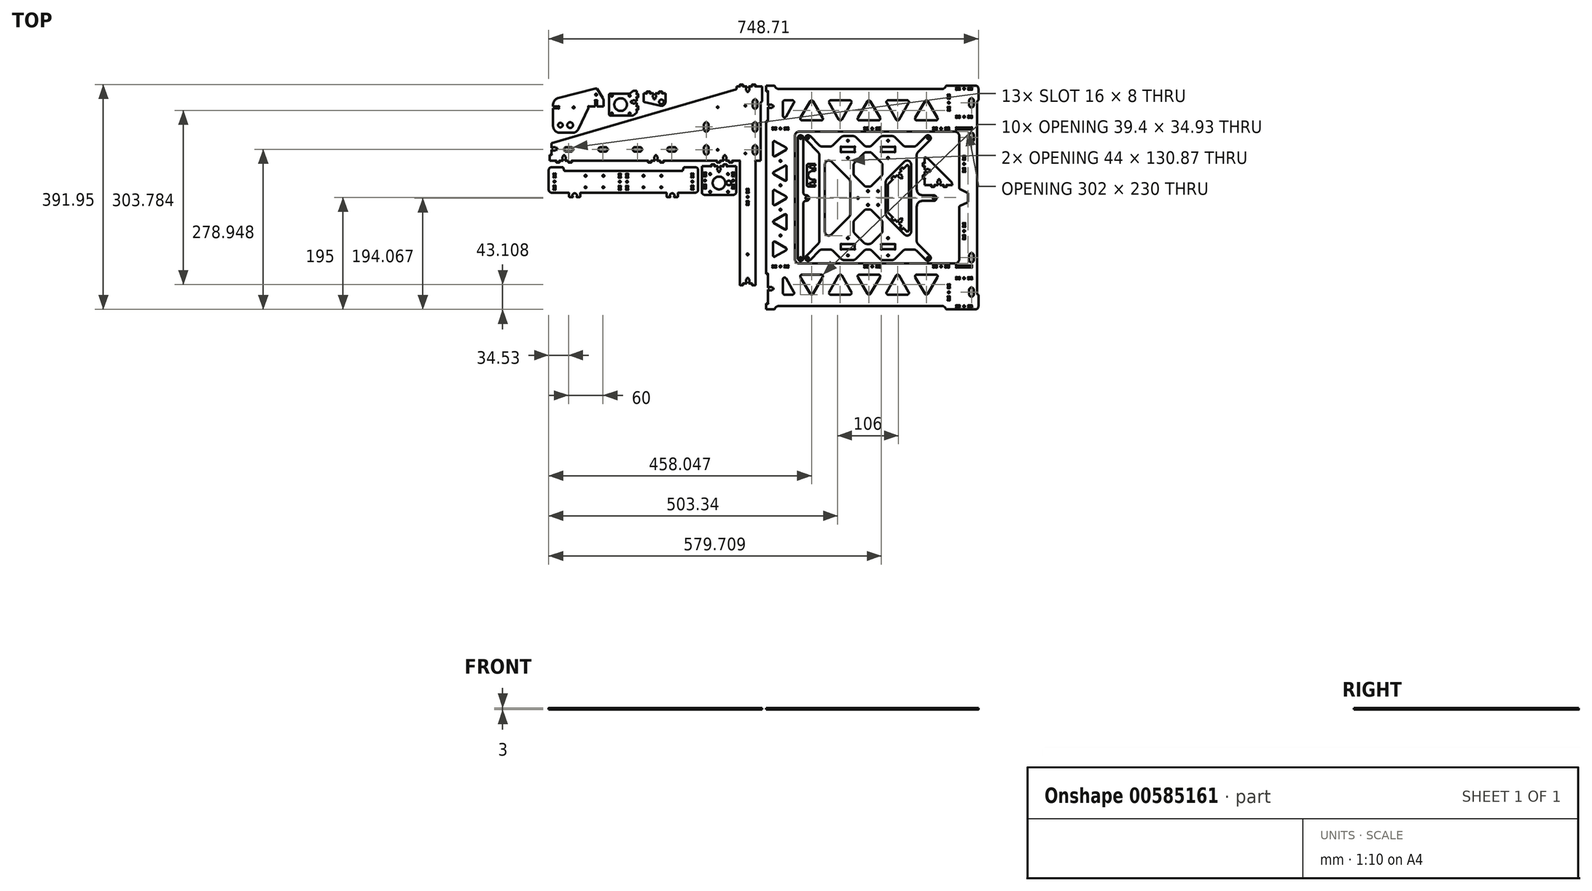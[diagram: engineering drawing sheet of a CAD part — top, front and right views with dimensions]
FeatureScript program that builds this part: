
annotation { "Feature Type Name" : "Feature", "Feature Type Description" : "" }
export const myFeature = defineFeature(function(context is Context, id is Id, definition is map)
    precondition{}
    {
        {
            assignVariable(context, id + "F0", {"name" : "thikness", "anyValue" : 3});
        }
        {
            var Q0;
            Q0=qCreatedBy(makeId("Top.planeOp"),FACE);
            var sketch = newSketch(context, id + "F1", { "sketchPlane" : qUnion([Q0])});
            skLineSegment(sketch, "E0", {"start": v(506.33, 298.49) * mm, "end": v(508.33, 300.49) * mm});
            skLineSegment(sketch, "E1", {"start": v(508.33, 300.49) * mm, "end": v(508.33, 320.49) * mm});
            skArc(sketch, "E2", {"start": v(508.33, 320.49) * mm, "mid": v(506.86, 324.03) * mm, "end": v(503.33, 325.49) * mm});
            skLineSegment(sketch, "E3", {"start": v(503.33, 325.49) * mm, "end": v(451.98, 325.49) * mm});
            skArc(sketch, "E4", {"start": v(444.23, 319.49) * mm, "mid": v(449.13, 321.17) * mm, "end": v(451.98, 325.49) * mm});
            skLineSegment(sketch, "E5", {"start": v(444.23, 319.49) * mm, "end": v(161.07, 319.49) * mm});
            skArc(sketch, "E6", {"start": v(153.33, 325.49) * mm, "mid": v(156.18, 321.17) * mm, "end": v(161.07, 319.49) * mm});
            skLineSegment(sketch, "E7", {"start": v(153.33, 325.49) * mm, "end": v(138.33, 325.49) * mm});
            skLineSegment(sketch, "E8", {"start": v(138.33, 325.49) * mm, "end": v(138.33, 315.49) * mm});
            skLineSegment(sketch, "E9", {"start": v(138.33, 315.49) * mm, "end": v(140.56, 315.49) * mm});
            skArc(sketch, "E10", {"start": v(140.56, 315.49) * mm, "mid": v(140.81, 315.56) * mm, "end": v(141, 315.74) * mm});
            skArc(sketch, "E11", {"start": v(141.68, 315.06) * mm, "mid": v(141.78, 315.84) * mm, "end": v(141, 315.74) * mm});
            skArc(sketch, "E12", {"start": v(141.68, 315.06) * mm, "mid": v(141.5, 314.87) * mm, "end": v(141.43, 314.62) * mm});
            skLineSegment(sketch, "E13", {"start": v(141.43, 314.62) * mm, "end": v(141.43, 291.26) * mm});
            skLineSegment(sketch, "E14", {"start": v(141.43, 291.26) * mm, "end": v(144.43, 291.26) * mm});
            skLineSegment(sketch, "E15", {"start": v(144.43, 291.26) * mm, "end": v(144.43, 292.54) * mm});
            skLineSegment(sketch, "E16", {"start": v(144.43, 292.54) * mm, "end": v(148.43, 292.54) * mm});
            skLineSegment(sketch, "E17", {"start": v(148.43, 292.54) * mm, "end": v(148.43, 291.26) * mm});
            skLineSegment(sketch, "E18", {"start": v(148.43, 291.26) * mm, "end": v(151.43, 291.26) * mm});
            skLineSegment(sketch, "E19", {"start": v(151.43, 291.26) * mm, "end": v(151.43, 288.06) * mm});
            skLineSegment(sketch, "E20", {"start": v(151.43, 288.06) * mm, "end": v(148.43, 288.06) * mm});
            skLineSegment(sketch, "E21", {"start": v(148.43, 288.06) * mm, "end": v(148.43, 286.79) * mm});
            skLineSegment(sketch, "E22", {"start": v(148.43, 286.79) * mm, "end": v(144.43, 286.79) * mm});
            skLineSegment(sketch, "E23", {"start": v(144.43, 286.79) * mm, "end": v(144.43, 288.06) * mm});
            skLineSegment(sketch, "E24", {"start": v(144.43, 288.06) * mm, "end": v(141.43, 288.06) * mm});
            skLineSegment(sketch, "E25", {"start": v(141.43, 288.06) * mm, "end": v(141.43, 264.7) * mm});
            skArc(sketch, "E26", {"start": v(141.43, 264.7) * mm, "mid": v(141.5, 264.46) * mm, "end": v(141.68, 264.27) * mm});
            skArc(sketch, "E27", {"start": v(141, 263.59) * mm, "mid": v(141.78, 263.49) * mm, "end": v(141.68, 264.27) * mm});
            skArc(sketch, "E28", {"start": v(141, 263.59) * mm, "mid": v(140.81, 263.77) * mm, "end": v(140.56, 263.84) * mm});
            skLineSegment(sketch, "E29", {"start": v(140.56, 263.84) * mm, "end": v(138.33, 263.84) * mm});
            skLineSegment(sketch, "E30", {"start": v(138.33, 263.84) * mm, "end": v(138.33, -2.86) * mm});
            skLineSegment(sketch, "E31", {"start": v(138.33, -2.86) * mm, "end": v(140.56, -2.86) * mm});
            skArc(sketch, "E32", {"start": v(140.56, -2.86) * mm, "mid": v(140.81, -2.8) * mm, "end": v(141, -2.61) * mm});
            skArc(sketch, "E33", {"start": v(141.68, -3.3) * mm, "mid": v(141.78, -2.5) * mm, "end": v(141, -2.61) * mm});
            skArc(sketch, "E34", {"start": v(141.68, -3.3) * mm, "mid": v(141.5, -3.48) * mm, "end": v(141.43, -3.73) * mm});
            skLineSegment(sketch, "E35", {"start": v(141.43, -3.73) * mm, "end": v(141.43, -27.09) * mm});
            skLineSegment(sketch, "E36", {"start": v(141.43, -27.09) * mm, "end": v(144.43, -27.09) * mm});
            skLineSegment(sketch, "E37", {"start": v(144.43, -27.09) * mm, "end": v(144.43, -25.81) * mm});
            skLineSegment(sketch, "E38", {"start": v(144.43, -25.81) * mm, "end": v(148.43, -25.81) * mm});
            skLineSegment(sketch, "E39", {"start": v(148.43, -25.81) * mm, "end": v(148.43, -27.09) * mm});
            skLineSegment(sketch, "E40", {"start": v(148.43, -27.09) * mm, "end": v(151.43, -27.09) * mm});
            skLineSegment(sketch, "E41", {"start": v(151.43, -27.09) * mm, "end": v(151.43, -30.29) * mm});
            skLineSegment(sketch, "E42", {"start": v(151.43, -30.29) * mm, "end": v(148.43, -30.29) * mm});
            skLineSegment(sketch, "E43", {"start": v(148.43, -30.29) * mm, "end": v(148.43, -31.56) * mm});
            skLineSegment(sketch, "E44", {"start": v(148.43, -31.56) * mm, "end": v(144.43, -31.56) * mm});
            skLineSegment(sketch, "E45", {"start": v(144.43, -31.56) * mm, "end": v(144.43, -30.29) * mm});
            skLineSegment(sketch, "E46", {"start": v(144.43, -30.29) * mm, "end": v(141.43, -30.29) * mm});
            skLineSegment(sketch, "E47", {"start": v(141.43, -30.29) * mm, "end": v(141.43, -53.64) * mm});
            skArc(sketch, "E48", {"start": v(141.43, -53.64) * mm, "mid": v(141.5, -53.9) * mm, "end": v(141.68, -54.08) * mm});
            skArc(sketch, "E49", {"start": v(141, -54.76) * mm, "mid": v(141.78, -54.86) * mm, "end": v(141.68, -54.08) * mm});
            skArc(sketch, "E50", {"start": v(141, -54.76) * mm, "mid": v(140.81, -54.58) * mm, "end": v(140.56, -54.51) * mm});
            skLineSegment(sketch, "E51", {"start": v(140.56, -54.51) * mm, "end": v(138.33, -54.51) * mm});
            skLineSegment(sketch, "E52", {"start": v(138.33, -54.51) * mm, "end": v(138.33, -64.51) * mm});
            skLineSegment(sketch, "E53", {"start": v(138.33, -64.51) * mm, "end": v(153.33, -64.51) * mm});
            skArc(sketch, "E54", {"start": v(161.07, -58.51) * mm, "mid": v(156.18, -60.19) * mm, "end": v(153.33, -64.51) * mm});
            skLineSegment(sketch, "E55", {"start": v(161.07, -58.51) * mm, "end": v(444.23, -58.51) * mm});
            skArc(sketch, "E56", {"start": v(451.98, -64.51) * mm, "mid": v(449.13, -60.19) * mm, "end": v(444.23, -58.51) * mm});
            skLineSegment(sketch, "E57", {"start": v(451.98, -64.51) * mm, "end": v(503.33, -64.51) * mm});
            skArc(sketch, "E58", {"start": v(503.33, -64.51) * mm, "mid": v(506.86, -63.05) * mm, "end": v(508.33, -59.51) * mm});
            skLineSegment(sketch, "E59", {"start": v(508.33, -59.51) * mm, "end": v(508.33, -39.51) * mm});
            skLineSegment(sketch, "E60", {"start": v(508.33, -39.51) * mm, "end": v(506.33, -37.51) * mm});
            skLineSegment(sketch, "E61", {"start": v(506.33, -37.51) * mm, "end": v(506.33, 298.49) * mm});
            skLineSegment(sketch, "E62", {"start": v(490.33, 123.77) * mm, "end": v(490.33, 137.22) * mm});
            skArc(sketch, "E63", {"start": v(490.33, 137.22) * mm, "mid": v(490.02, 138.3) * mm, "end": v(489.17, 139.03) * mm});
            skLineSegment(sketch, "E64", {"start": v(489.17, 139.03) * mm, "end": v(476.36, 145) * mm});
            skArc(sketch, "E65", {"start": v(475.2, 146.82) * mm, "mid": v(475.52, 145.74) * mm, "end": v(476.36, 145) * mm});
            skLineSegment(sketch, "E66", {"start": v(475.2, 146.82) * mm, "end": v(475.2, 237.49) * mm});
            skArc(sketch, "E67", {"start": v(475.2, 237.49) * mm, "mid": v(472.87, 243.14) * mm, "end": v(467.22, 245.49) * mm});
            skLineSegment(sketch, "E68", {"start": v(467.22, 245.49) * mm, "end": v(196.33, 245.49) * mm});
            skArc(sketch, "E69", {"start": v(196.33, 245.49) * mm, "mid": v(190.67, 243.15) * mm, "end": v(188.33, 237.49) * mm});
            skLineSegment(sketch, "E70", {"start": v(188.33, 237.49) * mm, "end": v(188.33, 23.49) * mm});
            skArc(sketch, "E71", {"start": v(188.33, 23.49) * mm, "mid": v(190.67, 17.83) * mm, "end": v(196.33, 15.49) * mm});
            skLineSegment(sketch, "E72", {"start": v(196.33, 15.49) * mm, "end": v(467.22, 15.49) * mm});
            skArc(sketch, "E73", {"start": v(467.22, 15.49) * mm, "mid": v(472.87, 17.84) * mm, "end": v(475.2, 23.49) * mm});
            skLineSegment(sketch, "E74", {"start": v(475.2, 23.49) * mm, "end": v(475.2, 114.26) * mm});
            skArc(sketch, "E75", {"start": v(476.37, 116.08) * mm, "mid": v(475.52, 115.34) * mm, "end": v(475.2, 114.26) * mm});
            skLineSegment(sketch, "E76", {"start": v(476.37, 116.08) * mm, "end": v(489.16, 121.95) * mm});
            skArc(sketch, "E77", {"start": v(489.16, 121.95) * mm, "mid": v(490.01, 122.7) * mm, "end": v(490.33, 123.77) * mm});
            skLineSegment(sketch, "E78", {"start": v(434.37, -3.94) * mm, "end": v(400.97, -3.94) * mm});
            skArc(sketch, "E79", {"start": v(400.97, -3.94) * mm, "mid": v(398.37, -5.44) * mm, "end": v(398.37, -8.44) * mm});
            skLineSegment(sketch, "E80", {"start": v(398.37, -8.44) * mm, "end": v(415.07, -37.37) * mm});
            skArc(sketch, "E81", {"start": v(415.07, -37.37) * mm, "mid": v(417.67, -38.87) * mm, "end": v(420.26, -37.37) * mm});
            skLineSegment(sketch, "E82", {"start": v(420.26, -37.37) * mm, "end": v(436.97, -8.44) * mm});
            skArc(sketch, "E83", {"start": v(436.97, -8.44) * mm, "mid": v(436.97, -5.44) * mm, "end": v(434.37, -3.94) * mm});
            skLineSegment(sketch, "E84", {"start": v(384.37, -38.87) * mm, "end": v(350.97, -38.87) * mm});
            skArc(sketch, "E85", {"start": v(348.37, -34.37) * mm, "mid": v(348.37, -37.37) * mm, "end": v(350.97, -38.87) * mm});
            skLineSegment(sketch, "E86", {"start": v(348.37, -34.37) * mm, "end": v(365.07, -5.44) * mm});
            skArc(sketch, "E87", {"start": v(370.27, -5.44) * mm, "mid": v(367.67, -3.94) * mm, "end": v(365.07, -5.44) * mm});
            skLineSegment(sketch, "E88", {"start": v(370.27, -5.44) * mm, "end": v(386.97, -34.37) * mm});
            skArc(sketch, "E89", {"start": v(384.37, -38.87) * mm, "mid": v(386.97, -37.37) * mm, "end": v(386.97, -34.37) * mm});
            skLineSegment(sketch, "E90", {"start": v(334.37, -3.94) * mm, "end": v(300.97, -3.94) * mm});
            skArc(sketch, "E91", {"start": v(300.97, -3.94) * mm, "mid": v(298.37, -5.44) * mm, "end": v(298.37, -8.44) * mm});
            skLineSegment(sketch, "E92", {"start": v(298.37, -8.44) * mm, "end": v(315.07, -37.37) * mm});
            skArc(sketch, "E93", {"start": v(315.07, -37.37) * mm, "mid": v(317.67, -38.87) * mm, "end": v(320.26, -37.37) * mm});
            skLineSegment(sketch, "E94", {"start": v(320.26, -37.37) * mm, "end": v(336.97, -8.44) * mm});
            skArc(sketch, "E95", {"start": v(336.97, -8.44) * mm, "mid": v(336.97, -5.44) * mm, "end": v(334.37, -3.94) * mm});
            skLineSegment(sketch, "E96", {"start": v(284.37, -38.87) * mm, "end": v(250.97, -38.87) * mm});
            skArc(sketch, "E97", {"start": v(248.37, -34.37) * mm, "mid": v(248.37, -37.37) * mm, "end": v(250.97, -38.87) * mm});
            skLineSegment(sketch, "E98", {"start": v(248.37, -34.37) * mm, "end": v(265.07, -5.44) * mm});
            skArc(sketch, "E99", {"start": v(270.27, -5.44) * mm, "mid": v(267.67, -3.94) * mm, "end": v(265.07, -5.44) * mm});
            skLineSegment(sketch, "E100", {"start": v(270.27, -5.44) * mm, "end": v(286.97, -34.37) * mm});
            skArc(sketch, "E101", {"start": v(284.37, -38.87) * mm, "mid": v(286.97, -37.37) * mm, "end": v(286.97, -34.37) * mm});
            skLineSegment(sketch, "E102", {"start": v(234.37, -3.94) * mm, "end": v(200.97, -3.94) * mm});
            skArc(sketch, "E103", {"start": v(200.97, -3.94) * mm, "mid": v(198.37, -5.44) * mm, "end": v(198.37, -8.44) * mm});
            skLineSegment(sketch, "E104", {"start": v(198.37, -8.44) * mm, "end": v(215.07, -37.37) * mm});
            skArc(sketch, "E105", {"start": v(215.07, -37.37) * mm, "mid": v(217.67, -38.87) * mm, "end": v(220.26, -37.37) * mm});
            skLineSegment(sketch, "E106", {"start": v(220.26, -37.37) * mm, "end": v(236.97, -8.44) * mm});
            skArc(sketch, "E107", {"start": v(236.97, -8.44) * mm, "mid": v(236.97, -5.44) * mm, "end": v(234.37, -3.94) * mm});
            skLineSegment(sketch, "E108", {"start": v(434.37, 264.92) * mm, "end": v(400.97, 264.92) * mm});
            skArc(sketch, "E109", {"start": v(398.37, 269.42) * mm, "mid": v(398.37, 266.42) * mm, "end": v(400.97, 264.92) * mm});
            skLineSegment(sketch, "E110", {"start": v(398.37, 269.42) * mm, "end": v(415.07, 298.35) * mm});
            skArc(sketch, "E111", {"start": v(420.26, 298.35) * mm, "mid": v(417.67, 299.85) * mm, "end": v(415.07, 298.35) * mm});
            skLineSegment(sketch, "E112", {"start": v(420.26, 298.35) * mm, "end": v(436.97, 269.42) * mm});
            skArc(sketch, "E113", {"start": v(434.37, 264.92) * mm, "mid": v(436.97, 266.42) * mm, "end": v(436.97, 269.42) * mm});
            skLineSegment(sketch, "E114", {"start": v(384.37, 299.85) * mm, "end": v(350.97, 299.85) * mm});
            skArc(sketch, "E115", {"start": v(350.97, 299.85) * mm, "mid": v(348.37, 298.35) * mm, "end": v(348.37, 295.35) * mm});
            skLineSegment(sketch, "E116", {"start": v(348.37, 295.35) * mm, "end": v(365.07, 266.42) * mm});
            skArc(sketch, "E117", {"start": v(365.07, 266.42) * mm, "mid": v(367.67, 264.92) * mm, "end": v(370.27, 266.42) * mm});
            skLineSegment(sketch, "E118", {"start": v(370.27, 266.42) * mm, "end": v(386.97, 295.35) * mm});
            skArc(sketch, "E119", {"start": v(386.97, 295.35) * mm, "mid": v(386.97, 298.35) * mm, "end": v(384.37, 299.85) * mm});
            skLineSegment(sketch, "E120", {"start": v(334.37, 264.92) * mm, "end": v(300.97, 264.92) * mm});
            skArc(sketch, "E121", {"start": v(298.37, 269.42) * mm, "mid": v(298.37, 266.42) * mm, "end": v(300.97, 264.92) * mm});
            skLineSegment(sketch, "E122", {"start": v(298.37, 269.42) * mm, "end": v(315.07, 298.35) * mm});
            skArc(sketch, "E123", {"start": v(320.26, 298.35) * mm, "mid": v(317.67, 299.85) * mm, "end": v(315.07, 298.35) * mm});
            skLineSegment(sketch, "E124", {"start": v(320.26, 298.35) * mm, "end": v(336.97, 269.42) * mm});
            skArc(sketch, "E125", {"start": v(334.37, 264.92) * mm, "mid": v(336.97, 266.42) * mm, "end": v(336.97, 269.42) * mm});
            skLineSegment(sketch, "E126", {"start": v(284.37, 299.85) * mm, "end": v(250.97, 299.85) * mm});
            skArc(sketch, "E127", {"start": v(250.97, 299.85) * mm, "mid": v(248.37, 298.35) * mm, "end": v(248.37, 295.35) * mm});
            skLineSegment(sketch, "E128", {"start": v(248.37, 295.35) * mm, "end": v(265.07, 266.42) * mm});
            skArc(sketch, "E129", {"start": v(265.07, 266.42) * mm, "mid": v(267.67, 264.92) * mm, "end": v(270.27, 266.42) * mm});
            skLineSegment(sketch, "E130", {"start": v(270.27, 266.42) * mm, "end": v(286.97, 295.35) * mm});
            skArc(sketch, "E131", {"start": v(286.97, 295.35) * mm, "mid": v(286.97, 298.35) * mm, "end": v(284.37, 299.85) * mm});
            skLineSegment(sketch, "E132", {"start": v(234.37, 264.92) * mm, "end": v(200.97, 264.92) * mm});
            skArc(sketch, "E133", {"start": v(198.37, 269.42) * mm, "mid": v(198.37, 266.42) * mm, "end": v(200.97, 264.92) * mm});
            skLineSegment(sketch, "E134", {"start": v(198.37, 269.42) * mm, "end": v(215.07, 298.35) * mm});
            skArc(sketch, "E135", {"start": v(220.26, 298.35) * mm, "mid": v(217.67, 299.85) * mm, "end": v(215.07, 298.35) * mm});
            skLineSegment(sketch, "E136", {"start": v(220.26, 298.35) * mm, "end": v(236.97, 269.42) * mm});
            skArc(sketch, "E137", {"start": v(234.37, 264.92) * mm, "mid": v(236.97, 266.42) * mm, "end": v(236.97, 269.42) * mm});
            skLineSegment(sketch, "E138", {"start": v(150.64, 51.7) * mm, "end": v(150.64, 29.16) * mm});
            skArc(sketch, "E139", {"start": v(150.64, 29.16) * mm, "mid": v(151.65, 27.4) * mm, "end": v(153.67, 27.4) * mm});
            skLineSegment(sketch, "E140", {"start": v(153.67, 27.4) * mm, "end": v(173.2, 38.68) * mm});
            skArc(sketch, "E141", {"start": v(173.2, 38.68) * mm, "mid": v(174.21, 40.43) * mm, "end": v(173.2, 42.19) * mm});
            skLineSegment(sketch, "E142", {"start": v(173.2, 42.19) * mm, "end": v(153.67, 53.46) * mm});
            skArc(sketch, "E143", {"start": v(153.67, 53.46) * mm, "mid": v(151.65, 53.46) * mm, "end": v(150.64, 51.7) * mm});
            skLineSegment(sketch, "E144", {"start": v(174.21, 99.25) * mm, "end": v(174.21, 76.7) * mm});
            skArc(sketch, "E145", {"start": v(171.17, 74.95) * mm, "mid": v(173.2, 74.95) * mm, "end": v(174.21, 76.7) * mm});
            skLineSegment(sketch, "E146", {"start": v(171.17, 74.95) * mm, "end": v(151.65, 86.23) * mm});
            skArc(sketch, "E147", {"start": v(151.65, 89.73) * mm, "mid": v(150.64, 87.98) * mm, "end": v(151.65, 86.23) * mm});
            skLineSegment(sketch, "E148", {"start": v(151.65, 89.73) * mm, "end": v(171.17, 101) * mm});
            skArc(sketch, "E149", {"start": v(174.21, 99.25) * mm, "mid": v(173.2, 101) * mm, "end": v(171.17, 101) * mm});
            skLineSegment(sketch, "E150", {"start": v(150.64, 141.75) * mm, "end": v(150.64, 119.2) * mm});
            skArc(sketch, "E151", {"start": v(150.64, 119.2) * mm, "mid": v(151.65, 117.45) * mm, "end": v(153.67, 117.45) * mm});
            skLineSegment(sketch, "E152", {"start": v(153.67, 117.45) * mm, "end": v(173.2, 128.73) * mm});
            skArc(sketch, "E153", {"start": v(173.2, 128.73) * mm, "mid": v(174.21, 130.48) * mm, "end": v(173.2, 132.23) * mm});
            skLineSegment(sketch, "E154", {"start": v(173.2, 132.23) * mm, "end": v(153.67, 143.5) * mm});
            skArc(sketch, "E155", {"start": v(153.67, 143.5) * mm, "mid": v(151.65, 143.5) * mm, "end": v(150.64, 141.75) * mm});
            skLineSegment(sketch, "E156", {"start": v(174.21, 184.26) * mm, "end": v(174.21, 161.72) * mm});
            skArc(sketch, "E157", {"start": v(171.17, 159.96) * mm, "mid": v(173.2, 159.96) * mm, "end": v(174.21, 161.72) * mm});
            skLineSegment(sketch, "E158", {"start": v(171.17, 159.96) * mm, "end": v(151.65, 171.24) * mm});
            skArc(sketch, "E159", {"start": v(151.65, 174.74) * mm, "mid": v(150.64, 172.99) * mm, "end": v(151.65, 171.24) * mm});
            skLineSegment(sketch, "E160", {"start": v(151.65, 174.74) * mm, "end": v(171.17, 186.02) * mm});
            skArc(sketch, "E161", {"start": v(174.21, 184.26) * mm, "mid": v(173.2, 186.02) * mm, "end": v(171.17, 186.02) * mm});
            skLineSegment(sketch, "E162", {"start": v(150.64, 226.76) * mm, "end": v(150.64, 204.22) * mm});
            skArc(sketch, "E163", {"start": v(150.64, 204.22) * mm, "mid": v(151.65, 202.46) * mm, "end": v(153.67, 202.46) * mm});
            skLineSegment(sketch, "E164", {"start": v(153.67, 202.46) * mm, "end": v(173.2, 213.74) * mm});
            skArc(sketch, "E165", {"start": v(173.2, 213.74) * mm, "mid": v(174.21, 215.49) * mm, "end": v(173.2, 217.24) * mm});
            skLineSegment(sketch, "E166", {"start": v(173.2, 217.24) * mm, "end": v(153.67, 228.52) * mm});
            skArc(sketch, "E167", {"start": v(153.67, 228.52) * mm, "mid": v(151.65, 228.52) * mm, "end": v(150.64, 226.76) * mm});
            skLineSegment(sketch, "E168", {"start": v(500.33, -38.51) * mm, "end": v(500.33, -30.51) * mm});
            skArc(sketch, "E169", {"start": v(500.33, -30.51) * mm, "mid": v(496.33, -26.51) * mm, "end": v(492.33, -30.51) * mm});
            skLineSegment(sketch, "E170", {"start": v(492.33, -30.51) * mm, "end": v(492.33, -38.51) * mm});
            skArc(sketch, "E171", {"start": v(492.33, -38.51) * mm, "mid": v(496.33, -42.51) * mm, "end": v(500.33, -38.51) * mm});
            skLineSegment(sketch, "E172", {"start": v(500.33, 21.49) * mm, "end": v(500.33, 29.49) * mm});
            skArc(sketch, "E173", {"start": v(500.33, 29.49) * mm, "mid": v(496.33, 33.49) * mm, "end": v(492.33, 29.49) * mm});
            skLineSegment(sketch, "E174", {"start": v(492.33, 29.49) * mm, "end": v(492.33, 21.49) * mm});
            skArc(sketch, "E175", {"start": v(492.33, 21.49) * mm, "mid": v(496.33, 17.49) * mm, "end": v(500.33, 21.49) * mm});
            skLineSegment(sketch, "E176", {"start": v(500.33, 231.49) * mm, "end": v(500.33, 239.49) * mm});
            skArc(sketch, "E177", {"start": v(500.33, 239.49) * mm, "mid": v(496.33, 243.49) * mm, "end": v(492.33, 239.49) * mm});
            skLineSegment(sketch, "E178", {"start": v(492.33, 239.49) * mm, "end": v(492.33, 231.49) * mm});
            skArc(sketch, "E179", {"start": v(492.33, 231.49) * mm, "mid": v(496.33, 227.49) * mm, "end": v(500.33, 231.49) * mm});
            skLineSegment(sketch, "E180", {"start": v(500.33, 291.49) * mm, "end": v(500.33, 299.49) * mm});
            skArc(sketch, "E181", {"start": v(500.33, 299.49) * mm, "mid": v(496.33, 303.49) * mm, "end": v(492.33, 299.49) * mm});
            skLineSegment(sketch, "E182", {"start": v(492.33, 299.49) * mm, "end": v(492.33, 291.49) * mm});
            skArc(sketch, "E183", {"start": v(492.33, 291.49) * mm, "mid": v(496.33, 287.49) * mm, "end": v(500.33, 291.49) * mm});
            skArc(sketch, "E184", {"start": v(469.63, 11.1) * mm, "mid": v(469.56, 11.35) * mm, "end": v(469.38, 11.53) * mm});
            skArc(sketch, "E185", {"start": v(470.06, 12.21) * mm, "mid": v(469.28, 12.32) * mm, "end": v(469.38, 11.53) * mm});
            skArc(sketch, "E186", {"start": v(470.06, 12.21) * mm, "mid": v(470.24, 12.03) * mm, "end": v(470.5, 11.96) * mm});
            skLineSegment(sketch, "E187", {"start": v(470.5, 11.96) * mm, "end": v(496.16, 11.96) * mm});
            skArc(sketch, "E188", {"start": v(496.16, 11.96) * mm, "mid": v(496.41, 12.03) * mm, "end": v(496.6, 12.21) * mm});
            skArc(sketch, "E189", {"start": v(497.28, 11.53) * mm, "mid": v(497.38, 12.32) * mm, "end": v(496.6, 12.21) * mm});
            skArc(sketch, "E190", {"start": v(497.28, 11.53) * mm, "mid": v(497.1, 11.35) * mm, "end": v(497.03, 11.1) * mm});
            skLineSegment(sketch, "E191", {"start": v(497.03, 11.1) * mm, "end": v(497.03, 9.53) * mm});
            skArc(sketch, "E192", {"start": v(497.03, 9.53) * mm, "mid": v(497.1, 9.28) * mm, "end": v(497.28, 9.1) * mm});
            skArc(sketch, "E193", {"start": v(496.6, 8.41) * mm, "mid": v(497.38, 8.31) * mm, "end": v(497.28, 9.1) * mm});
            skArc(sketch, "E194", {"start": v(496.6, 8.41) * mm, "mid": v(496.41, 8.6) * mm, "end": v(496.16, 8.66) * mm});
            skLineSegment(sketch, "E195", {"start": v(496.16, 8.66) * mm, "end": v(470.5, 8.66) * mm});
            skArc(sketch, "E196", {"start": v(470.5, 8.66) * mm, "mid": v(470.24, 8.6) * mm, "end": v(470.06, 8.41) * mm});
            skArc(sketch, "E197", {"start": v(469.38, 9.1) * mm, "mid": v(469.28, 8.31) * mm, "end": v(470.06, 8.41) * mm});
            skArc(sketch, "E198", {"start": v(469.38, 9.1) * mm, "mid": v(469.56, 9.28) * mm, "end": v(469.63, 9.53) * mm});
            skLineSegment(sketch, "E199", {"start": v(469.63, 9.53) * mm, "end": v(469.63, 11.1) * mm});
            skArc(sketch, "E200", {"start": v(469.63, 251.45) * mm, "mid": v(469.56, 251.7) * mm, "end": v(469.38, 251.88) * mm});
            skArc(sketch, "E201", {"start": v(470.06, 252.56) * mm, "mid": v(469.28, 252.67) * mm, "end": v(469.38, 251.88) * mm});
            skArc(sketch, "E202", {"start": v(470.06, 252.56) * mm, "mid": v(470.24, 252.38) * mm, "end": v(470.5, 252.31) * mm});
            skLineSegment(sketch, "E203", {"start": v(470.5, 252.31) * mm, "end": v(496.16, 252.31) * mm});
            skArc(sketch, "E204", {"start": v(496.16, 252.31) * mm, "mid": v(496.41, 252.38) * mm, "end": v(496.6, 252.56) * mm});
            skArc(sketch, "E205", {"start": v(497.28, 251.88) * mm, "mid": v(497.38, 252.67) * mm, "end": v(496.6, 252.56) * mm});
            skArc(sketch, "E206", {"start": v(497.28, 251.88) * mm, "mid": v(497.1, 251.7) * mm, "end": v(497.03, 251.45) * mm});
            skLineSegment(sketch, "E207", {"start": v(497.03, 251.45) * mm, "end": v(497.03, 249.88) * mm});
            skArc(sketch, "E208", {"start": v(497.03, 249.88) * mm, "mid": v(497.1, 249.63) * mm, "end": v(497.28, 249.45) * mm});
            skArc(sketch, "E209", {"start": v(496.6, 248.76) * mm, "mid": v(497.38, 248.66) * mm, "end": v(497.28, 249.45) * mm});
            skArc(sketch, "E210", {"start": v(496.6, 248.76) * mm, "mid": v(496.41, 248.95) * mm, "end": v(496.16, 249.01) * mm});
            skLineSegment(sketch, "E211", {"start": v(496.16, 249.01) * mm, "end": v(470.5, 249.01) * mm});
            skArc(sketch, "E212", {"start": v(470.5, 249.01) * mm, "mid": v(470.24, 248.95) * mm, "end": v(470.06, 248.76) * mm});
            skArc(sketch, "E213", {"start": v(469.38, 249.45) * mm, "mid": v(469.28, 248.66) * mm, "end": v(470.06, 248.76) * mm});
            skArc(sketch, "E214", {"start": v(469.38, 249.45) * mm, "mid": v(469.56, 249.63) * mm, "end": v(469.63, 249.88) * mm});
            skLineSegment(sketch, "E215", {"start": v(469.63, 249.88) * mm, "end": v(469.63, 251.45) * mm});
            skArc(sketch, "E216", {"start": v(490.83, -58.55) * mm, "mid": v(490.76, -58.3) * mm, "end": v(490.58, -58.11) * mm});
            skArc(sketch, "E217", {"start": v(491.26, -57.43) * mm, "mid": v(490.48, -57.33) * mm, "end": v(490.58, -58.11) * mm});
            skArc(sketch, "E218", {"start": v(491.26, -57.43) * mm, "mid": v(491.44, -57.61) * mm, "end": v(491.7, -57.68) * mm});
            skLineSegment(sketch, "E219", {"start": v(491.7, -57.68) * mm, "end": v(496.16, -57.68) * mm});
            skArc(sketch, "E220", {"start": v(496.16, -57.68) * mm, "mid": v(496.41, -57.61) * mm, "end": v(496.6, -57.43) * mm});
            skArc(sketch, "E221", {"start": v(497.28, -58.11) * mm, "mid": v(497.38, -57.33) * mm, "end": v(496.6, -57.43) * mm});
            skArc(sketch, "E222", {"start": v(497.28, -58.11) * mm, "mid": v(497.1, -58.3) * mm, "end": v(497.03, -58.55) * mm});
            skLineSegment(sketch, "E223", {"start": v(497.03, -58.55) * mm, "end": v(497.03, -60.11) * mm});
            skArc(sketch, "E224", {"start": v(497.03, -60.11) * mm, "mid": v(497.1, -60.36) * mm, "end": v(497.28, -60.55) * mm});
            skArc(sketch, "E225", {"start": v(496.6, -61.23) * mm, "mid": v(497.38, -61.33) * mm, "end": v(497.28, -60.55) * mm});
            skArc(sketch, "E226", {"start": v(496.6, -61.23) * mm, "mid": v(496.41, -61.05) * mm, "end": v(496.16, -60.98) * mm});
            skLineSegment(sketch, "E227", {"start": v(496.16, -60.98) * mm, "end": v(491.7, -60.98) * mm});
            skArc(sketch, "E228", {"start": v(491.7, -60.98) * mm, "mid": v(491.44, -61.05) * mm, "end": v(491.26, -61.23) * mm});
            skArc(sketch, "E229", {"start": v(490.58, -60.55) * mm, "mid": v(490.48, -61.33) * mm, "end": v(491.26, -61.23) * mm});
            skArc(sketch, "E230", {"start": v(490.58, -60.55) * mm, "mid": v(490.76, -60.36) * mm, "end": v(490.83, -60.11) * mm});
            skLineSegment(sketch, "E231", {"start": v(490.83, -60.11) * mm, "end": v(490.83, -58.55) * mm});
            skArc(sketch, "E232", {"start": v(469.63, -58.55) * mm, "mid": v(469.56, -58.3) * mm, "end": v(469.38, -58.11) * mm});
            skArc(sketch, "E233", {"start": v(470.06, -57.43) * mm, "mid": v(469.28, -57.33) * mm, "end": v(469.38, -58.11) * mm});
            skArc(sketch, "E234", {"start": v(470.06, -57.43) * mm, "mid": v(470.24, -57.61) * mm, "end": v(470.5, -57.68) * mm});
            skLineSegment(sketch, "E235", {"start": v(470.5, -57.68) * mm, "end": v(474.96, -57.68) * mm});
            skArc(sketch, "E236", {"start": v(474.96, -57.68) * mm, "mid": v(475.21, -57.61) * mm, "end": v(475.4, -57.43) * mm});
            skArc(sketch, "E237", {"start": v(476.08, -58.11) * mm, "mid": v(476.18, -57.33) * mm, "end": v(475.4, -57.43) * mm});
            skArc(sketch, "E238", {"start": v(476.08, -58.11) * mm, "mid": v(475.9, -58.3) * mm, "end": v(475.83, -58.55) * mm});
            skLineSegment(sketch, "E239", {"start": v(475.83, -58.55) * mm, "end": v(475.83, -60.11) * mm});
            skArc(sketch, "E240", {"start": v(475.83, -60.11) * mm, "mid": v(475.9, -60.36) * mm, "end": v(476.08, -60.55) * mm});
            skArc(sketch, "E241", {"start": v(475.4, -61.23) * mm, "mid": v(476.18, -61.33) * mm, "end": v(476.08, -60.55) * mm});
            skArc(sketch, "E242", {"start": v(475.4, -61.23) * mm, "mid": v(475.21, -61.05) * mm, "end": v(474.96, -60.98) * mm});
            skLineSegment(sketch, "E243", {"start": v(474.96, -60.98) * mm, "end": v(470.5, -60.98) * mm});
            skArc(sketch, "E244", {"start": v(470.5, -60.98) * mm, "mid": v(470.24, -61.05) * mm, "end": v(470.06, -61.23) * mm});
            skArc(sketch, "E245", {"start": v(469.38, -60.55) * mm, "mid": v(469.28, -61.33) * mm, "end": v(470.06, -61.23) * mm});
            skArc(sketch, "E246", {"start": v(469.38, -60.55) * mm, "mid": v(469.56, -60.36) * mm, "end": v(469.63, -60.11) * mm});
            skLineSegment(sketch, "E247", {"start": v(469.63, -60.11) * mm, "end": v(469.63, -58.55) * mm});
            skArc(sketch, "E248", {"start": v(455.9, -48.51) * mm, "mid": v(455.65, -48.58) * mm, "end": v(455.47, -48.76) * mm});
            skArc(sketch, "E249", {"start": v(454.78, -48.08) * mm, "mid": v(454.68, -48.86) * mm, "end": v(455.47, -48.76) * mm});
            skArc(sketch, "E250", {"start": v(454.78, -48.08) * mm, "mid": v(454.97, -47.9) * mm, "end": v(455.03, -47.64) * mm});
            skLineSegment(sketch, "E251", {"start": v(455.03, -47.64) * mm, "end": v(455.03, -43.18) * mm});
            skArc(sketch, "E252", {"start": v(455.03, -43.18) * mm, "mid": v(454.97, -42.93) * mm, "end": v(454.78, -42.74) * mm});
            skArc(sketch, "E253", {"start": v(455.47, -42.06) * mm, "mid": v(454.68, -41.96) * mm, "end": v(454.78, -42.74) * mm});
            skArc(sketch, "E254", {"start": v(455.47, -42.06) * mm, "mid": v(455.65, -42.24) * mm, "end": v(455.9, -42.31) * mm});
            skLineSegment(sketch, "E255", {"start": v(455.9, -42.31) * mm, "end": v(457.47, -42.31) * mm});
            skArc(sketch, "E256", {"start": v(457.47, -42.31) * mm, "mid": v(457.72, -42.24) * mm, "end": v(457.9, -42.06) * mm});
            skArc(sketch, "E257", {"start": v(458.58, -42.74) * mm, "mid": v(458.69, -41.96) * mm, "end": v(457.9, -42.06) * mm});
            skArc(sketch, "E258", {"start": v(458.58, -42.74) * mm, "mid": v(458.4, -42.93) * mm, "end": v(458.33, -43.18) * mm});
            skLineSegment(sketch, "E259", {"start": v(458.33, -43.18) * mm, "end": v(458.33, -47.64) * mm});
            skArc(sketch, "E260", {"start": v(458.33, -47.64) * mm, "mid": v(458.4, -47.9) * mm, "end": v(458.58, -48.08) * mm});
            skArc(sketch, "E261", {"start": v(457.9, -48.76) * mm, "mid": v(458.69, -48.86) * mm, "end": v(458.58, -48.08) * mm});
            skArc(sketch, "E262", {"start": v(457.9, -48.76) * mm, "mid": v(457.72, -48.58) * mm, "end": v(457.47, -48.51) * mm});
            skLineSegment(sketch, "E263", {"start": v(457.47, -48.51) * mm, "end": v(455.9, -48.51) * mm});
            skArc(sketch, "E264", {"start": v(455.9, -27.31) * mm, "mid": v(455.65, -27.38) * mm, "end": v(455.47, -27.56) * mm});
            skArc(sketch, "E265", {"start": v(454.78, -26.88) * mm, "mid": v(454.68, -27.66) * mm, "end": v(455.47, -27.56) * mm});
            skArc(sketch, "E266", {"start": v(454.78, -26.88) * mm, "mid": v(454.97, -26.7) * mm, "end": v(455.03, -26.44) * mm});
            skLineSegment(sketch, "E267", {"start": v(455.03, -26.44) * mm, "end": v(455.03, -21.98) * mm});
            skArc(sketch, "E268", {"start": v(455.03, -21.98) * mm, "mid": v(454.97, -21.73) * mm, "end": v(454.78, -21.54) * mm});
            skArc(sketch, "E269", {"start": v(455.47, -20.86) * mm, "mid": v(454.68, -20.76) * mm, "end": v(454.78, -21.54) * mm});
            skArc(sketch, "E270", {"start": v(455.47, -20.86) * mm, "mid": v(455.65, -21.04) * mm, "end": v(455.9, -21.11) * mm});
            skLineSegment(sketch, "E271", {"start": v(455.9, -21.11) * mm, "end": v(457.47, -21.11) * mm});
            skArc(sketch, "E272", {"start": v(457.47, -21.11) * mm, "mid": v(457.72, -21.04) * mm, "end": v(457.9, -20.86) * mm});
            skArc(sketch, "E273", {"start": v(458.58, -21.54) * mm, "mid": v(458.69, -20.76) * mm, "end": v(457.9, -20.86) * mm});
            skArc(sketch, "E274", {"start": v(458.58, -21.54) * mm, "mid": v(458.4, -21.73) * mm, "end": v(458.33, -21.98) * mm});
            skLineSegment(sketch, "E275", {"start": v(458.33, -21.98) * mm, "end": v(458.33, -26.44) * mm});
            skArc(sketch, "E276", {"start": v(458.33, -26.44) * mm, "mid": v(458.4, -26.7) * mm, "end": v(458.58, -26.88) * mm});
            skArc(sketch, "E277", {"start": v(457.9, -27.56) * mm, "mid": v(458.69, -27.66) * mm, "end": v(458.58, -26.88) * mm});
            skArc(sketch, "E278", {"start": v(457.9, -27.56) * mm, "mid": v(457.72, -27.38) * mm, "end": v(457.47, -27.31) * mm});
            skLineSegment(sketch, "E279", {"start": v(457.47, -27.31) * mm, "end": v(455.9, -27.31) * mm});
            skArc(sketch, "E280", {"start": v(490.83, -9.5) * mm, "mid": v(490.76, -9.26) * mm, "end": v(490.58, -9.07) * mm});
            skArc(sketch, "E281", {"start": v(491.26, -8.4) * mm, "mid": v(490.48, -8.29) * mm, "end": v(490.58, -9.07) * mm});
            skArc(sketch, "E282", {"start": v(491.26, -8.4) * mm, "mid": v(491.44, -8.57) * mm, "end": v(491.7, -8.64) * mm});
            skLineSegment(sketch, "E283", {"start": v(491.7, -8.64) * mm, "end": v(496.16, -8.64) * mm});
            skArc(sketch, "E284", {"start": v(496.16, -8.64) * mm, "mid": v(496.41, -8.57) * mm, "end": v(496.6, -8.4) * mm});
            skArc(sketch, "E285", {"start": v(497.28, -9.07) * mm, "mid": v(497.38, -8.29) * mm, "end": v(496.6, -8.4) * mm});
            skArc(sketch, "E286", {"start": v(497.28, -9.07) * mm, "mid": v(497.1, -9.26) * mm, "end": v(497.03, -9.5) * mm});
            skLineSegment(sketch, "E287", {"start": v(497.03, -9.5) * mm, "end": v(497.03, -11.07) * mm});
            skArc(sketch, "E288", {"start": v(497.03, -11.07) * mm, "mid": v(497.1, -11.32) * mm, "end": v(497.28, -11.5) * mm});
            skArc(sketch, "E289", {"start": v(496.6, -12.2) * mm, "mid": v(497.38, -12.3) * mm, "end": v(497.28, -11.5) * mm});
            skArc(sketch, "E290", {"start": v(496.6, -12.2) * mm, "mid": v(496.41, -12) * mm, "end": v(496.16, -11.94) * mm});
            skLineSegment(sketch, "E291", {"start": v(496.16, -11.94) * mm, "end": v(491.7, -11.94) * mm});
            skArc(sketch, "E292", {"start": v(491.7, -11.94) * mm, "mid": v(491.44, -12) * mm, "end": v(491.26, -12.2) * mm});
            skArc(sketch, "E293", {"start": v(490.58, -11.5) * mm, "mid": v(490.48, -12.3) * mm, "end": v(491.26, -12.2) * mm});
            skArc(sketch, "E294", {"start": v(490.58, -11.5) * mm, "mid": v(490.76, -11.32) * mm, "end": v(490.83, -11.07) * mm});
            skLineSegment(sketch, "E295", {"start": v(490.83, -11.07) * mm, "end": v(490.83, -9.5) * mm});
            skArc(sketch, "E296", {"start": v(469.63, -9.5) * mm, "mid": v(469.56, -9.26) * mm, "end": v(469.38, -9.07) * mm});
            skArc(sketch, "E297", {"start": v(470.06, -8.4) * mm, "mid": v(469.28, -8.29) * mm, "end": v(469.38, -9.07) * mm});
            skArc(sketch, "E298", {"start": v(470.06, -8.4) * mm, "mid": v(470.24, -8.57) * mm, "end": v(470.5, -8.64) * mm});
            skLineSegment(sketch, "E299", {"start": v(470.5, -8.64) * mm, "end": v(474.96, -8.64) * mm});
            skArc(sketch, "E300", {"start": v(474.96, -8.64) * mm, "mid": v(475.21, -8.57) * mm, "end": v(475.4, -8.4) * mm});
            skArc(sketch, "E301", {"start": v(476.08, -9.07) * mm, "mid": v(476.18, -8.29) * mm, "end": v(475.4, -8.4) * mm});
            skArc(sketch, "E302", {"start": v(476.08, -9.07) * mm, "mid": v(475.9, -9.26) * mm, "end": v(475.83, -9.5) * mm});
            skLineSegment(sketch, "E303", {"start": v(475.83, -9.5) * mm, "end": v(475.83, -11.07) * mm});
            skArc(sketch, "E304", {"start": v(475.83, -11.07) * mm, "mid": v(475.9, -11.32) * mm, "end": v(476.08, -11.5) * mm});
            skArc(sketch, "E305", {"start": v(475.4, -12.2) * mm, "mid": v(476.18, -12.3) * mm, "end": v(476.08, -11.5) * mm});
            skArc(sketch, "E306", {"start": v(475.4, -12.2) * mm, "mid": v(475.21, -12) * mm, "end": v(474.96, -11.94) * mm});
            skLineSegment(sketch, "E307", {"start": v(474.96, -11.94) * mm, "end": v(470.5, -11.94) * mm});
            skArc(sketch, "E308", {"start": v(470.5, -11.94) * mm, "mid": v(470.24, -12) * mm, "end": v(470.06, -12.2) * mm});
            skArc(sketch, "E309", {"start": v(469.38, -11.5) * mm, "mid": v(469.28, -12.3) * mm, "end": v(470.06, -12.2) * mm});
            skArc(sketch, "E310", {"start": v(469.38, -11.5) * mm, "mid": v(469.56, -11.32) * mm, "end": v(469.63, -11.07) * mm});
            skLineSegment(sketch, "E311", {"start": v(469.63, -11.07) * mm, "end": v(469.63, -9.5) * mm});
            skArc(sketch, "E312", {"start": v(450.58, 9.1) * mm, "mid": v(450.76, 9.28) * mm, "end": v(450.83, 9.53) * mm});
            skArc(sketch, "E313", {"start": v(450.58, 9.1) * mm, "mid": v(450.48, 8.31) * mm, "end": v(451.26, 8.41) * mm});
            skArc(sketch, "E314", {"start": v(451.7, 8.66) * mm, "mid": v(451.44, 8.6) * mm, "end": v(451.26, 8.41) * mm});
            skLineSegment(sketch, "E315", {"start": v(451.7, 8.66) * mm, "end": v(456.16, 8.66) * mm});
            skArc(sketch, "E316", {"start": v(456.6, 8.41) * mm, "mid": v(456.41, 8.6) * mm, "end": v(456.16, 8.66) * mm});
            skArc(sketch, "E317", {"start": v(456.6, 8.41) * mm, "mid": v(457.38, 8.31) * mm, "end": v(457.28, 9.1) * mm});
            skArc(sketch, "E318", {"start": v(457.03, 9.53) * mm, "mid": v(457.1, 9.28) * mm, "end": v(457.28, 9.1) * mm});
            skLineSegment(sketch, "E319", {"start": v(457.03, 9.53) * mm, "end": v(457.03, 11.1) * mm});
            skArc(sketch, "E320", {"start": v(457.28, 11.53) * mm, "mid": v(457.1, 11.35) * mm, "end": v(457.03, 11.1) * mm});
            skArc(sketch, "E321", {"start": v(457.28, 11.53) * mm, "mid": v(457.38, 12.32) * mm, "end": v(456.6, 12.21) * mm});
            skArc(sketch, "E322", {"start": v(456.16, 11.96) * mm, "mid": v(456.41, 12.03) * mm, "end": v(456.6, 12.21) * mm});
            skLineSegment(sketch, "E323", {"start": v(456.16, 11.96) * mm, "end": v(451.7, 11.96) * mm});
            skArc(sketch, "E324", {"start": v(451.26, 12.21) * mm, "mid": v(451.44, 12.03) * mm, "end": v(451.7, 11.96) * mm});
            skArc(sketch, "E325", {"start": v(451.26, 12.21) * mm, "mid": v(450.48, 12.32) * mm, "end": v(450.58, 11.53) * mm});
            skArc(sketch, "E326", {"start": v(450.83, 11.1) * mm, "mid": v(450.76, 11.35) * mm, "end": v(450.58, 11.53) * mm});
            skLineSegment(sketch, "E327", {"start": v(450.83, 11.1) * mm, "end": v(450.83, 9.53) * mm});
            skArc(sketch, "E328", {"start": v(429.38, 9.1) * mm, "mid": v(429.56, 9.28) * mm, "end": v(429.63, 9.53) * mm});
            skArc(sketch, "E329", {"start": v(429.38, 9.1) * mm, "mid": v(429.28, 8.31) * mm, "end": v(430.06, 8.41) * mm});
            skArc(sketch, "E330", {"start": v(430.5, 8.66) * mm, "mid": v(430.24, 8.6) * mm, "end": v(430.06, 8.41) * mm});
            skLineSegment(sketch, "E331", {"start": v(430.5, 8.66) * mm, "end": v(434.96, 8.66) * mm});
            skArc(sketch, "E332", {"start": v(435.4, 8.41) * mm, "mid": v(435.21, 8.6) * mm, "end": v(434.96, 8.66) * mm});
            skArc(sketch, "E333", {"start": v(435.4, 8.41) * mm, "mid": v(436.18, 8.31) * mm, "end": v(436.08, 9.1) * mm});
            skArc(sketch, "E334", {"start": v(435.83, 9.53) * mm, "mid": v(435.9, 9.28) * mm, "end": v(436.08, 9.1) * mm});
            skLineSegment(sketch, "E335", {"start": v(435.83, 9.53) * mm, "end": v(435.83, 11.1) * mm});
            skArc(sketch, "E336", {"start": v(436.08, 11.53) * mm, "mid": v(435.9, 11.35) * mm, "end": v(435.83, 11.1) * mm});
            skArc(sketch, "E337", {"start": v(436.08, 11.53) * mm, "mid": v(436.18, 12.32) * mm, "end": v(435.4, 12.21) * mm});
            skArc(sketch, "E338", {"start": v(434.96, 11.96) * mm, "mid": v(435.21, 12.03) * mm, "end": v(435.4, 12.21) * mm});
            skLineSegment(sketch, "E339", {"start": v(434.96, 11.96) * mm, "end": v(430.5, 11.96) * mm});
            skArc(sketch, "E340", {"start": v(430.06, 12.21) * mm, "mid": v(430.24, 12.03) * mm, "end": v(430.5, 11.96) * mm});
            skArc(sketch, "E341", {"start": v(430.06, 12.21) * mm, "mid": v(429.28, 12.32) * mm, "end": v(429.38, 11.53) * mm});
            skArc(sketch, "E342", {"start": v(429.63, 11.1) * mm, "mid": v(429.56, 11.35) * mm, "end": v(429.38, 11.53) * mm});
            skLineSegment(sketch, "E343", {"start": v(429.63, 11.1) * mm, "end": v(429.63, 9.53) * mm});
            skArc(sketch, "E344", {"start": v(330.83, 11.1) * mm, "mid": v(330.76, 11.35) * mm, "end": v(330.58, 11.53) * mm});
            skArc(sketch, "E345", {"start": v(331.26, 12.21) * mm, "mid": v(330.48, 12.32) * mm, "end": v(330.58, 11.53) * mm});
            skArc(sketch, "E346", {"start": v(331.26, 12.21) * mm, "mid": v(331.44, 12.03) * mm, "end": v(331.7, 11.96) * mm});
            skLineSegment(sketch, "E347", {"start": v(331.7, 11.96) * mm, "end": v(336.16, 11.96) * mm});
            skArc(sketch, "E348", {"start": v(336.16, 11.96) * mm, "mid": v(336.41, 12.03) * mm, "end": v(336.6, 12.21) * mm});
            skArc(sketch, "E349", {"start": v(337.28, 11.53) * mm, "mid": v(337.38, 12.32) * mm, "end": v(336.6, 12.21) * mm});
            skArc(sketch, "E350", {"start": v(337.28, 11.53) * mm, "mid": v(337.1, 11.35) * mm, "end": v(337.03, 11.1) * mm});
            skLineSegment(sketch, "E351", {"start": v(337.03, 11.1) * mm, "end": v(337.03, 9.53) * mm});
            skArc(sketch, "E352", {"start": v(337.03, 9.53) * mm, "mid": v(337.1, 9.28) * mm, "end": v(337.28, 9.1) * mm});
            skArc(sketch, "E353", {"start": v(336.6, 8.41) * mm, "mid": v(337.38, 8.31) * mm, "end": v(337.28, 9.1) * mm});
            skArc(sketch, "E354", {"start": v(336.6, 8.41) * mm, "mid": v(336.41, 8.6) * mm, "end": v(336.16, 8.66) * mm});
            skLineSegment(sketch, "E355", {"start": v(336.16, 8.66) * mm, "end": v(331.7, 8.66) * mm});
            skArc(sketch, "E356", {"start": v(331.7, 8.66) * mm, "mid": v(331.44, 8.6) * mm, "end": v(331.26, 8.41) * mm});
            skArc(sketch, "E357", {"start": v(330.58, 9.1) * mm, "mid": v(330.48, 8.31) * mm, "end": v(331.26, 8.41) * mm});
            skArc(sketch, "E358", {"start": v(330.58, 9.1) * mm, "mid": v(330.76, 9.28) * mm, "end": v(330.83, 9.53) * mm});
            skLineSegment(sketch, "E359", {"start": v(330.83, 9.53) * mm, "end": v(330.83, 11.1) * mm});
            skArc(sketch, "E360", {"start": v(309.63, 11.1) * mm, "mid": v(309.56, 11.35) * mm, "end": v(309.38, 11.53) * mm});
            skArc(sketch, "E361", {"start": v(310.06, 12.21) * mm, "mid": v(309.28, 12.32) * mm, "end": v(309.38, 11.53) * mm});
            skArc(sketch, "E362", {"start": v(310.06, 12.21) * mm, "mid": v(310.24, 12.03) * mm, "end": v(310.5, 11.96) * mm});
            skLineSegment(sketch, "E363", {"start": v(310.5, 11.96) * mm, "end": v(314.96, 11.96) * mm});
            skArc(sketch, "E364", {"start": v(314.96, 11.96) * mm, "mid": v(315.21, 12.03) * mm, "end": v(315.4, 12.21) * mm});
            skArc(sketch, "E365", {"start": v(316.08, 11.53) * mm, "mid": v(316.18, 12.32) * mm, "end": v(315.4, 12.21) * mm});
            skArc(sketch, "E366", {"start": v(316.08, 11.53) * mm, "mid": v(315.9, 11.35) * mm, "end": v(315.83, 11.1) * mm});
            skLineSegment(sketch, "E367", {"start": v(315.83, 11.1) * mm, "end": v(315.83, 9.53) * mm});
            skArc(sketch, "E368", {"start": v(315.83, 9.53) * mm, "mid": v(315.9, 9.28) * mm, "end": v(316.08, 9.1) * mm});
            skArc(sketch, "E369", {"start": v(315.4, 8.41) * mm, "mid": v(316.18, 8.31) * mm, "end": v(316.08, 9.1) * mm});
            skArc(sketch, "E370", {"start": v(315.4, 8.41) * mm, "mid": v(315.21, 8.6) * mm, "end": v(314.96, 8.66) * mm});
            skLineSegment(sketch, "E371", {"start": v(314.96, 8.66) * mm, "end": v(310.5, 8.66) * mm});
            skArc(sketch, "E372", {"start": v(310.5, 8.66) * mm, "mid": v(310.24, 8.6) * mm, "end": v(310.06, 8.41) * mm});
            skArc(sketch, "E373", {"start": v(309.38, 9.1) * mm, "mid": v(309.28, 8.31) * mm, "end": v(310.06, 8.41) * mm});
            skArc(sketch, "E374", {"start": v(309.38, 9.1) * mm, "mid": v(309.56, 9.28) * mm, "end": v(309.63, 9.53) * mm});
            skLineSegment(sketch, "E375", {"start": v(309.63, 9.53) * mm, "end": v(309.63, 11.1) * mm});
            skArc(sketch, "E376", {"start": v(170.83, 11.1) * mm, "mid": v(170.76, 11.35) * mm, "end": v(170.58, 11.53) * mm});
            skArc(sketch, "E377", {"start": v(171.26, 12.21) * mm, "mid": v(170.48, 12.32) * mm, "end": v(170.58, 11.53) * mm});
            skArc(sketch, "E378", {"start": v(171.26, 12.21) * mm, "mid": v(171.44, 12.03) * mm, "end": v(171.7, 11.96) * mm});
            skLineSegment(sketch, "E379", {"start": v(171.7, 11.96) * mm, "end": v(176.16, 11.96) * mm});
            skArc(sketch, "E380", {"start": v(176.16, 11.96) * mm, "mid": v(176.41, 12.03) * mm, "end": v(176.6, 12.21) * mm});
            skArc(sketch, "E381", {"start": v(177.28, 11.53) * mm, "mid": v(177.38, 12.32) * mm, "end": v(176.6, 12.21) * mm});
            skArc(sketch, "E382", {"start": v(177.28, 11.53) * mm, "mid": v(177.1, 11.35) * mm, "end": v(177.03, 11.1) * mm});
            skLineSegment(sketch, "E383", {"start": v(177.03, 11.1) * mm, "end": v(177.03, 9.53) * mm});
            skArc(sketch, "E384", {"start": v(177.03, 9.53) * mm, "mid": v(177.1, 9.28) * mm, "end": v(177.28, 9.1) * mm});
            skArc(sketch, "E385", {"start": v(176.6, 8.41) * mm, "mid": v(177.38, 8.31) * mm, "end": v(177.28, 9.1) * mm});
            skArc(sketch, "E386", {"start": v(176.6, 8.41) * mm, "mid": v(176.41, 8.6) * mm, "end": v(176.16, 8.66) * mm});
            skLineSegment(sketch, "E387", {"start": v(176.16, 8.66) * mm, "end": v(171.7, 8.66) * mm});
            skArc(sketch, "E388", {"start": v(171.7, 8.66) * mm, "mid": v(171.44, 8.6) * mm, "end": v(171.26, 8.41) * mm});
            skArc(sketch, "E389", {"start": v(170.58, 9.1) * mm, "mid": v(170.48, 8.31) * mm, "end": v(171.26, 8.41) * mm});
            skArc(sketch, "E390", {"start": v(170.58, 9.1) * mm, "mid": v(170.76, 9.28) * mm, "end": v(170.83, 9.53) * mm});
            skLineSegment(sketch, "E391", {"start": v(170.83, 9.53) * mm, "end": v(170.83, 11.1) * mm});
            skArc(sketch, "E392", {"start": v(149.63, 11.1) * mm, "mid": v(149.56, 11.35) * mm, "end": v(149.38, 11.53) * mm});
            skArc(sketch, "E393", {"start": v(150.06, 12.21) * mm, "mid": v(149.28, 12.32) * mm, "end": v(149.38, 11.53) * mm});
            skArc(sketch, "E394", {"start": v(150.06, 12.21) * mm, "mid": v(150.24, 12.03) * mm, "end": v(150.5, 11.96) * mm});
            skLineSegment(sketch, "E395", {"start": v(150.5, 11.96) * mm, "end": v(154.96, 11.96) * mm});
            skArc(sketch, "E396", {"start": v(154.96, 11.96) * mm, "mid": v(155.21, 12.03) * mm, "end": v(155.4, 12.21) * mm});
            skArc(sketch, "E397", {"start": v(156.08, 11.53) * mm, "mid": v(156.18, 12.32) * mm, "end": v(155.4, 12.21) * mm});
            skArc(sketch, "E398", {"start": v(156.08, 11.53) * mm, "mid": v(155.9, 11.35) * mm, "end": v(155.83, 11.1) * mm});
            skLineSegment(sketch, "E399", {"start": v(155.83, 11.1) * mm, "end": v(155.83, 9.53) * mm});
            skArc(sketch, "E400", {"start": v(155.83, 9.53) * mm, "mid": v(155.9, 9.28) * mm, "end": v(156.08, 9.1) * mm});
            skArc(sketch, "E401", {"start": v(155.4, 8.41) * mm, "mid": v(156.18, 8.31) * mm, "end": v(156.08, 9.1) * mm});
            skArc(sketch, "E402", {"start": v(155.4, 8.41) * mm, "mid": v(155.21, 8.6) * mm, "end": v(154.96, 8.66) * mm});
            skLineSegment(sketch, "E403", {"start": v(154.96, 8.66) * mm, "end": v(150.5, 8.66) * mm});
            skArc(sketch, "E404", {"start": v(150.5, 8.66) * mm, "mid": v(150.24, 8.6) * mm, "end": v(150.06, 8.41) * mm});
            skArc(sketch, "E405", {"start": v(149.38, 9.1) * mm, "mid": v(149.28, 8.31) * mm, "end": v(150.06, 8.41) * mm});
            skArc(sketch, "E406", {"start": v(149.38, 9.1) * mm, "mid": v(149.56, 9.28) * mm, "end": v(149.63, 9.53) * mm});
            skLineSegment(sketch, "E407", {"start": v(149.63, 9.53) * mm, "end": v(149.63, 11.1) * mm});
            skArc(sketch, "E408", {"start": v(450.58, 249.45) * mm, "mid": v(450.76, 249.63) * mm, "end": v(450.83, 249.88) * mm});
            skArc(sketch, "E409", {"start": v(450.58, 249.45) * mm, "mid": v(450.48, 248.66) * mm, "end": v(451.26, 248.76) * mm});
            skArc(sketch, "E410", {"start": v(451.7, 249.01) * mm, "mid": v(451.44, 248.95) * mm, "end": v(451.26, 248.76) * mm});
            skLineSegment(sketch, "E411", {"start": v(451.7, 249.01) * mm, "end": v(456.16, 249.01) * mm});
            skArc(sketch, "E412", {"start": v(456.6, 248.76) * mm, "mid": v(456.41, 248.95) * mm, "end": v(456.16, 249.01) * mm});
            skArc(sketch, "E413", {"start": v(456.6, 248.76) * mm, "mid": v(457.38, 248.66) * mm, "end": v(457.28, 249.45) * mm});
            skArc(sketch, "E414", {"start": v(457.03, 249.88) * mm, "mid": v(457.1, 249.63) * mm, "end": v(457.28, 249.45) * mm});
            skLineSegment(sketch, "E415", {"start": v(457.03, 249.88) * mm, "end": v(457.03, 251.45) * mm});
            skArc(sketch, "E416", {"start": v(457.28, 251.88) * mm, "mid": v(457.1, 251.7) * mm, "end": v(457.03, 251.45) * mm});
            skArc(sketch, "E417", {"start": v(457.28, 251.88) * mm, "mid": v(457.38, 252.67) * mm, "end": v(456.6, 252.56) * mm});
            skArc(sketch, "E418", {"start": v(456.16, 252.31) * mm, "mid": v(456.41, 252.38) * mm, "end": v(456.6, 252.56) * mm});
            skLineSegment(sketch, "E419", {"start": v(456.16, 252.31) * mm, "end": v(451.7, 252.31) * mm});
            skArc(sketch, "E420", {"start": v(451.26, 252.56) * mm, "mid": v(451.44, 252.38) * mm, "end": v(451.7, 252.31) * mm});
            skArc(sketch, "E421", {"start": v(451.26, 252.56) * mm, "mid": v(450.48, 252.67) * mm, "end": v(450.58, 251.88) * mm});
            skArc(sketch, "E422", {"start": v(450.83, 251.45) * mm, "mid": v(450.76, 251.7) * mm, "end": v(450.58, 251.88) * mm});
            skLineSegment(sketch, "E423", {"start": v(450.83, 251.45) * mm, "end": v(450.83, 249.88) * mm});
            skArc(sketch, "E424", {"start": v(429.38, 249.45) * mm, "mid": v(429.56, 249.63) * mm, "end": v(429.63, 249.88) * mm});
            skArc(sketch, "E425", {"start": v(429.38, 249.45) * mm, "mid": v(429.28, 248.66) * mm, "end": v(430.06, 248.76) * mm});
            skArc(sketch, "E426", {"start": v(430.5, 249.01) * mm, "mid": v(430.24, 248.95) * mm, "end": v(430.06, 248.76) * mm});
            skLineSegment(sketch, "E427", {"start": v(430.5, 249.01) * mm, "end": v(434.96, 249.01) * mm});
            skArc(sketch, "E428", {"start": v(435.4, 248.76) * mm, "mid": v(435.21, 248.95) * mm, "end": v(434.96, 249.01) * mm});
            skArc(sketch, "E429", {"start": v(435.4, 248.76) * mm, "mid": v(436.18, 248.66) * mm, "end": v(436.08, 249.45) * mm});
            skArc(sketch, "E430", {"start": v(435.83, 249.88) * mm, "mid": v(435.9, 249.63) * mm, "end": v(436.08, 249.45) * mm});
            skLineSegment(sketch, "E431", {"start": v(435.83, 249.88) * mm, "end": v(435.83, 251.45) * mm});
            skArc(sketch, "E432", {"start": v(436.08, 251.88) * mm, "mid": v(435.9, 251.7) * mm, "end": v(435.83, 251.45) * mm});
            skArc(sketch, "E433", {"start": v(436.08, 251.88) * mm, "mid": v(436.18, 252.67) * mm, "end": v(435.4, 252.56) * mm});
            skArc(sketch, "E434", {"start": v(434.96, 252.31) * mm, "mid": v(435.21, 252.38) * mm, "end": v(435.4, 252.56) * mm});
            skLineSegment(sketch, "E435", {"start": v(434.96, 252.31) * mm, "end": v(430.5, 252.31) * mm});
            skArc(sketch, "E436", {"start": v(430.06, 252.56) * mm, "mid": v(430.24, 252.38) * mm, "end": v(430.5, 252.31) * mm});
            skArc(sketch, "E437", {"start": v(430.06, 252.56) * mm, "mid": v(429.28, 252.67) * mm, "end": v(429.38, 251.88) * mm});
            skArc(sketch, "E438", {"start": v(429.63, 251.45) * mm, "mid": v(429.56, 251.7) * mm, "end": v(429.38, 251.88) * mm});
            skLineSegment(sketch, "E439", {"start": v(429.63, 251.45) * mm, "end": v(429.63, 249.88) * mm});
            skArc(sketch, "E440", {"start": v(330.83, 251.45) * mm, "mid": v(330.76, 251.7) * mm, "end": v(330.58, 251.88) * mm});
            skArc(sketch, "E441", {"start": v(331.26, 252.56) * mm, "mid": v(330.48, 252.67) * mm, "end": v(330.58, 251.88) * mm});
            skArc(sketch, "E442", {"start": v(331.26, 252.56) * mm, "mid": v(331.44, 252.38) * mm, "end": v(331.7, 252.31) * mm});
            skLineSegment(sketch, "E443", {"start": v(331.7, 252.31) * mm, "end": v(336.16, 252.31) * mm});
            skArc(sketch, "E444", {"start": v(336.16, 252.31) * mm, "mid": v(336.41, 252.38) * mm, "end": v(336.6, 252.56) * mm});
            skArc(sketch, "E445", {"start": v(337.28, 251.88) * mm, "mid": v(337.38, 252.67) * mm, "end": v(336.6, 252.56) * mm});
            skArc(sketch, "E446", {"start": v(337.28, 251.88) * mm, "mid": v(337.1, 251.7) * mm, "end": v(337.03, 251.45) * mm});
            skLineSegment(sketch, "E447", {"start": v(337.03, 251.45) * mm, "end": v(337.03, 249.88) * mm});
            skArc(sketch, "E448", {"start": v(337.03, 249.88) * mm, "mid": v(337.1, 249.63) * mm, "end": v(337.28, 249.45) * mm});
            skArc(sketch, "E449", {"start": v(336.6, 248.76) * mm, "mid": v(337.38, 248.66) * mm, "end": v(337.28, 249.45) * mm});
            skArc(sketch, "E450", {"start": v(336.6, 248.76) * mm, "mid": v(336.41, 248.95) * mm, "end": v(336.16, 249.01) * mm});
            skLineSegment(sketch, "E451", {"start": v(336.16, 249.01) * mm, "end": v(331.7, 249.01) * mm});
            skArc(sketch, "E452", {"start": v(331.7, 249.01) * mm, "mid": v(331.44, 248.95) * mm, "end": v(331.26, 248.76) * mm});
            skArc(sketch, "E453", {"start": v(330.58, 249.45) * mm, "mid": v(330.48, 248.66) * mm, "end": v(331.26, 248.76) * mm});
            skArc(sketch, "E454", {"start": v(330.58, 249.45) * mm, "mid": v(330.76, 249.63) * mm, "end": v(330.83, 249.88) * mm});
            skLineSegment(sketch, "E455", {"start": v(330.83, 249.88) * mm, "end": v(330.83, 251.45) * mm});
            skArc(sketch, "E456", {"start": v(309.63, 251.45) * mm, "mid": v(309.56, 251.7) * mm, "end": v(309.38, 251.88) * mm});
            skArc(sketch, "E457", {"start": v(310.06, 252.56) * mm, "mid": v(309.28, 252.67) * mm, "end": v(309.38, 251.88) * mm});
            skArc(sketch, "E458", {"start": v(310.06, 252.56) * mm, "mid": v(310.24, 252.38) * mm, "end": v(310.5, 252.31) * mm});
            skLineSegment(sketch, "E459", {"start": v(310.5, 252.31) * mm, "end": v(314.96, 252.31) * mm});
            skArc(sketch, "E460", {"start": v(314.96, 252.31) * mm, "mid": v(315.21, 252.38) * mm, "end": v(315.4, 252.56) * mm});
            skArc(sketch, "E461", {"start": v(316.08, 251.88) * mm, "mid": v(316.18, 252.67) * mm, "end": v(315.4, 252.56) * mm});
            skArc(sketch, "E462", {"start": v(316.08, 251.88) * mm, "mid": v(315.9, 251.7) * mm, "end": v(315.83, 251.45) * mm});
            skLineSegment(sketch, "E463", {"start": v(315.83, 251.45) * mm, "end": v(315.83, 249.88) * mm});
            skArc(sketch, "E464", {"start": v(315.83, 249.88) * mm, "mid": v(315.9, 249.63) * mm, "end": v(316.08, 249.45) * mm});
            skArc(sketch, "E465", {"start": v(315.4, 248.76) * mm, "mid": v(316.18, 248.66) * mm, "end": v(316.08, 249.45) * mm});
            skArc(sketch, "E466", {"start": v(315.4, 248.76) * mm, "mid": v(315.21, 248.95) * mm, "end": v(314.96, 249.01) * mm});
            skLineSegment(sketch, "E467", {"start": v(314.96, 249.01) * mm, "end": v(310.5, 249.01) * mm});
            skArc(sketch, "E468", {"start": v(310.5, 249.01) * mm, "mid": v(310.24, 248.95) * mm, "end": v(310.06, 248.76) * mm});
            skArc(sketch, "E469", {"start": v(309.38, 249.45) * mm, "mid": v(309.28, 248.66) * mm, "end": v(310.06, 248.76) * mm});
            skArc(sketch, "E470", {"start": v(309.38, 249.45) * mm, "mid": v(309.56, 249.63) * mm, "end": v(309.63, 249.88) * mm});
            skLineSegment(sketch, "E471", {"start": v(309.63, 249.88) * mm, "end": v(309.63, 251.45) * mm});
            skArc(sketch, "E472", {"start": v(170.83, 251.45) * mm, "mid": v(170.76, 251.7) * mm, "end": v(170.58, 251.88) * mm});
            skArc(sketch, "E473", {"start": v(171.26, 252.56) * mm, "mid": v(170.48, 252.67) * mm, "end": v(170.58, 251.88) * mm});
            skArc(sketch, "E474", {"start": v(171.26, 252.56) * mm, "mid": v(171.44, 252.38) * mm, "end": v(171.7, 252.31) * mm});
            skLineSegment(sketch, "E475", {"start": v(171.7, 252.31) * mm, "end": v(176.16, 252.31) * mm});
            skArc(sketch, "E476", {"start": v(176.16, 252.31) * mm, "mid": v(176.41, 252.38) * mm, "end": v(176.6, 252.56) * mm});
            skArc(sketch, "E477", {"start": v(177.28, 251.88) * mm, "mid": v(177.38, 252.67) * mm, "end": v(176.6, 252.56) * mm});
            skArc(sketch, "E478", {"start": v(177.28, 251.88) * mm, "mid": v(177.1, 251.7) * mm, "end": v(177.03, 251.45) * mm});
            skLineSegment(sketch, "E479", {"start": v(177.03, 251.45) * mm, "end": v(177.03, 249.88) * mm});
            skArc(sketch, "E480", {"start": v(177.03, 249.88) * mm, "mid": v(177.1, 249.63) * mm, "end": v(177.28, 249.45) * mm});
            skArc(sketch, "E481", {"start": v(176.6, 248.76) * mm, "mid": v(177.38, 248.66) * mm, "end": v(177.28, 249.45) * mm});
            skArc(sketch, "E482", {"start": v(176.6, 248.76) * mm, "mid": v(176.41, 248.95) * mm, "end": v(176.16, 249.01) * mm});
            skLineSegment(sketch, "E483", {"start": v(176.16, 249.01) * mm, "end": v(171.7, 249.01) * mm});
            skArc(sketch, "E484", {"start": v(171.7, 249.01) * mm, "mid": v(171.44, 248.95) * mm, "end": v(171.26, 248.76) * mm});
            skArc(sketch, "E485", {"start": v(170.58, 249.45) * mm, "mid": v(170.48, 248.66) * mm, "end": v(171.26, 248.76) * mm});
            skArc(sketch, "E486", {"start": v(170.58, 249.45) * mm, "mid": v(170.76, 249.63) * mm, "end": v(170.83, 249.88) * mm});
            skLineSegment(sketch, "E487", {"start": v(170.83, 249.88) * mm, "end": v(170.83, 251.45) * mm});
            skArc(sketch, "E488", {"start": v(149.63, 251.45) * mm, "mid": v(149.56, 251.7) * mm, "end": v(149.38, 251.88) * mm});
            skArc(sketch, "E489", {"start": v(150.06, 252.56) * mm, "mid": v(149.28, 252.67) * mm, "end": v(149.38, 251.88) * mm});
            skArc(sketch, "E490", {"start": v(150.06, 252.56) * mm, "mid": v(150.24, 252.38) * mm, "end": v(150.5, 252.31) * mm});
            skLineSegment(sketch, "E491", {"start": v(150.5, 252.31) * mm, "end": v(154.96, 252.31) * mm});
            skArc(sketch, "E492", {"start": v(154.96, 252.31) * mm, "mid": v(155.21, 252.38) * mm, "end": v(155.4, 252.56) * mm});
            skArc(sketch, "E493", {"start": v(156.08, 251.88) * mm, "mid": v(156.18, 252.67) * mm, "end": v(155.4, 252.56) * mm});
            skArc(sketch, "E494", {"start": v(156.08, 251.88) * mm, "mid": v(155.9, 251.7) * mm, "end": v(155.83, 251.45) * mm});
            skLineSegment(sketch, "E495", {"start": v(155.83, 251.45) * mm, "end": v(155.83, 249.88) * mm});
            skArc(sketch, "E496", {"start": v(155.83, 249.88) * mm, "mid": v(155.9, 249.63) * mm, "end": v(156.08, 249.45) * mm});
            skArc(sketch, "E497", {"start": v(155.4, 248.76) * mm, "mid": v(156.18, 248.66) * mm, "end": v(156.08, 249.45) * mm});
            skArc(sketch, "E498", {"start": v(155.4, 248.76) * mm, "mid": v(155.21, 248.95) * mm, "end": v(154.96, 249.01) * mm});
            skLineSegment(sketch, "E499", {"start": v(154.96, 249.01) * mm, "end": v(150.5, 249.01) * mm});
            skArc(sketch, "E500", {"start": v(150.5, 249.01) * mm, "mid": v(150.24, 248.95) * mm, "end": v(150.06, 248.76) * mm});
            skArc(sketch, "E501", {"start": v(149.38, 249.45) * mm, "mid": v(149.28, 248.66) * mm, "end": v(150.06, 248.76) * mm});
            skArc(sketch, "E502", {"start": v(149.38, 249.45) * mm, "mid": v(149.56, 249.63) * mm, "end": v(149.63, 249.88) * mm});
            skLineSegment(sketch, "E503", {"start": v(149.63, 249.88) * mm, "end": v(149.63, 251.45) * mm});
            skArc(sketch, "E504", {"start": v(490.58, 270.05) * mm, "mid": v(490.76, 270.24) * mm, "end": v(490.83, 270.49) * mm});
            skArc(sketch, "E505", {"start": v(490.58, 270.05) * mm, "mid": v(490.48, 269.27) * mm, "end": v(491.26, 269.37) * mm});
            skArc(sketch, "E506", {"start": v(491.7, 269.62) * mm, "mid": v(491.44, 269.55) * mm, "end": v(491.26, 269.37) * mm});
            skLineSegment(sketch, "E507", {"start": v(491.7, 269.62) * mm, "end": v(496.16, 269.62) * mm});
            skArc(sketch, "E508", {"start": v(496.6, 269.37) * mm, "mid": v(496.41, 269.55) * mm, "end": v(496.16, 269.62) * mm});
            skArc(sketch, "E509", {"start": v(496.6, 269.37) * mm, "mid": v(497.38, 269.27) * mm, "end": v(497.28, 270.05) * mm});
            skArc(sketch, "E510", {"start": v(497.03, 270.49) * mm, "mid": v(497.1, 270.24) * mm, "end": v(497.28, 270.05) * mm});
            skLineSegment(sketch, "E511", {"start": v(497.03, 270.49) * mm, "end": v(497.03, 272.05) * mm});
            skArc(sketch, "E512", {"start": v(497.28, 272.49) * mm, "mid": v(497.1, 272.3) * mm, "end": v(497.03, 272.05) * mm});
            skArc(sketch, "E513", {"start": v(497.28, 272.49) * mm, "mid": v(497.38, 273.27) * mm, "end": v(496.6, 273.17) * mm});
            skArc(sketch, "E514", {"start": v(496.16, 272.92) * mm, "mid": v(496.41, 272.99) * mm, "end": v(496.6, 273.17) * mm});
            skLineSegment(sketch, "E515", {"start": v(496.16, 272.92) * mm, "end": v(491.7, 272.92) * mm});
            skArc(sketch, "E516", {"start": v(491.26, 273.17) * mm, "mid": v(491.44, 272.99) * mm, "end": v(491.7, 272.92) * mm});
            skArc(sketch, "E517", {"start": v(491.26, 273.17) * mm, "mid": v(490.48, 273.27) * mm, "end": v(490.58, 272.49) * mm});
            skArc(sketch, "E518", {"start": v(490.83, 272.05) * mm, "mid": v(490.76, 272.3) * mm, "end": v(490.58, 272.49) * mm});
            skLineSegment(sketch, "E519", {"start": v(490.83, 272.05) * mm, "end": v(490.83, 270.49) * mm});
            skArc(sketch, "E520", {"start": v(469.38, 270.05) * mm, "mid": v(469.56, 270.24) * mm, "end": v(469.63, 270.49) * mm});
            skArc(sketch, "E521", {"start": v(469.38, 270.05) * mm, "mid": v(469.28, 269.27) * mm, "end": v(470.06, 269.37) * mm});
            skArc(sketch, "E522", {"start": v(470.5, 269.62) * mm, "mid": v(470.24, 269.55) * mm, "end": v(470.06, 269.37) * mm});
            skLineSegment(sketch, "E523", {"start": v(470.5, 269.62) * mm, "end": v(474.96, 269.62) * mm});
            skArc(sketch, "E524", {"start": v(475.4, 269.37) * mm, "mid": v(475.21, 269.55) * mm, "end": v(474.96, 269.62) * mm});
            skArc(sketch, "E525", {"start": v(475.4, 269.37) * mm, "mid": v(476.18, 269.27) * mm, "end": v(476.08, 270.05) * mm});
            skArc(sketch, "E526", {"start": v(475.83, 270.49) * mm, "mid": v(475.9, 270.24) * mm, "end": v(476.08, 270.05) * mm});
            skLineSegment(sketch, "E527", {"start": v(475.83, 270.49) * mm, "end": v(475.83, 272.05) * mm});
            skArc(sketch, "E528", {"start": v(476.08, 272.49) * mm, "mid": v(475.9, 272.3) * mm, "end": v(475.83, 272.05) * mm});
            skArc(sketch, "E529", {"start": v(476.08, 272.49) * mm, "mid": v(476.18, 273.27) * mm, "end": v(475.4, 273.17) * mm});
            skArc(sketch, "E530", {"start": v(474.96, 272.92) * mm, "mid": v(475.21, 272.99) * mm, "end": v(475.4, 273.17) * mm});
            skLineSegment(sketch, "E531", {"start": v(474.96, 272.92) * mm, "end": v(470.5, 272.92) * mm});
            skArc(sketch, "E532", {"start": v(470.06, 273.17) * mm, "mid": v(470.24, 272.99) * mm, "end": v(470.5, 272.92) * mm});
            skArc(sketch, "E533", {"start": v(470.06, 273.17) * mm, "mid": v(469.28, 273.27) * mm, "end": v(469.38, 272.49) * mm});
            skArc(sketch, "E534", {"start": v(469.63, 272.05) * mm, "mid": v(469.56, 272.3) * mm, "end": v(469.38, 272.49) * mm});
            skLineSegment(sketch, "E535", {"start": v(469.63, 272.05) * mm, "end": v(469.63, 270.49) * mm});
            skArc(sketch, "E536", {"start": v(455.47, 288.54) * mm, "mid": v(455.65, 288.36) * mm, "end": v(455.9, 288.29) * mm});
            skArc(sketch, "E537", {"start": v(455.47, 288.54) * mm, "mid": v(454.68, 288.64) * mm, "end": v(454.78, 287.86) * mm});
            skArc(sketch, "E538", {"start": v(455.03, 287.42) * mm, "mid": v(454.97, 287.67) * mm, "end": v(454.78, 287.86) * mm});
            skLineSegment(sketch, "E539", {"start": v(455.03, 287.42) * mm, "end": v(455.03, 282.96) * mm});
            skArc(sketch, "E540", {"start": v(454.78, 282.52) * mm, "mid": v(454.97, 282.7) * mm, "end": v(455.03, 282.96) * mm});
            skArc(sketch, "E541", {"start": v(454.78, 282.52) * mm, "mid": v(454.68, 281.74) * mm, "end": v(455.47, 281.84) * mm});
            skArc(sketch, "E542", {"start": v(455.9, 282.09) * mm, "mid": v(455.65, 282.02) * mm, "end": v(455.47, 281.84) * mm});
            skLineSegment(sketch, "E543", {"start": v(455.9, 282.09) * mm, "end": v(457.47, 282.09) * mm});
            skArc(sketch, "E544", {"start": v(457.9, 281.84) * mm, "mid": v(457.72, 282.02) * mm, "end": v(457.47, 282.09) * mm});
            skArc(sketch, "E545", {"start": v(457.9, 281.84) * mm, "mid": v(458.69, 281.74) * mm, "end": v(458.58, 282.52) * mm});
            skArc(sketch, "E546", {"start": v(458.33, 282.96) * mm, "mid": v(458.4, 282.7) * mm, "end": v(458.58, 282.52) * mm});
            skLineSegment(sketch, "E547", {"start": v(458.33, 282.96) * mm, "end": v(458.33, 287.42) * mm});
            skArc(sketch, "E548", {"start": v(458.58, 287.86) * mm, "mid": v(458.4, 287.67) * mm, "end": v(458.33, 287.42) * mm});
            skArc(sketch, "E549", {"start": v(458.58, 287.86) * mm, "mid": v(458.69, 288.64) * mm, "end": v(457.9, 288.54) * mm});
            skArc(sketch, "E550", {"start": v(457.47, 288.29) * mm, "mid": v(457.72, 288.36) * mm, "end": v(457.9, 288.54) * mm});
            skLineSegment(sketch, "E551", {"start": v(457.47, 288.29) * mm, "end": v(455.9, 288.29) * mm});
            skArc(sketch, "E552", {"start": v(455.47, 309.74) * mm, "mid": v(455.65, 309.56) * mm, "end": v(455.9, 309.49) * mm});
            skArc(sketch, "E553", {"start": v(455.47, 309.74) * mm, "mid": v(454.68, 309.84) * mm, "end": v(454.78, 309.06) * mm});
            skArc(sketch, "E554", {"start": v(455.03, 308.62) * mm, "mid": v(454.97, 308.87) * mm, "end": v(454.78, 309.06) * mm});
            skLineSegment(sketch, "E555", {"start": v(455.03, 308.62) * mm, "end": v(455.03, 304.16) * mm});
            skArc(sketch, "E556", {"start": v(454.78, 303.72) * mm, "mid": v(454.97, 303.9) * mm, "end": v(455.03, 304.16) * mm});
            skArc(sketch, "E557", {"start": v(454.78, 303.72) * mm, "mid": v(454.68, 302.94) * mm, "end": v(455.47, 303.04) * mm});
            skArc(sketch, "E558", {"start": v(455.9, 303.29) * mm, "mid": v(455.65, 303.22) * mm, "end": v(455.47, 303.04) * mm});
            skLineSegment(sketch, "E559", {"start": v(455.9, 303.29) * mm, "end": v(457.47, 303.29) * mm});
            skArc(sketch, "E560", {"start": v(457.9, 303.04) * mm, "mid": v(457.72, 303.22) * mm, "end": v(457.47, 303.29) * mm});
            skArc(sketch, "E561", {"start": v(457.9, 303.04) * mm, "mid": v(458.69, 302.94) * mm, "end": v(458.58, 303.72) * mm});
            skArc(sketch, "E562", {"start": v(458.33, 304.16) * mm, "mid": v(458.4, 303.9) * mm, "end": v(458.58, 303.72) * mm});
            skLineSegment(sketch, "E563", {"start": v(458.33, 304.16) * mm, "end": v(458.33, 308.62) * mm});
            skArc(sketch, "E564", {"start": v(458.58, 309.06) * mm, "mid": v(458.4, 308.87) * mm, "end": v(458.33, 308.62) * mm});
            skArc(sketch, "E565", {"start": v(458.58, 309.06) * mm, "mid": v(458.69, 309.84) * mm, "end": v(457.9, 309.74) * mm});
            skArc(sketch, "E566", {"start": v(457.47, 309.49) * mm, "mid": v(457.72, 309.56) * mm, "end": v(457.9, 309.74) * mm});
            skLineSegment(sketch, "E567", {"start": v(457.47, 309.49) * mm, "end": v(455.9, 309.49) * mm});
            skArc(sketch, "E568", {"start": v(490.58, 319.1) * mm, "mid": v(490.76, 319.28) * mm, "end": v(490.83, 319.53) * mm});
            skArc(sketch, "E569", {"start": v(490.58, 319.1) * mm, "mid": v(490.48, 318.3) * mm, "end": v(491.26, 318.4) * mm});
            skArc(sketch, "E570", {"start": v(491.7, 318.66) * mm, "mid": v(491.44, 318.6) * mm, "end": v(491.26, 318.4) * mm});
            skLineSegment(sketch, "E571", {"start": v(491.7, 318.66) * mm, "end": v(496.16, 318.66) * mm});
            skArc(sketch, "E572", {"start": v(496.6, 318.4) * mm, "mid": v(496.41, 318.6) * mm, "end": v(496.16, 318.66) * mm});
            skArc(sketch, "E573", {"start": v(496.6, 318.4) * mm, "mid": v(497.38, 318.3) * mm, "end": v(497.28, 319.1) * mm});
            skArc(sketch, "E574", {"start": v(497.03, 319.53) * mm, "mid": v(497.1, 319.28) * mm, "end": v(497.28, 319.1) * mm});
            skLineSegment(sketch, "E575", {"start": v(497.03, 319.53) * mm, "end": v(497.03, 321.1) * mm});
            skArc(sketch, "E576", {"start": v(497.28, 321.53) * mm, "mid": v(497.1, 321.34) * mm, "end": v(497.03, 321.1) * mm});
            skArc(sketch, "E577", {"start": v(497.28, 321.53) * mm, "mid": v(497.38, 322.31) * mm, "end": v(496.6, 322.2) * mm});
            skArc(sketch, "E578", {"start": v(496.16, 321.96) * mm, "mid": v(496.41, 322.03) * mm, "end": v(496.6, 322.2) * mm});
            skLineSegment(sketch, "E579", {"start": v(496.16, 321.96) * mm, "end": v(491.7, 321.96) * mm});
            skArc(sketch, "E580", {"start": v(491.26, 322.2) * mm, "mid": v(491.44, 322.03) * mm, "end": v(491.7, 321.96) * mm});
            skArc(sketch, "E581", {"start": v(491.26, 322.2) * mm, "mid": v(490.48, 322.31) * mm, "end": v(490.58, 321.53) * mm});
            skArc(sketch, "E582", {"start": v(490.83, 321.1) * mm, "mid": v(490.76, 321.34) * mm, "end": v(490.58, 321.53) * mm});
            skLineSegment(sketch, "E583", {"start": v(490.83, 321.1) * mm, "end": v(490.83, 319.53) * mm});
            skArc(sketch, "E584", {"start": v(469.38, 319.1) * mm, "mid": v(469.56, 319.28) * mm, "end": v(469.63, 319.53) * mm});
            skArc(sketch, "E585", {"start": v(469.38, 319.1) * mm, "mid": v(469.28, 318.3) * mm, "end": v(470.06, 318.4) * mm});
            skArc(sketch, "E586", {"start": v(470.5, 318.66) * mm, "mid": v(470.24, 318.6) * mm, "end": v(470.06, 318.4) * mm});
            skLineSegment(sketch, "E587", {"start": v(470.5, 318.66) * mm, "end": v(474.96, 318.66) * mm});
            skArc(sketch, "E588", {"start": v(475.4, 318.4) * mm, "mid": v(475.21, 318.6) * mm, "end": v(474.96, 318.66) * mm});
            skArc(sketch, "E589", {"start": v(475.4, 318.4) * mm, "mid": v(476.18, 318.3) * mm, "end": v(476.08, 319.1) * mm});
            skArc(sketch, "E590", {"start": v(475.83, 319.53) * mm, "mid": v(475.9, 319.28) * mm, "end": v(476.08, 319.1) * mm});
            skLineSegment(sketch, "E591", {"start": v(475.83, 319.53) * mm, "end": v(475.83, 321.1) * mm});
            skArc(sketch, "E592", {"start": v(476.08, 321.53) * mm, "mid": v(475.9, 321.34) * mm, "end": v(475.83, 321.1) * mm});
            skArc(sketch, "E593", {"start": v(476.08, 321.53) * mm, "mid": v(476.18, 322.31) * mm, "end": v(475.4, 322.2) * mm});
            skArc(sketch, "E594", {"start": v(474.96, 321.96) * mm, "mid": v(475.21, 322.03) * mm, "end": v(475.4, 322.2) * mm});
            skLineSegment(sketch, "E595", {"start": v(474.96, 321.96) * mm, "end": v(470.5, 321.96) * mm});
            skArc(sketch, "E596", {"start": v(470.06, 322.2) * mm, "mid": v(470.24, 322.03) * mm, "end": v(470.5, 321.96) * mm});
            skArc(sketch, "E597", {"start": v(470.06, 322.2) * mm, "mid": v(469.28, 322.31) * mm, "end": v(469.38, 321.53) * mm});
            skArc(sketch, "E598", {"start": v(469.63, 321.1) * mm, "mid": v(469.56, 321.34) * mm, "end": v(469.38, 321.53) * mm});
            skLineSegment(sketch, "E599", {"start": v(469.63, 321.1) * mm, "end": v(469.63, 319.53) * mm});
            skCircle(sketch, "E600", {"center": v(483.33, -59.33) * mm, "radius": 1.6 * mm});
            skCircle(sketch, "E601", {"center": v(456.68, -34.81) * mm, "radius": 1.6 * mm});
            skCircle(sketch, "E602", {"center": v(483.33, -10.3) * mm, "radius": 1.6 * mm});
            skCircle(sketch, "E603", {"center": v(443.33, 10.31) * mm, "radius": 1.6 * mm});
            skCircle(sketch, "E604", {"center": v(323.33, 10.31) * mm, "radius": 1.6 * mm});
            skCircle(sketch, "E605", {"center": v(163.33, 10.31) * mm, "radius": 1.6 * mm});
            skCircle(sketch, "E606", {"center": v(443.33, 250.66) * mm, "radius": 1.6 * mm});
            skCircle(sketch, "E607", {"center": v(323.33, 250.66) * mm, "radius": 1.6 * mm});
            skCircle(sketch, "E608", {"center": v(163.33, 250.66) * mm, "radius": 1.6 * mm});
            skCircle(sketch, "E609", {"center": v(483.33, 271.27) * mm, "radius": 1.6 * mm});
            skCircle(sketch, "E610", {"center": v(456.68, 295.79) * mm, "radius": 1.6 * mm});
            skCircle(sketch, "E611", {"center": v(483.33, 320.3) * mm, "radius": 1.6 * mm});
            skArc(sketch, "E612", {"start": v(-246.27, -63.4) * mm, "mid": v(-246.09, -63.59) * mm, "end": v(-245.84, -63.65) * mm});
            skArc(sketch, "E613", {"start": v(-246.27, -63.4) * mm, "mid": v(-247.06, -63.3) * mm, "end": v(-246.96, -64.09) * mm});
            skArc(sketch, "E614", {"start": v(-246.7, -64.52) * mm, "mid": v(-246.77, -64.27) * mm, "end": v(-246.96, -64.09) * mm});
            skLineSegment(sketch, "E615", {"start": v(-246.7, -64.52) * mm, "end": v(-246.7, -66.15) * mm});
            skArc(sketch, "E616", {"start": v(-247.2, -66.65) * mm, "mid": v(-246.85, -66.5) * mm, "end": v(-246.7, -66.15) * mm});
            skLineSegment(sketch, "E617", {"start": v(-247.2, -66.65) * mm, "end": v(-252.2, -66.65) * mm});
            skArc(sketch, "E618", {"start": v(-252.7, -66.15) * mm, "mid": v(-252.56, -66.5) * mm, "end": v(-252.2, -66.65) * mm});
            skLineSegment(sketch, "E619", {"start": v(-252.7, -66.15) * mm, "end": v(-252.7, -64.52) * mm});
            skArc(sketch, "E620", {"start": v(-252.46, -64.09) * mm, "mid": v(-252.64, -64.27) * mm, "end": v(-252.7, -64.52) * mm});
            skArc(sketch, "E621", {"start": v(-252.46, -64.09) * mm, "mid": v(-252.35, -63.3) * mm, "end": v(-253.14, -63.4) * mm});
            skArc(sketch, "E622", {"start": v(-253.57, -63.65) * mm, "mid": v(-253.32, -63.59) * mm, "end": v(-253.14, -63.4) * mm});
            skLineSegment(sketch, "E623", {"start": v(-253.57, -63.65) * mm, "end": v(-258.7, -63.65) * mm});
            skLineSegment(sketch, "E624", {"start": v(-258.7, -63.65) * mm, "end": v(-258.7, -60.65) * mm});
            skLineSegment(sketch, "E625", {"start": v(-258.7, -60.65) * mm, "end": v(-257.43, -60.65) * mm});
            skLineSegment(sketch, "E626", {"start": v(-257.43, -60.65) * mm, "end": v(-257.43, -56.65) * mm});
            skLineSegment(sketch, "E627", {"start": v(-257.43, -56.65) * mm, "end": v(-258.7, -56.65) * mm});
            skLineSegment(sketch, "E628", {"start": v(-258.7, -56.65) * mm, "end": v(-258.7, -53.65) * mm});
            skLineSegment(sketch, "E629", {"start": v(-258.7, -53.65) * mm, "end": v(-261.9, -53.65) * mm});
            skLineSegment(sketch, "E630", {"start": v(-261.9, -53.65) * mm, "end": v(-261.9, -56.65) * mm});
            skLineSegment(sketch, "E631", {"start": v(-261.9, -56.65) * mm, "end": v(-263.18, -56.65) * mm});
            skLineSegment(sketch, "E632", {"start": v(-263.18, -56.65) * mm, "end": v(-263.18, -60.65) * mm});
            skLineSegment(sketch, "E633", {"start": v(-263.18, -60.65) * mm, "end": v(-261.9, -60.65) * mm});
            skLineSegment(sketch, "E634", {"start": v(-261.9, -60.65) * mm, "end": v(-261.9, -63.65) * mm});
            skLineSegment(sketch, "E635", {"start": v(-261.9, -63.65) * mm, "end": v(-267.04, -63.65) * mm});
            skArc(sketch, "E636", {"start": v(-267.47, -63.4) * mm, "mid": v(-267.29, -63.59) * mm, "end": v(-267.04, -63.65) * mm});
            skArc(sketch, "E637", {"start": v(-267.47, -63.4) * mm, "mid": v(-268.26, -63.3) * mm, "end": v(-268.16, -64.09) * mm});
            skArc(sketch, "E638", {"start": v(-267.9, -64.52) * mm, "mid": v(-267.97, -64.27) * mm, "end": v(-268.16, -64.09) * mm});
            skLineSegment(sketch, "E639", {"start": v(-267.9, -64.52) * mm, "end": v(-267.9, -66.15) * mm});
            skArc(sketch, "E640", {"start": v(-268.4, -66.65) * mm, "mid": v(-268.05, -66.5) * mm, "end": v(-267.9, -66.15) * mm});
            skLineSegment(sketch, "E641", {"start": v(-268.4, -66.65) * mm, "end": v(-273.4, -66.65) * mm});
            skArc(sketch, "E642", {"start": v(-273.9, -66.15) * mm, "mid": v(-273.76, -66.5) * mm, "end": v(-273.4, -66.65) * mm});
            skLineSegment(sketch, "E643", {"start": v(-273.9, -66.15) * mm, "end": v(-273.9, -64.52) * mm});
            skArc(sketch, "E644", {"start": v(-273.66, -64.09) * mm, "mid": v(-273.84, -64.27) * mm, "end": v(-273.9, -64.52) * mm});
            skArc(sketch, "E645", {"start": v(-273.66, -64.09) * mm, "mid": v(-273.55, -63.3) * mm, "end": v(-274.34, -63.4) * mm});
            skArc(sketch, "E646", {"start": v(-274.77, -63.65) * mm, "mid": v(-274.52, -63.59) * mm, "end": v(-274.34, -63.4) * mm});
            skLineSegment(sketch, "E647", {"start": v(-274.77, -63.65) * mm, "end": v(-285.3, -63.65) * mm});
            skLineSegment(sketch, "E648", {"start": v(-285.3, -58.65) * mm, "end": v(-285.3, -37.65) * mm});
            skLineSegment(sketch, "E649", {"start": v(-285.3, -37.65) * mm, "end": v(-283.3, -35.65) * mm});
            skLineSegment(sketch, "E650", {"start": v(-283.3, -35.65) * mm, "end": v(-283.3, 66.35) * mm});
            skLineSegment(sketch, "E651", {"start": v(-283.3, 66.35) * mm, "end": v(-274.77, 66.35) * mm});
            skArc(sketch, "E652", {"start": v(-274.34, 66.1) * mm, "mid": v(-274.52, 66.28) * mm, "end": v(-274.77, 66.35) * mm});
            skArc(sketch, "E653", {"start": v(-274.34, 66.1) * mm, "mid": v(-273.55, 66) * mm, "end": v(-273.66, 66.78) * mm});
            skArc(sketch, "E654", {"start": v(-273.9, 67.21) * mm, "mid": v(-273.84, 66.96) * mm, "end": v(-273.66, 66.78) * mm});
            skLineSegment(sketch, "E655", {"start": v(-273.9, 67.21) * mm, "end": v(-273.9, 278.85) * mm});
            skArc(sketch, "E656", {"start": v(-273.4, 283.35) * mm, "mid": v(-273.76, 283.2) * mm, "end": v(-273.9, 282.85) * mm});
            skLineSegment(sketch, "E657", {"start": v(-273.4, 283.35) * mm, "end": v(-268.4, 283.35) * mm});
            skArc(sketch, "E658", {"start": v(-267.9, 282.85) * mm, "mid": v(-268.05, 283.2) * mm, "end": v(-268.4, 283.35) * mm});
            skLineSegment(sketch, "E659", {"start": v(-267.9, 282.85) * mm, "end": v(-267.9, 281.21) * mm});
            skArc(sketch, "E660", {"start": v(-268.16, 280.78) * mm, "mid": v(-267.97, 280.96) * mm, "end": v(-267.9, 281.21) * mm});
            skArc(sketch, "E661", {"start": v(-268.16, 280.78) * mm, "mid": v(-268.26, 280) * mm, "end": v(-267.47, 280.1) * mm});
            skArc(sketch, "E662", {"start": v(-267.04, 280.35) * mm, "mid": v(-267.29, 280.28) * mm, "end": v(-267.47, 280.1) * mm});
            skLineSegment(sketch, "E663", {"start": v(-267.04, 280.35) * mm, "end": v(-261.9, 280.35) * mm});
            skLineSegment(sketch, "E664", {"start": v(-261.9, 280.35) * mm, "end": v(-261.9, 277.35) * mm});
            skLineSegment(sketch, "E665", {"start": v(-261.9, 277.35) * mm, "end": v(-263.18, 277.35) * mm});
            skLineSegment(sketch, "E666", {"start": v(-263.18, 277.35) * mm, "end": v(-263.18, 273.35) * mm});
            skLineSegment(sketch, "E667", {"start": v(-263.18, 273.35) * mm, "end": v(-261.9, 273.35) * mm});
            skLineSegment(sketch, "E668", {"start": v(-261.9, 273.35) * mm, "end": v(-261.9, 270.35) * mm});
            skLineSegment(sketch, "E669", {"start": v(-261.9, 270.35) * mm, "end": v(-258.7, 270.35) * mm});
            skLineSegment(sketch, "E670", {"start": v(-258.7, 270.35) * mm, "end": v(-258.7, 273.35) * mm});
            skLineSegment(sketch, "E671", {"start": v(-258.7, 273.35) * mm, "end": v(-257.43, 273.35) * mm});
            skLineSegment(sketch, "E672", {"start": v(-257.43, 273.35) * mm, "end": v(-257.43, 277.35) * mm});
            skLineSegment(sketch, "E673", {"start": v(-257.43, 277.35) * mm, "end": v(-258.7, 277.35) * mm});
            skLineSegment(sketch, "E674", {"start": v(-258.7, 277.35) * mm, "end": v(-258.7, 280.35) * mm});
            skLineSegment(sketch, "E675", {"start": v(-258.7, 280.35) * mm, "end": v(-253.57, 280.35) * mm});
            skArc(sketch, "E676", {"start": v(-253.14, 280.1) * mm, "mid": v(-253.32, 280.28) * mm, "end": v(-253.57, 280.35) * mm});
            skArc(sketch, "E677", {"start": v(-253.14, 280.1) * mm, "mid": v(-252.35, 280) * mm, "end": v(-252.46, 280.78) * mm});
            skArc(sketch, "E678", {"start": v(-252.7, 281.21) * mm, "mid": v(-252.64, 280.96) * mm, "end": v(-252.46, 280.78) * mm});
            skLineSegment(sketch, "E679", {"start": v(-252.7, 281.21) * mm, "end": v(-252.7, 282.85) * mm});
            skArc(sketch, "E680", {"start": v(-252.2, 283.35) * mm, "mid": v(-252.56, 283.2) * mm, "end": v(-252.7, 282.85) * mm});
            skLineSegment(sketch, "E681", {"start": v(-252.2, 283.35) * mm, "end": v(-247.2, 283.35) * mm});
            skArc(sketch, "E682", {"start": v(-246.7, 282.85) * mm, "mid": v(-246.85, 283.2) * mm, "end": v(-247.2, 283.35) * mm});
            skLineSegment(sketch, "E683", {"start": v(-246.7, 278.85) * mm, "end": v(-246.7, 67.21) * mm});
            skArc(sketch, "E684", {"start": v(-246.96, 66.78) * mm, "mid": v(-246.77, 66.96) * mm, "end": v(-246.7, 67.21) * mm});
            skArc(sketch, "E685", {"start": v(-246.96, 66.78) * mm, "mid": v(-247.06, 66) * mm, "end": v(-246.27, 66.1) * mm});
            skArc(sketch, "E686", {"start": v(-245.84, 66.35) * mm, "mid": v(-246.09, 66.28) * mm, "end": v(-246.27, 66.1) * mm});
            skLineSegment(sketch, "E687", {"start": v(-245.84, 66.35) * mm, "end": v(-234.77, 66.35) * mm});
            skArc(sketch, "E688", {"start": v(-234.34, 66.1) * mm, "mid": v(-234.52, 66.28) * mm, "end": v(-234.77, 66.35) * mm});
            skArc(sketch, "E689", {"start": v(-234.34, 66.1) * mm, "mid": v(-233.55, 66) * mm, "end": v(-233.66, 66.78) * mm});
            skArc(sketch, "E690", {"start": v(-233.9, 67.21) * mm, "mid": v(-233.84, 66.96) * mm, "end": v(-233.66, 66.78) * mm});
            skLineSegment(sketch, "E691", {"start": v(-233.9, 67.21) * mm, "end": v(-233.9, 68.85) * mm});
            skArc(sketch, "E692", {"start": v(-233.4, 69.35) * mm, "mid": v(-233.76, 69.2) * mm, "end": v(-233.9, 68.85) * mm});
            skLineSegment(sketch, "E693", {"start": v(-233.4, 69.35) * mm, "end": v(-228.4, 69.35) * mm});
            skArc(sketch, "E694", {"start": v(-227.9, 68.85) * mm, "mid": v(-228.05, 69.2) * mm, "end": v(-228.4, 69.35) * mm});
            skLineSegment(sketch, "E695", {"start": v(-227.9, 68.85) * mm, "end": v(-227.9, 67.21) * mm});
            skArc(sketch, "E696", {"start": v(-228.16, 66.78) * mm, "mid": v(-227.97, 66.96) * mm, "end": v(-227.9, 67.21) * mm});
            skArc(sketch, "E697", {"start": v(-228.16, 66.78) * mm, "mid": v(-228.26, 66) * mm, "end": v(-227.47, 66.1) * mm});
            skArc(sketch, "E698", {"start": v(-227.04, 66.35) * mm, "mid": v(-227.29, 66.28) * mm, "end": v(-227.47, 66.1) * mm});
            skLineSegment(sketch, "E699", {"start": v(-227.04, 66.35) * mm, "end": v(-221.9, 66.35) * mm});
            skLineSegment(sketch, "E700", {"start": v(-221.9, 66.35) * mm, "end": v(-221.9, 63.35) * mm});
            skLineSegment(sketch, "E701", {"start": v(-221.9, 63.35) * mm, "end": v(-223.18, 63.35) * mm});
            skLineSegment(sketch, "E702", {"start": v(-223.18, 63.35) * mm, "end": v(-223.18, 59.35) * mm});
            skLineSegment(sketch, "E703", {"start": v(-223.18, 59.35) * mm, "end": v(-221.9, 59.35) * mm});
            skLineSegment(sketch, "E704", {"start": v(-221.9, 59.35) * mm, "end": v(-221.9, 56.35) * mm});
            skLineSegment(sketch, "E705", {"start": v(-221.9, 56.35) * mm, "end": v(-218.7, 56.35) * mm});
            skLineSegment(sketch, "E706", {"start": v(-218.7, 56.35) * mm, "end": v(-218.7, 59.35) * mm});
            skLineSegment(sketch, "E707", {"start": v(-218.7, 59.35) * mm, "end": v(-217.43, 59.35) * mm});
            skLineSegment(sketch, "E708", {"start": v(-217.43, 59.35) * mm, "end": v(-217.43, 63.35) * mm});
            skLineSegment(sketch, "E709", {"start": v(-217.43, 63.35) * mm, "end": v(-218.7, 63.35) * mm});
            skLineSegment(sketch, "E710", {"start": v(-218.7, 63.35) * mm, "end": v(-218.7, 66.35) * mm});
            skLineSegment(sketch, "E711", {"start": v(-218.7, 66.35) * mm, "end": v(-213.57, 66.35) * mm});
            skArc(sketch, "E712", {"start": v(-213.14, 66.1) * mm, "mid": v(-213.32, 66.28) * mm, "end": v(-213.57, 66.35) * mm});
            skArc(sketch, "E713", {"start": v(-213.14, 66.1) * mm, "mid": v(-212.35, 66) * mm, "end": v(-212.46, 66.78) * mm});
            skArc(sketch, "E714", {"start": v(-212.7, 67.21) * mm, "mid": v(-212.64, 66.96) * mm, "end": v(-212.46, 66.78) * mm});
            skLineSegment(sketch, "E715", {"start": v(-212.7, 67.21) * mm, "end": v(-212.7, 68.85) * mm});
            skArc(sketch, "E716", {"start": v(-212.2, 69.35) * mm, "mid": v(-212.56, 69.2) * mm, "end": v(-212.7, 68.85) * mm});
            skLineSegment(sketch, "E717", {"start": v(-212.2, 69.35) * mm, "end": v(-207.2, 69.35) * mm});
            skArc(sketch, "E718", {"start": v(-206.7, 68.85) * mm, "mid": v(-206.85, 69.2) * mm, "end": v(-207.2, 69.35) * mm});
            skLineSegment(sketch, "E719", {"start": v(-206.7, 68.85) * mm, "end": v(-206.7, 67.21) * mm});
            skArc(sketch, "E720", {"start": v(-206.96, 66.78) * mm, "mid": v(-206.77, 66.96) * mm, "end": v(-206.7, 67.21) * mm});
            skArc(sketch, "E721", {"start": v(-206.96, 66.78) * mm, "mid": v(-207.06, 66) * mm, "end": v(-206.27, 66.1) * mm});
            skArc(sketch, "E722", {"start": v(-205.84, 66.35) * mm, "mid": v(-206.09, 66.28) * mm, "end": v(-206.27, 66.1) * mm});
            skLineSegment(sketch, "E723", {"start": v(-205.84, 66.35) * mm, "end": v(-114.77, 66.35) * mm});
            skArc(sketch, "E724", {"start": v(-114.34, 66.1) * mm, "mid": v(-114.52, 66.28) * mm, "end": v(-114.77, 66.35) * mm});
            skArc(sketch, "E725", {"start": v(-114.34, 66.1) * mm, "mid": v(-113.55, 66) * mm, "end": v(-113.66, 66.78) * mm});
            skArc(sketch, "E726", {"start": v(-113.9, 67.21) * mm, "mid": v(-113.84, 66.96) * mm, "end": v(-113.66, 66.78) * mm});
            skLineSegment(sketch, "E727", {"start": v(-113.9, 67.21) * mm, "end": v(-113.9, 68.85) * mm});
            skArc(sketch, "E728", {"start": v(-113.4, 69.35) * mm, "mid": v(-113.76, 69.2) * mm, "end": v(-113.9, 68.85) * mm});
            skLineSegment(sketch, "E729", {"start": v(-113.4, 69.35) * mm, "end": v(-108.4, 69.35) * mm});
            skArc(sketch, "E730", {"start": v(-107.9, 68.85) * mm, "mid": v(-108.05, 69.2) * mm, "end": v(-108.4, 69.35) * mm});
            skLineSegment(sketch, "E731", {"start": v(-107.9, 68.85) * mm, "end": v(-107.9, 67.21) * mm});
            skArc(sketch, "E732", {"start": v(-108.16, 66.78) * mm, "mid": v(-107.97, 66.96) * mm, "end": v(-107.9, 67.21) * mm});
            skArc(sketch, "E733", {"start": v(-108.16, 66.78) * mm, "mid": v(-108.26, 66) * mm, "end": v(-107.47, 66.1) * mm});
            skArc(sketch, "E734", {"start": v(-107.04, 66.35) * mm, "mid": v(-107.29, 66.28) * mm, "end": v(-107.47, 66.1) * mm});
            skLineSegment(sketch, "E735", {"start": v(-107.04, 66.35) * mm, "end": v(-101.9, 66.35) * mm});
            skLineSegment(sketch, "E736", {"start": v(-101.9, 66.35) * mm, "end": v(-101.9, 63.35) * mm});
            skLineSegment(sketch, "E737", {"start": v(-101.9, 63.35) * mm, "end": v(-103.18, 63.35) * mm});
            skLineSegment(sketch, "E738", {"start": v(-103.18, 63.35) * mm, "end": v(-103.18, 59.35) * mm});
            skLineSegment(sketch, "E739", {"start": v(-103.18, 59.35) * mm, "end": v(-101.9, 59.35) * mm});
            skLineSegment(sketch, "E740", {"start": v(-101.9, 59.35) * mm, "end": v(-101.9, 56.35) * mm});
            skLineSegment(sketch, "E741", {"start": v(-101.9, 56.35) * mm, "end": v(-98.7, 56.35) * mm});
            skLineSegment(sketch, "E742", {"start": v(-98.7, 56.35) * mm, "end": v(-98.7, 59.35) * mm});
            skLineSegment(sketch, "E743", {"start": v(-98.7, 59.35) * mm, "end": v(-97.43, 59.35) * mm});
            skLineSegment(sketch, "E744", {"start": v(-97.43, 59.35) * mm, "end": v(-97.43, 63.35) * mm});
            skLineSegment(sketch, "E745", {"start": v(-97.43, 63.35) * mm, "end": v(-98.7, 63.35) * mm});
            skLineSegment(sketch, "E746", {"start": v(-98.7, 63.35) * mm, "end": v(-98.7, 66.35) * mm});
            skLineSegment(sketch, "E747", {"start": v(-98.7, 66.35) * mm, "end": v(-93.57, 66.35) * mm});
            skArc(sketch, "E748", {"start": v(-93.14, 66.1) * mm, "mid": v(-93.32, 66.28) * mm, "end": v(-93.57, 66.35) * mm});
            skArc(sketch, "E749", {"start": v(-93.14, 66.1) * mm, "mid": v(-92.35, 66) * mm, "end": v(-92.46, 66.78) * mm});
            skArc(sketch, "E750", {"start": v(-92.7, 67.21) * mm, "mid": v(-92.64, 66.96) * mm, "end": v(-92.46, 66.78) * mm});
            skLineSegment(sketch, "E751", {"start": v(-92.7, 67.21) * mm, "end": v(-92.7, 68.85) * mm});
            skArc(sketch, "E752", {"start": v(-92.2, 69.35) * mm, "mid": v(-92.56, 69.2) * mm, "end": v(-92.7, 68.85) * mm});
            skLineSegment(sketch, "E753", {"start": v(-92.2, 69.35) * mm, "end": v(-87.2, 69.35) * mm});
            skArc(sketch, "E754", {"start": v(-86.7, 68.85) * mm, "mid": v(-86.85, 69.2) * mm, "end": v(-87.2, 69.35) * mm});
            skLineSegment(sketch, "E755", {"start": v(-86.7, 68.85) * mm, "end": v(-86.7, 67.21) * mm});
            skArc(sketch, "E756", {"start": v(-86.96, 66.78) * mm, "mid": v(-86.77, 66.96) * mm, "end": v(-86.7, 67.21) * mm});
            skArc(sketch, "E757", {"start": v(-86.96, 66.78) * mm, "mid": v(-87.06, 66) * mm, "end": v(-86.27, 66.1) * mm});
            skArc(sketch, "E758", {"start": v(-85.84, 66.35) * mm, "mid": v(-86.09, 66.28) * mm, "end": v(-86.27, 66.1) * mm});
            skLineSegment(sketch, "E759", {"start": v(-85.84, 66.35) * mm, "end": v(45.23, 66.35) * mm});
            skArc(sketch, "E760", {"start": v(45.66, 66.1) * mm, "mid": v(45.48, 66.28) * mm, "end": v(45.23, 66.35) * mm});
            skArc(sketch, "E761", {"start": v(45.66, 66.1) * mm, "mid": v(46.45, 66) * mm, "end": v(46.34, 66.78) * mm});
            skArc(sketch, "E762", {"start": v(46.1, 67.21) * mm, "mid": v(46.16, 66.96) * mm, "end": v(46.34, 66.78) * mm});
            skLineSegment(sketch, "E763", {"start": v(46.1, 67.21) * mm, "end": v(46.1, 68.85) * mm});
            skArc(sketch, "E764", {"start": v(46.6, 69.35) * mm, "mid": v(46.24, 69.2) * mm, "end": v(46.1, 68.85) * mm});
            skLineSegment(sketch, "E765", {"start": v(46.6, 69.35) * mm, "end": v(51.6, 69.35) * mm});
            skArc(sketch, "E766", {"start": v(52.1, 68.85) * mm, "mid": v(51.95, 69.2) * mm, "end": v(51.6, 69.35) * mm});
            skLineSegment(sketch, "E767", {"start": v(52.1, 68.85) * mm, "end": v(52.1, 67.21) * mm});
            skArc(sketch, "E768", {"start": v(51.84, 66.78) * mm, "mid": v(52.03, 66.96) * mm, "end": v(52.1, 67.21) * mm});
            skArc(sketch, "E769", {"start": v(51.84, 66.78) * mm, "mid": v(51.74, 66) * mm, "end": v(52.53, 66.1) * mm});
            skArc(sketch, "E770", {"start": v(52.96, 66.35) * mm, "mid": v(52.71, 66.28) * mm, "end": v(52.53, 66.1) * mm});
            skLineSegment(sketch, "E771", {"start": v(52.96, 66.35) * mm, "end": v(58.1, 66.35) * mm});
            skLineSegment(sketch, "E772", {"start": v(58.1, 66.35) * mm, "end": v(58.1, 63.35) * mm});
            skLineSegment(sketch, "E773", {"start": v(58.1, 63.35) * mm, "end": v(56.82, 63.35) * mm});
            skLineSegment(sketch, "E774", {"start": v(56.82, 63.35) * mm, "end": v(56.82, 59.35) * mm});
            skLineSegment(sketch, "E775", {"start": v(56.82, 59.35) * mm, "end": v(58.1, 59.35) * mm});
            skLineSegment(sketch, "E776", {"start": v(58.1, 59.35) * mm, "end": v(58.1, 56.35) * mm});
            skLineSegment(sketch, "E777", {"start": v(58.1, 56.35) * mm, "end": v(61.3, 56.35) * mm});
            skLineSegment(sketch, "E778", {"start": v(61.3, 56.35) * mm, "end": v(61.3, 59.35) * mm});
            skLineSegment(sketch, "E779", {"start": v(61.3, 59.35) * mm, "end": v(62.57, 59.35) * mm});
            skLineSegment(sketch, "E780", {"start": v(62.57, 59.35) * mm, "end": v(62.57, 63.35) * mm});
            skLineSegment(sketch, "E781", {"start": v(62.57, 63.35) * mm, "end": v(61.3, 63.35) * mm});
            skLineSegment(sketch, "E782", {"start": v(61.3, 63.35) * mm, "end": v(61.3, 66.35) * mm});
            skLineSegment(sketch, "E783", {"start": v(61.3, 66.35) * mm, "end": v(66.43, 66.35) * mm});
            skArc(sketch, "E784", {"start": v(66.86, 66.1) * mm, "mid": v(66.68, 66.28) * mm, "end": v(66.43, 66.35) * mm});
            skArc(sketch, "E785", {"start": v(66.86, 66.1) * mm, "mid": v(67.65, 66) * mm, "end": v(67.54, 66.78) * mm});
            skArc(sketch, "E786", {"start": v(67.3, 67.21) * mm, "mid": v(67.36, 66.96) * mm, "end": v(67.54, 66.78) * mm});
            skLineSegment(sketch, "E787", {"start": v(67.3, 67.21) * mm, "end": v(67.3, 68.85) * mm});
            skArc(sketch, "E788", {"start": v(67.8, 69.35) * mm, "mid": v(67.44, 69.2) * mm, "end": v(67.3, 68.85) * mm});
            skLineSegment(sketch, "E789", {"start": v(67.8, 69.35) * mm, "end": v(72.8, 69.35) * mm});
            skArc(sketch, "E790", {"start": v(73.3, 68.85) * mm, "mid": v(73.15, 69.2) * mm, "end": v(72.8, 69.35) * mm});
            skLineSegment(sketch, "E791", {"start": v(73.3, 68.85) * mm, "end": v(73.3, 67.21) * mm});
            skArc(sketch, "E792", {"start": v(73.04, 66.78) * mm, "mid": v(73.23, 66.96) * mm, "end": v(73.3, 67.21) * mm});
            skArc(sketch, "E793", {"start": v(73.04, 66.78) * mm, "mid": v(72.94, 66) * mm, "end": v(73.73, 66.1) * mm});
            skArc(sketch, "E794", {"start": v(74.16, 66.35) * mm, "mid": v(73.91, 66.28) * mm, "end": v(73.73, 66.1) * mm});
            skLineSegment(sketch, "E795", {"start": v(74.16, 66.35) * mm, "end": v(84.7, 66.35) * mm});
            skLineSegment(sketch, "E796", {"start": v(84.7, 66.35) * mm, "end": v(84.7, 55.7) * mm});
            skLineSegment(sketch, "E797", {"start": v(84.7, 55.7) * mm, "end": v(82.46, 55.7) * mm});
            skArc(sketch, "E798", {"start": v(82.03, 55.95) * mm, "mid": v(82.21, 55.76) * mm, "end": v(82.46, 55.7) * mm});
            skArc(sketch, "E799", {"start": v(82.03, 55.95) * mm, "mid": v(81.24, 56.05) * mm, "end": v(81.34, 55.26) * mm});
            skArc(sketch, "E800", {"start": v(81.6, 54.83) * mm, "mid": v(81.53, 55.08) * mm, "end": v(81.34, 55.26) * mm});
            skLineSegment(sketch, "E801", {"start": v(81.6, 54.83) * mm, "end": v(81.6, 47.3) * mm});
            skLineSegment(sketch, "E802", {"start": v(81.6, 47.3) * mm, "end": v(78.6, 47.3) * mm});
            skLineSegment(sketch, "E803", {"start": v(78.6, 47.3) * mm, "end": v(78.6, 48.57) * mm});
            skLineSegment(sketch, "E804", {"start": v(78.6, 48.57) * mm, "end": v(74.6, 48.57) * mm});
            skLineSegment(sketch, "E805", {"start": v(74.6, 48.57) * mm, "end": v(74.6, 47.3) * mm});
            skLineSegment(sketch, "E806", {"start": v(74.6, 47.3) * mm, "end": v(71.6, 47.3) * mm});
            skLineSegment(sketch, "E807", {"start": v(71.6, 47.3) * mm, "end": v(71.6, 44.1) * mm});
            skLineSegment(sketch, "E808", {"start": v(71.6, 44.1) * mm, "end": v(74.6, 44.1) * mm});
            skLineSegment(sketch, "E809", {"start": v(74.6, 44.1) * mm, "end": v(74.6, 42.82) * mm});
            skLineSegment(sketch, "E810", {"start": v(74.6, 42.82) * mm, "end": v(78.6, 42.82) * mm});
            skLineSegment(sketch, "E811", {"start": v(78.6, 42.82) * mm, "end": v(78.6, 44.1) * mm});
            skLineSegment(sketch, "E812", {"start": v(78.6, 44.1) * mm, "end": v(81.6, 44.1) * mm});
            skLineSegment(sketch, "E813", {"start": v(81.6, 44.1) * mm, "end": v(81.6, 35.35) * mm});
            skLineSegment(sketch, "E814", {"start": v(81.6, 35.35) * mm, "end": v(-240.5, -58.55) * mm});
            skLineSegment(sketch, "E815", {"start": v(-240.86, -63.65) * mm, "end": v(-245.84, -63.65) * mm});
            skLineSegment(sketch, "E816", {"start": v(47.7, 42.35) * mm, "end": v(55.7, 42.35) * mm});
            skArc(sketch, "E817", {"start": v(55.7, 42.35) * mm, "mid": v(59.7, 46.35) * mm, "end": v(55.7, 50.35) * mm});
            skLineSegment(sketch, "E818", {"start": v(55.7, 50.35) * mm, "end": v(47.7, 50.35) * mm});
            skArc(sketch, "E819", {"start": v(47.7, 50.35) * mm, "mid": v(43.7, 46.35) * mm, "end": v(47.7, 42.35) * mm});
            skLineSegment(sketch, "E820", {"start": v(-12.3, 42.35) * mm, "end": v(-4.3, 42.35) * mm});
            skArc(sketch, "E821", {"start": v(-4.3, 42.35) * mm, "mid": v(-0.3, 46.35) * mm, "end": v(-4.3, 50.35) * mm});
            skLineSegment(sketch, "E822", {"start": v(-4.3, 50.35) * mm, "end": v(-12.3, 50.35) * mm});
            skArc(sketch, "E823", {"start": v(-12.3, 50.35) * mm, "mid": v(-16.3, 46.35) * mm, "end": v(-12.3, 42.35) * mm});
            skLineSegment(sketch, "E824", {"start": v(-72.3, 42.35) * mm, "end": v(-64.3, 42.35) * mm});
            skArc(sketch, "E825", {"start": v(-64.3, 42.35) * mm, "mid": v(-60.3, 46.35) * mm, "end": v(-64.3, 50.35) * mm});
            skLineSegment(sketch, "E826", {"start": v(-64.3, 50.35) * mm, "end": v(-72.3, 50.35) * mm});
            skArc(sketch, "E827", {"start": v(-72.3, 50.35) * mm, "mid": v(-76.3, 46.35) * mm, "end": v(-72.3, 42.35) * mm});
            skLineSegment(sketch, "E828", {"start": v(-132.3, 42.35) * mm, "end": v(-124.3, 42.35) * mm});
            skArc(sketch, "E829", {"start": v(-124.3, 42.35) * mm, "mid": v(-120.3, 46.35) * mm, "end": v(-124.3, 50.35) * mm});
            skLineSegment(sketch, "E830", {"start": v(-124.3, 50.35) * mm, "end": v(-132.3, 50.35) * mm});
            skArc(sketch, "E831", {"start": v(-132.3, 50.35) * mm, "mid": v(-136.3, 46.35) * mm, "end": v(-132.3, 42.35) * mm});
            skLineSegment(sketch, "E832", {"start": v(-192.3, 51.35) * mm, "end": v(-192.3, 43.35) * mm});
            skArc(sketch, "E833", {"start": v(-192.3, 43.35) * mm, "mid": v(-188.3, 39.35) * mm, "end": v(-184.3, 43.35) * mm});
            skLineSegment(sketch, "E834", {"start": v(-184.3, 43.35) * mm, "end": v(-184.3, 51.35) * mm});
            skArc(sketch, "E835", {"start": v(-184.3, 51.35) * mm, "mid": v(-188.3, 55.35) * mm, "end": v(-192.3, 51.35) * mm});
            skLineSegment(sketch, "E836", {"start": v(-192.3, 11.35) * mm, "end": v(-192.3, 3.35) * mm});
            skArc(sketch, "E837", {"start": v(-192.3, 3.35) * mm, "mid": v(-188.3, -0.65) * mm, "end": v(-184.3, 3.35) * mm});
            skLineSegment(sketch, "E838", {"start": v(-184.3, 3.35) * mm, "end": v(-184.3, 11.35) * mm});
            skArc(sketch, "E839", {"start": v(-184.3, 11.35) * mm, "mid": v(-188.3, 15.35) * mm, "end": v(-192.3, 11.35) * mm});
            skLineSegment(sketch, "E840", {"start": v(-277.3, 51.35) * mm, "end": v(-277.3, 43.35) * mm});
            skArc(sketch, "E841", {"start": v(-277.3, 43.35) * mm, "mid": v(-273.3, 39.35) * mm, "end": v(-269.3, 43.35) * mm});
            skLineSegment(sketch, "E842", {"start": v(-269.3, 43.35) * mm, "end": v(-269.3, 51.35) * mm});
            skArc(sketch, "E843", {"start": v(-269.3, 51.35) * mm, "mid": v(-273.3, 55.35) * mm, "end": v(-277.3, 51.35) * mm});
            skLineSegment(sketch, "E844", {"start": v(-277.3, 11.35) * mm, "end": v(-277.3, 3.35) * mm});
            skArc(sketch, "E845", {"start": v(-277.3, 3.35) * mm, "mid": v(-273.3, -0.65) * mm, "end": v(-269.3, 3.35) * mm});
            skLineSegment(sketch, "E846", {"start": v(-269.3, 3.35) * mm, "end": v(-269.3, 11.35) * mm});
            skArc(sketch, "E847", {"start": v(-269.3, 11.35) * mm, "mid": v(-273.3, 15.35) * mm, "end": v(-277.3, 11.35) * mm});
            skLineSegment(sketch, "E848", {"start": v(-277.3, -28.65) * mm, "end": v(-277.3, -36.65) * mm});
            skArc(sketch, "E849", {"start": v(-277.3, -36.65) * mm, "mid": v(-273.3, -40.65) * mm, "end": v(-269.3, -36.65) * mm});
            skLineSegment(sketch, "E850", {"start": v(-269.3, -36.65) * mm, "end": v(-269.3, -28.65) * mm});
            skArc(sketch, "E851", {"start": v(-269.3, -28.65) * mm, "mid": v(-273.3, -24.65) * mm, "end": v(-277.3, -28.65) * mm});
            skCircle(sketch, "E852", {"center": v(-208.27, 53.55) * mm, "radius": 1.3 * mm});
            skCircle(sketch, "E853", {"center": v(-208.3, -29.65) * mm, "radius": 1.3 * mm});
            skCircle(sketch, "E854", {"center": v(-256.47, 47.35) * mm, "radius": 1.3 * mm});
            skCircle(sketch, "E855", {"center": v(-256.49, -27.15) * mm, "radius": 1.3 * mm});
            skArc(sketch, "E856", {"start": v(-110.47, -34.37) * mm, "mid": v(-110.72, -34.44) * mm, "end": v(-110.9, -34.62) * mm});
            skArc(sketch, "E857", {"start": v(-111.58, -33.94) * mm, "mid": v(-111.69, -34.72) * mm, "end": v(-110.9, -34.62) * mm});
            skArc(sketch, "E858", {"start": v(-111.58, -33.94) * mm, "mid": v(-111.4, -33.75) * mm, "end": v(-111.33, -33.5) * mm});
            skLineSegment(sketch, "E859", {"start": v(-111.33, -33.5) * mm, "end": v(-111.33, -31.87) * mm});
            skArc(sketch, "E860", {"start": v(-111.33, -31.87) * mm, "mid": v(-111.48, -31.52) * mm, "end": v(-111.83, -31.37) * mm});
            skLineSegment(sketch, "E861", {"start": v(-111.83, -31.37) * mm, "end": v(-116.83, -31.37) * mm});
            skArc(sketch, "E862", {"start": v(-116.83, -31.37) * mm, "mid": v(-117.19, -31.52) * mm, "end": v(-117.33, -31.87) * mm});
            skLineSegment(sketch, "E863", {"start": v(-117.33, -31.87) * mm, "end": v(-117.33, -33.5) * mm});
            skArc(sketch, "E864", {"start": v(-117.33, -33.5) * mm, "mid": v(-117.27, -33.75) * mm, "end": v(-117.08, -33.94) * mm});
            skArc(sketch, "E865", {"start": v(-117.77, -34.62) * mm, "mid": v(-116.98, -34.72) * mm, "end": v(-117.08, -33.94) * mm});
            skArc(sketch, "E866", {"start": v(-117.77, -34.62) * mm, "mid": v(-117.95, -34.44) * mm, "end": v(-118.2, -34.37) * mm});
            skLineSegment(sketch, "E867", {"start": v(-118.2, -34.37) * mm, "end": v(-122.73, -34.37) * mm});
            skLineSegment(sketch, "E868", {"start": v(-122.73, -34.37) * mm, "end": v(-122.73, -47.78) * mm});
            skArc(sketch, "E869", {"start": v(-122.73, -47.78) * mm, "mid": v(-122.3, -49.02) * mm, "end": v(-121.18, -49.73) * mm});
            skLineSegment(sketch, "E870", {"start": v(-121.18, -49.73) * mm, "end": v(-93.31, -56.19) * mm});
            skArc(sketch, "E871", {"start": v(-93.31, -56.19) * mm, "mid": v(-87.38, -54.85) * mm, "end": v(-84.73, -49.37) * mm});
            skLineSegment(sketch, "E872", {"start": v(-84.73, -49.37) * mm, "end": v(-84.73, -34.37) * mm});
            skLineSegment(sketch, "E873", {"start": v(-84.73, -34.37) * mm, "end": v(-89.27, -34.37) * mm});
            skArc(sketch, "E874", {"start": v(-89.27, -34.37) * mm, "mid": v(-89.52, -34.44) * mm, "end": v(-89.7, -34.62) * mm});
            skArc(sketch, "E875", {"start": v(-90.38, -33.94) * mm, "mid": v(-90.49, -34.72) * mm, "end": v(-89.7, -34.62) * mm});
            skArc(sketch, "E876", {"start": v(-90.38, -33.94) * mm, "mid": v(-90.2, -33.75) * mm, "end": v(-90.13, -33.5) * mm});
            skLineSegment(sketch, "E877", {"start": v(-90.13, -33.5) * mm, "end": v(-90.13, -31.87) * mm});
            skArc(sketch, "E878", {"start": v(-90.13, -31.87) * mm, "mid": v(-90.28, -31.52) * mm, "end": v(-90.63, -31.37) * mm});
            skLineSegment(sketch, "E879", {"start": v(-90.63, -31.37) * mm, "end": v(-95.63, -31.37) * mm});
            skArc(sketch, "E880", {"start": v(-95.63, -31.37) * mm, "mid": v(-95.99, -31.52) * mm, "end": v(-96.13, -31.87) * mm});
            skLineSegment(sketch, "E881", {"start": v(-96.13, -31.87) * mm, "end": v(-96.13, -33.5) * mm});
            skArc(sketch, "E882", {"start": v(-96.13, -33.5) * mm, "mid": v(-96.07, -33.75) * mm, "end": v(-95.88, -33.94) * mm});
            skArc(sketch, "E883", {"start": v(-96.57, -34.62) * mm, "mid": v(-95.78, -34.72) * mm, "end": v(-95.88, -33.94) * mm});
            skArc(sketch, "E884", {"start": v(-96.57, -34.62) * mm, "mid": v(-96.75, -34.44) * mm, "end": v(-97, -34.37) * mm});
            skLineSegment(sketch, "E885", {"start": v(-97, -34.37) * mm, "end": v(-102.13, -34.37) * mm});
            skLineSegment(sketch, "E886", {"start": v(-102.13, -34.37) * mm, "end": v(-102.13, -37.37) * mm});
            skLineSegment(sketch, "E887", {"start": v(-102.13, -37.37) * mm, "end": v(-100.86, -37.37) * mm});
            skLineSegment(sketch, "E888", {"start": v(-100.86, -37.37) * mm, "end": v(-100.86, -41.37) * mm});
            skLineSegment(sketch, "E889", {"start": v(-100.86, -41.37) * mm, "end": v(-102.13, -41.37) * mm});
            skLineSegment(sketch, "E890", {"start": v(-102.13, -41.37) * mm, "end": v(-102.13, -44.37) * mm});
            skLineSegment(sketch, "E891", {"start": v(-102.13, -44.37) * mm, "end": v(-105.33, -44.37) * mm});
            skLineSegment(sketch, "E892", {"start": v(-105.33, -44.37) * mm, "end": v(-105.33, -41.37) * mm});
            skLineSegment(sketch, "E893", {"start": v(-105.33, -41.37) * mm, "end": v(-106.6, -41.37) * mm});
            skLineSegment(sketch, "E894", {"start": v(-106.6, -41.37) * mm, "end": v(-106.6, -37.37) * mm});
            skLineSegment(sketch, "E895", {"start": v(-106.6, -37.37) * mm, "end": v(-105.33, -37.37) * mm});
            skLineSegment(sketch, "E896", {"start": v(-105.33, -37.37) * mm, "end": v(-105.33, -34.37) * mm});
            skLineSegment(sketch, "E897", {"start": v(-105.33, -34.37) * mm, "end": v(-110.47, -34.37) * mm});
            skCircle(sketch, "E898", {"center": v(-91.73, -49.37) * mm, "radius": 4 * mm});
            skArc(sketch, "E899", {"start": v(-62.8, 312.28) * mm, "mid": v(-63.05, 312.22) * mm, "end": v(-63.23, 312.03) * mm});
            skArc(sketch, "E900", {"start": v(-63.91, 312.72) * mm, "mid": v(-64.02, 311.93) * mm, "end": v(-63.23, 312.03) * mm});
            skArc(sketch, "E901", {"start": v(-63.91, 312.72) * mm, "mid": v(-63.73, 312.9) * mm, "end": v(-63.66, 313.15) * mm});
            skLineSegment(sketch, "E902", {"start": v(-63.66, 313.15) * mm, "end": v(-63.66, 314.78) * mm});
            skArc(sketch, "E903", {"start": v(-63.66, 314.78) * mm, "mid": v(-63.81, 315.14) * mm, "end": v(-64.16, 315.28) * mm});
            skLineSegment(sketch, "E904", {"start": v(-64.16, 315.28) * mm, "end": v(-69.16, 315.28) * mm});
            skArc(sketch, "E905", {"start": v(-69.16, 315.28) * mm, "mid": v(-69.52, 315.14) * mm, "end": v(-69.66, 314.78) * mm});
            skLineSegment(sketch, "E906", {"start": v(-69.66, 314.78) * mm, "end": v(-69.66, 313.15) * mm});
            skArc(sketch, "E907", {"start": v(-69.66, 313.15) * mm, "mid": v(-69.6, 312.9) * mm, "end": v(-69.41, 312.72) * mm});
            skArc(sketch, "E908", {"start": v(-70.1, 312.03) * mm, "mid": v(-69.31, 311.93) * mm, "end": v(-69.41, 312.72) * mm});
            skArc(sketch, "E909", {"start": v(-70.1, 312.03) * mm, "mid": v(-70.28, 312.22) * mm, "end": v(-70.53, 312.28) * mm});
            skLineSegment(sketch, "E910", {"start": v(-70.53, 312.28) * mm, "end": v(-75.06, 312.28) * mm});
            skLineSegment(sketch, "E911", {"start": v(-75.06, 312.28) * mm, "end": v(-75.06, 298.87) * mm});
            skArc(sketch, "E912", {"start": v(-75.06, 298.87) * mm, "mid": v(-74.63, 297.63) * mm, "end": v(-73.52, 296.92) * mm});
            skLineSegment(sketch, "E913", {"start": v(-73.52, 296.92) * mm, "end": v(-45.64, 290.46) * mm});
            skArc(sketch, "E914", {"start": v(-45.64, 290.46) * mm, "mid": v(-39.7, 291.8) * mm, "end": v(-37.06, 297.28) * mm});
            skLineSegment(sketch, "E915", {"start": v(-37.06, 297.28) * mm, "end": v(-37.06, 312.28) * mm});
            skLineSegment(sketch, "E916", {"start": v(-37.06, 312.28) * mm, "end": v(-41.6, 312.28) * mm});
            skArc(sketch, "E917", {"start": v(-41.6, 312.28) * mm, "mid": v(-41.85, 312.22) * mm, "end": v(-42.03, 312.03) * mm});
            skArc(sketch, "E918", {"start": v(-42.71, 312.72) * mm, "mid": v(-42.82, 311.93) * mm, "end": v(-42.03, 312.03) * mm});
            skArc(sketch, "E919", {"start": v(-42.71, 312.72) * mm, "mid": v(-42.53, 312.9) * mm, "end": v(-42.46, 313.15) * mm});
            skLineSegment(sketch, "E920", {"start": v(-42.46, 313.15) * mm, "end": v(-42.46, 314.78) * mm});
            skArc(sketch, "E921", {"start": v(-42.46, 314.78) * mm, "mid": v(-42.61, 315.14) * mm, "end": v(-42.96, 315.28) * mm});
            skLineSegment(sketch, "E922", {"start": v(-42.96, 315.28) * mm, "end": v(-47.96, 315.28) * mm});
            skArc(sketch, "E923", {"start": v(-47.96, 315.28) * mm, "mid": v(-48.32, 315.14) * mm, "end": v(-48.46, 314.78) * mm});
            skLineSegment(sketch, "E924", {"start": v(-48.46, 314.78) * mm, "end": v(-48.46, 313.15) * mm});
            skArc(sketch, "E925", {"start": v(-48.46, 313.15) * mm, "mid": v(-48.4, 312.9) * mm, "end": v(-48.21, 312.72) * mm});
            skArc(sketch, "E926", {"start": v(-48.9, 312.03) * mm, "mid": v(-48.11, 311.93) * mm, "end": v(-48.21, 312.72) * mm});
            skArc(sketch, "E927", {"start": v(-48.9, 312.03) * mm, "mid": v(-49.08, 312.22) * mm, "end": v(-49.33, 312.28) * mm});
            skLineSegment(sketch, "E928", {"start": v(-49.33, 312.28) * mm, "end": v(-54.46, 312.28) * mm});
            skLineSegment(sketch, "E929", {"start": v(-54.46, 312.28) * mm, "end": v(-54.46, 309.28) * mm});
            skLineSegment(sketch, "E930", {"start": v(-54.46, 309.28) * mm, "end": v(-53.19, 309.28) * mm});
            skLineSegment(sketch, "E931", {"start": v(-53.19, 309.28) * mm, "end": v(-53.19, 305.28) * mm});
            skLineSegment(sketch, "E932", {"start": v(-53.19, 305.28) * mm, "end": v(-54.46, 305.28) * mm});
            skLineSegment(sketch, "E933", {"start": v(-54.46, 305.28) * mm, "end": v(-54.46, 302.28) * mm});
            skLineSegment(sketch, "E934", {"start": v(-54.46, 302.28) * mm, "end": v(-57.66, 302.28) * mm});
            skLineSegment(sketch, "E935", {"start": v(-57.66, 302.28) * mm, "end": v(-57.66, 305.28) * mm});
            skLineSegment(sketch, "E936", {"start": v(-57.66, 305.28) * mm, "end": v(-58.94, 305.28) * mm});
            skLineSegment(sketch, "E937", {"start": v(-58.94, 305.28) * mm, "end": v(-58.94, 309.28) * mm});
            skLineSegment(sketch, "E938", {"start": v(-58.94, 309.28) * mm, "end": v(-57.66, 309.28) * mm});
            skLineSegment(sketch, "E939", {"start": v(-57.66, 309.28) * mm, "end": v(-57.66, 312.28) * mm});
            skLineSegment(sketch, "E940", {"start": v(-57.66, 312.28) * mm, "end": v(-62.8, 312.28) * mm});
            skCircle(sketch, "E941", {"center": v(-44.06, 297.28) * mm, "radius": 4 * mm});
            skLineSegment(sketch, "E942", {"start": v(173.27, -10.63) * mm, "end": v(186.97, -34.37) * mm});
            skArc(sketch, "E943", {"start": v(184.37, -38.87) * mm, "mid": v(186.97, -37.37) * mm, "end": v(186.97, -34.37) * mm});
            skLineSegment(sketch, "E944", {"start": v(167.67, -35.87) * mm, "end": v(167.67, -12.13) * mm});
            skArc(sketch, "E945", {"start": v(173.27, -10.63) * mm, "mid": v(169.9, -9.24) * mm, "end": v(167.67, -12.13) * mm});
            skLineSegment(sketch, "E946", {"start": v(170.67, -38.87) * mm, "end": v(184.37, -38.87) * mm});
            skArc(sketch, "E947", {"start": v(167.67, -35.87) * mm, "mid": v(168.55, -37.99) * mm, "end": v(170.67, -38.87) * mm});
            skLineSegment(sketch, "E948", {"start": v(173.27, 271.61) * mm, "end": v(186.97, 295.35) * mm});
            skArc(sketch, "E949", {"start": v(186.97, 295.35) * mm, "mid": v(186.97, 298.35) * mm, "end": v(184.37, 299.85) * mm});
            skLineSegment(sketch, "E950", {"start": v(167.67, 296.85) * mm, "end": v(167.67, 273.11) * mm});
            skArc(sketch, "E951", {"start": v(167.67, 273.11) * mm, "mid": v(169.9, 270.22) * mm, "end": v(173.27, 271.61) * mm});
            skLineSegment(sketch, "E952", {"start": v(170.67, 299.85) * mm, "end": v(184.37, 299.85) * mm});
            skArc(sketch, "E953", {"start": v(170.67, 299.85) * mm, "mid": v(168.55, 298.97) * mm, "end": v(167.67, 296.85) * mm});
            skCircle(sketch, "E954", {"center": v(163.33, 109.23) * mm, "radius": 1.6 * mm});
            skCircle(sketch, "E955", {"center": v(163.33, 151.74) * mm, "radius": 1.6 * mm});
            skCircle(sketch, "E956", {"center": v(163.33, 194.24) * mm, "radius": 1.6 * mm});
            skCircle(sketch, "E957", {"center": v(163.33, 64.2) * mm, "radius": 1.6 * mm});
            skArc(sketch, "E958", {"start": v(482.54, 58.26) * mm, "mid": v(482.3, 58.2) * mm, "end": v(482.11, 58.01) * mm});
            skArc(sketch, "E959", {"start": v(481.43, 58.7) * mm, "mid": v(481.33, 57.91) * mm, "end": v(482.11, 58.01) * mm});
            skArc(sketch, "E960", {"start": v(481.43, 58.7) * mm, "mid": v(481.61, 58.88) * mm, "end": v(481.68, 59.13) * mm});
            skLineSegment(sketch, "E961", {"start": v(481.68, 59.13) * mm, "end": v(481.68, 63.6) * mm});
            skArc(sketch, "E962", {"start": v(481.68, 63.6) * mm, "mid": v(481.61, 63.85) * mm, "end": v(481.43, 64.03) * mm});
            skArc(sketch, "E963", {"start": v(482.11, 64.71) * mm, "mid": v(481.33, 64.82) * mm, "end": v(481.43, 64.03) * mm});
            skArc(sketch, "E964", {"start": v(482.11, 64.71) * mm, "mid": v(482.3, 64.53) * mm, "end": v(482.54, 64.46) * mm});
            skLineSegment(sketch, "E965", {"start": v(482.54, 64.46) * mm, "end": v(484.11, 64.46) * mm});
            skArc(sketch, "E966", {"start": v(484.11, 64.46) * mm, "mid": v(484.36, 64.53) * mm, "end": v(484.55, 64.71) * mm});
            skArc(sketch, "E967", {"start": v(485.23, 64.03) * mm, "mid": v(485.33, 64.82) * mm, "end": v(484.55, 64.71) * mm});
            skArc(sketch, "E968", {"start": v(485.23, 64.03) * mm, "mid": v(485.05, 63.85) * mm, "end": v(484.98, 63.6) * mm});
            skLineSegment(sketch, "E969", {"start": v(484.98, 63.6) * mm, "end": v(484.98, 59.13) * mm});
            skArc(sketch, "E970", {"start": v(484.98, 59.13) * mm, "mid": v(485.05, 58.88) * mm, "end": v(485.23, 58.7) * mm});
            skArc(sketch, "E971", {"start": v(484.55, 58.01) * mm, "mid": v(485.33, 57.91) * mm, "end": v(485.23, 58.7) * mm});
            skArc(sketch, "E972", {"start": v(484.55, 58.01) * mm, "mid": v(484.36, 58.2) * mm, "end": v(484.11, 58.26) * mm});
            skLineSegment(sketch, "E973", {"start": v(484.11, 58.26) * mm, "end": v(482.54, 58.26) * mm});
            skArc(sketch, "E974", {"start": v(482.54, 79.46) * mm, "mid": v(482.3, 79.4) * mm, "end": v(482.11, 79.21) * mm});
            skArc(sketch, "E975", {"start": v(481.43, 79.9) * mm, "mid": v(481.33, 79.11) * mm, "end": v(482.11, 79.21) * mm});
            skArc(sketch, "E976", {"start": v(481.43, 79.9) * mm, "mid": v(481.61, 80.08) * mm, "end": v(481.68, 80.33) * mm});
            skLineSegment(sketch, "E977", {"start": v(481.68, 80.33) * mm, "end": v(481.68, 84.8) * mm});
            skArc(sketch, "E978", {"start": v(481.68, 84.8) * mm, "mid": v(481.61, 85.05) * mm, "end": v(481.43, 85.23) * mm});
            skArc(sketch, "E979", {"start": v(482.11, 85.91) * mm, "mid": v(481.33, 86.02) * mm, "end": v(481.43, 85.23) * mm});
            skArc(sketch, "E980", {"start": v(482.11, 85.91) * mm, "mid": v(482.3, 85.73) * mm, "end": v(482.54, 85.66) * mm});
            skLineSegment(sketch, "E981", {"start": v(482.54, 85.66) * mm, "end": v(484.11, 85.66) * mm});
            skArc(sketch, "E982", {"start": v(484.11, 85.66) * mm, "mid": v(484.36, 85.73) * mm, "end": v(484.55, 85.91) * mm});
            skArc(sketch, "E983", {"start": v(485.23, 85.23) * mm, "mid": v(485.33, 86.02) * mm, "end": v(484.55, 85.91) * mm});
            skArc(sketch, "E984", {"start": v(485.23, 85.23) * mm, "mid": v(485.05, 85.05) * mm, "end": v(484.98, 84.8) * mm});
            skLineSegment(sketch, "E985", {"start": v(484.98, 84.8) * mm, "end": v(484.98, 80.33) * mm});
            skArc(sketch, "E986", {"start": v(484.98, 80.33) * mm, "mid": v(485.05, 80.08) * mm, "end": v(485.23, 79.9) * mm});
            skArc(sketch, "E987", {"start": v(484.55, 79.21) * mm, "mid": v(485.33, 79.11) * mm, "end": v(485.23, 79.9) * mm});
            skArc(sketch, "E988", {"start": v(484.55, 79.21) * mm, "mid": v(484.36, 79.4) * mm, "end": v(484.11, 79.46) * mm});
            skLineSegment(sketch, "E989", {"start": v(484.11, 79.46) * mm, "end": v(482.54, 79.46) * mm});
            skCircle(sketch, "E990", {"center": v(483.33, 71.96) * mm, "radius": 1.6 * mm});
            skArc(sketch, "E991", {"start": v(-261.09, 136.85) * mm, "mid": v(-261.34, 136.78) * mm, "end": v(-261.52, 136.6) * mm});
            skArc(sketch, "E992", {"start": v(-262.2, 137.28) * mm, "mid": v(-262.3, 136.5) * mm, "end": v(-261.52, 136.6) * mm});
            skArc(sketch, "E993", {"start": v(-262.2, 137.28) * mm, "mid": v(-262.02, 137.46) * mm, "end": v(-261.96, 137.71) * mm});
            skLineSegment(sketch, "E994", {"start": v(-261.96, 137.71) * mm, "end": v(-261.96, 142.18) * mm});
            skArc(sketch, "E995", {"start": v(-261.96, 142.18) * mm, "mid": v(-262.02, 142.43) * mm, "end": v(-262.2, 142.61) * mm});
            skArc(sketch, "E996", {"start": v(-261.52, 143.3) * mm, "mid": v(-262.3, 143.4) * mm, "end": v(-262.2, 142.61) * mm});
            skArc(sketch, "E997", {"start": v(-261.52, 143.3) * mm, "mid": v(-261.34, 143.11) * mm, "end": v(-261.09, 143.05) * mm});
            skLineSegment(sketch, "E998", {"start": v(-261.09, 143.05) * mm, "end": v(-259.52, 143.05) * mm});
            skArc(sketch, "E999", {"start": v(-259.52, 143.05) * mm, "mid": v(-259.27, 143.11) * mm, "end": v(-259.09, 143.3) * mm});
            skArc(sketch, "E1000", {"start": v(-258.4, 142.61) * mm, "mid": v(-258.3, 143.4) * mm, "end": v(-259.09, 143.3) * mm});
            skArc(sketch, "E1001", {"start": v(-258.4, 142.61) * mm, "mid": v(-258.59, 142.43) * mm, "end": v(-258.66, 142.18) * mm});
            skLineSegment(sketch, "E1002", {"start": v(-258.66, 142.18) * mm, "end": v(-258.66, 137.71) * mm});
            skArc(sketch, "E1003", {"start": v(-258.66, 137.71) * mm, "mid": v(-258.59, 137.46) * mm, "end": v(-258.4, 137.28) * mm});
            skArc(sketch, "E1004", {"start": v(-259.09, 136.6) * mm, "mid": v(-258.3, 136.5) * mm, "end": v(-258.4, 137.28) * mm});
            skArc(sketch, "E1005", {"start": v(-259.09, 136.6) * mm, "mid": v(-259.27, 136.78) * mm, "end": v(-259.52, 136.85) * mm});
            skLineSegment(sketch, "E1006", {"start": v(-259.52, 136.85) * mm, "end": v(-261.09, 136.85) * mm});
            skArc(sketch, "E1007", {"start": v(-261.09, 115.65) * mm, "mid": v(-261.34, 115.58) * mm, "end": v(-261.52, 115.4) * mm});
            skArc(sketch, "E1008", {"start": v(-262.2, 116.08) * mm, "mid": v(-262.3, 115.3) * mm, "end": v(-261.52, 115.4) * mm});
            skArc(sketch, "E1009", {"start": v(-262.2, 116.08) * mm, "mid": v(-262.02, 116.26) * mm, "end": v(-261.96, 116.51) * mm});
            skLineSegment(sketch, "E1010", {"start": v(-261.96, 116.51) * mm, "end": v(-261.96, 120.98) * mm});
            skArc(sketch, "E1011", {"start": v(-261.96, 120.98) * mm, "mid": v(-262.02, 121.23) * mm, "end": v(-262.2, 121.41) * mm});
            skArc(sketch, "E1012", {"start": v(-261.52, 122.1) * mm, "mid": v(-262.3, 122.2) * mm, "end": v(-262.2, 121.41) * mm});
            skArc(sketch, "E1013", {"start": v(-261.52, 122.1) * mm, "mid": v(-261.34, 121.91) * mm, "end": v(-261.09, 121.85) * mm});
            skLineSegment(sketch, "E1014", {"start": v(-261.09, 121.85) * mm, "end": v(-259.52, 121.85) * mm});
            skArc(sketch, "E1015", {"start": v(-259.52, 121.85) * mm, "mid": v(-259.27, 121.91) * mm, "end": v(-259.09, 122.1) * mm});
            skArc(sketch, "E1016", {"start": v(-258.4, 121.41) * mm, "mid": v(-258.3, 122.2) * mm, "end": v(-259.09, 122.1) * mm});
            skArc(sketch, "E1017", {"start": v(-258.4, 121.41) * mm, "mid": v(-258.59, 121.23) * mm, "end": v(-258.66, 120.98) * mm});
            skLineSegment(sketch, "E1018", {"start": v(-258.66, 120.98) * mm, "end": v(-258.66, 116.51) * mm});
            skArc(sketch, "E1019", {"start": v(-258.66, 116.51) * mm, "mid": v(-258.59, 116.26) * mm, "end": v(-258.4, 116.08) * mm});
            skArc(sketch, "E1020", {"start": v(-259.09, 115.4) * mm, "mid": v(-258.3, 115.3) * mm, "end": v(-258.4, 116.08) * mm});
            skArc(sketch, "E1021", {"start": v(-259.09, 115.4) * mm, "mid": v(-259.27, 115.58) * mm, "end": v(-259.52, 115.65) * mm});
            skLineSegment(sketch, "E1022", {"start": v(-259.52, 115.65) * mm, "end": v(-261.09, 115.65) * mm});
            skCircle(sketch, "E1023", {"center": v(-260.3, 129.35) * mm, "radius": 1.6 * mm});
            skArc(sketch, "E1024", {"start": v(482.54, 175.31) * mm, "mid": v(482.3, 175.25) * mm, "end": v(482.11, 175.06) * mm});
            skArc(sketch, "E1025", {"start": v(481.43, 175.75) * mm, "mid": v(481.33, 174.96) * mm, "end": v(482.11, 175.06) * mm});
            skArc(sketch, "E1026", {"start": v(481.43, 175.75) * mm, "mid": v(481.61, 175.93) * mm, "end": v(481.68, 176.18) * mm});
            skLineSegment(sketch, "E1027", {"start": v(481.68, 176.18) * mm, "end": v(481.68, 180.65) * mm});
            skArc(sketch, "E1028", {"start": v(481.68, 180.65) * mm, "mid": v(481.61, 180.9) * mm, "end": v(481.43, 181.08) * mm});
            skArc(sketch, "E1029", {"start": v(482.11, 181.76) * mm, "mid": v(481.33, 181.87) * mm, "end": v(481.43, 181.08) * mm});
            skArc(sketch, "E1030", {"start": v(482.11, 181.76) * mm, "mid": v(482.3, 181.58) * mm, "end": v(482.54, 181.51) * mm});
            skLineSegment(sketch, "E1031", {"start": v(482.54, 181.51) * mm, "end": v(484.11, 181.51) * mm});
            skArc(sketch, "E1032", {"start": v(484.11, 181.51) * mm, "mid": v(484.36, 181.58) * mm, "end": v(484.55, 181.76) * mm});
            skArc(sketch, "E1033", {"start": v(485.23, 181.08) * mm, "mid": v(485.33, 181.87) * mm, "end": v(484.55, 181.76) * mm});
            skArc(sketch, "E1034", {"start": v(485.23, 181.08) * mm, "mid": v(485.05, 180.9) * mm, "end": v(484.98, 180.65) * mm});
            skLineSegment(sketch, "E1035", {"start": v(484.98, 180.65) * mm, "end": v(484.98, 176.18) * mm});
            skArc(sketch, "E1036", {"start": v(484.98, 176.18) * mm, "mid": v(485.05, 175.93) * mm, "end": v(485.23, 175.75) * mm});
            skArc(sketch, "E1037", {"start": v(484.55, 175.06) * mm, "mid": v(485.33, 174.96) * mm, "end": v(485.23, 175.75) * mm});
            skArc(sketch, "E1038", {"start": v(484.55, 175.06) * mm, "mid": v(484.36, 175.25) * mm, "end": v(484.11, 175.31) * mm});
            skLineSegment(sketch, "E1039", {"start": v(484.11, 175.31) * mm, "end": v(482.54, 175.31) * mm});
            skArc(sketch, "E1040", {"start": v(482.54, 196.51) * mm, "mid": v(482.3, 196.45) * mm, "end": v(482.11, 196.26) * mm});
            skArc(sketch, "E1041", {"start": v(481.43, 196.95) * mm, "mid": v(481.33, 196.16) * mm, "end": v(482.11, 196.26) * mm});
            skArc(sketch, "E1042", {"start": v(481.43, 196.95) * mm, "mid": v(481.61, 197.13) * mm, "end": v(481.68, 197.38) * mm});
            skLineSegment(sketch, "E1043", {"start": v(481.68, 197.38) * mm, "end": v(481.68, 201.85) * mm});
            skArc(sketch, "E1044", {"start": v(481.68, 201.85) * mm, "mid": v(481.61, 202.1) * mm, "end": v(481.43, 202.28) * mm});
            skArc(sketch, "E1045", {"start": v(482.11, 202.96) * mm, "mid": v(481.33, 203.07) * mm, "end": v(481.43, 202.28) * mm});
            skArc(sketch, "E1046", {"start": v(482.11, 202.96) * mm, "mid": v(482.3, 202.78) * mm, "end": v(482.54, 202.71) * mm});
            skLineSegment(sketch, "E1047", {"start": v(482.54, 202.71) * mm, "end": v(484.11, 202.71) * mm});
            skArc(sketch, "E1048", {"start": v(484.11, 202.71) * mm, "mid": v(484.36, 202.78) * mm, "end": v(484.55, 202.96) * mm});
            skArc(sketch, "E1049", {"start": v(485.23, 202.28) * mm, "mid": v(485.33, 203.07) * mm, "end": v(484.55, 202.96) * mm});
            skArc(sketch, "E1050", {"start": v(485.23, 202.28) * mm, "mid": v(485.05, 202.1) * mm, "end": v(484.98, 201.85) * mm});
            skLineSegment(sketch, "E1051", {"start": v(484.98, 201.85) * mm, "end": v(484.98, 197.38) * mm});
            skArc(sketch, "E1052", {"start": v(484.98, 197.38) * mm, "mid": v(485.05, 197.13) * mm, "end": v(485.23, 196.95) * mm});
            skArc(sketch, "E1053", {"start": v(484.55, 196.26) * mm, "mid": v(485.33, 196.16) * mm, "end": v(485.23, 196.95) * mm});
            skArc(sketch, "E1054", {"start": v(484.55, 196.26) * mm, "mid": v(484.36, 196.45) * mm, "end": v(484.11, 196.51) * mm});
            skLineSegment(sketch, "E1055", {"start": v(484.11, 196.51) * mm, "end": v(482.54, 196.51) * mm});
            skCircle(sketch, "E1056", {"center": v(483.33, 189.01) * mm, "radius": 1.6 * mm});
            skArc(sketch, "E1057", {"start": v(92.12, 324.19) * mm, "mid": v(91.93, 324.37) * mm, "end": v(91.68, 324.44) * mm});
            skArc(sketch, "E1058", {"start": v(92.12, 324.19) * mm, "mid": v(92.9, 324.08) * mm, "end": v(92.8, 324.87) * mm});
            skArc(sketch, "E1059", {"start": v(92.55, 325.3) * mm, "mid": v(92.62, 325.05) * mm, "end": v(92.8, 324.87) * mm});
            skLineSegment(sketch, "E1060", {"start": v(92.55, 325.3) * mm, "end": v(92.55, 326.94) * mm});
            skArc(sketch, "E1061", {"start": v(93.05, 327.44) * mm, "mid": v(92.7, 327.3) * mm, "end": v(92.55, 326.94) * mm});
            skLineSegment(sketch, "E1062", {"start": v(93.05, 327.44) * mm, "end": v(98.05, 327.44) * mm});
            skArc(sketch, "E1063", {"start": v(98.55, 326.94) * mm, "mid": v(98.4, 327.3) * mm, "end": v(98.05, 327.44) * mm});
            skLineSegment(sketch, "E1064", {"start": v(98.55, 326.94) * mm, "end": v(98.55, 325.3) * mm});
            skArc(sketch, "E1065", {"start": v(98.3, 324.87) * mm, "mid": v(98.48, 325.05) * mm, "end": v(98.55, 325.3) * mm});
            skArc(sketch, "E1066", {"start": v(98.3, 324.87) * mm, "mid": v(98.2, 324.08) * mm, "end": v(98.98, 324.19) * mm});
            skArc(sketch, "E1067", {"start": v(99.42, 324.44) * mm, "mid": v(99.17, 324.37) * mm, "end": v(98.98, 324.19) * mm});
            skLineSegment(sketch, "E1068", {"start": v(99.42, 324.44) * mm, "end": v(104.55, 324.44) * mm});
            skLineSegment(sketch, "E1069", {"start": v(104.55, 324.44) * mm, "end": v(104.55, 321.44) * mm});
            skLineSegment(sketch, "E1070", {"start": v(104.55, 321.44) * mm, "end": v(103.28, 321.44) * mm});
            skLineSegment(sketch, "E1071", {"start": v(103.28, 321.44) * mm, "end": v(103.28, 317.44) * mm});
            skLineSegment(sketch, "E1072", {"start": v(103.28, 317.44) * mm, "end": v(104.55, 317.44) * mm});
            skLineSegment(sketch, "E1073", {"start": v(104.55, 317.44) * mm, "end": v(104.55, 314.44) * mm});
            skLineSegment(sketch, "E1074", {"start": v(104.55, 314.44) * mm, "end": v(107.75, 314.44) * mm});
            skLineSegment(sketch, "E1075", {"start": v(107.75, 314.44) * mm, "end": v(107.75, 317.44) * mm});
            skLineSegment(sketch, "E1076", {"start": v(107.75, 317.44) * mm, "end": v(109.03, 317.44) * mm});
            skLineSegment(sketch, "E1077", {"start": v(109.03, 317.44) * mm, "end": v(109.03, 321.44) * mm});
            skLineSegment(sketch, "E1078", {"start": v(109.03, 321.44) * mm, "end": v(107.75, 321.44) * mm});
            skLineSegment(sketch, "E1079", {"start": v(107.75, 321.44) * mm, "end": v(107.75, 324.44) * mm});
            skLineSegment(sketch, "E1080", {"start": v(107.75, 324.44) * mm, "end": v(112.88, 324.44) * mm});
            skArc(sketch, "E1081", {"start": v(113.32, 324.19) * mm, "mid": v(113.13, 324.37) * mm, "end": v(112.88, 324.44) * mm});
            skArc(sketch, "E1082", {"start": v(113.32, 324.19) * mm, "mid": v(114.1, 324.08) * mm, "end": v(114, 324.87) * mm});
            skArc(sketch, "E1083", {"start": v(113.75, 325.3) * mm, "mid": v(113.82, 325.05) * mm, "end": v(114, 324.87) * mm});
            skLineSegment(sketch, "E1084", {"start": v(113.75, 325.3) * mm, "end": v(113.75, 326.94) * mm});
            skArc(sketch, "E1085", {"start": v(114.25, 327.44) * mm, "mid": v(113.9, 327.3) * mm, "end": v(113.75, 326.94) * mm});
            skLineSegment(sketch, "E1086", {"start": v(114.25, 327.44) * mm, "end": v(119.25, 327.44) * mm});
            skArc(sketch, "E1087", {"start": v(119.75, 326.94) * mm, "mid": v(119.6, 327.3) * mm, "end": v(119.25, 327.44) * mm});
            skLineSegment(sketch, "E1088", {"start": v(119.75, 326.94) * mm, "end": v(119.75, 325.3) * mm});
            skArc(sketch, "E1089", {"start": v(119.5, 324.87) * mm, "mid": v(119.68, 325.05) * mm, "end": v(119.75, 325.3) * mm});
            skArc(sketch, "E1090", {"start": v(119.5, 324.87) * mm, "mid": v(119.4, 324.08) * mm, "end": v(120.18, 324.19) * mm});
            skArc(sketch, "E1091", {"start": v(120.62, 324.44) * mm, "mid": v(120.37, 324.37) * mm, "end": v(120.18, 324.19) * mm});
            skLineSegment(sketch, "E1092", {"start": v(120.62, 324.44) * mm, "end": v(131.15, 324.44) * mm});
            skLineSegment(sketch, "E1093", {"start": v(131.15, 319.44) * mm, "end": v(131.15, 298.44) * mm});
            skLineSegment(sketch, "E1094", {"start": v(131.15, 298.44) * mm, "end": v(129.15, 296.44) * mm});
            skLineSegment(sketch, "E1095", {"start": v(129.15, 296.44) * mm, "end": v(129.15, 194.44) * mm});
            skLineSegment(sketch, "E1096", {"start": v(129.15, 194.44) * mm, "end": v(120.62, 194.44) * mm});
            skArc(sketch, "E1097", {"start": v(120.18, 194.69) * mm, "mid": v(120.37, 194.5) * mm, "end": v(120.62, 194.44) * mm});
            skArc(sketch, "E1098", {"start": v(120.18, 194.69) * mm, "mid": v(119.4, 194.8) * mm, "end": v(119.5, 194) * mm});
            skArc(sketch, "E1099", {"start": v(119.75, 193.57) * mm, "mid": v(119.68, 193.82) * mm, "end": v(119.5, 194) * mm});
            skArc(sketch, "E1100", {"start": v(92.8, 194) * mm, "mid": v(92.62, 193.82) * mm, "end": v(92.55, 193.57) * mm});
            skArc(sketch, "E1101", {"start": v(92.8, 194) * mm, "mid": v(92.9, 194.8) * mm, "end": v(92.12, 194.69) * mm});
            skArc(sketch, "E1102", {"start": v(91.68, 194.44) * mm, "mid": v(91.93, 194.5) * mm, "end": v(92.12, 194.69) * mm});
            skLineSegment(sketch, "E1103", {"start": v(91.68, 194.44) * mm, "end": v(80.62, 194.44) * mm});
            skArc(sketch, "E1104", {"start": v(80.18, 194.69) * mm, "mid": v(80.37, 194.5) * mm, "end": v(80.62, 194.44) * mm});
            skArc(sketch, "E1105", {"start": v(80.18, 194.69) * mm, "mid": v(79.4, 194.8) * mm, "end": v(79.5, 194) * mm});
            skArc(sketch, "E1106", {"start": v(79.75, 193.57) * mm, "mid": v(79.68, 193.82) * mm, "end": v(79.5, 194) * mm});
            skLineSegment(sketch, "E1107", {"start": v(79.75, 193.57) * mm, "end": v(79.75, 191.94) * mm});
            skArc(sketch, "E1108", {"start": v(79.25, 191.44) * mm, "mid": v(79.6, 191.58) * mm, "end": v(79.75, 191.94) * mm});
            skLineSegment(sketch, "E1109", {"start": v(79.25, 191.44) * mm, "end": v(74.25, 191.44) * mm});
            skArc(sketch, "E1110", {"start": v(73.75, 191.94) * mm, "mid": v(73.9, 191.58) * mm, "end": v(74.25, 191.44) * mm});
            skLineSegment(sketch, "E1111", {"start": v(73.75, 191.94) * mm, "end": v(73.75, 193.57) * mm});
            skArc(sketch, "E1112", {"start": v(74, 194) * mm, "mid": v(73.82, 193.82) * mm, "end": v(73.75, 193.57) * mm});
            skArc(sketch, "E1113", {"start": v(74, 194) * mm, "mid": v(74.1, 194.8) * mm, "end": v(73.32, 194.69) * mm});
            skArc(sketch, "E1114", {"start": v(72.88, 194.44) * mm, "mid": v(73.13, 194.5) * mm, "end": v(73.32, 194.69) * mm});
            skLineSegment(sketch, "E1115", {"start": v(72.88, 194.44) * mm, "end": v(67.75, 194.44) * mm});
            skLineSegment(sketch, "E1116", {"start": v(67.75, 194.44) * mm, "end": v(67.75, 197.44) * mm});
            skLineSegment(sketch, "E1117", {"start": v(67.75, 197.44) * mm, "end": v(69.03, 197.44) * mm});
            skLineSegment(sketch, "E1118", {"start": v(69.03, 197.44) * mm, "end": v(69.03, 201.44) * mm});
            skLineSegment(sketch, "E1119", {"start": v(69.03, 201.44) * mm, "end": v(67.75, 201.44) * mm});
            skLineSegment(sketch, "E1120", {"start": v(67.75, 201.44) * mm, "end": v(67.75, 204.44) * mm});
            skLineSegment(sketch, "E1121", {"start": v(67.75, 204.44) * mm, "end": v(64.55, 204.44) * mm});
            skLineSegment(sketch, "E1122", {"start": v(64.55, 204.44) * mm, "end": v(64.55, 201.44) * mm});
            skLineSegment(sketch, "E1123", {"start": v(64.55, 201.44) * mm, "end": v(63.28, 201.44) * mm});
            skLineSegment(sketch, "E1124", {"start": v(63.28, 201.44) * mm, "end": v(63.28, 197.44) * mm});
            skLineSegment(sketch, "E1125", {"start": v(63.28, 197.44) * mm, "end": v(64.55, 197.44) * mm});
            skLineSegment(sketch, "E1126", {"start": v(64.55, 197.44) * mm, "end": v(64.55, 194.44) * mm});
            skLineSegment(sketch, "E1127", {"start": v(64.55, 194.44) * mm, "end": v(59.42, 194.44) * mm});
            skArc(sketch, "E1128", {"start": v(58.98, 194.69) * mm, "mid": v(59.17, 194.5) * mm, "end": v(59.42, 194.44) * mm});
            skArc(sketch, "E1129", {"start": v(58.98, 194.69) * mm, "mid": v(58.2, 194.8) * mm, "end": v(58.3, 194) * mm});
            skArc(sketch, "E1130", {"start": v(58.55, 193.57) * mm, "mid": v(58.48, 193.82) * mm, "end": v(58.3, 194) * mm});
            skLineSegment(sketch, "E1131", {"start": v(58.55, 193.57) * mm, "end": v(58.55, 191.94) * mm});
            skArc(sketch, "E1132", {"start": v(58.05, 191.44) * mm, "mid": v(58.4, 191.58) * mm, "end": v(58.55, 191.94) * mm});
            skLineSegment(sketch, "E1133", {"start": v(58.05, 191.44) * mm, "end": v(53.05, 191.44) * mm});
            skArc(sketch, "E1134", {"start": v(52.55, 191.94) * mm, "mid": v(52.7, 191.58) * mm, "end": v(53.05, 191.44) * mm});
            skLineSegment(sketch, "E1135", {"start": v(52.55, 191.94) * mm, "end": v(52.55, 193.57) * mm});
            skArc(sketch, "E1136", {"start": v(52.8, 194) * mm, "mid": v(52.62, 193.82) * mm, "end": v(52.55, 193.57) * mm});
            skArc(sketch, "E1137", {"start": v(52.8, 194) * mm, "mid": v(52.9, 194.8) * mm, "end": v(52.12, 194.69) * mm});
            skArc(sketch, "E1138", {"start": v(51.68, 194.44) * mm, "mid": v(51.93, 194.5) * mm, "end": v(52.12, 194.69) * mm});
            skLineSegment(sketch, "E1139", {"start": v(51.68, 194.44) * mm, "end": v(-39.38, 194.44) * mm});
            skArc(sketch, "E1140", {"start": v(-39.82, 194.69) * mm, "mid": v(-39.63, 194.5) * mm, "end": v(-39.38, 194.44) * mm});
            skArc(sketch, "E1141", {"start": v(-39.82, 194.69) * mm, "mid": v(-40.6, 194.8) * mm, "end": v(-40.5, 194) * mm});
            skArc(sketch, "E1142", {"start": v(-40.25, 193.57) * mm, "mid": v(-40.32, 193.82) * mm, "end": v(-40.5, 194) * mm});
            skLineSegment(sketch, "E1143", {"start": v(-40.25, 193.57) * mm, "end": v(-40.25, 191.94) * mm});
            skArc(sketch, "E1144", {"start": v(-40.75, 191.44) * mm, "mid": v(-40.4, 191.58) * mm, "end": v(-40.25, 191.94) * mm});
            skLineSegment(sketch, "E1145", {"start": v(-40.75, 191.44) * mm, "end": v(-45.75, 191.44) * mm});
            skArc(sketch, "E1146", {"start": v(-46.25, 191.94) * mm, "mid": v(-46.1, 191.58) * mm, "end": v(-45.75, 191.44) * mm});
            skLineSegment(sketch, "E1147", {"start": v(-46.25, 191.94) * mm, "end": v(-46.25, 193.57) * mm});
            skArc(sketch, "E1148", {"start": v(-46, 194) * mm, "mid": v(-46.18, 193.82) * mm, "end": v(-46.25, 193.57) * mm});
            skArc(sketch, "E1149", {"start": v(-46, 194) * mm, "mid": v(-45.9, 194.8) * mm, "end": v(-46.68, 194.69) * mm});
            skArc(sketch, "E1150", {"start": v(-47.12, 194.44) * mm, "mid": v(-46.87, 194.5) * mm, "end": v(-46.68, 194.69) * mm});
            skLineSegment(sketch, "E1151", {"start": v(-47.12, 194.44) * mm, "end": v(-52.25, 194.44) * mm});
            skLineSegment(sketch, "E1152", {"start": v(-52.25, 194.44) * mm, "end": v(-52.25, 197.44) * mm});
            skLineSegment(sketch, "E1153", {"start": v(-52.25, 197.44) * mm, "end": v(-50.97, 197.44) * mm});
            skLineSegment(sketch, "E1154", {"start": v(-50.97, 197.44) * mm, "end": v(-50.97, 201.44) * mm});
            skLineSegment(sketch, "E1155", {"start": v(-50.97, 201.44) * mm, "end": v(-52.25, 201.44) * mm});
            skLineSegment(sketch, "E1156", {"start": v(-52.25, 201.44) * mm, "end": v(-52.25, 204.44) * mm});
            skLineSegment(sketch, "E1157", {"start": v(-52.25, 204.44) * mm, "end": v(-55.45, 204.44) * mm});
            skLineSegment(sketch, "E1158", {"start": v(-55.45, 204.44) * mm, "end": v(-55.45, 201.44) * mm});
            skLineSegment(sketch, "E1159", {"start": v(-55.45, 201.44) * mm, "end": v(-56.72, 201.44) * mm});
            skLineSegment(sketch, "E1160", {"start": v(-56.72, 201.44) * mm, "end": v(-56.72, 197.44) * mm});
            skLineSegment(sketch, "E1161", {"start": v(-56.72, 197.44) * mm, "end": v(-55.45, 197.44) * mm});
            skLineSegment(sketch, "E1162", {"start": v(-55.45, 197.44) * mm, "end": v(-55.45, 194.44) * mm});
            skLineSegment(sketch, "E1163", {"start": v(-55.45, 194.44) * mm, "end": v(-60.58, 194.44) * mm});
            skArc(sketch, "E1164", {"start": v(-61.02, 194.69) * mm, "mid": v(-60.83, 194.5) * mm, "end": v(-60.58, 194.44) * mm});
            skArc(sketch, "E1165", {"start": v(-61.02, 194.69) * mm, "mid": v(-61.8, 194.8) * mm, "end": v(-61.7, 194) * mm});
            skArc(sketch, "E1166", {"start": v(-61.45, 193.57) * mm, "mid": v(-61.52, 193.82) * mm, "end": v(-61.7, 194) * mm});
            skLineSegment(sketch, "E1167", {"start": v(-61.45, 193.57) * mm, "end": v(-61.45, 191.94) * mm});
            skArc(sketch, "E1168", {"start": v(-61.95, 191.44) * mm, "mid": v(-61.6, 191.58) * mm, "end": v(-61.45, 191.94) * mm});
            skLineSegment(sketch, "E1169", {"start": v(-61.95, 191.44) * mm, "end": v(-66.95, 191.44) * mm});
            skArc(sketch, "E1170", {"start": v(-67.45, 191.94) * mm, "mid": v(-67.3, 191.58) * mm, "end": v(-66.95, 191.44) * mm});
            skLineSegment(sketch, "E1171", {"start": v(-67.45, 191.94) * mm, "end": v(-67.45, 193.57) * mm});
            skArc(sketch, "E1172", {"start": v(-67.2, 194) * mm, "mid": v(-67.38, 193.82) * mm, "end": v(-67.45, 193.57) * mm});
            skArc(sketch, "E1173", {"start": v(-67.2, 194) * mm, "mid": v(-67.1, 194.8) * mm, "end": v(-67.88, 194.69) * mm});
            skArc(sketch, "E1174", {"start": v(-68.32, 194.44) * mm, "mid": v(-68.07, 194.5) * mm, "end": v(-67.88, 194.69) * mm});
            skLineSegment(sketch, "E1175", {"start": v(-68.32, 194.44) * mm, "end": v(-199.38, 194.44) * mm});
            skArc(sketch, "E1176", {"start": v(-199.82, 194.69) * mm, "mid": v(-199.63, 194.5) * mm, "end": v(-199.38, 194.44) * mm});
            skArc(sketch, "E1177", {"start": v(-199.82, 194.69) * mm, "mid": v(-200.6, 194.8) * mm, "end": v(-200.5, 194) * mm});
            skArc(sketch, "E1178", {"start": v(-200.25, 193.57) * mm, "mid": v(-200.32, 193.82) * mm, "end": v(-200.5, 194) * mm});
            skLineSegment(sketch, "E1179", {"start": v(-200.25, 193.57) * mm, "end": v(-200.25, 191.94) * mm});
            skArc(sketch, "E1180", {"start": v(-200.75, 191.44) * mm, "mid": v(-200.4, 191.58) * mm, "end": v(-200.25, 191.94) * mm});
            skLineSegment(sketch, "E1181", {"start": v(-200.75, 191.44) * mm, "end": v(-205.75, 191.44) * mm});
            skArc(sketch, "E1182", {"start": v(-206.25, 191.94) * mm, "mid": v(-206.1, 191.58) * mm, "end": v(-205.75, 191.44) * mm});
            skLineSegment(sketch, "E1183", {"start": v(-206.25, 191.94) * mm, "end": v(-206.25, 193.57) * mm});
            skArc(sketch, "E1184", {"start": v(-206, 194) * mm, "mid": v(-206.18, 193.82) * mm, "end": v(-206.25, 193.57) * mm});
            skArc(sketch, "E1185", {"start": v(-206, 194) * mm, "mid": v(-205.9, 194.8) * mm, "end": v(-206.68, 194.69) * mm});
            skArc(sketch, "E1186", {"start": v(-207.12, 194.44) * mm, "mid": v(-206.87, 194.5) * mm, "end": v(-206.68, 194.69) * mm});
            skLineSegment(sketch, "E1187", {"start": v(-207.12, 194.44) * mm, "end": v(-212.25, 194.44) * mm});
            skLineSegment(sketch, "E1188", {"start": v(-212.25, 194.44) * mm, "end": v(-212.25, 197.44) * mm});
            skLineSegment(sketch, "E1189", {"start": v(-212.25, 197.44) * mm, "end": v(-210.97, 197.44) * mm});
            skLineSegment(sketch, "E1190", {"start": v(-210.97, 197.44) * mm, "end": v(-210.97, 201.44) * mm});
            skLineSegment(sketch, "E1191", {"start": v(-210.97, 201.44) * mm, "end": v(-212.25, 201.44) * mm});
            skLineSegment(sketch, "E1192", {"start": v(-212.25, 201.44) * mm, "end": v(-212.25, 204.44) * mm});
            skLineSegment(sketch, "E1193", {"start": v(-212.25, 204.44) * mm, "end": v(-215.45, 204.44) * mm});
            skLineSegment(sketch, "E1194", {"start": v(-215.45, 204.44) * mm, "end": v(-215.45, 201.44) * mm});
            skLineSegment(sketch, "E1195", {"start": v(-215.45, 201.44) * mm, "end": v(-216.72, 201.44) * mm});
            skLineSegment(sketch, "E1196", {"start": v(-216.72, 201.44) * mm, "end": v(-216.72, 197.44) * mm});
            skLineSegment(sketch, "E1197", {"start": v(-216.72, 197.44) * mm, "end": v(-215.45, 197.44) * mm});
            skLineSegment(sketch, "E1198", {"start": v(-215.45, 197.44) * mm, "end": v(-215.45, 194.44) * mm});
            skLineSegment(sketch, "E1199", {"start": v(-215.45, 194.44) * mm, "end": v(-220.58, 194.44) * mm});
            skArc(sketch, "E1200", {"start": v(-221.02, 194.69) * mm, "mid": v(-220.83, 194.5) * mm, "end": v(-220.58, 194.44) * mm});
            skArc(sketch, "E1201", {"start": v(-221.02, 194.69) * mm, "mid": v(-221.8, 194.8) * mm, "end": v(-221.7, 194) * mm});
            skArc(sketch, "E1202", {"start": v(-221.45, 193.57) * mm, "mid": v(-221.52, 193.82) * mm, "end": v(-221.7, 194) * mm});
            skLineSegment(sketch, "E1203", {"start": v(-221.45, 193.57) * mm, "end": v(-221.45, 191.94) * mm});
            skArc(sketch, "E1204", {"start": v(-221.95, 191.44) * mm, "mid": v(-221.6, 191.58) * mm, "end": v(-221.45, 191.94) * mm});
            skLineSegment(sketch, "E1205", {"start": v(-221.95, 191.44) * mm, "end": v(-226.95, 191.44) * mm});
            skArc(sketch, "E1206", {"start": v(-227.45, 191.94) * mm, "mid": v(-227.3, 191.58) * mm, "end": v(-226.95, 191.44) * mm});
            skLineSegment(sketch, "E1207", {"start": v(-227.45, 191.94) * mm, "end": v(-227.45, 193.57) * mm});
            skArc(sketch, "E1208", {"start": v(-227.2, 194) * mm, "mid": v(-227.38, 193.82) * mm, "end": v(-227.45, 193.57) * mm});
            skArc(sketch, "E1209", {"start": v(-227.2, 194) * mm, "mid": v(-227.1, 194.8) * mm, "end": v(-227.88, 194.69) * mm});
            skArc(sketch, "E1210", {"start": v(-228.32, 194.44) * mm, "mid": v(-228.07, 194.5) * mm, "end": v(-227.88, 194.69) * mm});
            skLineSegment(sketch, "E1211", {"start": v(-228.32, 194.44) * mm, "end": v(-238.85, 194.44) * mm});
            skLineSegment(sketch, "E1212", {"start": v(-238.85, 194.44) * mm, "end": v(-238.85, 205.09) * mm});
            skLineSegment(sketch, "E1213", {"start": v(-238.85, 205.09) * mm, "end": v(-236.62, 205.09) * mm});
            skArc(sketch, "E1214", {"start": v(-236.18, 204.84) * mm, "mid": v(-236.37, 205.02) * mm, "end": v(-236.62, 205.09) * mm});
            skArc(sketch, "E1215", {"start": v(-236.18, 204.84) * mm, "mid": v(-235.4, 204.73) * mm, "end": v(-235.5, 205.52) * mm});
            skArc(sketch, "E1216", {"start": v(-235.75, 205.95) * mm, "mid": v(-235.68, 205.7) * mm, "end": v(-235.5, 205.52) * mm});
            skLineSegment(sketch, "E1217", {"start": v(-235.75, 205.95) * mm, "end": v(-235.75, 213.49) * mm});
            skLineSegment(sketch, "E1218", {"start": v(-235.75, 213.49) * mm, "end": v(-232.75, 213.49) * mm});
            skLineSegment(sketch, "E1219", {"start": v(-232.75, 213.49) * mm, "end": v(-232.75, 212.21) * mm});
            skLineSegment(sketch, "E1220", {"start": v(-232.75, 212.21) * mm, "end": v(-228.75, 212.21) * mm});
            skLineSegment(sketch, "E1221", {"start": v(-228.75, 212.21) * mm, "end": v(-228.75, 213.49) * mm});
            skLineSegment(sketch, "E1222", {"start": v(-228.75, 213.49) * mm, "end": v(-225.75, 213.49) * mm});
            skLineSegment(sketch, "E1223", {"start": v(-225.75, 213.49) * mm, "end": v(-225.75, 216.69) * mm});
            skLineSegment(sketch, "E1224", {"start": v(-225.75, 216.69) * mm, "end": v(-228.75, 216.69) * mm});
            skLineSegment(sketch, "E1225", {"start": v(-228.75, 216.69) * mm, "end": v(-228.75, 217.96) * mm});
            skLineSegment(sketch, "E1226", {"start": v(-228.75, 217.96) * mm, "end": v(-232.75, 217.96) * mm});
            skLineSegment(sketch, "E1227", {"start": v(-232.75, 217.96) * mm, "end": v(-232.75, 216.69) * mm});
            skLineSegment(sketch, "E1228", {"start": v(-232.75, 216.69) * mm, "end": v(-235.75, 216.69) * mm});
            skLineSegment(sketch, "E1229", {"start": v(-235.75, 216.69) * mm, "end": v(-235.75, 225.44) * mm});
            skLineSegment(sketch, "E1230", {"start": v(-235.75, 225.44) * mm, "end": v(86.34, 319.33) * mm});
            skLineSegment(sketch, "E1231", {"start": v(86.7, 324.44) * mm, "end": v(91.68, 324.44) * mm});
            skLineSegment(sketch, "E1232", {"start": v(-201.85, 218.44) * mm, "end": v(-209.85, 218.44) * mm});
            skArc(sketch, "E1233", {"start": v(-209.85, 218.44) * mm, "mid": v(-213.85, 214.44) * mm, "end": v(-209.85, 210.44) * mm});
            skLineSegment(sketch, "E1234", {"start": v(-209.85, 210.44) * mm, "end": v(-201.85, 210.44) * mm});
            skArc(sketch, "E1235", {"start": v(-201.85, 210.44) * mm, "mid": v(-197.85, 214.44) * mm, "end": v(-201.85, 218.44) * mm});
            skLineSegment(sketch, "E1236", {"start": v(-141.85, 218.44) * mm, "end": v(-149.85, 218.44) * mm});
            skArc(sketch, "E1237", {"start": v(-149.85, 218.44) * mm, "mid": v(-153.85, 214.44) * mm, "end": v(-149.85, 210.44) * mm});
            skLineSegment(sketch, "E1238", {"start": v(-149.85, 210.44) * mm, "end": v(-141.85, 210.44) * mm});
            skArc(sketch, "E1239", {"start": v(-141.85, 210.44) * mm, "mid": v(-137.85, 214.44) * mm, "end": v(-141.85, 218.44) * mm});
            skLineSegment(sketch, "E1240", {"start": v(-81.85, 218.44) * mm, "end": v(-89.85, 218.44) * mm});
            skArc(sketch, "E1241", {"start": v(-89.85, 218.44) * mm, "mid": v(-93.85, 214.44) * mm, "end": v(-89.85, 210.44) * mm});
            skLineSegment(sketch, "E1242", {"start": v(-89.85, 210.44) * mm, "end": v(-81.85, 210.44) * mm});
            skArc(sketch, "E1243", {"start": v(-81.85, 210.44) * mm, "mid": v(-77.85, 214.44) * mm, "end": v(-81.85, 218.44) * mm});
            skLineSegment(sketch, "E1244", {"start": v(-21.85, 218.44) * mm, "end": v(-29.85, 218.44) * mm});
            skArc(sketch, "E1245", {"start": v(-29.85, 218.44) * mm, "mid": v(-33.85, 214.44) * mm, "end": v(-29.85, 210.44) * mm});
            skLineSegment(sketch, "E1246", {"start": v(-29.85, 210.44) * mm, "end": v(-21.85, 210.44) * mm});
            skArc(sketch, "E1247", {"start": v(-21.85, 210.44) * mm, "mid": v(-17.85, 214.44) * mm, "end": v(-21.85, 218.44) * mm});
            skLineSegment(sketch, "E1248", {"start": v(38.15, 209.44) * mm, "end": v(38.15, 217.44) * mm});
            skArc(sketch, "E1249", {"start": v(38.15, 217.44) * mm, "mid": v(34.15, 221.44) * mm, "end": v(30.15, 217.44) * mm});
            skLineSegment(sketch, "E1250", {"start": v(30.15, 217.44) * mm, "end": v(30.15, 209.44) * mm});
            skArc(sketch, "E1251", {"start": v(30.15, 209.44) * mm, "mid": v(34.15, 205.44) * mm, "end": v(38.15, 209.44) * mm});
            skLineSegment(sketch, "E1252", {"start": v(38.15, 249.44) * mm, "end": v(38.15, 257.44) * mm});
            skArc(sketch, "E1253", {"start": v(38.15, 257.44) * mm, "mid": v(34.15, 261.44) * mm, "end": v(30.15, 257.44) * mm});
            skLineSegment(sketch, "E1254", {"start": v(30.15, 257.44) * mm, "end": v(30.15, 249.44) * mm});
            skArc(sketch, "E1255", {"start": v(30.15, 249.44) * mm, "mid": v(34.15, 245.44) * mm, "end": v(38.15, 249.44) * mm});
            skLineSegment(sketch, "E1256", {"start": v(123.15, 209.44) * mm, "end": v(123.15, 217.44) * mm});
            skArc(sketch, "E1257", {"start": v(123.15, 217.44) * mm, "mid": v(119.15, 221.44) * mm, "end": v(115.15, 217.44) * mm});
            skLineSegment(sketch, "E1258", {"start": v(115.15, 217.44) * mm, "end": v(115.15, 209.44) * mm});
            skArc(sketch, "E1259", {"start": v(115.15, 209.44) * mm, "mid": v(119.15, 205.44) * mm, "end": v(123.15, 209.44) * mm});
            skLineSegment(sketch, "E1260", {"start": v(123.15, 249.44) * mm, "end": v(123.15, 257.44) * mm});
            skArc(sketch, "E1261", {"start": v(123.15, 257.44) * mm, "mid": v(119.15, 261.44) * mm, "end": v(115.15, 257.44) * mm});
            skLineSegment(sketch, "E1262", {"start": v(115.15, 257.44) * mm, "end": v(115.15, 249.44) * mm});
            skArc(sketch, "E1263", {"start": v(115.15, 249.44) * mm, "mid": v(119.15, 245.44) * mm, "end": v(123.15, 249.44) * mm});
            skLineSegment(sketch, "E1264", {"start": v(123.15, 289.44) * mm, "end": v(123.15, 297.44) * mm});
            skArc(sketch, "E1265", {"start": v(123.15, 297.44) * mm, "mid": v(119.15, 301.44) * mm, "end": v(115.15, 297.44) * mm});
            skLineSegment(sketch, "E1266", {"start": v(115.15, 297.44) * mm, "end": v(115.15, 289.44) * mm});
            skArc(sketch, "E1267", {"start": v(115.15, 289.44) * mm, "mid": v(119.15, 285.44) * mm, "end": v(123.15, 289.44) * mm});
            skCircle(sketch, "E1268", {"center": v(102.31, 207.23) * mm, "radius": 1.3 * mm});
            skCircle(sketch, "E1269", {"center": v(102.33, 290.43) * mm, "radius": 1.3 * mm});
            skCircle(sketch, "E1270", {"center": v(54.12, 213.45) * mm, "radius": 1.3 * mm});
            skCircle(sketch, "E1271", {"center": v(54.13, 287.95) * mm, "radius": 1.3 * mm});
            skLineSegment(sketch, "E1272", {"start": v(119.75, 193.57) * mm, "end": v(119.75, -18.06) * mm});
            skArc(sketch, "E1273", {"start": v(119.25, -22.56) * mm, "mid": v(119.6, -22.42) * mm, "end": v(119.75, -22.06) * mm});
            skLineSegment(sketch, "E1274", {"start": v(119.25, -22.56) * mm, "end": v(114.25, -22.56) * mm});
            skArc(sketch, "E1275", {"start": v(113.75, -22.06) * mm, "mid": v(113.9, -22.42) * mm, "end": v(114.25, -22.56) * mm});
            skLineSegment(sketch, "E1276", {"start": v(113.75, -22.06) * mm, "end": v(113.75, -20.43) * mm});
            skArc(sketch, "E1277", {"start": v(114, -20) * mm, "mid": v(113.82, -20.18) * mm, "end": v(113.75, -20.43) * mm});
            skArc(sketch, "E1278", {"start": v(114, -20) * mm, "mid": v(114.1, -19.2) * mm, "end": v(113.32, -19.31) * mm});
            skArc(sketch, "E1279", {"start": v(112.88, -19.56) * mm, "mid": v(113.13, -19.5) * mm, "end": v(113.32, -19.31) * mm});
            skLineSegment(sketch, "E1280", {"start": v(112.88, -19.56) * mm, "end": v(107.75, -19.56) * mm});
            skLineSegment(sketch, "E1281", {"start": v(107.75, -19.56) * mm, "end": v(107.75, -16.56) * mm});
            skLineSegment(sketch, "E1282", {"start": v(107.75, -16.56) * mm, "end": v(109.03, -16.56) * mm});
            skLineSegment(sketch, "E1283", {"start": v(109.03, -16.56) * mm, "end": v(109.03, -12.56) * mm});
            skLineSegment(sketch, "E1284", {"start": v(109.03, -12.56) * mm, "end": v(107.75, -12.56) * mm});
            skLineSegment(sketch, "E1285", {"start": v(107.75, -12.56) * mm, "end": v(107.75, -9.56) * mm});
            skLineSegment(sketch, "E1286", {"start": v(107.75, -9.56) * mm, "end": v(104.55, -9.56) * mm});
            skLineSegment(sketch, "E1287", {"start": v(104.55, -9.56) * mm, "end": v(104.55, -12.56) * mm});
            skLineSegment(sketch, "E1288", {"start": v(104.55, -12.56) * mm, "end": v(103.28, -12.56) * mm});
            skLineSegment(sketch, "E1289", {"start": v(103.28, -12.56) * mm, "end": v(103.28, -16.56) * mm});
            skLineSegment(sketch, "E1290", {"start": v(103.28, -16.56) * mm, "end": v(104.55, -16.56) * mm});
            skLineSegment(sketch, "E1291", {"start": v(104.55, -16.56) * mm, "end": v(104.55, -19.56) * mm});
            skLineSegment(sketch, "E1292", {"start": v(104.55, -19.56) * mm, "end": v(99.42, -19.56) * mm});
            skArc(sketch, "E1293", {"start": v(98.98, -19.31) * mm, "mid": v(99.17, -19.5) * mm, "end": v(99.42, -19.56) * mm});
            skArc(sketch, "E1294", {"start": v(98.98, -19.31) * mm, "mid": v(98.2, -19.2) * mm, "end": v(98.3, -20) * mm});
            skArc(sketch, "E1295", {"start": v(98.55, -20.43) * mm, "mid": v(98.48, -20.18) * mm, "end": v(98.3, -20) * mm});
            skLineSegment(sketch, "E1296", {"start": v(98.55, -20.43) * mm, "end": v(98.55, -22.06) * mm});
            skArc(sketch, "E1297", {"start": v(98.05, -22.56) * mm, "mid": v(98.4, -22.42) * mm, "end": v(98.55, -22.06) * mm});
            skLineSegment(sketch, "E1298", {"start": v(98.05, -22.56) * mm, "end": v(93.05, -22.56) * mm});
            skArc(sketch, "E1299", {"start": v(92.55, -22.06) * mm, "mid": v(92.7, -22.42) * mm, "end": v(93.05, -22.56) * mm});
            skLineSegment(sketch, "E1300", {"start": v(92.55, -18.06) * mm, "end": v(92.55, 193.57) * mm});
            skArc(sketch, "E1301", {"start": v(106.93, 123.94) * mm, "mid": v(107.18, 124) * mm, "end": v(107.37, 124.19) * mm});
            skArc(sketch, "E1302", {"start": v(108.05, 123.5) * mm, "mid": v(108.15, 124.3) * mm, "end": v(107.37, 124.19) * mm});
            skArc(sketch, "E1303", {"start": v(108.05, 123.5) * mm, "mid": v(107.87, 123.32) * mm, "end": v(107.8, 123.07) * mm});
            skLineSegment(sketch, "E1304", {"start": v(107.8, 123.07) * mm, "end": v(107.8, 118.6) * mm});
            skArc(sketch, "E1305", {"start": v(107.8, 118.6) * mm, "mid": v(107.87, 118.35) * mm, "end": v(108.05, 118.17) * mm});
            skArc(sketch, "E1306", {"start": v(107.37, 117.49) * mm, "mid": v(108.15, 117.38) * mm, "end": v(108.05, 118.17) * mm});
            skArc(sketch, "E1307", {"start": v(107.37, 117.49) * mm, "mid": v(107.18, 117.67) * mm, "end": v(106.93, 117.74) * mm});
            skLineSegment(sketch, "E1308", {"start": v(106.93, 117.74) * mm, "end": v(105.37, 117.74) * mm});
            skArc(sketch, "E1309", {"start": v(105.37, 117.74) * mm, "mid": v(105.12, 117.67) * mm, "end": v(104.93, 117.49) * mm});
            skArc(sketch, "E1310", {"start": v(104.25, 118.17) * mm, "mid": v(104.15, 117.38) * mm, "end": v(104.93, 117.49) * mm});
            skArc(sketch, "E1311", {"start": v(104.25, 118.17) * mm, "mid": v(104.43, 118.35) * mm, "end": v(104.5, 118.6) * mm});
            skLineSegment(sketch, "E1312", {"start": v(104.5, 118.6) * mm, "end": v(104.5, 123.07) * mm});
            skArc(sketch, "E1313", {"start": v(104.5, 123.07) * mm, "mid": v(104.43, 123.32) * mm, "end": v(104.25, 123.5) * mm});
            skArc(sketch, "E1314", {"start": v(104.93, 124.19) * mm, "mid": v(104.15, 124.3) * mm, "end": v(104.25, 123.5) * mm});
            skArc(sketch, "E1315", {"start": v(104.93, 124.19) * mm, "mid": v(105.12, 124) * mm, "end": v(105.37, 123.94) * mm});
            skLineSegment(sketch, "E1316", {"start": v(105.37, 123.94) * mm, "end": v(106.93, 123.94) * mm});
            skArc(sketch, "E1317", {"start": v(106.93, 145.14) * mm, "mid": v(107.18, 145.2) * mm, "end": v(107.37, 145.39) * mm});
            skArc(sketch, "E1318", {"start": v(108.05, 144.7) * mm, "mid": v(108.15, 145.5) * mm, "end": v(107.37, 145.39) * mm});
            skArc(sketch, "E1319", {"start": v(108.05, 144.7) * mm, "mid": v(107.87, 144.52) * mm, "end": v(107.8, 144.27) * mm});
            skLineSegment(sketch, "E1320", {"start": v(107.8, 144.27) * mm, "end": v(107.8, 139.8) * mm});
            skArc(sketch, "E1321", {"start": v(107.8, 139.8) * mm, "mid": v(107.87, 139.55) * mm, "end": v(108.05, 139.37) * mm});
            skArc(sketch, "E1322", {"start": v(107.37, 138.69) * mm, "mid": v(108.15, 138.58) * mm, "end": v(108.05, 139.37) * mm});
            skArc(sketch, "E1323", {"start": v(107.37, 138.69) * mm, "mid": v(107.18, 138.87) * mm, "end": v(106.93, 138.94) * mm});
            skLineSegment(sketch, "E1324", {"start": v(106.93, 138.94) * mm, "end": v(105.37, 138.94) * mm});
            skArc(sketch, "E1325", {"start": v(105.37, 138.94) * mm, "mid": v(105.12, 138.87) * mm, "end": v(104.93, 138.69) * mm});
            skArc(sketch, "E1326", {"start": v(104.25, 139.37) * mm, "mid": v(104.15, 138.58) * mm, "end": v(104.93, 138.69) * mm});
            skArc(sketch, "E1327", {"start": v(104.25, 139.37) * mm, "mid": v(104.43, 139.55) * mm, "end": v(104.5, 139.8) * mm});
            skLineSegment(sketch, "E1328", {"start": v(104.5, 139.8) * mm, "end": v(104.5, 144.27) * mm});
            skArc(sketch, "E1329", {"start": v(104.5, 144.27) * mm, "mid": v(104.43, 144.52) * mm, "end": v(104.25, 144.7) * mm});
            skArc(sketch, "E1330", {"start": v(104.93, 145.39) * mm, "mid": v(104.15, 145.5) * mm, "end": v(104.25, 144.7) * mm});
            skArc(sketch, "E1331", {"start": v(104.93, 145.39) * mm, "mid": v(105.12, 145.2) * mm, "end": v(105.37, 145.14) * mm});
            skLineSegment(sketch, "E1332", {"start": v(105.37, 145.14) * mm, "end": v(106.93, 145.14) * mm});
            skCircle(sketch, "E1333", {"center": v(106.15, 131.44) * mm, "radius": 1.6 * mm});
            skLineSegment(sketch, "E1334", {"start": v(-97.27, 295.88) * mm, "end": v(-97.27, 299.08) * mm});
            skLineSegment(sketch, "E1335", {"start": v(-97.27, 299.08) * mm, "end": v(-94.27, 299.08) * mm});
            skLineSegment(sketch, "E1336", {"start": v(-94.27, 299.08) * mm, "end": v(-94.27, 300.36) * mm});
            skLineSegment(sketch, "E1337", {"start": v(-94.27, 300.36) * mm, "end": v(-90.27, 300.36) * mm});
            skLineSegment(sketch, "E1338", {"start": v(-90.27, 300.36) * mm, "end": v(-90.27, 299.08) * mm});
            skLineSegment(sketch, "E1339", {"start": v(-90.27, 299.08) * mm, "end": v(-87.27, 299.08) * mm});
            skLineSegment(sketch, "E1340", {"start": v(-87.27, 299.08) * mm, "end": v(-87.27, 304.22) * mm});
            skArc(sketch, "E1341", {"start": v(-87.27, 304.22) * mm, "mid": v(-87.34, 304.47) * mm, "end": v(-87.52, 304.65) * mm});
            skArc(sketch, "E1342", {"start": v(-86.84, 305.33) * mm, "mid": v(-87.63, 305.44) * mm, "end": v(-87.52, 304.65) * mm});
            skArc(sketch, "E1343", {"start": v(-86.84, 305.33) * mm, "mid": v(-86.66, 305.15) * mm, "end": v(-86.4, 305.08) * mm});
            skLineSegment(sketch, "E1344", {"start": v(-86.4, 305.08) * mm, "end": v(-84.77, 305.08) * mm});
            skArc(sketch, "E1345", {"start": v(-84.77, 305.08) * mm, "mid": v(-84.42, 305.23) * mm, "end": v(-84.27, 305.58) * mm});
            skLineSegment(sketch, "E1346", {"start": v(-84.27, 305.58) * mm, "end": v(-84.27, 310.58) * mm});
            skArc(sketch, "E1347", {"start": v(-84.27, 310.58) * mm, "mid": v(-84.42, 310.94) * mm, "end": v(-84.77, 311.08) * mm});
            skLineSegment(sketch, "E1348", {"start": v(-84.77, 311.08) * mm, "end": v(-86.4, 311.08) * mm});
            skArc(sketch, "E1349", {"start": v(-86.4, 311.08) * mm, "mid": v(-86.66, 311.02) * mm, "end": v(-86.84, 310.83) * mm});
            skArc(sketch, "E1350", {"start": v(-87.52, 311.52) * mm, "mid": v(-87.63, 310.73) * mm, "end": v(-86.84, 310.83) * mm});
            skArc(sketch, "E1351", {"start": v(-87.52, 311.52) * mm, "mid": v(-87.34, 311.7) * mm, "end": v(-87.27, 311.95) * mm});
            skLineSegment(sketch, "E1352", {"start": v(-87.27, 311.95) * mm, "end": v(-87.27, 316.48) * mm});
            skLineSegment(sketch, "E1353", {"start": v(-87.27, 316.48) * mm, "end": v(-92.48, 316.48) * mm});
            skLineSegment(sketch, "E1354", {"start": v(-101.79, 311.48) * mm, "end": v(-133.27, 311.48) * mm});
            skArc(sketch, "E1355", {"start": v(-133.27, 311.48) * mm, "mid": v(-134.69, 310.9) * mm, "end": v(-135.27, 309.48) * mm});
            skLineSegment(sketch, "E1356", {"start": v(-135.27, 309.48) * mm, "end": v(-135.27, 275.48) * mm});
            skArc(sketch, "E1357", {"start": v(-135.27, 275.48) * mm, "mid": v(-134.69, 274.07) * mm, "end": v(-133.27, 273.48) * mm});
            skLineSegment(sketch, "E1358", {"start": v(-133.27, 273.48) * mm, "end": v(-96.25, 273.48) * mm});
            skArc(sketch, "E1359", {"start": v(-87.27, 283.02) * mm, "mid": v(-87.34, 283.27) * mm, "end": v(-87.52, 283.45) * mm});
            skArc(sketch, "E1360", {"start": v(-86.84, 284.13) * mm, "mid": v(-87.63, 284.24) * mm, "end": v(-87.52, 283.45) * mm});
            skArc(sketch, "E1361", {"start": v(-86.84, 284.13) * mm, "mid": v(-86.66, 283.95) * mm, "end": v(-86.4, 283.88) * mm});
            skLineSegment(sketch, "E1362", {"start": v(-86.4, 283.88) * mm, "end": v(-84.77, 283.88) * mm});
            skArc(sketch, "E1363", {"start": v(-84.77, 283.88) * mm, "mid": v(-84.42, 284.03) * mm, "end": v(-84.27, 284.38) * mm});
            skLineSegment(sketch, "E1364", {"start": v(-84.27, 284.38) * mm, "end": v(-84.27, 289.38) * mm});
            skArc(sketch, "E1365", {"start": v(-84.27, 289.38) * mm, "mid": v(-84.42, 289.74) * mm, "end": v(-84.77, 289.88) * mm});
            skLineSegment(sketch, "E1366", {"start": v(-84.77, 289.88) * mm, "end": v(-86.4, 289.88) * mm});
            skArc(sketch, "E1367", {"start": v(-86.4, 289.88) * mm, "mid": v(-86.66, 289.82) * mm, "end": v(-86.84, 289.63) * mm});
            skArc(sketch, "E1368", {"start": v(-87.52, 290.32) * mm, "mid": v(-87.63, 289.53) * mm, "end": v(-86.84, 289.63) * mm});
            skArc(sketch, "E1369", {"start": v(-87.52, 290.32) * mm, "mid": v(-87.34, 290.5) * mm, "end": v(-87.27, 290.75) * mm});
            skLineSegment(sketch, "E1370", {"start": v(-87.27, 290.75) * mm, "end": v(-87.27, 295.88) * mm});
            skLineSegment(sketch, "E1371", {"start": v(-87.27, 295.88) * mm, "end": v(-90.27, 295.88) * mm});
            skLineSegment(sketch, "E1372", {"start": v(-90.27, 295.88) * mm, "end": v(-90.27, 294.6) * mm});
            skLineSegment(sketch, "E1373", {"start": v(-90.27, 294.6) * mm, "end": v(-94.27, 294.6) * mm});
            skLineSegment(sketch, "E1374", {"start": v(-94.27, 294.6) * mm, "end": v(-94.27, 295.88) * mm});
            skLineSegment(sketch, "E1375", {"start": v(-94.27, 295.88) * mm, "end": v(-97.27, 295.88) * mm});
            skCircle(sketch, "E1376", {"center": v(-115.06, 292.48) * mm, "radius": 11.1 * mm});
            skCircle(sketch, "E1377", {"center": v(-99.56, 276.98) * mm, "radius": 1.6 * mm});
            skCircle(sketch, "E1378", {"center": v(-130.56, 276.98) * mm, "radius": 1.6 * mm});
            skCircle(sketch, "E1379", {"center": v(-99.56, 307.98) * mm, "radius": 1.6 * mm});
            skCircle(sketch, "E1380", {"center": v(-130.56, 307.98) * mm, "radius": 1.6 * mm});
            skLineSegment(sketch, "E1381", {"start": v(-93.65, 273.68) * mm, "end": v(-87.27, 278.48) * mm});
            skLineSegment(sketch, "E1382", {"start": v(-99.18, 311.68) * mm, "end": v(-93.08, 316.28) * mm});
            skArc(sketch, "E1383", {"start": v(-94.25, 273.48) * mm, "mid": v(-93.93, 273.54) * mm, "end": v(-93.65, 273.68) * mm});
            skArc(sketch, "E1384", {"start": v(-99.79, 311.48) * mm, "mid": v(-99.47, 311.54) * mm, "end": v(-99.18, 311.68) * mm});
            skArc(sketch, "E1385", {"start": v(-92.48, 316.48) * mm, "mid": v(-92.8, 316.43) * mm, "end": v(-93.08, 316.28) * mm});
            skLineSegment(sketch, "E1386", {"start": v(-87.27, 278.48) * mm, "end": v(-87.27, 283.02) * mm});
            skLineSegment(sketch, "E1387", {"start": v(-7.76, 120.34) * mm, "end": v(-212.64, 120.34) * mm});
            skLineSegment(sketch, "E1388", {"start": v(-213.6, 121.04) * mm, "end": v(-215.16, 126.02) * mm});
            skLineSegment(sketch, "E1389", {"start": v(-216.11, 126.73) * mm, "end": v(-235.38, 126.73) * mm});
            skArc(sketch, "E1390", {"start": v(-235.38, 126.73) * mm, "mid": v(-238.91, 125.26) * mm, "end": v(-240.38, 121.73) * mm});
            skLineSegment(sketch, "E1391", {"start": v(-240.38, 121.73) * mm, "end": v(-240.38, 87.34) * mm});
            skArc(sketch, "E1392", {"start": v(-240.38, 87.34) * mm, "mid": v(-238.91, 83.8) * mm, "end": v(-235.38, 82.34) * mm});
            skLineSegment(sketch, "E1393", {"start": v(-235.38, 82.34) * mm, "end": v(-205.7, 82.34) * mm});
            skArc(sketch, "E1394", {"start": v(-205.2, 81.84) * mm, "mid": v(-205.35, 82.2) * mm, "end": v(-205.7, 82.34) * mm});
            skArc(sketch, "E1395", {"start": v(-184.7, 82.34) * mm, "mid": v(-185.06, 82.2) * mm, "end": v(-185.2, 81.84) * mm});
            skLineSegment(sketch, "E1396", {"start": v(-184.7, 82.34) * mm, "end": v(-35.7, 82.34) * mm});
            skArc(sketch, "E1397", {"start": v(-35.2, 81.84) * mm, "mid": v(-35.34, 82.2) * mm, "end": v(-35.7, 82.34) * mm});
            skLineSegment(sketch, "E1398", {"start": v(-35.2, 81.84) * mm, "end": v(-35.2, 76.34) * mm});
            skArc(sketch, "E1399", {"start": v(-35.2, 76.34) * mm, "mid": v(-34.61, 74.93) * mm, "end": v(-33.2, 74.34) * mm});
            skLineSegment(sketch, "E1400", {"start": v(-33.2, 74.34) * mm, "end": v(-28.88, 74.34) * mm});
            skArc(sketch, "E1401", {"start": v(-21.93, 75.12) * mm, "mid": v(-25.2, 81.29) * mm, "end": v(-28.47, 75.12) * mm});
            skLineSegment(sketch, "E1402", {"start": v(-21.51, 74.34) * mm, "end": v(-17.2, 74.34) * mm});
            skArc(sketch, "E1403", {"start": v(-17.2, 74.34) * mm, "mid": v(-15.78, 74.93) * mm, "end": v(-15.2, 76.34) * mm});
            skLineSegment(sketch, "E1404", {"start": v(-15.2, 76.34) * mm, "end": v(-15.2, 81.84) * mm});
            skArc(sketch, "E1405", {"start": v(-14.7, 82.34) * mm, "mid": v(-15.05, 82.2) * mm, "end": v(-15.2, 81.84) * mm});
            skLineSegment(sketch, "E1406", {"start": v(-14.7, 82.34) * mm, "end": v(14.97, 82.34) * mm});
            skArc(sketch, "E1407", {"start": v(14.97, 82.34) * mm, "mid": v(18.5, 83.8) * mm, "end": v(19.97, 87.34) * mm});
            skLineSegment(sketch, "E1408", {"start": v(19.97, 87.34) * mm, "end": v(19.97, 121.73) * mm});
            skArc(sketch, "E1409", {"start": v(19.97, 121.73) * mm, "mid": v(18.5, 125.26) * mm, "end": v(14.97, 126.73) * mm});
            skLineSegment(sketch, "E1410", {"start": v(14.97, 126.73) * mm, "end": v(-4.3, 126.73) * mm});
            skLineSegment(sketch, "E1411", {"start": v(-5.25, 126.02) * mm, "end": v(-6.8, 121.04) * mm});
            skArc(sketch, "E1412", {"start": v(9.2, 109.23) * mm, "mid": v(8.94, 109.16) * mm, "end": v(8.76, 108.98) * mm});
            skArc(sketch, "E1413", {"start": v(8.07, 109.66) * mm, "mid": v(7.97, 108.87) * mm, "end": v(8.76, 108.98) * mm});
            skArc(sketch, "E1414", {"start": v(8.07, 109.66) * mm, "mid": v(8.26, 109.84) * mm, "end": v(8.32, 110.1) * mm});
            skLineSegment(sketch, "E1415", {"start": v(8.32, 110.1) * mm, "end": v(8.32, 114.56) * mm});
            skArc(sketch, "E1416", {"start": v(8.32, 114.56) * mm, "mid": v(8.26, 114.8) * mm, "end": v(8.07, 115) * mm});
            skArc(sketch, "E1417", {"start": v(8.76, 115.68) * mm, "mid": v(7.97, 115.78) * mm, "end": v(8.07, 115) * mm});
            skArc(sketch, "E1418", {"start": v(8.76, 115.68) * mm, "mid": v(8.94, 115.5) * mm, "end": v(9.2, 115.43) * mm});
            skLineSegment(sketch, "E1419", {"start": v(9.2, 115.43) * mm, "end": v(10.76, 115.43) * mm});
            skArc(sketch, "E1420", {"start": v(10.76, 115.43) * mm, "mid": v(11, 115.5) * mm, "end": v(11.2, 115.68) * mm});
            skArc(sketch, "E1421", {"start": v(11.87, 115) * mm, "mid": v(11.98, 115.78) * mm, "end": v(11.2, 115.68) * mm});
            skArc(sketch, "E1422", {"start": v(11.87, 115) * mm, "mid": v(11.7, 114.8) * mm, "end": v(11.62, 114.56) * mm});
            skLineSegment(sketch, "E1423", {"start": v(11.62, 114.56) * mm, "end": v(11.62, 110.1) * mm});
            skArc(sketch, "E1424", {"start": v(11.62, 110.1) * mm, "mid": v(11.7, 109.84) * mm, "end": v(11.87, 109.66) * mm});
            skArc(sketch, "E1425", {"start": v(11.2, 108.98) * mm, "mid": v(11.98, 108.87) * mm, "end": v(11.87, 109.66) * mm});
            skArc(sketch, "E1426", {"start": v(11.2, 108.98) * mm, "mid": v(11, 109.16) * mm, "end": v(10.76, 109.23) * mm});
            skLineSegment(sketch, "E1427", {"start": v(10.76, 109.23) * mm, "end": v(9.2, 109.23) * mm});
            skArc(sketch, "E1428", {"start": v(9.2, 88.03) * mm, "mid": v(8.94, 87.96) * mm, "end": v(8.76, 87.78) * mm});
            skArc(sketch, "E1429", {"start": v(8.07, 88.46) * mm, "mid": v(7.97, 87.67) * mm, "end": v(8.76, 87.78) * mm});
            skArc(sketch, "E1430", {"start": v(8.07, 88.46) * mm, "mid": v(8.26, 88.64) * mm, "end": v(8.32, 88.9) * mm});
            skLineSegment(sketch, "E1431", {"start": v(8.32, 88.9) * mm, "end": v(8.32, 93.36) * mm});
            skArc(sketch, "E1432", {"start": v(8.32, 93.36) * mm, "mid": v(8.26, 93.6) * mm, "end": v(8.07, 93.8) * mm});
            skArc(sketch, "E1433", {"start": v(8.76, 94.48) * mm, "mid": v(7.97, 94.58) * mm, "end": v(8.07, 93.8) * mm});
            skArc(sketch, "E1434", {"start": v(8.76, 94.48) * mm, "mid": v(8.94, 94.3) * mm, "end": v(9.2, 94.23) * mm});
            skLineSegment(sketch, "E1435", {"start": v(9.2, 94.23) * mm, "end": v(10.76, 94.23) * mm});
            skArc(sketch, "E1436", {"start": v(10.76, 94.23) * mm, "mid": v(11, 94.3) * mm, "end": v(11.2, 94.48) * mm});
            skArc(sketch, "E1437", {"start": v(11.87, 93.8) * mm, "mid": v(11.98, 94.58) * mm, "end": v(11.2, 94.48) * mm});
            skArc(sketch, "E1438", {"start": v(11.87, 93.8) * mm, "mid": v(11.7, 93.6) * mm, "end": v(11.62, 93.36) * mm});
            skLineSegment(sketch, "E1439", {"start": v(11.62, 93.36) * mm, "end": v(11.62, 88.9) * mm});
            skArc(sketch, "E1440", {"start": v(11.62, 88.9) * mm, "mid": v(11.7, 88.64) * mm, "end": v(11.87, 88.46) * mm});
            skArc(sketch, "E1441", {"start": v(11.2, 87.78) * mm, "mid": v(11.98, 87.67) * mm, "end": v(11.87, 88.46) * mm});
            skArc(sketch, "E1442", {"start": v(11.2, 87.78) * mm, "mid": v(11, 87.96) * mm, "end": v(10.76, 88.03) * mm});
            skLineSegment(sketch, "E1443", {"start": v(10.76, 88.03) * mm, "end": v(9.2, 88.03) * mm});
            skArc(sketch, "E1444", {"start": v(-104.68, 108.84) * mm, "mid": v(-104.93, 108.77) * mm, "end": v(-105.12, 108.59) * mm});
            skArc(sketch, "E1445", {"start": v(-105.8, 109.27) * mm, "mid": v(-105.9, 108.48) * mm, "end": v(-105.12, 108.59) * mm});
            skArc(sketch, "E1446", {"start": v(-105.8, 109.27) * mm, "mid": v(-105.62, 109.45) * mm, "end": v(-105.55, 109.7) * mm});
            skLineSegment(sketch, "E1447", {"start": v(-105.55, 109.7) * mm, "end": v(-105.55, 114.17) * mm});
            skArc(sketch, "E1448", {"start": v(-105.55, 114.17) * mm, "mid": v(-105.62, 114.42) * mm, "end": v(-105.8, 114.6) * mm});
            skArc(sketch, "E1449", {"start": v(-105.12, 115.29) * mm, "mid": v(-105.9, 115.4) * mm, "end": v(-105.8, 114.6) * mm});
            skArc(sketch, "E1450", {"start": v(-105.12, 115.29) * mm, "mid": v(-104.93, 115.1) * mm, "end": v(-104.68, 115.04) * mm});
            skLineSegment(sketch, "E1451", {"start": v(-104.68, 115.04) * mm, "end": v(-103.12, 115.04) * mm});
            skArc(sketch, "E1452", {"start": v(-103.12, 115.04) * mm, "mid": v(-102.87, 115.1) * mm, "end": v(-102.68, 115.29) * mm});
            skArc(sketch, "E1453", {"start": v(-102, 114.6) * mm, "mid": v(-101.9, 115.4) * mm, "end": v(-102.68, 115.29) * mm});
            skArc(sketch, "E1454", {"start": v(-102, 114.6) * mm, "mid": v(-102.18, 114.42) * mm, "end": v(-102.25, 114.17) * mm});
            skLineSegment(sketch, "E1455", {"start": v(-102.25, 114.17) * mm, "end": v(-102.25, 109.7) * mm});
            skArc(sketch, "E1456", {"start": v(-102.25, 109.7) * mm, "mid": v(-102.18, 109.45) * mm, "end": v(-102, 109.27) * mm});
            skArc(sketch, "E1457", {"start": v(-102.68, 108.59) * mm, "mid": v(-101.9, 108.48) * mm, "end": v(-102, 109.27) * mm});
            skArc(sketch, "E1458", {"start": v(-102.68, 108.59) * mm, "mid": v(-102.87, 108.77) * mm, "end": v(-103.12, 108.84) * mm});
            skLineSegment(sketch, "E1459", {"start": v(-103.12, 108.84) * mm, "end": v(-104.68, 108.84) * mm});
            skArc(sketch, "E1460", {"start": v(-104.68, 87.64) * mm, "mid": v(-104.93, 87.57) * mm, "end": v(-105.12, 87.39) * mm});
            skArc(sketch, "E1461", {"start": v(-105.8, 88.07) * mm, "mid": v(-105.9, 87.28) * mm, "end": v(-105.12, 87.39) * mm});
            skArc(sketch, "E1462", {"start": v(-105.8, 88.07) * mm, "mid": v(-105.62, 88.25) * mm, "end": v(-105.55, 88.5) * mm});
            skLineSegment(sketch, "E1463", {"start": v(-105.55, 88.5) * mm, "end": v(-105.55, 92.97) * mm});
            skArc(sketch, "E1464", {"start": v(-105.55, 92.97) * mm, "mid": v(-105.62, 93.22) * mm, "end": v(-105.8, 93.4) * mm});
            skArc(sketch, "E1465", {"start": v(-105.12, 94.09) * mm, "mid": v(-105.9, 94.2) * mm, "end": v(-105.8, 93.4) * mm});
            skArc(sketch, "E1466", {"start": v(-105.12, 94.09) * mm, "mid": v(-104.93, 93.9) * mm, "end": v(-104.68, 93.84) * mm});
            skLineSegment(sketch, "E1467", {"start": v(-104.68, 93.84) * mm, "end": v(-103.12, 93.84) * mm});
            skArc(sketch, "E1468", {"start": v(-103.12, 93.84) * mm, "mid": v(-102.87, 93.9) * mm, "end": v(-102.68, 94.09) * mm});
            skArc(sketch, "E1469", {"start": v(-102, 93.4) * mm, "mid": v(-101.9, 94.2) * mm, "end": v(-102.68, 94.09) * mm});
            skArc(sketch, "E1470", {"start": v(-102, 93.4) * mm, "mid": v(-102.18, 93.22) * mm, "end": v(-102.25, 92.97) * mm});
            skLineSegment(sketch, "E1471", {"start": v(-102.25, 92.97) * mm, "end": v(-102.25, 88.5) * mm});
            skArc(sketch, "E1472", {"start": v(-102.25, 88.5) * mm, "mid": v(-102.18, 88.25) * mm, "end": v(-102, 88.07) * mm});
            skArc(sketch, "E1473", {"start": v(-102.68, 87.39) * mm, "mid": v(-101.9, 87.28) * mm, "end": v(-102, 88.07) * mm});
            skArc(sketch, "E1474", {"start": v(-102.68, 87.39) * mm, "mid": v(-102.87, 87.57) * mm, "end": v(-103.12, 87.64) * mm});
            skLineSegment(sketch, "E1475", {"start": v(-103.12, 87.64) * mm, "end": v(-104.68, 87.64) * mm});
            skArc(sketch, "E1476", {"start": v(-117.28, 108.84) * mm, "mid": v(-117.53, 108.77) * mm, "end": v(-117.72, 108.59) * mm});
            skArc(sketch, "E1477", {"start": v(-118.4, 109.27) * mm, "mid": v(-118.5, 108.48) * mm, "end": v(-117.72, 108.59) * mm});
            skArc(sketch, "E1478", {"start": v(-118.4, 109.27) * mm, "mid": v(-118.22, 109.45) * mm, "end": v(-118.15, 109.7) * mm});
            skLineSegment(sketch, "E1479", {"start": v(-118.15, 109.7) * mm, "end": v(-118.15, 114.17) * mm});
            skArc(sketch, "E1480", {"start": v(-118.15, 114.17) * mm, "mid": v(-118.22, 114.42) * mm, "end": v(-118.4, 114.6) * mm});
            skArc(sketch, "E1481", {"start": v(-117.72, 115.29) * mm, "mid": v(-118.5, 115.4) * mm, "end": v(-118.4, 114.6) * mm});
            skArc(sketch, "E1482", {"start": v(-117.72, 115.29) * mm, "mid": v(-117.53, 115.1) * mm, "end": v(-117.28, 115.04) * mm});
            skLineSegment(sketch, "E1483", {"start": v(-117.28, 115.04) * mm, "end": v(-115.72, 115.04) * mm});
            skArc(sketch, "E1484", {"start": v(-115.72, 115.04) * mm, "mid": v(-115.47, 115.1) * mm, "end": v(-115.28, 115.29) * mm});
            skArc(sketch, "E1485", {"start": v(-114.6, 114.6) * mm, "mid": v(-114.5, 115.4) * mm, "end": v(-115.28, 115.29) * mm});
            skArc(sketch, "E1486", {"start": v(-114.6, 114.6) * mm, "mid": v(-114.78, 114.42) * mm, "end": v(-114.85, 114.17) * mm});
            skLineSegment(sketch, "E1487", {"start": v(-114.85, 114.17) * mm, "end": v(-114.85, 109.7) * mm});
            skArc(sketch, "E1488", {"start": v(-114.85, 109.7) * mm, "mid": v(-114.78, 109.45) * mm, "end": v(-114.6, 109.27) * mm});
            skArc(sketch, "E1489", {"start": v(-115.28, 108.59) * mm, "mid": v(-114.5, 108.48) * mm, "end": v(-114.6, 109.27) * mm});
            skArc(sketch, "E1490", {"start": v(-115.28, 108.59) * mm, "mid": v(-115.47, 108.77) * mm, "end": v(-115.72, 108.84) * mm});
            skLineSegment(sketch, "E1491", {"start": v(-115.72, 108.84) * mm, "end": v(-117.28, 108.84) * mm});
            skArc(sketch, "E1492", {"start": v(-117.28, 87.64) * mm, "mid": v(-117.53, 87.57) * mm, "end": v(-117.72, 87.39) * mm});
            skArc(sketch, "E1493", {"start": v(-118.4, 88.07) * mm, "mid": v(-118.5, 87.28) * mm, "end": v(-117.72, 87.39) * mm});
            skArc(sketch, "E1494", {"start": v(-118.4, 88.07) * mm, "mid": v(-118.22, 88.25) * mm, "end": v(-118.15, 88.5) * mm});
            skLineSegment(sketch, "E1495", {"start": v(-118.15, 88.5) * mm, "end": v(-118.15, 92.97) * mm});
            skArc(sketch, "E1496", {"start": v(-118.15, 92.97) * mm, "mid": v(-118.22, 93.22) * mm, "end": v(-118.4, 93.4) * mm});
            skArc(sketch, "E1497", {"start": v(-117.72, 94.09) * mm, "mid": v(-118.5, 94.2) * mm, "end": v(-118.4, 93.4) * mm});
            skArc(sketch, "E1498", {"start": v(-117.72, 94.09) * mm, "mid": v(-117.53, 93.9) * mm, "end": v(-117.28, 93.84) * mm});
            skLineSegment(sketch, "E1499", {"start": v(-117.28, 93.84) * mm, "end": v(-115.72, 93.84) * mm});
            skArc(sketch, "E1500", {"start": v(-115.72, 93.84) * mm, "mid": v(-115.47, 93.9) * mm, "end": v(-115.28, 94.09) * mm});
            skArc(sketch, "E1501", {"start": v(-114.6, 93.4) * mm, "mid": v(-114.5, 94.2) * mm, "end": v(-115.28, 94.09) * mm});
            skArc(sketch, "E1502", {"start": v(-114.6, 93.4) * mm, "mid": v(-114.78, 93.22) * mm, "end": v(-114.85, 92.97) * mm});
            skLineSegment(sketch, "E1503", {"start": v(-114.85, 92.97) * mm, "end": v(-114.85, 88.5) * mm});
            skArc(sketch, "E1504", {"start": v(-114.85, 88.5) * mm, "mid": v(-114.78, 88.25) * mm, "end": v(-114.6, 88.07) * mm});
            skArc(sketch, "E1505", {"start": v(-115.28, 87.39) * mm, "mid": v(-114.5, 87.28) * mm, "end": v(-114.6, 88.07) * mm});
            skArc(sketch, "E1506", {"start": v(-115.28, 87.39) * mm, "mid": v(-115.47, 87.57) * mm, "end": v(-115.72, 87.64) * mm});
            skLineSegment(sketch, "E1507", {"start": v(-115.72, 87.64) * mm, "end": v(-117.28, 87.64) * mm});
            skArc(sketch, "E1508", {"start": v(-229.16, 108.98) * mm, "mid": v(-229.34, 109.16) * mm, "end": v(-229.6, 109.23) * mm});
            skArc(sketch, "E1509", {"start": v(-229.16, 108.98) * mm, "mid": v(-228.37, 108.87) * mm, "end": v(-228.48, 109.66) * mm});
            skArc(sketch, "E1510", {"start": v(-228.73, 110.1) * mm, "mid": v(-228.66, 109.84) * mm, "end": v(-228.48, 109.66) * mm});
            skLineSegment(sketch, "E1511", {"start": v(-228.73, 110.1) * mm, "end": v(-228.73, 114.56) * mm});
            skArc(sketch, "E1512", {"start": v(-228.48, 115) * mm, "mid": v(-228.66, 114.8) * mm, "end": v(-228.73, 114.56) * mm});
            skArc(sketch, "E1513", {"start": v(-228.48, 115) * mm, "mid": v(-228.37, 115.78) * mm, "end": v(-229.16, 115.68) * mm});
            skArc(sketch, "E1514", {"start": v(-229.6, 115.43) * mm, "mid": v(-229.34, 115.5) * mm, "end": v(-229.16, 115.68) * mm});
            skLineSegment(sketch, "E1515", {"start": v(-229.6, 115.43) * mm, "end": v(-231.16, 115.43) * mm});
            skArc(sketch, "E1516", {"start": v(-231.6, 115.68) * mm, "mid": v(-231.4, 115.5) * mm, "end": v(-231.16, 115.43) * mm});
            skArc(sketch, "E1517", {"start": v(-231.6, 115.68) * mm, "mid": v(-232.38, 115.78) * mm, "end": v(-232.28, 115) * mm});
            skArc(sketch, "E1518", {"start": v(-232.03, 114.56) * mm, "mid": v(-232.1, 114.8) * mm, "end": v(-232.28, 115) * mm});
            skLineSegment(sketch, "E1519", {"start": v(-232.03, 114.56) * mm, "end": v(-232.03, 110.1) * mm});
            skArc(sketch, "E1520", {"start": v(-232.28, 109.66) * mm, "mid": v(-232.1, 109.84) * mm, "end": v(-232.03, 110.1) * mm});
            skArc(sketch, "E1521", {"start": v(-232.28, 109.66) * mm, "mid": v(-232.38, 108.87) * mm, "end": v(-231.6, 108.98) * mm});
            skArc(sketch, "E1522", {"start": v(-231.16, 109.23) * mm, "mid": v(-231.4, 109.16) * mm, "end": v(-231.6, 108.98) * mm});
            skLineSegment(sketch, "E1523", {"start": v(-231.16, 109.23) * mm, "end": v(-229.6, 109.23) * mm});
            skArc(sketch, "E1524", {"start": v(-229.16, 87.78) * mm, "mid": v(-229.34, 87.96) * mm, "end": v(-229.6, 88.03) * mm});
            skArc(sketch, "E1525", {"start": v(-229.16, 87.78) * mm, "mid": v(-228.37, 87.67) * mm, "end": v(-228.48, 88.46) * mm});
            skArc(sketch, "E1526", {"start": v(-228.73, 88.9) * mm, "mid": v(-228.66, 88.64) * mm, "end": v(-228.48, 88.46) * mm});
            skLineSegment(sketch, "E1527", {"start": v(-228.73, 88.9) * mm, "end": v(-228.73, 93.36) * mm});
            skArc(sketch, "E1528", {"start": v(-228.48, 93.8) * mm, "mid": v(-228.66, 93.6) * mm, "end": v(-228.73, 93.36) * mm});
            skArc(sketch, "E1529", {"start": v(-228.48, 93.8) * mm, "mid": v(-228.37, 94.58) * mm, "end": v(-229.16, 94.48) * mm});
            skArc(sketch, "E1530", {"start": v(-229.6, 94.23) * mm, "mid": v(-229.34, 94.3) * mm, "end": v(-229.16, 94.48) * mm});
            skLineSegment(sketch, "E1531", {"start": v(-229.6, 94.23) * mm, "end": v(-231.16, 94.23) * mm});
            skArc(sketch, "E1532", {"start": v(-231.6, 94.48) * mm, "mid": v(-231.4, 94.3) * mm, "end": v(-231.16, 94.23) * mm});
            skArc(sketch, "E1533", {"start": v(-231.6, 94.48) * mm, "mid": v(-232.38, 94.58) * mm, "end": v(-232.28, 93.8) * mm});
            skArc(sketch, "E1534", {"start": v(-232.03, 93.36) * mm, "mid": v(-232.1, 93.6) * mm, "end": v(-232.28, 93.8) * mm});
            skLineSegment(sketch, "E1535", {"start": v(-232.03, 93.36) * mm, "end": v(-232.03, 88.9) * mm});
            skArc(sketch, "E1536", {"start": v(-232.28, 88.46) * mm, "mid": v(-232.1, 88.64) * mm, "end": v(-232.03, 88.9) * mm});
            skArc(sketch, "E1537", {"start": v(-232.28, 88.46) * mm, "mid": v(-232.38, 87.67) * mm, "end": v(-231.6, 87.78) * mm});
            skArc(sketch, "E1538", {"start": v(-231.16, 88.03) * mm, "mid": v(-231.4, 87.96) * mm, "end": v(-231.6, 87.78) * mm});
            skLineSegment(sketch, "E1539", {"start": v(-231.16, 88.03) * mm, "end": v(-229.6, 88.03) * mm});
            skCircle(sketch, "E1540", {"center": v(9.97, 101.73) * mm, "radius": 1.6 * mm});
            skCircle(sketch, "E1541", {"center": v(-44.2, 111.73) * mm, "radius": 1.6 * mm});
            skCircle(sketch, "E1542", {"center": v(-44.2, 91.73) * mm, "radius": 1.6 * mm});
            skCircle(sketch, "E1543", {"center": v(-75.2, 111.73) * mm, "radius": 1.6 * mm});
            skCircle(sketch, "E1544", {"center": v(-75.2, 91.73) * mm, "radius": 1.6 * mm});
            skCircle(sketch, "E1545", {"center": v(-103.9, 101.34) * mm, "radius": 1.6 * mm});
            skCircle(sketch, "E1546", {"center": v(-116.5, 101.34) * mm, "radius": 1.6 * mm});
            skCircle(sketch, "E1547", {"center": v(-145.2, 111.73) * mm, "radius": 1.6 * mm});
            skCircle(sketch, "E1548", {"center": v(-145.2, 91.73) * mm, "radius": 1.6 * mm});
            skCircle(sketch, "E1549", {"center": v(-176.2, 111.73) * mm, "radius": 1.6 * mm});
            skCircle(sketch, "E1550", {"center": v(-176.2, 91.73) * mm, "radius": 1.6 * mm});
            skCircle(sketch, "E1551", {"center": v(-230.38, 101.73) * mm, "radius": 1.6 * mm});
            skArc(sketch, "E1552", {"start": v(-213.6, 121.04) * mm, "mid": v(-213.23, 120.53) * mm, "end": v(-212.64, 120.34) * mm});
            skArc(sketch, "E1553", {"start": v(-215.16, 126.02) * mm, "mid": v(-215.52, 126.53) * mm, "end": v(-216.11, 126.73) * mm});
            skArc(sketch, "E1554", {"start": v(-7.76, 120.34) * mm, "mid": v(-7.17, 120.53) * mm, "end": v(-6.8, 121.04) * mm});
            skArc(sketch, "E1555", {"start": v(-4.3, 126.73) * mm, "mid": v(-4.88, 126.53) * mm, "end": v(-5.25, 126.02) * mm});
            skArc(sketch, "E1556", {"start": v(-28.88, 74.34) * mm, "mid": v(-28.44, 74.6) * mm, "end": v(-28.47, 75.12) * mm});
            skArc(sketch, "E1557", {"start": v(-21.93, 75.12) * mm, "mid": v(-21.96, 74.6) * mm, "end": v(-21.51, 74.34) * mm});
            skArc(sketch, "E1558", {"start": v(-205.2, 76.34) * mm, "mid": v(-204.62, 74.93) * mm, "end": v(-203.2, 74.34) * mm});
            skLineSegment(sketch, "E1559", {"start": v(-203.2, 74.34) * mm, "end": v(-198.89, 74.34) * mm});
            skLineSegment(sketch, "E1560", {"start": v(-191.52, 74.34) * mm, "end": v(-187.2, 74.34) * mm});
            skArc(sketch, "E1561", {"start": v(-187.2, 74.34) * mm, "mid": v(-185.79, 74.93) * mm, "end": v(-185.2, 76.34) * mm});
            skArc(sketch, "E1562", {"start": v(-198.89, 74.34) * mm, "mid": v(-198.45, 74.6) * mm, "end": v(-198.47, 75.12) * mm});
            skArc(sketch, "E1563", {"start": v(-191.93, 75.12) * mm, "mid": v(-191.96, 74.6) * mm, "end": v(-191.52, 74.34) * mm});
            skLineSegment(sketch, "E1564", {"start": v(-185.2, 76.34) * mm, "end": v(-185.2, 81.84) * mm});
            skArc(sketch, "E1565", {"start": v(-191.93, 75.12) * mm, "mid": v(-195.2, 81.29) * mm, "end": v(-198.47, 75.12) * mm});
            skLineSegment(sketch, "E1566", {"start": v(-205.2, 81.84) * mm, "end": v(-205.2, 76.34) * mm});
            skLineSegment(sketch, "E1567", {"start": v(-7.76, 176.91) * mm, "end": v(-212.64, 176.91) * mm});
            skLineSegment(sketch, "E1568", {"start": v(-213.6, 177.61) * mm, "end": v(-215.16, 182.6) * mm});
            skLineSegment(sketch, "E1569", {"start": v(-216.11, 183.3) * mm, "end": v(-235.38, 183.3) * mm});
            skArc(sketch, "E1570", {"start": v(-235.38, 183.3) * mm, "mid": v(-238.91, 181.83) * mm, "end": v(-240.38, 178.3) * mm});
            skLineSegment(sketch, "E1571", {"start": v(-240.38, 178.3) * mm, "end": v(-240.38, 143.91) * mm});
            skArc(sketch, "E1572", {"start": v(-240.38, 143.91) * mm, "mid": v(-238.91, 140.38) * mm, "end": v(-235.38, 138.91) * mm});
            skLineSegment(sketch, "E1573", {"start": v(-235.38, 138.91) * mm, "end": v(-205.7, 138.91) * mm});
            skArc(sketch, "E1574", {"start": v(-205.2, 138.41) * mm, "mid": v(-205.35, 138.77) * mm, "end": v(-205.7, 138.91) * mm});
            skArc(sketch, "E1575", {"start": v(-184.7, 138.91) * mm, "mid": v(-185.06, 138.77) * mm, "end": v(-185.2, 138.41) * mm});
            skLineSegment(sketch, "E1576", {"start": v(-184.7, 138.91) * mm, "end": v(-35.7, 138.91) * mm});
            skArc(sketch, "E1577", {"start": v(-35.2, 138.41) * mm, "mid": v(-35.34, 138.77) * mm, "end": v(-35.7, 138.91) * mm});
            skLineSegment(sketch, "E1578", {"start": v(-35.2, 138.41) * mm, "end": v(-35.2, 132.91) * mm});
            skArc(sketch, "E1579", {"start": v(-35.2, 132.91) * mm, "mid": v(-34.61, 131.5) * mm, "end": v(-33.2, 130.91) * mm});
            skLineSegment(sketch, "E1580", {"start": v(-33.2, 130.91) * mm, "end": v(-28.88, 130.91) * mm});
            skArc(sketch, "E1581", {"start": v(-21.93, 131.7) * mm, "mid": v(-25.2, 137.86) * mm, "end": v(-28.47, 131.7) * mm});
            skLineSegment(sketch, "E1582", {"start": v(-21.51, 130.91) * mm, "end": v(-17.2, 130.91) * mm});
            skArc(sketch, "E1583", {"start": v(-17.2, 130.91) * mm, "mid": v(-15.78, 131.5) * mm, "end": v(-15.2, 132.91) * mm});
            skLineSegment(sketch, "E1584", {"start": v(-15.2, 132.91) * mm, "end": v(-15.2, 138.41) * mm});
            skArc(sketch, "E1585", {"start": v(-14.7, 138.91) * mm, "mid": v(-15.05, 138.77) * mm, "end": v(-15.2, 138.41) * mm});
            skLineSegment(sketch, "E1586", {"start": v(-14.7, 138.91) * mm, "end": v(14.97, 138.91) * mm});
            skArc(sketch, "E1587", {"start": v(14.97, 138.91) * mm, "mid": v(18.5, 140.38) * mm, "end": v(19.97, 143.91) * mm});
            skLineSegment(sketch, "E1588", {"start": v(19.97, 143.91) * mm, "end": v(19.97, 178.3) * mm});
            skArc(sketch, "E1589", {"start": v(19.97, 178.3) * mm, "mid": v(18.5, 181.83) * mm, "end": v(14.97, 183.3) * mm});
            skLineSegment(sketch, "E1590", {"start": v(14.97, 183.3) * mm, "end": v(-4.3, 183.3) * mm});
            skLineSegment(sketch, "E1591", {"start": v(-5.25, 182.6) * mm, "end": v(-6.8, 177.61) * mm});
            skArc(sketch, "E1592", {"start": v(9.2, 165.8) * mm, "mid": v(8.94, 165.73) * mm, "end": v(8.76, 165.55) * mm});
            skArc(sketch, "E1593", {"start": v(8.07, 166.23) * mm, "mid": v(7.97, 165.45) * mm, "end": v(8.76, 165.55) * mm});
            skArc(sketch, "E1594", {"start": v(8.07, 166.23) * mm, "mid": v(8.26, 166.42) * mm, "end": v(8.32, 166.67) * mm});
            skLineSegment(sketch, "E1595", {"start": v(8.32, 166.67) * mm, "end": v(8.32, 171.13) * mm});
            skArc(sketch, "E1596", {"start": v(8.32, 171.13) * mm, "mid": v(8.26, 171.38) * mm, "end": v(8.07, 171.57) * mm});
            skArc(sketch, "E1597", {"start": v(8.76, 172.25) * mm, "mid": v(7.97, 172.35) * mm, "end": v(8.07, 171.57) * mm});
            skArc(sketch, "E1598", {"start": v(8.76, 172.25) * mm, "mid": v(8.94, 172.07) * mm, "end": v(9.2, 172) * mm});
            skLineSegment(sketch, "E1599", {"start": v(9.2, 172) * mm, "end": v(10.76, 172) * mm});
            skArc(sketch, "E1600", {"start": v(10.76, 172) * mm, "mid": v(11, 172.07) * mm, "end": v(11.2, 172.25) * mm});
            skArc(sketch, "E1601", {"start": v(11.87, 171.57) * mm, "mid": v(11.98, 172.35) * mm, "end": v(11.2, 172.25) * mm});
            skArc(sketch, "E1602", {"start": v(11.87, 171.57) * mm, "mid": v(11.7, 171.38) * mm, "end": v(11.62, 171.13) * mm});
            skLineSegment(sketch, "E1603", {"start": v(11.62, 171.13) * mm, "end": v(11.62, 166.67) * mm});
            skArc(sketch, "E1604", {"start": v(11.62, 166.67) * mm, "mid": v(11.7, 166.42) * mm, "end": v(11.87, 166.23) * mm});
            skArc(sketch, "E1605", {"start": v(11.2, 165.55) * mm, "mid": v(11.98, 165.45) * mm, "end": v(11.87, 166.23) * mm});
            skArc(sketch, "E1606", {"start": v(11.2, 165.55) * mm, "mid": v(11, 165.73) * mm, "end": v(10.76, 165.8) * mm});
            skLineSegment(sketch, "E1607", {"start": v(10.76, 165.8) * mm, "end": v(9.2, 165.8) * mm});
            skArc(sketch, "E1608", {"start": v(9.2, 144.6) * mm, "mid": v(8.94, 144.53) * mm, "end": v(8.76, 144.35) * mm});
            skArc(sketch, "E1609", {"start": v(8.07, 145.03) * mm, "mid": v(7.97, 144.25) * mm, "end": v(8.76, 144.35) * mm});
            skArc(sketch, "E1610", {"start": v(8.07, 145.03) * mm, "mid": v(8.26, 145.22) * mm, "end": v(8.32, 145.47) * mm});
            skLineSegment(sketch, "E1611", {"start": v(8.32, 145.47) * mm, "end": v(8.32, 149.93) * mm});
            skArc(sketch, "E1612", {"start": v(8.32, 149.93) * mm, "mid": v(8.26, 150.18) * mm, "end": v(8.07, 150.37) * mm});
            skArc(sketch, "E1613", {"start": v(8.76, 151.05) * mm, "mid": v(7.97, 151.15) * mm, "end": v(8.07, 150.37) * mm});
            skArc(sketch, "E1614", {"start": v(8.76, 151.05) * mm, "mid": v(8.94, 150.87) * mm, "end": v(9.2, 150.8) * mm});
            skLineSegment(sketch, "E1615", {"start": v(9.2, 150.8) * mm, "end": v(10.76, 150.8) * mm});
            skArc(sketch, "E1616", {"start": v(10.76, 150.8) * mm, "mid": v(11, 150.87) * mm, "end": v(11.2, 151.05) * mm});
            skArc(sketch, "E1617", {"start": v(11.87, 150.37) * mm, "mid": v(11.98, 151.15) * mm, "end": v(11.2, 151.05) * mm});
            skArc(sketch, "E1618", {"start": v(11.87, 150.37) * mm, "mid": v(11.7, 150.18) * mm, "end": v(11.62, 149.93) * mm});
            skLineSegment(sketch, "E1619", {"start": v(11.62, 149.93) * mm, "end": v(11.62, 145.47) * mm});
            skArc(sketch, "E1620", {"start": v(11.62, 145.47) * mm, "mid": v(11.7, 145.22) * mm, "end": v(11.87, 145.03) * mm});
            skArc(sketch, "E1621", {"start": v(11.2, 144.35) * mm, "mid": v(11.98, 144.25) * mm, "end": v(11.87, 145.03) * mm});
            skArc(sketch, "E1622", {"start": v(11.2, 144.35) * mm, "mid": v(11, 144.53) * mm, "end": v(10.76, 144.6) * mm});
            skLineSegment(sketch, "E1623", {"start": v(10.76, 144.6) * mm, "end": v(9.2, 144.6) * mm});
            skArc(sketch, "E1624", {"start": v(-104.68, 165.41) * mm, "mid": v(-104.93, 165.34) * mm, "end": v(-105.12, 165.16) * mm});
            skArc(sketch, "E1625", {"start": v(-105.8, 165.84) * mm, "mid": v(-105.9, 165.06) * mm, "end": v(-105.12, 165.16) * mm});
            skArc(sketch, "E1626", {"start": v(-105.8, 165.84) * mm, "mid": v(-105.62, 166.03) * mm, "end": v(-105.55, 166.28) * mm});
            skLineSegment(sketch, "E1627", {"start": v(-105.55, 166.28) * mm, "end": v(-105.55, 170.75) * mm});
            skArc(sketch, "E1628", {"start": v(-105.55, 170.75) * mm, "mid": v(-105.62, 171) * mm, "end": v(-105.8, 171.18) * mm});
            skArc(sketch, "E1629", {"start": v(-105.12, 171.86) * mm, "mid": v(-105.9, 171.97) * mm, "end": v(-105.8, 171.18) * mm});
            skArc(sketch, "E1630", {"start": v(-105.12, 171.86) * mm, "mid": v(-104.93, 171.68) * mm, "end": v(-104.68, 171.61) * mm});
            skLineSegment(sketch, "E1631", {"start": v(-104.68, 171.61) * mm, "end": v(-103.12, 171.61) * mm});
            skArc(sketch, "E1632", {"start": v(-103.12, 171.61) * mm, "mid": v(-102.87, 171.68) * mm, "end": v(-102.68, 171.86) * mm});
            skArc(sketch, "E1633", {"start": v(-102, 171.18) * mm, "mid": v(-101.9, 171.97) * mm, "end": v(-102.68, 171.86) * mm});
            skArc(sketch, "E1634", {"start": v(-102, 171.18) * mm, "mid": v(-102.18, 171) * mm, "end": v(-102.25, 170.75) * mm});
            skLineSegment(sketch, "E1635", {"start": v(-102.25, 170.75) * mm, "end": v(-102.25, 166.28) * mm});
            skArc(sketch, "E1636", {"start": v(-102.25, 166.28) * mm, "mid": v(-102.18, 166.03) * mm, "end": v(-102, 165.84) * mm});
            skArc(sketch, "E1637", {"start": v(-102.68, 165.16) * mm, "mid": v(-101.9, 165.06) * mm, "end": v(-102, 165.84) * mm});
            skArc(sketch, "E1638", {"start": v(-102.68, 165.16) * mm, "mid": v(-102.87, 165.34) * mm, "end": v(-103.12, 165.41) * mm});
            skLineSegment(sketch, "E1639", {"start": v(-103.12, 165.41) * mm, "end": v(-104.68, 165.41) * mm});
            skArc(sketch, "E1640", {"start": v(-104.68, 144.21) * mm, "mid": v(-104.93, 144.14) * mm, "end": v(-105.12, 143.96) * mm});
            skArc(sketch, "E1641", {"start": v(-105.8, 144.64) * mm, "mid": v(-105.9, 143.86) * mm, "end": v(-105.12, 143.96) * mm});
            skArc(sketch, "E1642", {"start": v(-105.8, 144.64) * mm, "mid": v(-105.62, 144.83) * mm, "end": v(-105.55, 145.08) * mm});
            skLineSegment(sketch, "E1643", {"start": v(-105.55, 145.08) * mm, "end": v(-105.55, 149.55) * mm});
            skArc(sketch, "E1644", {"start": v(-105.55, 149.55) * mm, "mid": v(-105.62, 149.8) * mm, "end": v(-105.8, 149.98) * mm});
            skArc(sketch, "E1645", {"start": v(-105.12, 150.66) * mm, "mid": v(-105.9, 150.77) * mm, "end": v(-105.8, 149.98) * mm});
            skArc(sketch, "E1646", {"start": v(-105.12, 150.66) * mm, "mid": v(-104.93, 150.48) * mm, "end": v(-104.68, 150.41) * mm});
            skLineSegment(sketch, "E1647", {"start": v(-104.68, 150.41) * mm, "end": v(-103.12, 150.41) * mm});
            skArc(sketch, "E1648", {"start": v(-103.12, 150.41) * mm, "mid": v(-102.87, 150.48) * mm, "end": v(-102.68, 150.66) * mm});
            skArc(sketch, "E1649", {"start": v(-102, 149.98) * mm, "mid": v(-101.9, 150.77) * mm, "end": v(-102.68, 150.66) * mm});
            skArc(sketch, "E1650", {"start": v(-102, 149.98) * mm, "mid": v(-102.18, 149.8) * mm, "end": v(-102.25, 149.55) * mm});
            skLineSegment(sketch, "E1651", {"start": v(-102.25, 149.55) * mm, "end": v(-102.25, 145.08) * mm});
            skArc(sketch, "E1652", {"start": v(-102.25, 145.08) * mm, "mid": v(-102.18, 144.83) * mm, "end": v(-102, 144.64) * mm});
            skArc(sketch, "E1653", {"start": v(-102.68, 143.96) * mm, "mid": v(-101.9, 143.86) * mm, "end": v(-102, 144.64) * mm});
            skArc(sketch, "E1654", {"start": v(-102.68, 143.96) * mm, "mid": v(-102.87, 144.14) * mm, "end": v(-103.12, 144.21) * mm});
            skLineSegment(sketch, "E1655", {"start": v(-103.12, 144.21) * mm, "end": v(-104.68, 144.21) * mm});
            skArc(sketch, "E1656", {"start": v(-117.28, 165.41) * mm, "mid": v(-117.53, 165.34) * mm, "end": v(-117.72, 165.16) * mm});
            skArc(sketch, "E1657", {"start": v(-118.4, 165.84) * mm, "mid": v(-118.5, 165.06) * mm, "end": v(-117.72, 165.16) * mm});
            skArc(sketch, "E1658", {"start": v(-118.4, 165.84) * mm, "mid": v(-118.22, 166.03) * mm, "end": v(-118.15, 166.28) * mm});
            skLineSegment(sketch, "E1659", {"start": v(-118.15, 166.28) * mm, "end": v(-118.15, 170.75) * mm});
            skArc(sketch, "E1660", {"start": v(-118.15, 170.75) * mm, "mid": v(-118.22, 171) * mm, "end": v(-118.4, 171.18) * mm});
            skArc(sketch, "E1661", {"start": v(-117.72, 171.86) * mm, "mid": v(-118.5, 171.97) * mm, "end": v(-118.4, 171.18) * mm});
            skArc(sketch, "E1662", {"start": v(-117.72, 171.86) * mm, "mid": v(-117.53, 171.68) * mm, "end": v(-117.28, 171.61) * mm});
            skLineSegment(sketch, "E1663", {"start": v(-117.28, 171.61) * mm, "end": v(-115.72, 171.61) * mm});
            skArc(sketch, "E1664", {"start": v(-115.72, 171.61) * mm, "mid": v(-115.47, 171.68) * mm, "end": v(-115.28, 171.86) * mm});
            skArc(sketch, "E1665", {"start": v(-114.6, 171.18) * mm, "mid": v(-114.5, 171.97) * mm, "end": v(-115.28, 171.86) * mm});
            skArc(sketch, "E1666", {"start": v(-114.6, 171.18) * mm, "mid": v(-114.78, 171) * mm, "end": v(-114.85, 170.75) * mm});
            skLineSegment(sketch, "E1667", {"start": v(-114.85, 170.75) * mm, "end": v(-114.85, 166.28) * mm});
            skArc(sketch, "E1668", {"start": v(-114.85, 166.28) * mm, "mid": v(-114.78, 166.03) * mm, "end": v(-114.6, 165.84) * mm});
            skArc(sketch, "E1669", {"start": v(-115.28, 165.16) * mm, "mid": v(-114.5, 165.06) * mm, "end": v(-114.6, 165.84) * mm});
            skArc(sketch, "E1670", {"start": v(-115.28, 165.16) * mm, "mid": v(-115.47, 165.34) * mm, "end": v(-115.72, 165.41) * mm});
            skLineSegment(sketch, "E1671", {"start": v(-115.72, 165.41) * mm, "end": v(-117.28, 165.41) * mm});
            skArc(sketch, "E1672", {"start": v(-117.28, 144.21) * mm, "mid": v(-117.53, 144.14) * mm, "end": v(-117.72, 143.96) * mm});
            skArc(sketch, "E1673", {"start": v(-118.4, 144.64) * mm, "mid": v(-118.5, 143.86) * mm, "end": v(-117.72, 143.96) * mm});
            skArc(sketch, "E1674", {"start": v(-118.4, 144.64) * mm, "mid": v(-118.22, 144.83) * mm, "end": v(-118.15, 145.08) * mm});
            skLineSegment(sketch, "E1675", {"start": v(-118.15, 145.08) * mm, "end": v(-118.15, 149.55) * mm});
            skArc(sketch, "E1676", {"start": v(-118.15, 149.55) * mm, "mid": v(-118.22, 149.8) * mm, "end": v(-118.4, 149.98) * mm});
            skArc(sketch, "E1677", {"start": v(-117.72, 150.66) * mm, "mid": v(-118.5, 150.77) * mm, "end": v(-118.4, 149.98) * mm});
            skArc(sketch, "E1678", {"start": v(-117.72, 150.66) * mm, "mid": v(-117.53, 150.48) * mm, "end": v(-117.28, 150.41) * mm});
            skLineSegment(sketch, "E1679", {"start": v(-117.28, 150.41) * mm, "end": v(-115.72, 150.41) * mm});
            skArc(sketch, "E1680", {"start": v(-115.72, 150.41) * mm, "mid": v(-115.47, 150.48) * mm, "end": v(-115.28, 150.66) * mm});
            skArc(sketch, "E1681", {"start": v(-114.6, 149.98) * mm, "mid": v(-114.5, 150.77) * mm, "end": v(-115.28, 150.66) * mm});
            skArc(sketch, "E1682", {"start": v(-114.6, 149.98) * mm, "mid": v(-114.78, 149.8) * mm, "end": v(-114.85, 149.55) * mm});
            skLineSegment(sketch, "E1683", {"start": v(-114.85, 149.55) * mm, "end": v(-114.85, 145.08) * mm});
            skArc(sketch, "E1684", {"start": v(-114.85, 145.08) * mm, "mid": v(-114.78, 144.83) * mm, "end": v(-114.6, 144.64) * mm});
            skArc(sketch, "E1685", {"start": v(-115.28, 143.96) * mm, "mid": v(-114.5, 143.86) * mm, "end": v(-114.6, 144.64) * mm});
            skArc(sketch, "E1686", {"start": v(-115.28, 143.96) * mm, "mid": v(-115.47, 144.14) * mm, "end": v(-115.72, 144.21) * mm});
            skLineSegment(sketch, "E1687", {"start": v(-115.72, 144.21) * mm, "end": v(-117.28, 144.21) * mm});
            skArc(sketch, "E1688", {"start": v(-229.16, 165.55) * mm, "mid": v(-229.34, 165.73) * mm, "end": v(-229.6, 165.8) * mm});
            skArc(sketch, "E1689", {"start": v(-229.16, 165.55) * mm, "mid": v(-228.37, 165.45) * mm, "end": v(-228.48, 166.23) * mm});
            skArc(sketch, "E1690", {"start": v(-228.73, 166.67) * mm, "mid": v(-228.66, 166.42) * mm, "end": v(-228.48, 166.23) * mm});
            skLineSegment(sketch, "E1691", {"start": v(-228.73, 166.67) * mm, "end": v(-228.73, 171.13) * mm});
            skArc(sketch, "E1692", {"start": v(-228.48, 171.57) * mm, "mid": v(-228.66, 171.38) * mm, "end": v(-228.73, 171.13) * mm});
            skArc(sketch, "E1693", {"start": v(-228.48, 171.57) * mm, "mid": v(-228.37, 172.35) * mm, "end": v(-229.16, 172.25) * mm});
            skArc(sketch, "E1694", {"start": v(-229.6, 172) * mm, "mid": v(-229.34, 172.07) * mm, "end": v(-229.16, 172.25) * mm});
            skLineSegment(sketch, "E1695", {"start": v(-229.6, 172) * mm, "end": v(-231.16, 172) * mm});
            skArc(sketch, "E1696", {"start": v(-231.6, 172.25) * mm, "mid": v(-231.4, 172.07) * mm, "end": v(-231.16, 172) * mm});
            skArc(sketch, "E1697", {"start": v(-231.6, 172.25) * mm, "mid": v(-232.38, 172.35) * mm, "end": v(-232.28, 171.57) * mm});
            skArc(sketch, "E1698", {"start": v(-232.03, 171.13) * mm, "mid": v(-232.1, 171.38) * mm, "end": v(-232.28, 171.57) * mm});
            skLineSegment(sketch, "E1699", {"start": v(-232.03, 171.13) * mm, "end": v(-232.03, 166.67) * mm});
            skArc(sketch, "E1700", {"start": v(-232.28, 166.23) * mm, "mid": v(-232.1, 166.42) * mm, "end": v(-232.03, 166.67) * mm});
            skArc(sketch, "E1701", {"start": v(-232.28, 166.23) * mm, "mid": v(-232.38, 165.45) * mm, "end": v(-231.6, 165.55) * mm});
            skArc(sketch, "E1702", {"start": v(-231.16, 165.8) * mm, "mid": v(-231.4, 165.73) * mm, "end": v(-231.6, 165.55) * mm});
            skLineSegment(sketch, "E1703", {"start": v(-231.16, 165.8) * mm, "end": v(-229.6, 165.8) * mm});
            skArc(sketch, "E1704", {"start": v(-229.16, 144.35) * mm, "mid": v(-229.34, 144.53) * mm, "end": v(-229.6, 144.6) * mm});
            skArc(sketch, "E1705", {"start": v(-229.16, 144.35) * mm, "mid": v(-228.37, 144.25) * mm, "end": v(-228.48, 145.03) * mm});
            skArc(sketch, "E1706", {"start": v(-228.73, 145.47) * mm, "mid": v(-228.66, 145.22) * mm, "end": v(-228.48, 145.03) * mm});
            skLineSegment(sketch, "E1707", {"start": v(-228.73, 145.47) * mm, "end": v(-228.73, 149.93) * mm});
            skArc(sketch, "E1708", {"start": v(-228.48, 150.37) * mm, "mid": v(-228.66, 150.18) * mm, "end": v(-228.73, 149.93) * mm});
            skArc(sketch, "E1709", {"start": v(-228.48, 150.37) * mm, "mid": v(-228.37, 151.15) * mm, "end": v(-229.16, 151.05) * mm});
            skArc(sketch, "E1710", {"start": v(-229.6, 150.8) * mm, "mid": v(-229.34, 150.87) * mm, "end": v(-229.16, 151.05) * mm});
            skLineSegment(sketch, "E1711", {"start": v(-229.6, 150.8) * mm, "end": v(-231.16, 150.8) * mm});
            skArc(sketch, "E1712", {"start": v(-231.6, 151.05) * mm, "mid": v(-231.4, 150.87) * mm, "end": v(-231.16, 150.8) * mm});
            skArc(sketch, "E1713", {"start": v(-231.6, 151.05) * mm, "mid": v(-232.38, 151.15) * mm, "end": v(-232.28, 150.37) * mm});
            skArc(sketch, "E1714", {"start": v(-232.03, 149.93) * mm, "mid": v(-232.1, 150.18) * mm, "end": v(-232.28, 150.37) * mm});
            skLineSegment(sketch, "E1715", {"start": v(-232.03, 149.93) * mm, "end": v(-232.03, 145.47) * mm});
            skArc(sketch, "E1716", {"start": v(-232.28, 145.03) * mm, "mid": v(-232.1, 145.22) * mm, "end": v(-232.03, 145.47) * mm});
            skArc(sketch, "E1717", {"start": v(-232.28, 145.03) * mm, "mid": v(-232.38, 144.25) * mm, "end": v(-231.6, 144.35) * mm});
            skArc(sketch, "E1718", {"start": v(-231.16, 144.6) * mm, "mid": v(-231.4, 144.53) * mm, "end": v(-231.6, 144.35) * mm});
            skLineSegment(sketch, "E1719", {"start": v(-231.16, 144.6) * mm, "end": v(-229.6, 144.6) * mm});
            skCircle(sketch, "E1720", {"center": v(9.97, 158.3) * mm, "radius": 1.6 * mm});
            skCircle(sketch, "E1721", {"center": v(-44.2, 168.3) * mm, "radius": 1.6 * mm});
            skCircle(sketch, "E1722", {"center": v(-44.2, 148.3) * mm, "radius": 1.6 * mm});
            skCircle(sketch, "E1723", {"center": v(-75.2, 168.3) * mm, "radius": 1.6 * mm});
            skCircle(sketch, "E1724", {"center": v(-75.2, 148.3) * mm, "radius": 1.6 * mm});
            skCircle(sketch, "E1725", {"center": v(-103.9, 157.91) * mm, "radius": 1.6 * mm});
            skCircle(sketch, "E1726", {"center": v(-116.5, 157.91) * mm, "radius": 1.6 * mm});
            skCircle(sketch, "E1727", {"center": v(-145.2, 168.3) * mm, "radius": 1.6 * mm});
            skCircle(sketch, "E1728", {"center": v(-145.2, 148.3) * mm, "radius": 1.6 * mm});
            skCircle(sketch, "E1729", {"center": v(-176.2, 168.3) * mm, "radius": 1.6 * mm});
            skCircle(sketch, "E1730", {"center": v(-176.2, 148.3) * mm, "radius": 1.6 * mm});
            skCircle(sketch, "E1731", {"center": v(-230.38, 158.3) * mm, "radius": 1.6 * mm});
            skArc(sketch, "E1732", {"start": v(-213.6, 177.61) * mm, "mid": v(-213.23, 177.1) * mm, "end": v(-212.64, 176.91) * mm});
            skArc(sketch, "E1733", {"start": v(-215.16, 182.6) * mm, "mid": v(-215.52, 183.1) * mm, "end": v(-216.11, 183.3) * mm});
            skArc(sketch, "E1734", {"start": v(-7.76, 176.91) * mm, "mid": v(-7.17, 177.1) * mm, "end": v(-6.8, 177.61) * mm});
            skArc(sketch, "E1735", {"start": v(-4.3, 183.3) * mm, "mid": v(-4.88, 183.1) * mm, "end": v(-5.25, 182.6) * mm});
            skArc(sketch, "E1736", {"start": v(-28.88, 130.91) * mm, "mid": v(-28.44, 131.18) * mm, "end": v(-28.47, 131.7) * mm});
            skArc(sketch, "E1737", {"start": v(-21.93, 131.7) * mm, "mid": v(-21.96, 131.18) * mm, "end": v(-21.51, 130.91) * mm});
            skArc(sketch, "E1738", {"start": v(-205.2, 132.91) * mm, "mid": v(-204.62, 131.5) * mm, "end": v(-203.2, 130.91) * mm});
            skLineSegment(sketch, "E1739", {"start": v(-203.2, 130.91) * mm, "end": v(-198.89, 130.91) * mm});
            skLineSegment(sketch, "E1740", {"start": v(-191.52, 130.91) * mm, "end": v(-187.2, 130.91) * mm});
            skArc(sketch, "E1741", {"start": v(-187.2, 130.91) * mm, "mid": v(-185.79, 131.5) * mm, "end": v(-185.2, 132.91) * mm});
            skArc(sketch, "E1742", {"start": v(-198.89, 130.91) * mm, "mid": v(-198.45, 131.18) * mm, "end": v(-198.47, 131.7) * mm});
            skArc(sketch, "E1743", {"start": v(-191.93, 131.7) * mm, "mid": v(-191.96, 131.18) * mm, "end": v(-191.52, 130.91) * mm});
            skLineSegment(sketch, "E1744", {"start": v(-185.2, 132.91) * mm, "end": v(-185.2, 138.41) * mm});
            skArc(sketch, "E1745", {"start": v(-191.93, 131.7) * mm, "mid": v(-195.2, 137.86) * mm, "end": v(-198.47, 131.7) * mm});
            skLineSegment(sketch, "E1746", {"start": v(-205.2, 138.41) * mm, "end": v(-205.2, 132.91) * mm});
            skLineSegment(sketch, "E1747", {"start": v(86.38, 185.14) * mm, "end": v(86.38, 140.14) * mm});
            skArc(sketch, "E1748", {"start": v(81.38, 135.14) * mm, "mid": v(84.92, 136.6) * mm, "end": v(86.38, 140.14) * mm});
            skLineSegment(sketch, "E1749", {"start": v(81.38, 135.14) * mm, "end": v(31.38, 135.14) * mm});
            skArc(sketch, "E1750", {"start": v(26.38, 140.14) * mm, "mid": v(27.85, 136.6) * mm, "end": v(31.38, 135.14) * mm});
            skLineSegment(sketch, "E1751", {"start": v(26.38, 140.14) * mm, "end": v(26.38, 185.14) * mm});
            skLineSegment(sketch, "E1752", {"start": v(26.38, 185.14) * mm, "end": v(41.92, 185.14) * mm});
            skArc(sketch, "E1753", {"start": v(42.35, 184.89) * mm, "mid": v(42.17, 185.07) * mm, "end": v(41.92, 185.14) * mm});
            skArc(sketch, "E1754", {"start": v(42.35, 184.89) * mm, "mid": v(43.13, 184.78) * mm, "end": v(43.03, 185.57) * mm});
            skArc(sketch, "E1755", {"start": v(42.78, 186) * mm, "mid": v(42.85, 185.75) * mm, "end": v(43.03, 185.57) * mm});
            skLineSegment(sketch, "E1756", {"start": v(42.78, 186) * mm, "end": v(42.78, 187.64) * mm});
            skArc(sketch, "E1757", {"start": v(43.28, 188.14) * mm, "mid": v(42.93, 187.99) * mm, "end": v(42.78, 187.64) * mm});
            skLineSegment(sketch, "E1758", {"start": v(43.28, 188.14) * mm, "end": v(48.28, 188.14) * mm});
            skArc(sketch, "E1759", {"start": v(48.78, 187.64) * mm, "mid": v(48.63, 187.99) * mm, "end": v(48.28, 188.14) * mm});
            skLineSegment(sketch, "E1760", {"start": v(48.78, 187.64) * mm, "end": v(48.78, 186) * mm});
            skArc(sketch, "E1761", {"start": v(48.53, 185.57) * mm, "mid": v(48.71, 185.75) * mm, "end": v(48.78, 186) * mm});
            skArc(sketch, "E1762", {"start": v(48.53, 185.57) * mm, "mid": v(48.43, 184.78) * mm, "end": v(49.21, 184.89) * mm});
            skArc(sketch, "E1763", {"start": v(49.65, 185.14) * mm, "mid": v(49.4, 185.07) * mm, "end": v(49.21, 184.89) * mm});
            skLineSegment(sketch, "E1764", {"start": v(49.65, 185.14) * mm, "end": v(54.78, 185.14) * mm});
            skLineSegment(sketch, "E1765", {"start": v(54.78, 185.14) * mm, "end": v(54.78, 182.14) * mm});
            skLineSegment(sketch, "E1766", {"start": v(54.78, 182.14) * mm, "end": v(53.5, 182.14) * mm});
            skLineSegment(sketch, "E1767", {"start": v(53.5, 182.14) * mm, "end": v(53.5, 178.14) * mm});
            skLineSegment(sketch, "E1768", {"start": v(53.5, 178.14) * mm, "end": v(54.78, 178.14) * mm});
            skLineSegment(sketch, "E1769", {"start": v(54.78, 178.14) * mm, "end": v(54.78, 175.14) * mm});
            skLineSegment(sketch, "E1770", {"start": v(54.78, 175.14) * mm, "end": v(57.98, 175.14) * mm});
            skLineSegment(sketch, "E1771", {"start": v(57.98, 175.14) * mm, "end": v(57.98, 178.14) * mm});
            skLineSegment(sketch, "E1772", {"start": v(57.98, 178.14) * mm, "end": v(59.26, 178.14) * mm});
            skLineSegment(sketch, "E1773", {"start": v(59.26, 178.14) * mm, "end": v(59.26, 182.14) * mm});
            skLineSegment(sketch, "E1774", {"start": v(59.26, 182.14) * mm, "end": v(57.98, 182.14) * mm});
            skLineSegment(sketch, "E1775", {"start": v(57.98, 182.14) * mm, "end": v(57.98, 185.14) * mm});
            skLineSegment(sketch, "E1776", {"start": v(57.98, 185.14) * mm, "end": v(63.12, 185.14) * mm});
            skArc(sketch, "E1777", {"start": v(63.55, 184.89) * mm, "mid": v(63.37, 185.07) * mm, "end": v(63.12, 185.14) * mm});
            skArc(sketch, "E1778", {"start": v(63.55, 184.89) * mm, "mid": v(64.33, 184.78) * mm, "end": v(64.23, 185.57) * mm});
            skArc(sketch, "E1779", {"start": v(63.98, 186) * mm, "mid": v(64.05, 185.75) * mm, "end": v(64.23, 185.57) * mm});
            skLineSegment(sketch, "E1780", {"start": v(63.98, 186) * mm, "end": v(63.98, 187.64) * mm});
            skArc(sketch, "E1781", {"start": v(64.48, 188.14) * mm, "mid": v(64.13, 187.99) * mm, "end": v(63.98, 187.64) * mm});
            skLineSegment(sketch, "E1782", {"start": v(64.48, 188.14) * mm, "end": v(69.48, 188.14) * mm});
            skArc(sketch, "E1783", {"start": v(69.98, 187.64) * mm, "mid": v(69.83, 187.99) * mm, "end": v(69.48, 188.14) * mm});
            skLineSegment(sketch, "E1784", {"start": v(69.98, 187.64) * mm, "end": v(69.98, 186) * mm});
            skArc(sketch, "E1785", {"start": v(69.73, 185.57) * mm, "mid": v(69.91, 185.75) * mm, "end": v(69.98, 186) * mm});
            skArc(sketch, "E1786", {"start": v(69.73, 185.57) * mm, "mid": v(69.63, 184.78) * mm, "end": v(70.41, 184.89) * mm});
            skArc(sketch, "E1787", {"start": v(70.85, 185.14) * mm, "mid": v(70.6, 185.07) * mm, "end": v(70.41, 184.89) * mm});
            skLineSegment(sketch, "E1788", {"start": v(70.85, 185.14) * mm, "end": v(86.38, 185.14) * mm});
            skCircle(sketch, "E1789", {"center": v(56.38, 155.84) * mm, "radius": 11.1 * mm});
            skCircle(sketch, "E1790", {"center": v(73.38, 155.84) * mm, "radius": 4 * mm});
            skArc(sketch, "E1791", {"start": v(80.12, 167.64) * mm, "mid": v(79.87, 167.57) * mm, "end": v(79.68, 167.39) * mm});
            skArc(sketch, "E1792", {"start": v(79, 168.07) * mm, "mid": v(78.9, 167.28) * mm, "end": v(79.68, 167.39) * mm});
            skArc(sketch, "E1793", {"start": v(79, 168.07) * mm, "mid": v(79.18, 168.25) * mm, "end": v(79.25, 168.5) * mm});
            skLineSegment(sketch, "E1794", {"start": v(79.25, 168.5) * mm, "end": v(79.25, 172.97) * mm});
            skArc(sketch, "E1795", {"start": v(79.25, 172.97) * mm, "mid": v(79.18, 173.22) * mm, "end": v(79, 173.4) * mm});
            skArc(sketch, "E1796", {"start": v(79.68, 174.09) * mm, "mid": v(78.9, 174.19) * mm, "end": v(79, 173.4) * mm});
            skArc(sketch, "E1797", {"start": v(79.68, 174.09) * mm, "mid": v(79.87, 173.9) * mm, "end": v(80.12, 173.84) * mm});
            skLineSegment(sketch, "E1798", {"start": v(80.12, 173.84) * mm, "end": v(81.69, 173.84) * mm});
            skArc(sketch, "E1799", {"start": v(81.69, 173.84) * mm, "mid": v(81.94, 173.9) * mm, "end": v(82.12, 174.09) * mm});
            skArc(sketch, "E1800", {"start": v(82.8, 173.4) * mm, "mid": v(82.9, 174.19) * mm, "end": v(82.12, 174.09) * mm});
            skArc(sketch, "E1801", {"start": v(82.8, 173.4) * mm, "mid": v(82.62, 173.22) * mm, "end": v(82.55, 172.97) * mm});
            skLineSegment(sketch, "E1802", {"start": v(82.55, 172.97) * mm, "end": v(82.55, 168.5) * mm});
            skArc(sketch, "E1803", {"start": v(82.55, 168.5) * mm, "mid": v(82.62, 168.25) * mm, "end": v(82.8, 168.07) * mm});
            skArc(sketch, "E1804", {"start": v(82.12, 167.39) * mm, "mid": v(82.9, 167.28) * mm, "end": v(82.8, 168.07) * mm});
            skArc(sketch, "E1805", {"start": v(82.12, 167.39) * mm, "mid": v(81.94, 167.57) * mm, "end": v(81.69, 167.64) * mm});
            skLineSegment(sketch, "E1806", {"start": v(81.69, 167.64) * mm, "end": v(80.12, 167.64) * mm});
            skArc(sketch, "E1807", {"start": v(80.12, 146.44) * mm, "mid": v(79.87, 146.37) * mm, "end": v(79.68, 146.19) * mm});
            skArc(sketch, "E1808", {"start": v(79, 146.87) * mm, "mid": v(78.9, 146.08) * mm, "end": v(79.68, 146.19) * mm});
            skArc(sketch, "E1809", {"start": v(79, 146.87) * mm, "mid": v(79.18, 147.05) * mm, "end": v(79.25, 147.3) * mm});
            skLineSegment(sketch, "E1810", {"start": v(79.25, 147.3) * mm, "end": v(79.25, 151.77) * mm});
            skArc(sketch, "E1811", {"start": v(79.25, 151.77) * mm, "mid": v(79.18, 152.02) * mm, "end": v(79, 152.2) * mm});
            skArc(sketch, "E1812", {"start": v(79.68, 152.89) * mm, "mid": v(78.9, 152.99) * mm, "end": v(79, 152.2) * mm});
            skArc(sketch, "E1813", {"start": v(79.68, 152.89) * mm, "mid": v(79.87, 152.7) * mm, "end": v(80.12, 152.64) * mm});
            skLineSegment(sketch, "E1814", {"start": v(80.12, 152.64) * mm, "end": v(81.69, 152.64) * mm});
            skArc(sketch, "E1815", {"start": v(81.69, 152.64) * mm, "mid": v(81.94, 152.7) * mm, "end": v(82.12, 152.89) * mm});
            skArc(sketch, "E1816", {"start": v(82.8, 152.2) * mm, "mid": v(82.9, 152.99) * mm, "end": v(82.12, 152.89) * mm});
            skArc(sketch, "E1817", {"start": v(82.8, 152.2) * mm, "mid": v(82.62, 152.02) * mm, "end": v(82.55, 151.77) * mm});
            skLineSegment(sketch, "E1818", {"start": v(82.55, 151.77) * mm, "end": v(82.55, 147.3) * mm});
            skArc(sketch, "E1819", {"start": v(82.55, 147.3) * mm, "mid": v(82.62, 147.05) * mm, "end": v(82.8, 146.87) * mm});
            skArc(sketch, "E1820", {"start": v(82.12, 146.19) * mm, "mid": v(82.9, 146.08) * mm, "end": v(82.8, 146.87) * mm});
            skArc(sketch, "E1821", {"start": v(82.12, 146.19) * mm, "mid": v(81.94, 146.37) * mm, "end": v(81.69, 146.44) * mm});
            skLineSegment(sketch, "E1822", {"start": v(81.69, 146.44) * mm, "end": v(80.12, 146.44) * mm});
            skArc(sketch, "E1823", {"start": v(31.08, 167.64) * mm, "mid": v(30.83, 167.57) * mm, "end": v(30.64, 167.39) * mm});
            skArc(sketch, "E1824", {"start": v(29.96, 168.07) * mm, "mid": v(29.86, 167.28) * mm, "end": v(30.64, 167.39) * mm});
            skArc(sketch, "E1825", {"start": v(29.96, 168.07) * mm, "mid": v(30.14, 168.25) * mm, "end": v(30.21, 168.5) * mm});
            skLineSegment(sketch, "E1826", {"start": v(30.21, 168.5) * mm, "end": v(30.21, 172.97) * mm});
            skArc(sketch, "E1827", {"start": v(30.21, 172.97) * mm, "mid": v(30.14, 173.22) * mm, "end": v(29.96, 173.4) * mm});
            skArc(sketch, "E1828", {"start": v(30.64, 174.09) * mm, "mid": v(29.86, 174.19) * mm, "end": v(29.96, 173.4) * mm});
            skArc(sketch, "E1829", {"start": v(30.64, 174.09) * mm, "mid": v(30.83, 173.9) * mm, "end": v(31.08, 173.84) * mm});
            skLineSegment(sketch, "E1830", {"start": v(31.08, 173.84) * mm, "end": v(32.65, 173.84) * mm});
            skArc(sketch, "E1831", {"start": v(32.65, 173.84) * mm, "mid": v(32.9, 173.9) * mm, "end": v(33.08, 174.09) * mm});
            skArc(sketch, "E1832", {"start": v(33.76, 173.4) * mm, "mid": v(33.86, 174.19) * mm, "end": v(33.08, 174.09) * mm});
            skArc(sketch, "E1833", {"start": v(33.76, 173.4) * mm, "mid": v(33.58, 173.22) * mm, "end": v(33.51, 172.97) * mm});
            skLineSegment(sketch, "E1834", {"start": v(33.51, 172.97) * mm, "end": v(33.51, 168.5) * mm});
            skArc(sketch, "E1835", {"start": v(33.51, 168.5) * mm, "mid": v(33.58, 168.25) * mm, "end": v(33.76, 168.07) * mm});
            skArc(sketch, "E1836", {"start": v(33.08, 167.39) * mm, "mid": v(33.86, 167.28) * mm, "end": v(33.76, 168.07) * mm});
            skArc(sketch, "E1837", {"start": v(33.08, 167.39) * mm, "mid": v(32.9, 167.57) * mm, "end": v(32.65, 167.64) * mm});
            skLineSegment(sketch, "E1838", {"start": v(32.65, 167.64) * mm, "end": v(31.08, 167.64) * mm});
            skArc(sketch, "E1839", {"start": v(31.08, 146.44) * mm, "mid": v(30.83, 146.37) * mm, "end": v(30.64, 146.19) * mm});
            skArc(sketch, "E1840", {"start": v(29.96, 146.87) * mm, "mid": v(29.86, 146.08) * mm, "end": v(30.64, 146.19) * mm});
            skArc(sketch, "E1841", {"start": v(29.96, 146.87) * mm, "mid": v(30.14, 147.05) * mm, "end": v(30.21, 147.3) * mm});
            skLineSegment(sketch, "E1842", {"start": v(30.21, 147.3) * mm, "end": v(30.21, 151.77) * mm});
            skArc(sketch, "E1843", {"start": v(30.21, 151.77) * mm, "mid": v(30.14, 152.02) * mm, "end": v(29.96, 152.2) * mm});
            skArc(sketch, "E1844", {"start": v(30.64, 152.89) * mm, "mid": v(29.86, 152.99) * mm, "end": v(29.96, 152.2) * mm});
            skArc(sketch, "E1845", {"start": v(30.64, 152.89) * mm, "mid": v(30.83, 152.7) * mm, "end": v(31.08, 152.64) * mm});
            skLineSegment(sketch, "E1846", {"start": v(31.08, 152.64) * mm, "end": v(32.65, 152.64) * mm});
            skArc(sketch, "E1847", {"start": v(32.65, 152.64) * mm, "mid": v(32.9, 152.7) * mm, "end": v(33.08, 152.89) * mm});
            skArc(sketch, "E1848", {"start": v(33.76, 152.2) * mm, "mid": v(33.86, 152.99) * mm, "end": v(33.08, 152.89) * mm});
            skArc(sketch, "E1849", {"start": v(33.76, 152.2) * mm, "mid": v(33.58, 152.02) * mm, "end": v(33.51, 151.77) * mm});
            skLineSegment(sketch, "E1850", {"start": v(33.51, 151.77) * mm, "end": v(33.51, 147.3) * mm});
            skArc(sketch, "E1851", {"start": v(33.51, 147.3) * mm, "mid": v(33.58, 147.05) * mm, "end": v(33.76, 146.87) * mm});
            skArc(sketch, "E1852", {"start": v(33.08, 146.19) * mm, "mid": v(33.86, 146.08) * mm, "end": v(33.76, 146.87) * mm});
            skArc(sketch, "E1853", {"start": v(33.08, 146.19) * mm, "mid": v(32.9, 146.37) * mm, "end": v(32.65, 146.44) * mm});
            skLineSegment(sketch, "E1854", {"start": v(32.65, 146.44) * mm, "end": v(31.08, 146.44) * mm});
            skCircle(sketch, "E1855", {"center": v(80.9, 160.14) * mm, "radius": 1.6 * mm});
            skCircle(sketch, "E1856", {"center": v(71.88, 171.34) * mm, "radius": 1.6 * mm});
            skCircle(sketch, "E1857", {"center": v(71.88, 140.34) * mm, "radius": 1.6 * mm});
            skCircle(sketch, "E1858", {"center": v(40.88, 171.34) * mm, "radius": 1.6 * mm});
            skCircle(sketch, "E1859", {"center": v(40.88, 140.34) * mm, "radius": 1.6 * mm});
            skCircle(sketch, "E1860", {"center": v(31.86, 160.14) * mm, "radius": 1.6 * mm});
            skLineSegment(sketch, "E1861", {"start": v(86.38, 127.33) * mm, "end": v(86.38, 82.33) * mm});
            skArc(sketch, "E1862", {"start": v(81.38, 77.33) * mm, "mid": v(84.92, 78.8) * mm, "end": v(86.38, 82.33) * mm});
            skLineSegment(sketch, "E1863", {"start": v(81.38, 77.33) * mm, "end": v(31.38, 77.33) * mm});
            skArc(sketch, "E1864", {"start": v(26.38, 82.33) * mm, "mid": v(27.85, 78.8) * mm, "end": v(31.38, 77.33) * mm});
            skLineSegment(sketch, "E1865", {"start": v(26.38, 82.33) * mm, "end": v(26.38, 127.33) * mm});
            skLineSegment(sketch, "E1866", {"start": v(26.38, 127.33) * mm, "end": v(41.92, 127.33) * mm});
            skArc(sketch, "E1867", {"start": v(42.35, 127.08) * mm, "mid": v(42.17, 127.26) * mm, "end": v(41.92, 127.33) * mm});
            skArc(sketch, "E1868", {"start": v(42.35, 127.08) * mm, "mid": v(43.13, 126.98) * mm, "end": v(43.03, 127.76) * mm});
            skArc(sketch, "E1869", {"start": v(42.78, 128.2) * mm, "mid": v(42.85, 127.95) * mm, "end": v(43.03, 127.76) * mm});
            skLineSegment(sketch, "E1870", {"start": v(42.78, 128.2) * mm, "end": v(42.78, 129.83) * mm});
            skArc(sketch, "E1871", {"start": v(43.28, 130.33) * mm, "mid": v(42.93, 130.18) * mm, "end": v(42.78, 129.83) * mm});
            skLineSegment(sketch, "E1872", {"start": v(43.28, 130.33) * mm, "end": v(48.28, 130.33) * mm});
            skArc(sketch, "E1873", {"start": v(48.78, 129.83) * mm, "mid": v(48.63, 130.18) * mm, "end": v(48.28, 130.33) * mm});
            skLineSegment(sketch, "E1874", {"start": v(48.78, 129.83) * mm, "end": v(48.78, 128.2) * mm});
            skArc(sketch, "E1875", {"start": v(48.53, 127.76) * mm, "mid": v(48.71, 127.94) * mm, "end": v(48.78, 128.2) * mm});
            skArc(sketch, "E1876", {"start": v(48.53, 127.76) * mm, "mid": v(48.43, 126.98) * mm, "end": v(49.21, 127.08) * mm});
            skArc(sketch, "E1877", {"start": v(49.65, 127.33) * mm, "mid": v(49.4, 127.26) * mm, "end": v(49.21, 127.08) * mm});
            skLineSegment(sketch, "E1878", {"start": v(49.65, 127.33) * mm, "end": v(54.78, 127.33) * mm});
            skLineSegment(sketch, "E1879", {"start": v(54.78, 127.33) * mm, "end": v(54.78, 124.33) * mm});
            skLineSegment(sketch, "E1880", {"start": v(54.78, 124.33) * mm, "end": v(53.5, 124.33) * mm});
            skLineSegment(sketch, "E1881", {"start": v(53.5, 124.33) * mm, "end": v(53.5, 120.33) * mm});
            skLineSegment(sketch, "E1882", {"start": v(53.5, 120.33) * mm, "end": v(54.78, 120.33) * mm});
            skLineSegment(sketch, "E1883", {"start": v(54.78, 120.33) * mm, "end": v(54.78, 117.33) * mm});
            skLineSegment(sketch, "E1884", {"start": v(54.78, 117.33) * mm, "end": v(57.98, 117.33) * mm});
            skLineSegment(sketch, "E1885", {"start": v(57.98, 117.33) * mm, "end": v(57.98, 120.33) * mm});
            skLineSegment(sketch, "E1886", {"start": v(57.98, 120.33) * mm, "end": v(59.26, 120.33) * mm});
            skLineSegment(sketch, "E1887", {"start": v(59.26, 120.33) * mm, "end": v(59.26, 124.33) * mm});
            skLineSegment(sketch, "E1888", {"start": v(59.26, 124.33) * mm, "end": v(57.98, 124.33) * mm});
            skLineSegment(sketch, "E1889", {"start": v(57.98, 124.33) * mm, "end": v(57.98, 127.33) * mm});
            skLineSegment(sketch, "E1890", {"start": v(57.98, 127.33) * mm, "end": v(63.12, 127.33) * mm});
            skArc(sketch, "E1891", {"start": v(63.55, 127.08) * mm, "mid": v(63.37, 127.26) * mm, "end": v(63.12, 127.33) * mm});
            skArc(sketch, "E1892", {"start": v(63.55, 127.08) * mm, "mid": v(64.33, 126.98) * mm, "end": v(64.23, 127.76) * mm});
            skArc(sketch, "E1893", {"start": v(63.98, 128.2) * mm, "mid": v(64.05, 127.95) * mm, "end": v(64.23, 127.76) * mm});
            skLineSegment(sketch, "E1894", {"start": v(63.98, 128.2) * mm, "end": v(63.98, 129.83) * mm});
            skArc(sketch, "E1895", {"start": v(64.48, 130.33) * mm, "mid": v(64.13, 130.18) * mm, "end": v(63.98, 129.83) * mm});
            skLineSegment(sketch, "E1896", {"start": v(64.48, 130.33) * mm, "end": v(69.48, 130.33) * mm});
            skArc(sketch, "E1897", {"start": v(69.98, 129.83) * mm, "mid": v(69.83, 130.18) * mm, "end": v(69.48, 130.33) * mm});
            skLineSegment(sketch, "E1898", {"start": v(69.98, 129.83) * mm, "end": v(69.98, 128.2) * mm});
            skArc(sketch, "E1899", {"start": v(69.73, 127.76) * mm, "mid": v(69.91, 127.94) * mm, "end": v(69.98, 128.2) * mm});
            skArc(sketch, "E1900", {"start": v(69.73, 127.76) * mm, "mid": v(69.63, 126.98) * mm, "end": v(70.41, 127.08) * mm});
            skArc(sketch, "E1901", {"start": v(70.85, 127.33) * mm, "mid": v(70.6, 127.26) * mm, "end": v(70.41, 127.08) * mm});
            skLineSegment(sketch, "E1902", {"start": v(70.85, 127.33) * mm, "end": v(86.38, 127.33) * mm});
            skCircle(sketch, "E1903", {"center": v(56.38, 98.03) * mm, "radius": 11.1 * mm});
            skCircle(sketch, "E1904", {"center": v(73.38, 98.03) * mm, "radius": 4 * mm});
            skArc(sketch, "E1905", {"start": v(80.12, 109.83) * mm, "mid": v(79.87, 109.76) * mm, "end": v(79.68, 109.58) * mm});
            skArc(sketch, "E1906", {"start": v(79, 110.26) * mm, "mid": v(78.9, 109.48) * mm, "end": v(79.68, 109.58) * mm});
            skArc(sketch, "E1907", {"start": v(79, 110.26) * mm, "mid": v(79.18, 110.45) * mm, "end": v(79.25, 110.7) * mm});
            skLineSegment(sketch, "E1908", {"start": v(79.25, 110.7) * mm, "end": v(79.25, 115.16) * mm});
            skArc(sketch, "E1909", {"start": v(79.25, 115.16) * mm, "mid": v(79.18, 115.41) * mm, "end": v(79, 115.6) * mm});
            skArc(sketch, "E1910", {"start": v(79.68, 116.28) * mm, "mid": v(78.9, 116.38) * mm, "end": v(79, 115.6) * mm});
            skArc(sketch, "E1911", {"start": v(79.68, 116.28) * mm, "mid": v(79.87, 116.1) * mm, "end": v(80.12, 116.03) * mm});
            skLineSegment(sketch, "E1912", {"start": v(80.12, 116.03) * mm, "end": v(81.69, 116.03) * mm});
            skArc(sketch, "E1913", {"start": v(81.69, 116.03) * mm, "mid": v(81.94, 116.1) * mm, "end": v(82.12, 116.28) * mm});
            skArc(sketch, "E1914", {"start": v(82.8, 115.6) * mm, "mid": v(82.9, 116.38) * mm, "end": v(82.12, 116.28) * mm});
            skArc(sketch, "E1915", {"start": v(82.8, 115.6) * mm, "mid": v(82.62, 115.41) * mm, "end": v(82.55, 115.16) * mm});
            skLineSegment(sketch, "E1916", {"start": v(82.55, 115.16) * mm, "end": v(82.55, 110.7) * mm});
            skArc(sketch, "E1917", {"start": v(82.55, 110.7) * mm, "mid": v(82.62, 110.45) * mm, "end": v(82.8, 110.26) * mm});
            skArc(sketch, "E1918", {"start": v(82.12, 109.58) * mm, "mid": v(82.9, 109.48) * mm, "end": v(82.8, 110.26) * mm});
            skArc(sketch, "E1919", {"start": v(82.12, 109.58) * mm, "mid": v(81.94, 109.76) * mm, "end": v(81.69, 109.83) * mm});
            skLineSegment(sketch, "E1920", {"start": v(81.69, 109.83) * mm, "end": v(80.12, 109.83) * mm});
            skArc(sketch, "E1921", {"start": v(80.12, 88.63) * mm, "mid": v(79.87, 88.56) * mm, "end": v(79.68, 88.38) * mm});
            skArc(sketch, "E1922", {"start": v(79, 89.06) * mm, "mid": v(78.9, 88.28) * mm, "end": v(79.68, 88.38) * mm});
            skArc(sketch, "E1923", {"start": v(79, 89.06) * mm, "mid": v(79.18, 89.25) * mm, "end": v(79.25, 89.5) * mm});
            skLineSegment(sketch, "E1924", {"start": v(79.25, 89.5) * mm, "end": v(79.25, 93.96) * mm});
            skArc(sketch, "E1925", {"start": v(79.25, 93.96) * mm, "mid": v(79.18, 94.21) * mm, "end": v(79, 94.4) * mm});
            skArc(sketch, "E1926", {"start": v(79.68, 95.08) * mm, "mid": v(78.9, 95.18) * mm, "end": v(79, 94.4) * mm});
            skArc(sketch, "E1927", {"start": v(79.68, 95.08) * mm, "mid": v(79.87, 94.9) * mm, "end": v(80.12, 94.83) * mm});
            skLineSegment(sketch, "E1928", {"start": v(80.12, 94.83) * mm, "end": v(81.69, 94.83) * mm});
            skArc(sketch, "E1929", {"start": v(81.69, 94.83) * mm, "mid": v(81.94, 94.9) * mm, "end": v(82.12, 95.08) * mm});
            skArc(sketch, "E1930", {"start": v(82.8, 94.4) * mm, "mid": v(82.9, 95.18) * mm, "end": v(82.12, 95.08) * mm});
            skArc(sketch, "E1931", {"start": v(82.8, 94.4) * mm, "mid": v(82.62, 94.21) * mm, "end": v(82.55, 93.96) * mm});
            skLineSegment(sketch, "E1932", {"start": v(82.55, 93.96) * mm, "end": v(82.55, 89.5) * mm});
            skArc(sketch, "E1933", {"start": v(82.55, 89.5) * mm, "mid": v(82.62, 89.25) * mm, "end": v(82.8, 89.06) * mm});
            skArc(sketch, "E1934", {"start": v(82.12, 88.38) * mm, "mid": v(82.9, 88.28) * mm, "end": v(82.8, 89.06) * mm});
            skArc(sketch, "E1935", {"start": v(82.12, 88.38) * mm, "mid": v(81.94, 88.56) * mm, "end": v(81.69, 88.63) * mm});
            skLineSegment(sketch, "E1936", {"start": v(81.69, 88.63) * mm, "end": v(80.12, 88.63) * mm});
            skArc(sketch, "E1937", {"start": v(31.08, 109.83) * mm, "mid": v(30.83, 109.76) * mm, "end": v(30.64, 109.58) * mm});
            skArc(sketch, "E1938", {"start": v(29.96, 110.26) * mm, "mid": v(29.86, 109.48) * mm, "end": v(30.64, 109.58) * mm});
            skArc(sketch, "E1939", {"start": v(29.96, 110.26) * mm, "mid": v(30.14, 110.45) * mm, "end": v(30.21, 110.7) * mm});
            skLineSegment(sketch, "E1940", {"start": v(30.21, 110.7) * mm, "end": v(30.21, 115.16) * mm});
            skArc(sketch, "E1941", {"start": v(30.21, 115.16) * mm, "mid": v(30.14, 115.41) * mm, "end": v(29.96, 115.6) * mm});
            skArc(sketch, "E1942", {"start": v(30.64, 116.28) * mm, "mid": v(29.86, 116.38) * mm, "end": v(29.96, 115.6) * mm});
            skArc(sketch, "E1943", {"start": v(30.64, 116.28) * mm, "mid": v(30.83, 116.1) * mm, "end": v(31.08, 116.03) * mm});
            skLineSegment(sketch, "E1944", {"start": v(31.08, 116.03) * mm, "end": v(32.65, 116.03) * mm});
            skArc(sketch, "E1945", {"start": v(32.65, 116.03) * mm, "mid": v(32.9, 116.1) * mm, "end": v(33.08, 116.28) * mm});
            skArc(sketch, "E1946", {"start": v(33.76, 115.6) * mm, "mid": v(33.86, 116.38) * mm, "end": v(33.08, 116.28) * mm});
            skArc(sketch, "E1947", {"start": v(33.76, 115.6) * mm, "mid": v(33.58, 115.41) * mm, "end": v(33.51, 115.16) * mm});
            skLineSegment(sketch, "E1948", {"start": v(33.51, 115.16) * mm, "end": v(33.51, 110.7) * mm});
            skArc(sketch, "E1949", {"start": v(33.51, 110.7) * mm, "mid": v(33.58, 110.45) * mm, "end": v(33.76, 110.26) * mm});
            skArc(sketch, "E1950", {"start": v(33.08, 109.58) * mm, "mid": v(33.86, 109.48) * mm, "end": v(33.76, 110.26) * mm});
            skArc(sketch, "E1951", {"start": v(33.08, 109.58) * mm, "mid": v(32.9, 109.76) * mm, "end": v(32.65, 109.83) * mm});
            skLineSegment(sketch, "E1952", {"start": v(32.65, 109.83) * mm, "end": v(31.08, 109.83) * mm});
            skArc(sketch, "E1953", {"start": v(31.08, 88.63) * mm, "mid": v(30.83, 88.56) * mm, "end": v(30.64, 88.38) * mm});
            skArc(sketch, "E1954", {"start": v(29.96, 89.06) * mm, "mid": v(29.86, 88.28) * mm, "end": v(30.64, 88.38) * mm});
            skArc(sketch, "E1955", {"start": v(29.96, 89.06) * mm, "mid": v(30.14, 89.25) * mm, "end": v(30.21, 89.5) * mm});
            skLineSegment(sketch, "E1956", {"start": v(30.21, 89.5) * mm, "end": v(30.21, 93.96) * mm});
            skArc(sketch, "E1957", {"start": v(30.21, 93.96) * mm, "mid": v(30.14, 94.21) * mm, "end": v(29.96, 94.4) * mm});
            skArc(sketch, "E1958", {"start": v(30.64, 95.08) * mm, "mid": v(29.86, 95.18) * mm, "end": v(29.96, 94.4) * mm});
            skArc(sketch, "E1959", {"start": v(30.64, 95.08) * mm, "mid": v(30.83, 94.9) * mm, "end": v(31.08, 94.83) * mm});
            skLineSegment(sketch, "E1960", {"start": v(31.08, 94.83) * mm, "end": v(32.65, 94.83) * mm});
            skArc(sketch, "E1961", {"start": v(32.65, 94.83) * mm, "mid": v(32.9, 94.9) * mm, "end": v(33.08, 95.08) * mm});
            skArc(sketch, "E1962", {"start": v(33.76, 94.4) * mm, "mid": v(33.86, 95.18) * mm, "end": v(33.08, 95.08) * mm});
            skArc(sketch, "E1963", {"start": v(33.76, 94.4) * mm, "mid": v(33.58, 94.21) * mm, "end": v(33.51, 93.96) * mm});
            skLineSegment(sketch, "E1964", {"start": v(33.51, 93.96) * mm, "end": v(33.51, 89.5) * mm});
            skArc(sketch, "E1965", {"start": v(33.51, 89.5) * mm, "mid": v(33.58, 89.25) * mm, "end": v(33.76, 89.06) * mm});
            skArc(sketch, "E1966", {"start": v(33.08, 88.38) * mm, "mid": v(33.86, 88.28) * mm, "end": v(33.76, 89.06) * mm});
            skArc(sketch, "E1967", {"start": v(33.08, 88.38) * mm, "mid": v(32.9, 88.56) * mm, "end": v(32.65, 88.63) * mm});
            skLineSegment(sketch, "E1968", {"start": v(32.65, 88.63) * mm, "end": v(31.08, 88.63) * mm});
            skCircle(sketch, "E1969", {"center": v(80.9, 102.33) * mm, "radius": 1.6 * mm});
            skCircle(sketch, "E1970", {"center": v(71.88, 113.53) * mm, "radius": 1.6 * mm});
            skCircle(sketch, "E1971", {"center": v(71.88, 82.53) * mm, "radius": 1.6 * mm});
            skCircle(sketch, "E1972", {"center": v(40.88, 113.53) * mm, "radius": 1.6 * mm});
            skCircle(sketch, "E1973", {"center": v(40.88, 82.53) * mm, "radius": 1.6 * mm});
            skCircle(sketch, "E1974", {"center": v(31.86, 102.33) * mm, "radius": 1.6 * mm});
            skArc(sketch, "E1975", {"start": v(-224.23, 303.9) * mm, "mid": v(-230.42, 299.57) * mm, "end": v(-232.8, 292.4) * mm});
            skLineSegment(sketch, "E1976", {"start": v(-232.8, 292.4) * mm, "end": v(-232.8, 289.16) * mm});
            skLineSegment(sketch, "E1977", {"start": v(-232.8, 289.16) * mm, "end": v(-223.66, 289.16) * mm});
            skArc(sketch, "E1978", {"start": v(-223.66, 289.16) * mm, "mid": v(-223.4, 289.23) * mm, "end": v(-223.23, 289.41) * mm});
            skArc(sketch, "E1979", {"start": v(-222.54, 288.73) * mm, "mid": v(-222.44, 289.52) * mm, "end": v(-223.23, 289.41) * mm});
            skArc(sketch, "E1980", {"start": v(-222.54, 288.73) * mm, "mid": v(-222.73, 288.55) * mm, "end": v(-222.8, 288.3) * mm});
            skLineSegment(sketch, "E1981", {"start": v(-222.8, 288.3) * mm, "end": v(-222.8, 286.73) * mm});
            skArc(sketch, "E1982", {"start": v(-222.8, 286.73) * mm, "mid": v(-222.73, 286.48) * mm, "end": v(-222.54, 286.3) * mm});
            skArc(sketch, "E1983", {"start": v(-223.23, 285.61) * mm, "mid": v(-222.44, 285.5) * mm, "end": v(-222.54, 286.3) * mm});
            skArc(sketch, "E1984", {"start": v(-223.23, 285.61) * mm, "mid": v(-223.4, 285.8) * mm, "end": v(-223.66, 285.86) * mm});
            skLineSegment(sketch, "E1985", {"start": v(-223.66, 285.86) * mm, "end": v(-232.8, 285.86) * mm});
            skLineSegment(sketch, "E1986", {"start": v(-232.8, 285.86) * mm, "end": v(-232.8, 255.34) * mm});
            skArc(sketch, "E1987", {"start": v(-232.8, 255.34) * mm, "mid": v(-229.28, 246.85) * mm, "end": v(-220.8, 243.34) * mm});
            skLineSegment(sketch, "E1988", {"start": v(-220.8, 243.34) * mm, "end": v(-199.19, 243.34) * mm});
            skArc(sketch, "E1989", {"start": v(-199.19, 243.34) * mm, "mid": v(-192.9, 245.12) * mm, "end": v(-188.47, 249.94) * mm});
            skCircle(sketch, "E1990", {"center": v(-203.1, 256.7) * mm, "radius": 5 * mm});
            skCircle(sketch, "E1991", {"center": v(-220.1, 256.71) * mm, "radius": 4 * mm});
            skCircle(sketch, "E1992", {"center": v(-196.97, 287.51) * mm, "radius": 1.6 * mm});
            skLineSegment(sketch, "E1993", {"start": v(-156.32, 289.2) * mm, "end": v(-144.8, 289.2) * mm});
            skLineSegment(sketch, "E1994", {"start": v(-144.8, 289.2) * mm, "end": v(-144.8, 298.67) * mm});
            skArc(sketch, "E1995", {"start": v(-144.8, 298.67) * mm, "mid": v(-145.08, 301.27) * mm, "end": v(-145.92, 303.75) * mm});
            skLineSegment(sketch, "E1996", {"start": v(-145.92, 303.75) * mm, "end": v(-156.32, 320.2) * mm});
            skLineSegment(sketch, "E1997", {"start": v(-156.32, 320.2) * mm, "end": v(-159.41, 320.2) * mm});
            skLineSegment(sketch, "E1998", {"start": v(-171.14, 285.85) * mm, "end": v(-171.14, 288.34) * mm});
            skArc(sketch, "E1999", {"start": v(-171.14, 288.34) * mm, "mid": v(-171.21, 288.6) * mm, "end": v(-171.4, 288.77) * mm});
            skArc(sketch, "E2000", {"start": v(-170.71, 289.46) * mm, "mid": v(-171.5, 289.56) * mm, "end": v(-171.4, 288.77) * mm});
            skArc(sketch, "E2001", {"start": v(-170.71, 289.46) * mm, "mid": v(-170.53, 289.27) * mm, "end": v(-170.28, 289.2) * mm});
            skLineSegment(sketch, "E2002", {"start": v(-170.28, 289.2) * mm, "end": v(-159.62, 289.2) * mm});
            skLineSegment(sketch, "E2003", {"start": v(-159.62, 289.2) * mm, "end": v(-159.62, 299) * mm});
            skArc(sketch, "E2004", {"start": v(-159.62, 299) * mm, "mid": v(-159.68, 299.24) * mm, "end": v(-159.87, 299.42) * mm});
            skArc(sketch, "E2005", {"start": v(-159.18, 300.1) * mm, "mid": v(-159.97, 300.21) * mm, "end": v(-159.87, 299.42) * mm});
            skArc(sketch, "E2006", {"start": v(-159.18, 300.1) * mm, "mid": v(-159, 299.92) * mm, "end": v(-158.75, 299.86) * mm});
            skLineSegment(sketch, "E2007", {"start": v(-158.75, 299.86) * mm, "end": v(-157.18, 299.86) * mm});
            skArc(sketch, "E2008", {"start": v(-157.18, 299.86) * mm, "mid": v(-156.93, 299.92) * mm, "end": v(-156.75, 300.1) * mm});
            skArc(sketch, "E2009", {"start": v(-156.07, 299.42) * mm, "mid": v(-155.96, 300.2) * mm, "end": v(-156.75, 300.1) * mm});
            skArc(sketch, "E2010", {"start": v(-156.07, 299.42) * mm, "mid": v(-156.25, 299.24) * mm, "end": v(-156.32, 298.99) * mm});
            skLineSegment(sketch, "E2011", {"start": v(-156.32, 298.99) * mm, "end": v(-156.32, 289.2) * mm});
            skCircle(sketch, "E2012", {"center": v(-157.97, 309.86) * mm, "radius": 1.6 * mm});
            skLineSegment(sketch, "E2013", {"start": v(-159.41, 320.2) * mm, "end": v(-224.23, 303.9) * mm});
            skLineSegment(sketch, "E2014", {"start": v(-188.47, 249.94) * mm, "end": v(-171.14, 285.85) * mm});
            skArc(sketch, "E2015", {"start": v(73.38, -42.24) * mm, "mid": v(79.57, -37.9) * mm, "end": v(81.94, -30.74) * mm});
            skLineSegment(sketch, "E2016", {"start": v(81.94, -30.74) * mm, "end": v(81.94, -27.5) * mm});
            skLineSegment(sketch, "E2017", {"start": v(81.94, -27.5) * mm, "end": v(72.81, -27.5) * mm});
            skArc(sketch, "E2018", {"start": v(72.81, -27.5) * mm, "mid": v(72.56, -27.57) * mm, "end": v(72.38, -27.75) * mm});
            skArc(sketch, "E2019", {"start": v(71.7, -27.07) * mm, "mid": v(71.6, -27.85) * mm, "end": v(72.38, -27.75) * mm});
            skArc(sketch, "E2020", {"start": v(71.7, -27.07) * mm, "mid": v(71.88, -26.88) * mm, "end": v(71.94, -26.63) * mm});
            skLineSegment(sketch, "E2021", {"start": v(71.94, -26.63) * mm, "end": v(71.94, -25.07) * mm});
            skArc(sketch, "E2022", {"start": v(71.94, -25.07) * mm, "mid": v(71.88, -24.82) * mm, "end": v(71.7, -24.63) * mm});
            skArc(sketch, "E2023", {"start": v(72.38, -23.95) * mm, "mid": v(71.6, -23.85) * mm, "end": v(71.7, -24.63) * mm});
            skArc(sketch, "E2024", {"start": v(72.38, -23.95) * mm, "mid": v(72.56, -24.13) * mm, "end": v(72.81, -24.2) * mm});
            skLineSegment(sketch, "E2025", {"start": v(72.81, -24.2) * mm, "end": v(81.94, -24.2) * mm});
            skLineSegment(sketch, "E2026", {"start": v(81.94, -24.2) * mm, "end": v(81.95, 6.32) * mm});
            skArc(sketch, "E2027", {"start": v(81.95, 6.32) * mm, "mid": v(78.43, 14.8) * mm, "end": v(69.95, 18.32) * mm});
            skLineSegment(sketch, "E2028", {"start": v(69.95, 18.32) * mm, "end": v(48.34, 18.32) * mm});
            skArc(sketch, "E2029", {"start": v(48.34, 18.32) * mm, "mid": v(42.04, 16.54) * mm, "end": v(37.62, 11.72) * mm});
            skCircle(sketch, "E2030", {"center": v(52.24, 4.95) * mm, "radius": 5 * mm});
            skCircle(sketch, "E2031", {"center": v(69.24, 4.95) * mm, "radius": 4 * mm});
            skCircle(sketch, "E2032", {"center": v(46.12, -25.85) * mm, "radius": 1.6 * mm});
            skLineSegment(sketch, "E2033", {"start": v(5.47, -27.55) * mm, "end": v(-6.06, -27.54) * mm});
            skLineSegment(sketch, "E2034", {"start": v(-6.06, -27.54) * mm, "end": v(-6.06, -37.01) * mm});
            skArc(sketch, "E2035", {"start": v(-6.06, -37.01) * mm, "mid": v(-5.77, -39.61) * mm, "end": v(-4.93, -42.09) * mm});
            skLineSegment(sketch, "E2036", {"start": v(-4.93, -42.09) * mm, "end": v(5.47, -58.55) * mm});
            skLineSegment(sketch, "E2037", {"start": v(5.47, -58.55) * mm, "end": v(8.56, -58.55) * mm});
            skLineSegment(sketch, "E2038", {"start": v(20.3, -24.19) * mm, "end": v(20.3, -26.68) * mm});
            skArc(sketch, "E2039", {"start": v(20.3, -26.68) * mm, "mid": v(20.36, -26.93) * mm, "end": v(20.55, -27.11) * mm});
            skArc(sketch, "E2040", {"start": v(19.86, -27.8) * mm, "mid": v(20.65, -27.9) * mm, "end": v(20.55, -27.11) * mm});
            skArc(sketch, "E2041", {"start": v(19.86, -27.8) * mm, "mid": v(19.68, -27.61) * mm, "end": v(19.43, -27.55) * mm});
            skLineSegment(sketch, "E2042", {"start": v(19.43, -27.55) * mm, "end": v(8.77, -27.55) * mm});
            skLineSegment(sketch, "E2043", {"start": v(8.77, -27.55) * mm, "end": v(8.77, -37.33) * mm});
            skArc(sketch, "E2044", {"start": v(8.77, -37.33) * mm, "mid": v(8.84, -37.58) * mm, "end": v(9.02, -37.76) * mm});
            skArc(sketch, "E2045", {"start": v(8.34, -38.44) * mm, "mid": v(9.12, -38.55) * mm, "end": v(9.02, -37.76) * mm});
            skArc(sketch, "E2046", {"start": v(8.34, -38.44) * mm, "mid": v(8.15, -38.26) * mm, "end": v(7.9, -38.2) * mm});
            skLineSegment(sketch, "E2047", {"start": v(7.9, -38.2) * mm, "end": v(6.34, -38.2) * mm});
            skArc(sketch, "E2048", {"start": v(6.34, -38.2) * mm, "mid": v(6.09, -38.26) * mm, "end": v(5.9, -38.44) * mm});
            skArc(sketch, "E2049", {"start": v(5.22, -37.76) * mm, "mid": v(5.12, -38.55) * mm, "end": v(5.9, -38.44) * mm});
            skArc(sketch, "E2050", {"start": v(5.22, -37.76) * mm, "mid": v(5.4, -37.58) * mm, "end": v(5.47, -37.33) * mm});
            skLineSegment(sketch, "E2051", {"start": v(5.47, -37.33) * mm, "end": v(5.47, -27.55) * mm});
            skCircle(sketch, "E2052", {"center": v(7.12, -48.2) * mm, "radius": 1.6 * mm});
            skLineSegment(sketch, "E2053", {"start": v(8.56, -58.55) * mm, "end": v(73.38, -42.24) * mm});
            skLineSegment(sketch, "E2054", {"start": v(37.62, 11.72) * mm, "end": v(20.3, -24.19) * mm});
            skLineSegment(sketch, "E2055", {"start": v(269.2, 23.31) * mm, "end": v(254.72, 37.8) * mm});
            skArc(sketch, "E2056", {"start": v(254.72, 37.8) * mm, "mid": v(252.77, 39.1) * mm, "end": v(250.47, 39.56) * mm});
            skLineSegment(sketch, "E2057", {"start": v(250.47, 39.56) * mm, "end": v(235.44, 39.56) * mm});
            skArc(sketch, "E2058", {"start": v(235.44, 39.56) * mm, "mid": v(233.15, 39.1) * mm, "end": v(231.2, 37.8) * mm});
            skLineSegment(sketch, "E2059", {"start": v(231.2, 37.8) * mm, "end": v(214.96, 21.56) * mm});
            skArc(sketch, "E2060", {"start": v(207.96, 28.56) * mm, "mid": v(207.96, 21.56) * mm, "end": v(214.96, 21.56) * mm});
            skLineSegment(sketch, "E2061", {"start": v(207.96, 28.56) * mm, "end": v(229.2, 49.8) * mm});
            skArc(sketch, "E2062", {"start": v(229.2, 49.8) * mm, "mid": v(230.5, 51.75) * mm, "end": v(230.96, 54.04) * mm});
            skLineSegment(sketch, "E2063", {"start": v(230.96, 54.04) * mm, "end": v(230.96, 205.07) * mm});
            skArc(sketch, "E2064", {"start": v(230.96, 205.07) * mm, "mid": v(230.5, 207.37) * mm, "end": v(229.2, 209.31) * mm});
            skLineSegment(sketch, "E2065", {"start": v(229.2, 209.31) * mm, "end": v(207.96, 230.56) * mm});
            skArc(sketch, "E2066", {"start": v(214.96, 237.56) * mm, "mid": v(207.96, 237.56) * mm, "end": v(207.96, 230.56) * mm});
            skLineSegment(sketch, "E2067", {"start": v(214.96, 237.56) * mm, "end": v(231.2, 221.31) * mm});
            skLineSegment(sketch, "E2068", {"start": v(400.72, 221.31) * mm, "end": v(416.96, 237.56) * mm});
            skArc(sketch, "E2069", {"start": v(423.96, 230.56) * mm, "mid": v(423.96, 237.56) * mm, "end": v(416.96, 237.56) * mm});
            skLineSegment(sketch, "E2070", {"start": v(423.96, 230.56) * mm, "end": v(402.72, 209.31) * mm});
            skArc(sketch, "E2071", {"start": v(402.72, 209.31) * mm, "mid": v(401.42, 207.37) * mm, "end": v(400.96, 205.07) * mm});
            skLineSegment(sketch, "E2072", {"start": v(400.96, 205.07) * mm, "end": v(400.96, 144.5) * mm});
            skArc(sketch, "E2073", {"start": v(400.96, 54.04) * mm, "mid": v(401.42, 51.75) * mm, "end": v(402.72, 49.8) * mm});
            skLineSegment(sketch, "E2074", {"start": v(402.72, 49.8) * mm, "end": v(423.96, 28.56) * mm});
            skArc(sketch, "E2075", {"start": v(416.96, 21.56) * mm, "mid": v(423.96, 21.56) * mm, "end": v(423.96, 28.56) * mm});
            skLineSegment(sketch, "E2076", {"start": v(416.96, 21.56) * mm, "end": v(400.72, 37.8) * mm});
            skArc(sketch, "E2077", {"start": v(400.72, 37.8) * mm, "mid": v(398.77, 39.1) * mm, "end": v(396.47, 39.56) * mm});
            skLineSegment(sketch, "E2078", {"start": v(396.47, 39.56) * mm, "end": v(381.44, 39.56) * mm});
            skArc(sketch, "E2079", {"start": v(381.44, 39.56) * mm, "mid": v(379.15, 39.1) * mm, "end": v(377.2, 37.8) * mm});
            skLineSegment(sketch, "E2080", {"start": v(377.2, 37.8) * mm, "end": v(362.72, 23.31) * mm});
            skArc(sketch, "E2081", {"start": v(358.47, 21.56) * mm, "mid": v(360.77, 22.01) * mm, "end": v(362.72, 23.31) * mm});
            skLineSegment(sketch, "E2082", {"start": v(358.47, 21.56) * mm, "end": v(341.44, 21.56) * mm});
            skArc(sketch, "E2083", {"start": v(337.2, 23.31) * mm, "mid": v(339.15, 22.01) * mm, "end": v(341.44, 21.56) * mm});
            skLineSegment(sketch, "E2084", {"start": v(337.2, 23.31) * mm, "end": v(322.72, 37.8) * mm});
            skArc(sketch, "E2085", {"start": v(322.72, 37.8) * mm, "mid": v(320.77, 39.1) * mm, "end": v(318.47, 39.56) * mm});
            skLineSegment(sketch, "E2086", {"start": v(318.47, 39.56) * mm, "end": v(313.44, 39.56) * mm});
            skArc(sketch, "E2087", {"start": v(313.44, 39.56) * mm, "mid": v(311.15, 39.1) * mm, "end": v(309.2, 37.8) * mm});
            skLineSegment(sketch, "E2088", {"start": v(309.2, 37.8) * mm, "end": v(294.72, 23.31) * mm});
            skArc(sketch, "E2089", {"start": v(290.47, 21.56) * mm, "mid": v(292.77, 22.01) * mm, "end": v(294.72, 23.31) * mm});
            skLineSegment(sketch, "E2090", {"start": v(290.47, 21.56) * mm, "end": v(273.44, 21.56) * mm});
            skArc(sketch, "E2091", {"start": v(269.2, 23.31) * mm, "mid": v(271.15, 22.01) * mm, "end": v(273.44, 21.56) * mm});
            skLineSegment(sketch, "E2092", {"start": v(348.9, 162.3) * mm, "end": v(379.7, 193.1) * mm});
            skArc(sketch, "E2093", {"start": v(390.96, 188.42) * mm, "mid": v(386.89, 194.52) * mm, "end": v(379.7, 193.1) * mm});
            skLineSegment(sketch, "E2094", {"start": v(390.96, 188.42) * mm, "end": v(390.96, 70.7) * mm});
            skArc(sketch, "E2095", {"start": v(379.7, 66.02) * mm, "mid": v(386.89, 64.6) * mm, "end": v(390.96, 70.7) * mm});
            skLineSegment(sketch, "E2096", {"start": v(379.7, 66.02) * mm, "end": v(348.9, 96.82) * mm});
            skArc(sketch, "E2097", {"start": v(346.96, 101.5) * mm, "mid": v(347.46, 98.97) * mm, "end": v(348.9, 96.82) * mm});
            skLineSegment(sketch, "E2098", {"start": v(346.96, 101.5) * mm, "end": v(346.96, 157.62) * mm});
            skArc(sketch, "E2099", {"start": v(348.9, 162.3) * mm, "mid": v(347.46, 160.15) * mm, "end": v(346.96, 157.62) * mm});
            skLineSegment(sketch, "E2100", {"start": v(309.2, 51.31) * mm, "end": v(292.72, 67.8) * mm});
            skArc(sketch, "E2101", {"start": v(290.96, 72.04) * mm, "mid": v(291.42, 69.75) * mm, "end": v(292.72, 67.8) * mm});
            skLineSegment(sketch, "E2102", {"start": v(290.96, 72.04) * mm, "end": v(290.96, 87.07) * mm});
            skArc(sketch, "E2103", {"start": v(292.72, 91.31) * mm, "mid": v(291.42, 89.37) * mm, "end": v(290.96, 87.07) * mm});
            skLineSegment(sketch, "E2104", {"start": v(292.72, 91.31) * mm, "end": v(309.2, 107.8) * mm});
            skArc(sketch, "E2105", {"start": v(313.44, 109.56) * mm, "mid": v(311.15, 109.1) * mm, "end": v(309.2, 107.8) * mm});
            skLineSegment(sketch, "E2106", {"start": v(313.44, 109.56) * mm, "end": v(318.47, 109.56) * mm});
            skArc(sketch, "E2107", {"start": v(322.72, 107.8) * mm, "mid": v(320.77, 109.1) * mm, "end": v(318.47, 109.56) * mm});
            skLineSegment(sketch, "E2108", {"start": v(322.72, 107.8) * mm, "end": v(339.2, 91.31) * mm});
            skArc(sketch, "E2109", {"start": v(340.96, 87.07) * mm, "mid": v(340.5, 89.37) * mm, "end": v(339.2, 91.31) * mm});
            skLineSegment(sketch, "E2110", {"start": v(340.96, 87.07) * mm, "end": v(340.96, 72.04) * mm});
            skArc(sketch, "E2111", {"start": v(339.2, 67.8) * mm, "mid": v(340.5, 69.75) * mm, "end": v(340.96, 72.04) * mm});
            skLineSegment(sketch, "E2112", {"start": v(339.2, 67.8) * mm, "end": v(322.72, 51.31) * mm});
            skArc(sketch, "E2113", {"start": v(318.47, 49.56) * mm, "mid": v(320.77, 50.01) * mm, "end": v(322.72, 51.31) * mm});
            skLineSegment(sketch, "E2114", {"start": v(318.47, 49.56) * mm, "end": v(313.44, 49.56) * mm});
            skArc(sketch, "E2115", {"start": v(309.2, 51.31) * mm, "mid": v(311.15, 50.01) * mm, "end": v(313.44, 49.56) * mm});
            skLineSegment(sketch, "E2116", {"start": v(339.2, 167.8) * mm, "end": v(322.72, 151.31) * mm});
            skArc(sketch, "E2117", {"start": v(318.47, 149.56) * mm, "mid": v(320.77, 150.01) * mm, "end": v(322.72, 151.31) * mm});
            skLineSegment(sketch, "E2118", {"start": v(318.47, 149.56) * mm, "end": v(313.44, 149.56) * mm});
            skArc(sketch, "E2119", {"start": v(309.2, 151.31) * mm, "mid": v(311.15, 150.01) * mm, "end": v(313.44, 149.56) * mm});
            skLineSegment(sketch, "E2120", {"start": v(309.2, 151.31) * mm, "end": v(292.72, 167.8) * mm});
            skArc(sketch, "E2121", {"start": v(290.96, 172.04) * mm, "mid": v(291.42, 169.75) * mm, "end": v(292.72, 167.8) * mm});
            skArc(sketch, "E2122", {"start": v(339.2, 167.8) * mm, "mid": v(340.5, 169.75) * mm, "end": v(340.96, 172.04) * mm});
            skLineSegment(sketch, "E2123", {"start": v(363, 40.92) * mm, "end": v(363, 48.2) * mm});
            skLineSegment(sketch, "E2124", {"start": v(269.78, 40.06) * mm, "end": v(292.14, 40.06) * mm});
            skArc(sketch, "E2125", {"start": v(292.58, 39.8) * mm, "mid": v(292.4, 40) * mm, "end": v(292.14, 40.06) * mm});
            skArc(sketch, "E2126", {"start": v(292.58, 39.8) * mm, "mid": v(293.36, 39.7) * mm, "end": v(293.26, 40.5) * mm});
            skArc(sketch, "E2127", {"start": v(293, 40.92) * mm, "mid": v(293.08, 40.67) * mm, "end": v(293.26, 40.5) * mm});
            skLineSegment(sketch, "E2128", {"start": v(293, 40.92) * mm, "end": v(293, 48.2) * mm});
            skArc(sketch, "E2129", {"start": v(293.26, 48.62) * mm, "mid": v(293.08, 48.44) * mm, "end": v(293, 48.2) * mm});
            skArc(sketch, "E2130", {"start": v(293.26, 48.62) * mm, "mid": v(293.36, 49.41) * mm, "end": v(292.58, 49.3) * mm});
            skArc(sketch, "E2131", {"start": v(292.14, 49.06) * mm, "mid": v(292.4, 49.12) * mm, "end": v(292.58, 49.3) * mm});
            skLineSegment(sketch, "E2132", {"start": v(292.14, 49.06) * mm, "end": v(269.78, 49.06) * mm});
            skArc(sketch, "E2133", {"start": v(269.34, 49.3) * mm, "mid": v(269.53, 49.12) * mm, "end": v(269.78, 49.06) * mm});
            skArc(sketch, "E2134", {"start": v(269.34, 49.3) * mm, "mid": v(268.56, 49.41) * mm, "end": v(268.66, 48.62) * mm});
            skArc(sketch, "E2135", {"start": v(268.9, 48.2) * mm, "mid": v(268.84, 48.44) * mm, "end": v(268.66, 48.62) * mm});
            skLineSegment(sketch, "E2136", {"start": v(268.9, 48.2) * mm, "end": v(268.9, 40.92) * mm});
            skArc(sketch, "E2137", {"start": v(268.66, 40.5) * mm, "mid": v(268.84, 40.67) * mm, "end": v(268.9, 40.92) * mm});
            skArc(sketch, "E2138", {"start": v(268.66, 40.5) * mm, "mid": v(268.56, 39.7) * mm, "end": v(269.34, 39.8) * mm});
            skArc(sketch, "E2139", {"start": v(269.78, 40.06) * mm, "mid": v(269.53, 40) * mm, "end": v(269.34, 39.8) * mm});
            skCircle(sketch, "E2140", {"center": v(420.46, 25.06) * mm, "radius": 1.6 * mm});
            skCircle(sketch, "E2141", {"center": v(211.46, 25.06) * mm, "radius": 1.6 * mm});
            skCircle(sketch, "E2142", {"center": v(350.96, 29.56) * mm, "radius": 1.6 * mm});
            skCircle(sketch, "E2143", {"center": v(280.96, 29.56) * mm, "radius": 1.6 * mm});
            skCircle(sketch, "E2144", {"center": v(350.96, 59.56) * mm, "radius": 1.6 * mm});
            skCircle(sketch, "E2145", {"center": v(280.96, 59.56) * mm, "radius": 1.6 * mm});
            skCircle(sketch, "E2146", {"center": v(333.46, 117.56) * mm, "radius": 1.6 * mm});
            skCircle(sketch, "E2147", {"center": v(298.46, 129.56) * mm, "radius": 1.6 * mm});
            skCircle(sketch, "E2148", {"center": v(333.46, 141.56) * mm, "radius": 1.6 * mm});
            skCircle(sketch, "E2149", {"center": v(420.46, 234.06) * mm, "radius": 1.6 * mm});
            skCircle(sketch, "E2150", {"center": v(211.46, 234.06) * mm, "radius": 1.6 * mm});
            skLineSegment(sketch, "E2151", {"start": v(339.78, 40.06) * mm, "end": v(362.14, 40.06) * mm});
            skArc(sketch, "E2152", {"start": v(362.58, 39.8) * mm, "mid": v(362.4, 40) * mm, "end": v(362.14, 40.06) * mm});
            skArc(sketch, "E2153", {"start": v(362.58, 39.8) * mm, "mid": v(363.36, 39.7) * mm, "end": v(363.26, 40.5) * mm});
            skArc(sketch, "E2154", {"start": v(363, 40.92) * mm, "mid": v(363.08, 40.67) * mm, "end": v(363.26, 40.5) * mm});
            skArc(sketch, "E2155", {"start": v(363.26, 48.62) * mm, "mid": v(363.08, 48.44) * mm, "end": v(363, 48.2) * mm});
            skArc(sketch, "E2156", {"start": v(363.26, 48.62) * mm, "mid": v(363.36, 49.41) * mm, "end": v(362.58, 49.3) * mm});
            skArc(sketch, "E2157", {"start": v(362.14, 49.06) * mm, "mid": v(362.4, 49.12) * mm, "end": v(362.58, 49.3) * mm});
            skLineSegment(sketch, "E2158", {"start": v(362.14, 49.06) * mm, "end": v(339.78, 49.06) * mm});
            skArc(sketch, "E2159", {"start": v(339.34, 49.3) * mm, "mid": v(339.53, 49.12) * mm, "end": v(339.78, 49.06) * mm});
            skArc(sketch, "E2160", {"start": v(339.34, 49.3) * mm, "mid": v(338.56, 49.41) * mm, "end": v(338.66, 48.62) * mm});
            skArc(sketch, "E2161", {"start": v(338.9, 48.2) * mm, "mid": v(338.84, 48.44) * mm, "end": v(338.66, 48.62) * mm});
            skLineSegment(sketch, "E2162", {"start": v(338.9, 48.2) * mm, "end": v(338.9, 40.92) * mm});
            skArc(sketch, "E2163", {"start": v(338.66, 40.5) * mm, "mid": v(338.84, 40.67) * mm, "end": v(338.9, 40.92) * mm});
            skArc(sketch, "E2164", {"start": v(338.66, 40.5) * mm, "mid": v(338.56, 39.7) * mm, "end": v(339.34, 39.8) * mm});
            skArc(sketch, "E2165", {"start": v(339.78, 40.06) * mm, "mid": v(339.53, 40) * mm, "end": v(339.34, 39.8) * mm});
            skLineSegment(sketch, "E2166", {"start": v(281.39, 104.52) * mm, "end": v(274.24, 97.38) * mm});
            skArc(sketch, "E2167", {"start": v(273.76, 97.25) * mm, "mid": v(274.02, 97.25) * mm, "end": v(274.24, 97.38) * mm});
            skArc(sketch, "E2168", {"start": v(273.76, 97.25) * mm, "mid": v(273.13, 96.77) * mm, "end": v(273.76, 96.28) * mm});
            skArc(sketch, "E2169", {"start": v(274.24, 96.15) * mm, "mid": v(274.02, 96.28) * mm, "end": v(273.76, 96.28) * mm});
            skLineSegment(sketch, "E2170", {"start": v(274.24, 96.15) * mm, "end": v(275.4, 95) * mm});
            skArc(sketch, "E2171", {"start": v(275.4, 94.3) * mm, "mid": v(275.54, 94.64) * mm, "end": v(275.4, 95) * mm});
            skLineSegment(sketch, "E2172", {"start": v(275.4, 94.3) * mm, "end": v(271.86, 90.75) * mm});
            skArc(sketch, "E2173", {"start": v(271.15, 90.75) * mm, "mid": v(271.5, 90.6) * mm, "end": v(271.86, 90.75) * mm});
            skLineSegment(sketch, "E2174", {"start": v(271.15, 90.75) * mm, "end": v(270, 91.91) * mm});
            skArc(sketch, "E2175", {"start": v(269.87, 92.4) * mm, "mid": v(269.87, 92.13) * mm, "end": v(270, 91.91) * mm});
            skArc(sketch, "E2176", {"start": v(269.87, 92.4) * mm, "mid": v(269.39, 93.02) * mm, "end": v(268.9, 92.4) * mm});
            skArc(sketch, "E2177", {"start": v(268.77, 91.91) * mm, "mid": v(268.9, 92.13) * mm, "end": v(268.9, 92.4) * mm});
            skLineSegment(sketch, "E2178", {"start": v(268.77, 91.91) * mm, "end": v(265.14, 88.28) * mm});
            skLineSegment(sketch, "E2179", {"start": v(265.14, 88.28) * mm, "end": v(263.02, 90.4) * mm});
            skLineSegment(sketch, "E2180", {"start": v(263.02, 90.4) * mm, "end": v(263.92, 91.3) * mm});
            skLineSegment(sketch, "E2181", {"start": v(259.86, 87.24) * mm, "end": v(260.76, 88.14) * mm});
            skLineSegment(sketch, "E2182", {"start": v(260.76, 88.14) * mm, "end": v(262.88, 86.02) * mm});
            skLineSegment(sketch, "E2183", {"start": v(262.88, 86.02) * mm, "end": v(259.25, 82.39) * mm});
            skArc(sketch, "E2184", {"start": v(258.77, 82.26) * mm, "mid": v(259.03, 82.26) * mm, "end": v(259.25, 82.39) * mm});
            skArc(sketch, "E2185", {"start": v(258.77, 82.26) * mm, "mid": v(258.14, 81.77) * mm, "end": v(258.77, 81.3) * mm});
            skArc(sketch, "E2186", {"start": v(259.25, 81.16) * mm, "mid": v(259.03, 81.3) * mm, "end": v(258.77, 81.3) * mm});
            skLineSegment(sketch, "E2187", {"start": v(259.25, 81.16) * mm, "end": v(260.4, 80) * mm});
            skArc(sketch, "E2188", {"start": v(260.4, 79.3) * mm, "mid": v(260.55, 79.65) * mm, "end": v(260.4, 80) * mm});
            skLineSegment(sketch, "E2189", {"start": v(260.4, 79.3) * mm, "end": v(256.87, 75.76) * mm});
            skArc(sketch, "E2190", {"start": v(256.16, 75.76) * mm, "mid": v(256.52, 75.62) * mm, "end": v(256.87, 75.76) * mm});
            skLineSegment(sketch, "E2191", {"start": v(256.16, 75.76) * mm, "end": v(255, 76.92) * mm});
            skArc(sketch, "E2192", {"start": v(254.88, 77.4) * mm, "mid": v(254.88, 77.14) * mm, "end": v(255, 76.92) * mm});
            skArc(sketch, "E2193", {"start": v(254.88, 77.4) * mm, "mid": v(254.4, 78.03) * mm, "end": v(253.91, 77.4) * mm});
            skArc(sketch, "E2194", {"start": v(253.78, 76.92) * mm, "mid": v(253.91, 77.14) * mm, "end": v(253.91, 77.4) * mm});
            skLineSegment(sketch, "E2195", {"start": v(253.78, 76.92) * mm, "end": v(247.75, 70.89) * mm});
            skLineSegment(sketch, "E2196", {"start": v(247.75, 70.89) * mm, "end": v(247.26, 71.37) * mm});
            skLineSegment(sketch, "E2197", {"start": v(263.92, 91.3) * mm, "end": v(261.1, 94.13) * mm});
            skLineSegment(sketch, "E2198", {"start": v(261.1, 94.13) * mm, "end": v(260.2, 93.23) * mm});
            skLineSegment(sketch, "E2199", {"start": v(260.2, 93.23) * mm, "end": v(258.07, 95.35) * mm});
            skLineSegment(sketch, "E2200", {"start": v(258.07, 95.35) * mm, "end": v(255.81, 93.09) * mm});
            skLineSegment(sketch, "E2201", {"start": v(255.81, 93.09) * mm, "end": v(257.93, 90.97) * mm});
            skLineSegment(sketch, "E2202", {"start": v(257.93, 90.97) * mm, "end": v(257.03, 90.07) * mm});
            skLineSegment(sketch, "E2203", {"start": v(257.03, 90.07) * mm, "end": v(259.86, 87.24) * mm});
            skArc(sketch, "E2204", {"start": v(244.92, 77.03) * mm, "mid": v(245.53, 73.97) * mm, "end": v(247.26, 71.37) * mm});
            skArc(sketch, "E2205", {"start": v(281.39, 104.52) * mm, "mid": v(281.6, 104.86) * mm, "end": v(281.68, 105.25) * mm});
            skArc(sketch, "E2206", {"start": v(247.23, 187.74) * mm, "mid": v(245.5, 185.15) * mm, "end": v(244.89, 182.09) * mm});
            skLineSegment(sketch, "E2207", {"start": v(247.23, 187.74) * mm, "end": v(247.71, 188.23) * mm});
            skLineSegment(sketch, "E2208", {"start": v(247.71, 188.23) * mm, "end": v(253.75, 182.2) * mm});
            skArc(sketch, "E2209", {"start": v(253.88, 181.71) * mm, "mid": v(253.88, 181.97) * mm, "end": v(253.75, 182.2) * mm});
            skArc(sketch, "E2210", {"start": v(253.88, 181.71) * mm, "mid": v(254.36, 181.08) * mm, "end": v(254.84, 181.71) * mm});
            skArc(sketch, "E2211", {"start": v(254.97, 182.2) * mm, "mid": v(254.84, 181.97) * mm, "end": v(254.84, 181.71) * mm});
            skLineSegment(sketch, "E2212", {"start": v(254.97, 182.2) * mm, "end": v(256.13, 183.35) * mm});
            skArc(sketch, "E2213", {"start": v(256.84, 183.35) * mm, "mid": v(256.48, 183.5) * mm, "end": v(256.13, 183.35) * mm});
            skLineSegment(sketch, "E2214", {"start": v(256.84, 183.35) * mm, "end": v(260.37, 179.82) * mm});
            skArc(sketch, "E2215", {"start": v(260.37, 179.1) * mm, "mid": v(260.52, 179.46) * mm, "end": v(260.37, 179.82) * mm});
            skLineSegment(sketch, "E2216", {"start": v(260.37, 179.1) * mm, "end": v(259.22, 177.95) * mm});
            skArc(sketch, "E2217", {"start": v(258.73, 177.82) * mm, "mid": v(259, 177.82) * mm, "end": v(259.22, 177.95) * mm});
            skArc(sketch, "E2218", {"start": v(258.73, 177.82) * mm, "mid": v(258.1, 177.34) * mm, "end": v(258.73, 176.86) * mm});
            skArc(sketch, "E2219", {"start": v(259.22, 176.73) * mm, "mid": v(259, 176.86) * mm, "end": v(258.73, 176.86) * mm});
            skLineSegment(sketch, "E2220", {"start": v(259.22, 176.73) * mm, "end": v(262.85, 173.1) * mm});
            skLineSegment(sketch, "E2221", {"start": v(262.85, 173.1) * mm, "end": v(260.72, 170.98) * mm});
            skLineSegment(sketch, "E2222", {"start": v(260.72, 170.98) * mm, "end": v(259.82, 171.88) * mm});
            skLineSegment(sketch, "E2223", {"start": v(259.82, 171.88) * mm, "end": v(257, 169.05) * mm});
            skLineSegment(sketch, "E2224", {"start": v(257, 169.05) * mm, "end": v(257.9, 168.15) * mm});
            skLineSegment(sketch, "E2225", {"start": v(257.9, 168.15) * mm, "end": v(255.78, 166.03) * mm});
            skLineSegment(sketch, "E2226", {"start": v(255.78, 166.03) * mm, "end": v(258.04, 163.76) * mm});
            skLineSegment(sketch, "E2227", {"start": v(258.04, 163.76) * mm, "end": v(260.16, 165.89) * mm});
            skLineSegment(sketch, "E2228", {"start": v(260.16, 165.89) * mm, "end": v(261.06, 164.98) * mm});
            skLineSegment(sketch, "E2229", {"start": v(261.06, 164.98) * mm, "end": v(263.89, 167.81) * mm});
            skLineSegment(sketch, "E2230", {"start": v(263.89, 167.81) * mm, "end": v(262.99, 168.71) * mm});
            skLineSegment(sketch, "E2231", {"start": v(262.99, 168.71) * mm, "end": v(265.1, 170.83) * mm});
            skLineSegment(sketch, "E2232", {"start": v(265.1, 170.83) * mm, "end": v(268.74, 167.2) * mm});
            skArc(sketch, "E2233", {"start": v(268.87, 166.72) * mm, "mid": v(268.87, 166.98) * mm, "end": v(268.74, 167.2) * mm});
            skArc(sketch, "E2234", {"start": v(268.87, 166.72) * mm, "mid": v(269.35, 166.1) * mm, "end": v(269.83, 166.72) * mm});
            skArc(sketch, "E2235", {"start": v(269.96, 167.2) * mm, "mid": v(269.83, 166.98) * mm, "end": v(269.83, 166.72) * mm});
            skLineSegment(sketch, "E2236", {"start": v(269.96, 167.2) * mm, "end": v(271.12, 168.36) * mm});
            skArc(sketch, "E2237", {"start": v(271.83, 168.36) * mm, "mid": v(271.47, 168.5) * mm, "end": v(271.12, 168.36) * mm});
            skLineSegment(sketch, "E2238", {"start": v(271.83, 168.36) * mm, "end": v(275.36, 164.82) * mm});
            skArc(sketch, "E2239", {"start": v(275.36, 164.12) * mm, "mid": v(275.5, 164.47) * mm, "end": v(275.36, 164.82) * mm});
            skLineSegment(sketch, "E2240", {"start": v(275.36, 164.12) * mm, "end": v(274.2, 162.96) * mm});
            skArc(sketch, "E2241", {"start": v(273.72, 162.83) * mm, "mid": v(273.98, 162.83) * mm, "end": v(274.2, 162.96) * mm});
            skArc(sketch, "E2242", {"start": v(273.72, 162.83) * mm, "mid": v(273.1, 162.35) * mm, "end": v(273.72, 161.87) * mm});
            skArc(sketch, "E2243", {"start": v(274.2, 161.74) * mm, "mid": v(273.98, 161.87) * mm, "end": v(273.72, 161.87) * mm});
            skLineSegment(sketch, "E2244", {"start": v(274.2, 161.74) * mm, "end": v(281.37, 154.57) * mm});
            skArc(sketch, "E2245", {"start": v(281.66, 153.89) * mm, "mid": v(281.58, 154.26) * mm, "end": v(281.37, 154.57) * mm});
            skLineSegment(sketch, "E2246", {"start": v(281.66, 153.89) * mm, "end": v(281.68, 105.25) * mm});
            skLineSegment(sketch, "E2247", {"start": v(244.89, 182.09) * mm, "end": v(244.92, 77.03) * mm});
            skCircle(sketch, "E2248", {"center": v(315.96, 117.56) * mm, "radius": 1.6 * mm});
            skCircle(sketch, "E2249", {"center": v(315.96, 141.56) * mm, "radius": 1.6 * mm});
            skArc(sketch, "E2250", {"start": v(284.96, 157.62) * mm, "mid": v(284.46, 160.15) * mm, "end": v(283.03, 162.3) * mm});
            skLineSegment(sketch, "E2251", {"start": v(284.96, 157.62) * mm, "end": v(284.96, 101.5) * mm});
            skArc(sketch, "E2252", {"start": v(283.03, 96.82) * mm, "mid": v(284.46, 98.97) * mm, "end": v(284.96, 101.5) * mm});
            skArc(sketch, "E2253", {"start": v(252.23, 193.1) * mm, "mid": v(245.03, 194.52) * mm, "end": v(240.96, 188.42) * mm});
            skArc(sketch, "E2254", {"start": v(240.96, 70.7) * mm, "mid": v(245.03, 64.6) * mm, "end": v(252.23, 66.02) * mm});
            skLineSegment(sketch, "E2255", {"start": v(283.03, 96.82) * mm, "end": v(252.23, 66.02) * mm});
            skLineSegment(sketch, "E2256", {"start": v(252.23, 193.1) * mm, "end": v(283.03, 162.3) * mm});
            skLineSegment(sketch, "E2257", {"start": v(240.96, 70.7) * mm, "end": v(240.96, 188.42) * mm});
            skLineSegment(sketch, "E2258", {"start": v(350.96, 153.97) * mm, "end": v(358.1, 161.11) * mm});
            skArc(sketch, "E2259", {"start": v(358.59, 161.24) * mm, "mid": v(358.33, 161.24) * mm, "end": v(358.1, 161.11) * mm});
            skArc(sketch, "E2260", {"start": v(358.59, 161.24) * mm, "mid": v(359.22, 161.73) * mm, "end": v(358.59, 162.2) * mm});
            skArc(sketch, "E2261", {"start": v(358.1, 162.34) * mm, "mid": v(358.33, 162.2) * mm, "end": v(358.59, 162.2) * mm});
            skLineSegment(sketch, "E2262", {"start": v(358.1, 162.34) * mm, "end": v(356.95, 163.5) * mm});
            skArc(sketch, "E2263", {"start": v(356.95, 164.2) * mm, "mid": v(356.8, 163.85) * mm, "end": v(356.95, 163.5) * mm});
            skLineSegment(sketch, "E2264", {"start": v(356.95, 164.2) * mm, "end": v(360.49, 167.74) * mm});
            skArc(sketch, "E2265", {"start": v(361.2, 167.74) * mm, "mid": v(360.84, 167.88) * mm, "end": v(360.49, 167.74) * mm});
            skLineSegment(sketch, "E2266", {"start": v(361.2, 167.74) * mm, "end": v(362.35, 166.58) * mm});
            skArc(sketch, "E2267", {"start": v(362.48, 166.1) * mm, "mid": v(362.48, 166.36) * mm, "end": v(362.35, 166.58) * mm});
            skArc(sketch, "E2268", {"start": v(362.48, 166.1) * mm, "mid": v(362.96, 165.47) * mm, "end": v(363.44, 166.1) * mm});
            skArc(sketch, "E2269", {"start": v(363.57, 166.58) * mm, "mid": v(363.44, 166.36) * mm, "end": v(363.44, 166.1) * mm});
            skLineSegment(sketch, "E2270", {"start": v(363.57, 166.58) * mm, "end": v(367.2, 170.21) * mm});
            skLineSegment(sketch, "E2271", {"start": v(367.2, 170.21) * mm, "end": v(369.32, 168.1) * mm});
            skLineSegment(sketch, "E2272", {"start": v(369.32, 168.1) * mm, "end": v(368.42, 167.19) * mm});
            skLineSegment(sketch, "E2273", {"start": v(372.49, 171.25) * mm, "end": v(371.59, 170.35) * mm});
            skLineSegment(sketch, "E2274", {"start": v(371.59, 170.35) * mm, "end": v(369.47, 172.47) * mm});
            skLineSegment(sketch, "E2275", {"start": v(369.47, 172.47) * mm, "end": v(373.1, 176.1) * mm});
            skArc(sketch, "E2276", {"start": v(373.58, 176.23) * mm, "mid": v(373.32, 176.23) * mm, "end": v(373.1, 176.1) * mm});
            skArc(sketch, "E2277", {"start": v(373.58, 176.23) * mm, "mid": v(374.2, 176.72) * mm, "end": v(373.58, 177.2) * mm});
            skArc(sketch, "E2278", {"start": v(373.1, 177.33) * mm, "mid": v(373.32, 177.2) * mm, "end": v(373.58, 177.2) * mm});
            skLineSegment(sketch, "E2279", {"start": v(373.1, 177.33) * mm, "end": v(371.94, 178.49) * mm});
            skArc(sketch, "E2280", {"start": v(371.94, 179.2) * mm, "mid": v(371.8, 178.84) * mm, "end": v(371.94, 178.49) * mm});
            skLineSegment(sketch, "E2281", {"start": v(371.94, 179.2) * mm, "end": v(375.48, 182.73) * mm});
            skArc(sketch, "E2282", {"start": v(376.18, 182.73) * mm, "mid": v(375.83, 182.87) * mm, "end": v(375.48, 182.73) * mm});
            skLineSegment(sketch, "E2283", {"start": v(376.18, 182.73) * mm, "end": v(377.34, 181.57) * mm});
            skArc(sketch, "E2284", {"start": v(377.47, 181.09) * mm, "mid": v(377.47, 181.35) * mm, "end": v(377.34, 181.57) * mm});
            skArc(sketch, "E2285", {"start": v(377.47, 181.09) * mm, "mid": v(377.95, 180.46) * mm, "end": v(378.43, 181.09) * mm});
            skArc(sketch, "E2286", {"start": v(378.56, 181.57) * mm, "mid": v(378.43, 181.35) * mm, "end": v(378.43, 181.09) * mm});
            skLineSegment(sketch, "E2287", {"start": v(378.56, 181.57) * mm, "end": v(384.6, 187.6) * mm});
            skLineSegment(sketch, "E2288", {"start": v(384.6, 187.6) * mm, "end": v(385.08, 187.12) * mm});
            skLineSegment(sketch, "E2289", {"start": v(368.42, 167.19) * mm, "end": v(371.25, 164.36) * mm});
            skLineSegment(sketch, "E2290", {"start": v(371.25, 164.36) * mm, "end": v(372.15, 165.26) * mm});
            skLineSegment(sketch, "E2291", {"start": v(372.15, 165.26) * mm, "end": v(374.27, 163.14) * mm});
            skLineSegment(sketch, "E2292", {"start": v(374.27, 163.14) * mm, "end": v(376.54, 165.4) * mm});
            skLineSegment(sketch, "E2293", {"start": v(376.54, 165.4) * mm, "end": v(374.42, 167.52) * mm});
            skLineSegment(sketch, "E2294", {"start": v(374.42, 167.52) * mm, "end": v(375.32, 168.43) * mm});
            skLineSegment(sketch, "E2295", {"start": v(375.32, 168.43) * mm, "end": v(372.49, 171.25) * mm});
            skArc(sketch, "E2296", {"start": v(387.43, 181.46) * mm, "mid": v(386.82, 184.53) * mm, "end": v(385.08, 187.12) * mm});
            skArc(sketch, "E2297", {"start": v(350.96, 153.97) * mm, "mid": v(350.74, 153.63) * mm, "end": v(350.67, 153.24) * mm});
            skArc(sketch, "E2298", {"start": v(385.12, 70.75) * mm, "mid": v(386.85, 73.34) * mm, "end": v(387.46, 76.4) * mm});
            skLineSegment(sketch, "E2299", {"start": v(385.12, 70.75) * mm, "end": v(384.63, 70.26) * mm});
            skLineSegment(sketch, "E2300", {"start": v(384.63, 70.26) * mm, "end": v(378.6, 76.3) * mm});
            skArc(sketch, "E2301", {"start": v(378.47, 76.78) * mm, "mid": v(378.47, 76.52) * mm, "end": v(378.6, 76.3) * mm});
            skArc(sketch, "E2302", {"start": v(378.47, 76.78) * mm, "mid": v(377.99, 77.4) * mm, "end": v(377.5, 76.78) * mm});
            skArc(sketch, "E2303", {"start": v(377.37, 76.3) * mm, "mid": v(377.5, 76.52) * mm, "end": v(377.5, 76.78) * mm});
            skLineSegment(sketch, "E2304", {"start": v(377.37, 76.3) * mm, "end": v(376.22, 75.14) * mm});
            skArc(sketch, "E2305", {"start": v(375.51, 75.14) * mm, "mid": v(375.87, 75) * mm, "end": v(376.22, 75.14) * mm});
            skLineSegment(sketch, "E2306", {"start": v(375.51, 75.14) * mm, "end": v(371.98, 78.68) * mm});
            skArc(sketch, "E2307", {"start": v(371.98, 79.38) * mm, "mid": v(371.83, 79.03) * mm, "end": v(371.98, 78.68) * mm});
            skLineSegment(sketch, "E2308", {"start": v(371.98, 79.38) * mm, "end": v(373.13, 80.54) * mm});
            skArc(sketch, "E2309", {"start": v(373.61, 80.67) * mm, "mid": v(373.36, 80.67) * mm, "end": v(373.13, 80.54) * mm});
            skArc(sketch, "E2310", {"start": v(373.61, 80.67) * mm, "mid": v(374.24, 81.15) * mm, "end": v(373.61, 81.63) * mm});
            skArc(sketch, "E2311", {"start": v(373.13, 81.76) * mm, "mid": v(373.36, 81.63) * mm, "end": v(373.61, 81.63) * mm});
            skLineSegment(sketch, "E2312", {"start": v(373.13, 81.76) * mm, "end": v(369.5, 85.4) * mm});
            skLineSegment(sketch, "E2313", {"start": v(369.5, 85.4) * mm, "end": v(371.62, 87.52) * mm});
            skLineSegment(sketch, "E2314", {"start": v(371.62, 87.52) * mm, "end": v(372.52, 86.61) * mm});
            skLineSegment(sketch, "E2315", {"start": v(372.52, 86.61) * mm, "end": v(375.35, 89.44) * mm});
            skLineSegment(sketch, "E2316", {"start": v(375.35, 89.44) * mm, "end": v(374.45, 90.34) * mm});
            skLineSegment(sketch, "E2317", {"start": v(374.45, 90.34) * mm, "end": v(376.57, 92.47) * mm});
            skLineSegment(sketch, "E2318", {"start": v(376.57, 92.47) * mm, "end": v(374.3, 94.73) * mm});
            skLineSegment(sketch, "E2319", {"start": v(374.3, 94.73) * mm, "end": v(372.19, 92.6) * mm});
            skLineSegment(sketch, "E2320", {"start": v(372.19, 92.6) * mm, "end": v(371.29, 93.5) * mm});
            skLineSegment(sketch, "E2321", {"start": v(371.29, 93.5) * mm, "end": v(368.46, 90.68) * mm});
            skLineSegment(sketch, "E2322", {"start": v(368.46, 90.68) * mm, "end": v(369.36, 89.78) * mm});
            skLineSegment(sketch, "E2323", {"start": v(369.36, 89.78) * mm, "end": v(367.24, 87.66) * mm});
            skLineSegment(sketch, "E2324", {"start": v(367.24, 87.66) * mm, "end": v(363.6, 91.29) * mm});
            skArc(sketch, "E2325", {"start": v(363.48, 91.77) * mm, "mid": v(363.48, 91.51) * mm, "end": v(363.6, 91.29) * mm});
            skArc(sketch, "E2326", {"start": v(363.48, 91.77) * mm, "mid": v(363, 92.4) * mm, "end": v(362.51, 91.77) * mm});
            skArc(sketch, "E2327", {"start": v(362.38, 91.29) * mm, "mid": v(362.51, 91.51) * mm, "end": v(362.51, 91.77) * mm});
            skLineSegment(sketch, "E2328", {"start": v(362.38, 91.29) * mm, "end": v(361.23, 90.13) * mm});
            skArc(sketch, "E2329", {"start": v(360.52, 90.13) * mm, "mid": v(360.87, 89.99) * mm, "end": v(361.23, 90.13) * mm});
            skLineSegment(sketch, "E2330", {"start": v(360.52, 90.13) * mm, "end": v(356.99, 93.67) * mm});
            skArc(sketch, "E2331", {"start": v(356.99, 94.37) * mm, "mid": v(356.84, 94.02) * mm, "end": v(356.99, 93.67) * mm});
            skLineSegment(sketch, "E2332", {"start": v(356.99, 94.37) * mm, "end": v(358.14, 95.53) * mm});
            skArc(sketch, "E2333", {"start": v(358.62, 95.66) * mm, "mid": v(358.36, 95.66) * mm, "end": v(358.14, 95.53) * mm});
            skArc(sketch, "E2334", {"start": v(358.62, 95.66) * mm, "mid": v(359.25, 96.14) * mm, "end": v(358.62, 96.63) * mm});
            skArc(sketch, "E2335", {"start": v(358.14, 96.75) * mm, "mid": v(358.36, 96.63) * mm, "end": v(358.62, 96.63) * mm});
            skLineSegment(sketch, "E2336", {"start": v(358.14, 96.75) * mm, "end": v(350.98, 103.92) * mm});
            skArc(sketch, "E2337", {"start": v(350.68, 104.6) * mm, "mid": v(350.76, 104.23) * mm, "end": v(350.98, 103.92) * mm});
            skLineSegment(sketch, "E2338", {"start": v(350.68, 104.6) * mm, "end": v(350.67, 153.24) * mm});
            skLineSegment(sketch, "E2339", {"start": v(387.46, 76.4) * mm, "end": v(387.43, 181.46) * mm});
            skLineSegment(sketch, "E2340", {"start": v(269.2, 235.8) * mm, "end": v(254.72, 221.31) * mm});
            skArc(sketch, "E2341", {"start": v(250.47, 219.56) * mm, "mid": v(252.77, 220.01) * mm, "end": v(254.72, 221.31) * mm});
            skArc(sketch, "E2342", {"start": v(377.2, 221.31) * mm, "mid": v(379.15, 220.01) * mm, "end": v(381.44, 219.56) * mm});
            skLineSegment(sketch, "E2343", {"start": v(377.2, 221.31) * mm, "end": v(362.72, 235.8) * mm});
            skArc(sketch, "E2344", {"start": v(362.72, 235.8) * mm, "mid": v(360.77, 237.1) * mm, "end": v(358.47, 237.56) * mm});
            skLineSegment(sketch, "E2345", {"start": v(358.47, 237.56) * mm, "end": v(341.44, 237.56) * mm});
            skArc(sketch, "E2346", {"start": v(341.44, 237.56) * mm, "mid": v(339.15, 237.1) * mm, "end": v(337.2, 235.8) * mm});
            skLineSegment(sketch, "E2347", {"start": v(337.2, 235.8) * mm, "end": v(322.72, 221.31) * mm});
            skArc(sketch, "E2348", {"start": v(318.47, 219.56) * mm, "mid": v(320.77, 220.01) * mm, "end": v(322.72, 221.31) * mm});
            skLineSegment(sketch, "E2349", {"start": v(318.47, 219.56) * mm, "end": v(313.44, 219.56) * mm});
            skArc(sketch, "E2350", {"start": v(309.2, 221.31) * mm, "mid": v(311.15, 220.01) * mm, "end": v(313.44, 219.56) * mm});
            skLineSegment(sketch, "E2351", {"start": v(309.2, 221.31) * mm, "end": v(294.72, 235.8) * mm});
            skArc(sketch, "E2352", {"start": v(294.72, 235.8) * mm, "mid": v(292.77, 237.1) * mm, "end": v(290.47, 237.56) * mm});
            skLineSegment(sketch, "E2353", {"start": v(290.47, 237.56) * mm, "end": v(273.44, 237.56) * mm});
            skArc(sketch, "E2354", {"start": v(273.44, 237.56) * mm, "mid": v(271.15, 237.1) * mm, "end": v(269.2, 235.8) * mm});
            skArc(sketch, "E2355", {"start": v(322.72, 207.8) * mm, "mid": v(320.77, 209.1) * mm, "end": v(318.47, 209.56) * mm});
            skLineSegment(sketch, "E2356", {"start": v(318.47, 209.56) * mm, "end": v(313.44, 209.56) * mm});
            skArc(sketch, "E2357", {"start": v(313.44, 209.56) * mm, "mid": v(311.15, 209.1) * mm, "end": v(309.2, 207.8) * mm});
            skLineSegment(sketch, "E2358", {"start": v(363, 218.2) * mm, "end": v(363, 210.92) * mm});
            skLineSegment(sketch, "E2359", {"start": v(269.78, 219.06) * mm, "end": v(292.14, 219.06) * mm});
            skArc(sketch, "E2360", {"start": v(292.14, 219.06) * mm, "mid": v(292.4, 219.12) * mm, "end": v(292.58, 219.3) * mm});
            skArc(sketch, "E2361", {"start": v(293.26, 218.62) * mm, "mid": v(293.36, 219.41) * mm, "end": v(292.58, 219.3) * mm});
            skArc(sketch, "E2362", {"start": v(293.26, 218.62) * mm, "mid": v(293.08, 218.44) * mm, "end": v(293, 218.2) * mm});
            skLineSegment(sketch, "E2363", {"start": v(293, 218.2) * mm, "end": v(293, 210.92) * mm});
            skArc(sketch, "E2364", {"start": v(293, 210.92) * mm, "mid": v(293.08, 210.67) * mm, "end": v(293.26, 210.5) * mm});
            skArc(sketch, "E2365", {"start": v(292.58, 209.8) * mm, "mid": v(293.36, 209.7) * mm, "end": v(293.26, 210.5) * mm});
            skArc(sketch, "E2366", {"start": v(292.58, 209.8) * mm, "mid": v(292.4, 210) * mm, "end": v(292.14, 210.06) * mm});
            skLineSegment(sketch, "E2367", {"start": v(292.14, 210.06) * mm, "end": v(269.78, 210.06) * mm});
            skArc(sketch, "E2368", {"start": v(269.78, 210.06) * mm, "mid": v(269.53, 210) * mm, "end": v(269.34, 209.8) * mm});
            skArc(sketch, "E2369", {"start": v(268.66, 210.5) * mm, "mid": v(268.56, 209.7) * mm, "end": v(269.34, 209.8) * mm});
            skArc(sketch, "E2370", {"start": v(268.66, 210.5) * mm, "mid": v(268.84, 210.67) * mm, "end": v(268.9, 210.92) * mm});
            skLineSegment(sketch, "E2371", {"start": v(268.9, 210.92) * mm, "end": v(268.9, 218.2) * mm});
            skArc(sketch, "E2372", {"start": v(268.9, 218.2) * mm, "mid": v(268.84, 218.44) * mm, "end": v(268.66, 218.62) * mm});
            skArc(sketch, "E2373", {"start": v(269.34, 219.3) * mm, "mid": v(268.56, 219.41) * mm, "end": v(268.66, 218.62) * mm});
            skArc(sketch, "E2374", {"start": v(269.34, 219.3) * mm, "mid": v(269.53, 219.12) * mm, "end": v(269.78, 219.06) * mm});
            skCircle(sketch, "E2375", {"center": v(350.96, 229.56) * mm, "radius": 1.6 * mm});
            skCircle(sketch, "E2376", {"center": v(280.96, 229.56) * mm, "radius": 1.6 * mm});
            skLineSegment(sketch, "E2377", {"start": v(339.78, 219.06) * mm, "end": v(362.14, 219.06) * mm});
            skArc(sketch, "E2378", {"start": v(362.14, 219.06) * mm, "mid": v(362.4, 219.12) * mm, "end": v(362.58, 219.3) * mm});
            skArc(sketch, "E2379", {"start": v(363.26, 218.62) * mm, "mid": v(363.36, 219.41) * mm, "end": v(362.58, 219.3) * mm});
            skArc(sketch, "E2380", {"start": v(363.26, 218.62) * mm, "mid": v(363.08, 218.44) * mm, "end": v(363, 218.2) * mm});
            skArc(sketch, "E2381", {"start": v(363, 210.92) * mm, "mid": v(363.08, 210.67) * mm, "end": v(363.26, 210.5) * mm});
            skArc(sketch, "E2382", {"start": v(362.58, 209.8) * mm, "mid": v(363.36, 209.7) * mm, "end": v(363.26, 210.5) * mm});
            skArc(sketch, "E2383", {"start": v(362.58, 209.8) * mm, "mid": v(362.4, 210) * mm, "end": v(362.14, 210.06) * mm});
            skLineSegment(sketch, "E2384", {"start": v(362.14, 210.06) * mm, "end": v(339.78, 210.06) * mm});
            skArc(sketch, "E2385", {"start": v(339.78, 210.06) * mm, "mid": v(339.53, 210) * mm, "end": v(339.34, 209.8) * mm});
            skArc(sketch, "E2386", {"start": v(338.66, 210.5) * mm, "mid": v(338.56, 209.7) * mm, "end": v(339.34, 209.8) * mm});
            skArc(sketch, "E2387", {"start": v(338.66, 210.5) * mm, "mid": v(338.84, 210.67) * mm, "end": v(338.9, 210.92) * mm});
            skLineSegment(sketch, "E2388", {"start": v(338.9, 210.92) * mm, "end": v(338.9, 218.2) * mm});
            skArc(sketch, "E2389", {"start": v(338.9, 218.2) * mm, "mid": v(338.84, 218.44) * mm, "end": v(338.66, 218.62) * mm});
            skArc(sketch, "E2390", {"start": v(339.34, 219.3) * mm, "mid": v(338.56, 219.41) * mm, "end": v(338.66, 218.62) * mm});
            skArc(sketch, "E2391", {"start": v(339.34, 219.3) * mm, "mid": v(339.53, 219.12) * mm, "end": v(339.78, 219.06) * mm});
            skLineSegment(sketch, "E2392", {"start": v(309.2, 207.8) * mm, "end": v(292.72, 191.31) * mm});
            skArc(sketch, "E2393", {"start": v(292.72, 191.31) * mm, "mid": v(291.42, 189.37) * mm, "end": v(290.96, 187.07) * mm});
            skArc(sketch, "E2394", {"start": v(340.96, 187.07) * mm, "mid": v(340.5, 189.37) * mm, "end": v(339.2, 191.31) * mm});
            skLineSegment(sketch, "E2395", {"start": v(339.2, 191.31) * mm, "end": v(322.72, 207.8) * mm});
            skCircle(sketch, "E2396", {"center": v(350.96, 199.56) * mm, "radius": 1.6 * mm});
            skCircle(sketch, "E2397", {"center": v(280.96, 199.56) * mm, "radius": 1.6 * mm});
            skLineSegment(sketch, "E2398", {"start": v(290.96, 187.07) * mm, "end": v(290.96, 172.04) * mm});
            skLineSegment(sketch, "E2399", {"start": v(340.96, 172.04) * mm, "end": v(340.96, 187.07) * mm});
            skLineSegment(sketch, "E2400", {"start": v(250.47, 219.56) * mm, "end": v(235.44, 219.56) * mm});
            skLineSegment(sketch, "E2401", {"start": v(396.47, 219.56) * mm, "end": v(381.44, 219.56) * mm});
            skArc(sketch, "E2402", {"start": v(396.47, 219.56) * mm, "mid": v(398.77, 220.01) * mm, "end": v(400.72, 221.31) * mm});
            skArc(sketch, "E2403", {"start": v(231.2, 221.31) * mm, "mid": v(233.15, 220.01) * mm, "end": v(235.44, 219.56) * mm});
            skArc(sketch, "E2404", {"start": v(430.46, 124.6) * mm, "mid": v(435.4, 129.56) * mm, "end": v(430.46, 134.5) * mm});
            skCircle(sketch, "E2405", {"center": v(430.46, 129.56) * mm, "radius": 1.6 * mm});
            skLineSegment(sketch, "E2406", {"start": v(410.96, 134.5) * mm, "end": v(430.46, 134.5) * mm});
            skLineSegment(sketch, "E2407", {"start": v(430.46, 124.6) * mm, "end": v(410.96, 124.6) * mm});
            skArc(sketch, "E2408", {"start": v(400.96, 144.5) * mm, "mid": v(403.89, 137.44) * mm, "end": v(410.96, 134.5) * mm});
            skLineSegment(sketch, "E2409", {"start": v(400.96, 54.04) * mm, "end": v(400.96, 114.6) * mm});
            skArc(sketch, "E2410", {"start": v(410.96, 124.6) * mm, "mid": v(403.89, 121.68) * mm, "end": v(400.96, 114.6) * mm});
            skArc(sketch, "E2411", {"start": v(203.47, 234.06) * mm, "mid": v(198.52, 239) * mm, "end": v(193.57, 234.06) * mm});
            skArc(sketch, "E2412", {"start": v(193.57, 25.06) * mm, "mid": v(198.52, 20.1) * mm, "end": v(203.47, 25.06) * mm});
            skCircle(sketch, "E2413", {"center": v(198.52, 25.06) * mm, "radius": 1.6 * mm});
            skCircle(sketch, "E2414", {"center": v(198.52, 234.06) * mm, "radius": 1.6 * mm});
            skArc(sketch, "E2415", {"start": v(208.52, 124.6) * mm, "mid": v(213.47, 129.56) * mm, "end": v(208.52, 134.5) * mm});
            skCircle(sketch, "E2416", {"center": v(208.52, 129.56) * mm, "radius": 1.6 * mm});
            skLineSegment(sketch, "E2417", {"start": v(203.47, 120.6) * mm, "end": v(203.47, 25.06) * mm});
            skLineSegment(sketch, "E2418", {"start": v(208.52, 124.6) * mm, "end": v(207.47, 124.6) * mm});
            skLineSegment(sketch, "E2419", {"start": v(207.47, 134.5) * mm, "end": v(208.52, 134.5) * mm});
            skLineSegment(sketch, "E2420", {"start": v(203.47, 234.06) * mm, "end": v(203.47, 138.5) * mm});
            skLineSegment(sketch, "E2421", {"start": v(193.57, 25.06) * mm, "end": v(193.57, 234.06) * mm});
            skArc(sketch, "E2422", {"start": v(203.47, 138.5) * mm, "mid": v(204.64, 135.68) * mm, "end": v(207.47, 134.5) * mm});
            skArc(sketch, "E2423", {"start": v(207.47, 124.6) * mm, "mid": v(204.64, 123.44) * mm, "end": v(203.47, 120.6) * mm});
            skLineSegment(sketch, "E2424", {"start": v(318.97, 161.28) * mm, "end": v(314.97, 161.28) * mm});
            skLineSegment(sketch, "E2425", {"start": v(314.97, 161.28) * mm, "end": v(314.97, 162.56) * mm});
            skLineSegment(sketch, "E2426", {"start": v(314.97, 162.56) * mm, "end": v(311.97, 162.56) * mm});
            skLineSegment(sketch, "E2427", {"start": v(311.97, 162.56) * mm, "end": v(311.97, 165.76) * mm});
            skLineSegment(sketch, "E2428", {"start": v(311.97, 165.76) * mm, "end": v(314.97, 165.76) * mm});
            skLineSegment(sketch, "E2429", {"start": v(314.97, 165.76) * mm, "end": v(314.97, 167.03) * mm});
            skLineSegment(sketch, "E2430", {"start": v(314.97, 167.03) * mm, "end": v(318.97, 167.03) * mm});
            skLineSegment(sketch, "E2431", {"start": v(318.97, 167.03) * mm, "end": v(318.97, 165.76) * mm});
            skLineSegment(sketch, "E2432", {"start": v(318.97, 165.76) * mm, "end": v(321.97, 165.76) * mm});
            skLineSegment(sketch, "E2433", {"start": v(321.97, 165.76) * mm, "end": v(321.97, 171.66) * mm});
            skLineSegment(sketch, "E2434", {"start": v(321.97, 171.66) * mm, "end": v(316.87, 171.66) * mm});
            skArc(sketch, "E2435", {"start": v(316.87, 186.66) * mm, "mid": v(309.37, 179.16) * mm, "end": v(316.87, 171.66) * mm});
            skLineSegment(sketch, "E2436", {"start": v(316.87, 186.66) * mm, "end": v(321.97, 186.66) * mm});
            skLineSegment(sketch, "E2437", {"start": v(321.97, 186.66) * mm, "end": v(321.97, 192.56) * mm});
            skLineSegment(sketch, "E2438", {"start": v(321.97, 192.56) * mm, "end": v(318.97, 192.56) * mm});
            skLineSegment(sketch, "E2439", {"start": v(318.97, 192.56) * mm, "end": v(318.97, 191.28) * mm});
            skLineSegment(sketch, "E2440", {"start": v(318.97, 191.28) * mm, "end": v(314.97, 191.28) * mm});
            skLineSegment(sketch, "E2441", {"start": v(314.97, 191.28) * mm, "end": v(314.97, 192.56) * mm});
            skLineSegment(sketch, "E2442", {"start": v(314.97, 192.56) * mm, "end": v(311.97, 192.56) * mm});
            skLineSegment(sketch, "E2443", {"start": v(311.97, 192.56) * mm, "end": v(311.97, 195.76) * mm});
            skLineSegment(sketch, "E2444", {"start": v(311.97, 195.76) * mm, "end": v(314.97, 195.76) * mm});
            skLineSegment(sketch, "E2445", {"start": v(314.97, 195.76) * mm, "end": v(314.97, 197.03) * mm});
            skLineSegment(sketch, "E2446", {"start": v(314.97, 197.03) * mm, "end": v(318.97, 197.03) * mm});
            skLineSegment(sketch, "E2447", {"start": v(318.97, 197.03) * mm, "end": v(318.97, 195.76) * mm});
            skLineSegment(sketch, "E2448", {"start": v(318.97, 195.76) * mm, "end": v(321.97, 195.76) * mm});
            skLineSegment(sketch, "E2449", {"start": v(321.97, 195.76) * mm, "end": v(321.97, 198.76) * mm});
            skLineSegment(sketch, "E2450", {"start": v(321.97, 198.76) * mm, "end": v(309.96, 198.76) * mm});
            skArc(sketch, "E2451", {"start": v(309.96, 198.76) * mm, "mid": v(307.84, 197.88) * mm, "end": v(306.96, 195.76) * mm});
            skLineSegment(sketch, "E2452", {"start": v(306.96, 195.76) * mm, "end": v(306.96, 162.56) * mm});
            skArc(sketch, "E2453", {"start": v(306.96, 162.56) * mm, "mid": v(307.84, 160.44) * mm, "end": v(309.96, 159.56) * mm});
            skLineSegment(sketch, "E2454", {"start": v(309.96, 159.56) * mm, "end": v(321.97, 159.56) * mm});
            skLineSegment(sketch, "E2455", {"start": v(321.97, 159.56) * mm, "end": v(321.97, 162.56) * mm});
            skLineSegment(sketch, "E2456", {"start": v(321.97, 162.56) * mm, "end": v(318.97, 162.56) * mm});
            skLineSegment(sketch, "E2457", {"start": v(318.97, 162.56) * mm, "end": v(318.97, 161.28) * mm});
            skLineSegment(sketch, "E2458", {"start": v(319.87, 61.23) * mm, "end": v(315.87, 61.23) * mm});
            skLineSegment(sketch, "E2459", {"start": v(315.87, 61.23) * mm, "end": v(315.87, 62.5) * mm});
            skLineSegment(sketch, "E2460", {"start": v(315.87, 62.5) * mm, "end": v(312.87, 62.5) * mm});
            skLineSegment(sketch, "E2461", {"start": v(312.87, 62.5) * mm, "end": v(312.87, 65.7) * mm});
            skLineSegment(sketch, "E2462", {"start": v(312.87, 65.7) * mm, "end": v(315.87, 65.7) * mm});
            skLineSegment(sketch, "E2463", {"start": v(315.87, 65.7) * mm, "end": v(315.87, 66.98) * mm});
            skLineSegment(sketch, "E2464", {"start": v(315.87, 66.98) * mm, "end": v(319.87, 66.98) * mm});
            skLineSegment(sketch, "E2465", {"start": v(319.87, 66.98) * mm, "end": v(319.87, 65.7) * mm});
            skLineSegment(sketch, "E2466", {"start": v(319.87, 65.7) * mm, "end": v(322.87, 65.7) * mm});
            skLineSegment(sketch, "E2467", {"start": v(322.87, 65.7) * mm, "end": v(322.87, 71.6) * mm});
            skLineSegment(sketch, "E2468", {"start": v(322.87, 71.6) * mm, "end": v(317.77, 71.6) * mm});
            skArc(sketch, "E2469", {"start": v(317.77, 86.6) * mm, "mid": v(310.27, 79.1) * mm, "end": v(317.77, 71.6) * mm});
            skLineSegment(sketch, "E2470", {"start": v(317.77, 86.6) * mm, "end": v(322.87, 86.6) * mm});
            skLineSegment(sketch, "E2471", {"start": v(322.87, 86.6) * mm, "end": v(322.87, 92.5) * mm});
            skLineSegment(sketch, "E2472", {"start": v(322.87, 92.5) * mm, "end": v(319.87, 92.5) * mm});
            skLineSegment(sketch, "E2473", {"start": v(319.87, 92.5) * mm, "end": v(319.87, 91.23) * mm});
            skLineSegment(sketch, "E2474", {"start": v(319.87, 91.23) * mm, "end": v(315.87, 91.23) * mm});
            skLineSegment(sketch, "E2475", {"start": v(315.87, 91.23) * mm, "end": v(315.87, 92.5) * mm});
            skLineSegment(sketch, "E2476", {"start": v(315.87, 92.5) * mm, "end": v(312.87, 92.5) * mm});
            skLineSegment(sketch, "E2477", {"start": v(312.87, 92.5) * mm, "end": v(312.87, 95.7) * mm});
            skLineSegment(sketch, "E2478", {"start": v(312.87, 95.7) * mm, "end": v(315.87, 95.7) * mm});
            skLineSegment(sketch, "E2479", {"start": v(315.87, 95.7) * mm, "end": v(315.87, 96.98) * mm});
            skLineSegment(sketch, "E2480", {"start": v(315.87, 96.98) * mm, "end": v(319.87, 96.98) * mm});
            skLineSegment(sketch, "E2481", {"start": v(319.87, 96.98) * mm, "end": v(319.87, 95.7) * mm});
            skLineSegment(sketch, "E2482", {"start": v(319.87, 95.7) * mm, "end": v(322.87, 95.7) * mm});
            skLineSegment(sketch, "E2483", {"start": v(322.87, 95.7) * mm, "end": v(322.87, 98.7) * mm});
            skLineSegment(sketch, "E2484", {"start": v(322.87, 98.7) * mm, "end": v(310.86, 98.7) * mm});
            skArc(sketch, "E2485", {"start": v(310.86, 98.7) * mm, "mid": v(308.74, 97.83) * mm, "end": v(307.86, 95.7) * mm});
            skLineSegment(sketch, "E2486", {"start": v(307.86, 95.7) * mm, "end": v(307.86, 62.5) * mm});
            skArc(sketch, "E2487", {"start": v(307.86, 62.5) * mm, "mid": v(308.74, 60.39) * mm, "end": v(310.86, 59.5) * mm});
            skLineSegment(sketch, "E2488", {"start": v(310.86, 59.5) * mm, "end": v(322.87, 59.5) * mm});
            skLineSegment(sketch, "E2489", {"start": v(322.87, 59.5) * mm, "end": v(322.87, 62.5) * mm});
            skLineSegment(sketch, "E2490", {"start": v(322.87, 62.5) * mm, "end": v(319.87, 62.5) * mm});
            skLineSegment(sketch, "E2491", {"start": v(319.87, 62.5) * mm, "end": v(319.87, 61.23) * mm});
            skLineSegment(sketch, "E2492", {"start": v(221.3, 151.46) * mm, "end": v(217.3, 151.46) * mm});
            skLineSegment(sketch, "E2493", {"start": v(217.3, 151.46) * mm, "end": v(217.3, 152.74) * mm});
            skLineSegment(sketch, "E2494", {"start": v(217.3, 152.74) * mm, "end": v(214.3, 152.74) * mm});
            skLineSegment(sketch, "E2495", {"start": v(214.3, 152.74) * mm, "end": v(214.3, 155.94) * mm});
            skLineSegment(sketch, "E2496", {"start": v(214.3, 155.94) * mm, "end": v(217.3, 155.94) * mm});
            skLineSegment(sketch, "E2497", {"start": v(217.3, 155.94) * mm, "end": v(217.3, 157.21) * mm});
            skLineSegment(sketch, "E2498", {"start": v(217.3, 157.21) * mm, "end": v(221.3, 157.21) * mm});
            skLineSegment(sketch, "E2499", {"start": v(221.3, 157.21) * mm, "end": v(221.3, 155.94) * mm});
            skLineSegment(sketch, "E2500", {"start": v(221.3, 155.94) * mm, "end": v(224.3, 155.94) * mm});
            skLineSegment(sketch, "E2501", {"start": v(224.3, 155.94) * mm, "end": v(224.3, 161.84) * mm});
            skLineSegment(sketch, "E2502", {"start": v(224.3, 161.84) * mm, "end": v(219.2, 161.84) * mm});
            skArc(sketch, "E2503", {"start": v(219.2, 176.84) * mm, "mid": v(211.7, 169.34) * mm, "end": v(219.2, 161.84) * mm});
            skLineSegment(sketch, "E2504", {"start": v(219.2, 176.84) * mm, "end": v(224.3, 176.84) * mm});
            skLineSegment(sketch, "E2505", {"start": v(224.3, 176.84) * mm, "end": v(224.3, 182.74) * mm});
            skLineSegment(sketch, "E2506", {"start": v(224.3, 182.74) * mm, "end": v(221.3, 182.74) * mm});
            skLineSegment(sketch, "E2507", {"start": v(221.3, 182.74) * mm, "end": v(221.3, 181.46) * mm});
            skLineSegment(sketch, "E2508", {"start": v(221.3, 181.46) * mm, "end": v(217.3, 181.46) * mm});
            skLineSegment(sketch, "E2509", {"start": v(217.3, 181.46) * mm, "end": v(217.3, 182.74) * mm});
            skLineSegment(sketch, "E2510", {"start": v(217.3, 182.74) * mm, "end": v(214.3, 182.74) * mm});
            skLineSegment(sketch, "E2511", {"start": v(214.3, 182.74) * mm, "end": v(214.3, 185.94) * mm});
            skLineSegment(sketch, "E2512", {"start": v(214.3, 185.94) * mm, "end": v(217.3, 185.94) * mm});
            skLineSegment(sketch, "E2513", {"start": v(217.3, 185.94) * mm, "end": v(217.3, 187.21) * mm});
            skLineSegment(sketch, "E2514", {"start": v(217.3, 187.21) * mm, "end": v(221.3, 187.21) * mm});
            skLineSegment(sketch, "E2515", {"start": v(221.3, 187.21) * mm, "end": v(221.3, 185.94) * mm});
            skLineSegment(sketch, "E2516", {"start": v(221.3, 185.94) * mm, "end": v(224.3, 185.94) * mm});
            skLineSegment(sketch, "E2517", {"start": v(224.3, 185.94) * mm, "end": v(224.3, 188.94) * mm});
            skLineSegment(sketch, "E2518", {"start": v(224.3, 188.94) * mm, "end": v(212.29, 188.94) * mm});
            skArc(sketch, "E2519", {"start": v(212.29, 188.94) * mm, "mid": v(210.16, 188.06) * mm, "end": v(209.29, 185.94) * mm});
            skLineSegment(sketch, "E2520", {"start": v(209.29, 185.94) * mm, "end": v(209.29, 152.74) * mm});
            skArc(sketch, "E2521", {"start": v(209.29, 152.74) * mm, "mid": v(210.16, 150.62) * mm, "end": v(212.29, 149.74) * mm});
            skLineSegment(sketch, "E2522", {"start": v(212.29, 149.74) * mm, "end": v(224.3, 149.74) * mm});
            skLineSegment(sketch, "E2523", {"start": v(224.3, 149.74) * mm, "end": v(224.3, 152.74) * mm});
            skLineSegment(sketch, "E2524", {"start": v(224.3, 152.74) * mm, "end": v(221.3, 152.74) * mm});
            skLineSegment(sketch, "E2525", {"start": v(221.3, 152.74) * mm, "end": v(221.3, 151.46) * mm});
            skLineSegment(sketch, "E2526", {"start": v(467.83, 215.5) * mm, "end": v(467.83, 204.97) * mm});
            skArc(sketch, "E2527", {"start": v(467.58, 204.53) * mm, "mid": v(467.76, 204.72) * mm, "end": v(467.83, 204.97) * mm});
            skArc(sketch, "E2528", {"start": v(419.83, 214.82) * mm, "mid": v(420.43, 211.75) * mm, "end": v(422.17, 209.16) * mm});
            skLineSegment(sketch, "E2529", {"start": v(419.83, 214.82) * mm, "end": v(419.83, 215.5) * mm});
            skLineSegment(sketch, "E2530", {"start": v(419.83, 215.5) * mm, "end": v(428.36, 215.5) * mm});
            skArc(sketch, "E2531", {"start": v(428.8, 215.25) * mm, "mid": v(428.6, 215.43) * mm, "end": v(428.36, 215.5) * mm});
            skArc(sketch, "E2532", {"start": v(428.8, 215.25) * mm, "mid": v(429.58, 215.15) * mm, "end": v(429.48, 215.93) * mm});
            skArc(sketch, "E2533", {"start": v(429.23, 216.37) * mm, "mid": v(429.3, 216.12) * mm, "end": v(429.48, 215.93) * mm});
            skLineSegment(sketch, "E2534", {"start": v(429.23, 216.37) * mm, "end": v(429.23, 218) * mm});
            skArc(sketch, "E2535", {"start": v(429.73, 218.5) * mm, "mid": v(429.37, 218.36) * mm, "end": v(429.23, 218) * mm});
            skLineSegment(sketch, "E2536", {"start": v(429.73, 218.5) * mm, "end": v(434.73, 218.5) * mm});
            skArc(sketch, "E2537", {"start": v(435.23, 218) * mm, "mid": v(435.08, 218.36) * mm, "end": v(434.73, 218.5) * mm});
            skLineSegment(sketch, "E2538", {"start": v(435.23, 218) * mm, "end": v(435.23, 216.37) * mm});
            skArc(sketch, "E2539", {"start": v(434.98, 215.93) * mm, "mid": v(435.16, 216.12) * mm, "end": v(435.23, 216.37) * mm});
            skArc(sketch, "E2540", {"start": v(434.98, 215.93) * mm, "mid": v(434.87, 215.15) * mm, "end": v(435.66, 215.25) * mm});
            skArc(sketch, "E2541", {"start": v(436.1, 215.5) * mm, "mid": v(435.84, 215.43) * mm, "end": v(435.66, 215.25) * mm});
            skLineSegment(sketch, "E2542", {"start": v(436.1, 215.5) * mm, "end": v(441.23, 215.5) * mm});
            skLineSegment(sketch, "E2543", {"start": v(441.23, 215.5) * mm, "end": v(441.23, 212.5) * mm});
            skLineSegment(sketch, "E2544", {"start": v(441.23, 212.5) * mm, "end": v(439.95, 212.5) * mm});
            skLineSegment(sketch, "E2545", {"start": v(439.95, 212.5) * mm, "end": v(439.95, 208.5) * mm});
            skLineSegment(sketch, "E2546", {"start": v(439.95, 208.5) * mm, "end": v(441.23, 208.5) * mm});
            skLineSegment(sketch, "E2547", {"start": v(441.23, 208.5) * mm, "end": v(441.23, 205.5) * mm});
            skLineSegment(sketch, "E2548", {"start": v(441.23, 205.5) * mm, "end": v(444.43, 205.5) * mm});
            skLineSegment(sketch, "E2549", {"start": v(444.43, 205.5) * mm, "end": v(444.43, 208.5) * mm});
            skLineSegment(sketch, "E2550", {"start": v(444.43, 208.5) * mm, "end": v(445.7, 208.5) * mm});
            skLineSegment(sketch, "E2551", {"start": v(445.7, 208.5) * mm, "end": v(445.7, 212.5) * mm});
            skLineSegment(sketch, "E2552", {"start": v(445.7, 212.5) * mm, "end": v(444.43, 212.5) * mm});
            skLineSegment(sketch, "E2553", {"start": v(444.43, 212.5) * mm, "end": v(444.43, 215.5) * mm});
            skLineSegment(sketch, "E2554", {"start": v(444.43, 215.5) * mm, "end": v(449.56, 215.5) * mm});
            skArc(sketch, "E2555", {"start": v(450, 215.25) * mm, "mid": v(449.8, 215.43) * mm, "end": v(449.56, 215.5) * mm});
            skArc(sketch, "E2556", {"start": v(450, 215.25) * mm, "mid": v(450.78, 215.15) * mm, "end": v(450.68, 215.93) * mm});
            skArc(sketch, "E2557", {"start": v(450.43, 216.37) * mm, "mid": v(450.5, 216.12) * mm, "end": v(450.68, 215.93) * mm});
            skLineSegment(sketch, "E2558", {"start": v(450.43, 216.37) * mm, "end": v(450.43, 218) * mm});
            skArc(sketch, "E2559", {"start": v(450.93, 218.5) * mm, "mid": v(450.57, 218.36) * mm, "end": v(450.43, 218) * mm});
            skLineSegment(sketch, "E2560", {"start": v(450.93, 218.5) * mm, "end": v(455.93, 218.5) * mm});
            skArc(sketch, "E2561", {"start": v(456.43, 218) * mm, "mid": v(456.28, 218.36) * mm, "end": v(455.93, 218.5) * mm});
            skLineSegment(sketch, "E2562", {"start": v(456.43, 218) * mm, "end": v(456.43, 216.37) * mm});
            skArc(sketch, "E2563", {"start": v(456.18, 215.93) * mm, "mid": v(456.36, 216.12) * mm, "end": v(456.43, 216.37) * mm});
            skArc(sketch, "E2564", {"start": v(456.18, 215.93) * mm, "mid": v(456.07, 215.15) * mm, "end": v(456.86, 215.25) * mm});
            skArc(sketch, "E2565", {"start": v(457.3, 215.5) * mm, "mid": v(457.04, 215.43) * mm, "end": v(456.86, 215.25) * mm});
            skLineSegment(sketch, "E2566", {"start": v(457.3, 215.5) * mm, "end": v(467.83, 215.5) * mm});
            skArc(sketch, "E2567", {"start": v(467.58, 204.53) * mm, "mid": v(467.47, 203.75) * mm, "end": v(468.26, 203.85) * mm});
            skArc(sketch, "E2568", {"start": v(468.7, 204.1) * mm, "mid": v(468.44, 204.03) * mm, "end": v(468.26, 203.85) * mm});
            skLineSegment(sketch, "E2569", {"start": v(468.7, 204.1) * mm, "end": v(470.33, 204.1) * mm});
            skArc(sketch, "E2570", {"start": v(470.83, 203.6) * mm, "mid": v(470.68, 203.96) * mm, "end": v(470.33, 204.1) * mm});
            skLineSegment(sketch, "E2571", {"start": v(470.83, 203.6) * mm, "end": v(470.83, 198.6) * mm});
            skArc(sketch, "E2572", {"start": v(470.33, 198.1) * mm, "mid": v(470.68, 198.25) * mm, "end": v(470.83, 198.6) * mm});
            skLineSegment(sketch, "E2573", {"start": v(470.33, 198.1) * mm, "end": v(468.7, 198.1) * mm});
            skArc(sketch, "E2574", {"start": v(468.26, 198.35) * mm, "mid": v(468.44, 198.17) * mm, "end": v(468.7, 198.1) * mm});
            skArc(sketch, "E2575", {"start": v(468.26, 198.35) * mm, "mid": v(467.47, 198.46) * mm, "end": v(467.58, 197.67) * mm});
            skArc(sketch, "E2576", {"start": v(467.83, 197.24) * mm, "mid": v(467.76, 197.49) * mm, "end": v(467.58, 197.67) * mm});
            skLineSegment(sketch, "E2577", {"start": v(467.83, 197.24) * mm, "end": v(467.83, 192.1) * mm});
            skLineSegment(sketch, "E2578", {"start": v(467.83, 192.1) * mm, "end": v(464.83, 192.1) * mm});
            skLineSegment(sketch, "E2579", {"start": v(464.83, 192.1) * mm, "end": v(464.83, 193.38) * mm});
            skLineSegment(sketch, "E2580", {"start": v(464.83, 193.38) * mm, "end": v(460.83, 193.38) * mm});
            skLineSegment(sketch, "E2581", {"start": v(460.83, 193.38) * mm, "end": v(460.83, 192.1) * mm});
            skLineSegment(sketch, "E2582", {"start": v(460.83, 192.1) * mm, "end": v(457.83, 192.1) * mm});
            skLineSegment(sketch, "E2583", {"start": v(457.83, 192.1) * mm, "end": v(457.83, 188.9) * mm});
            skLineSegment(sketch, "E2584", {"start": v(457.83, 188.9) * mm, "end": v(460.83, 188.9) * mm});
            skLineSegment(sketch, "E2585", {"start": v(460.83, 188.9) * mm, "end": v(460.83, 187.63) * mm});
            skLineSegment(sketch, "E2586", {"start": v(460.83, 187.63) * mm, "end": v(464.83, 187.63) * mm});
            skLineSegment(sketch, "E2587", {"start": v(464.83, 187.63) * mm, "end": v(464.83, 188.9) * mm});
            skLineSegment(sketch, "E2588", {"start": v(464.83, 188.9) * mm, "end": v(467.83, 188.9) * mm});
            skLineSegment(sketch, "E2589", {"start": v(467.83, 188.9) * mm, "end": v(467.83, 183.77) * mm});
            skArc(sketch, "E2590", {"start": v(467.58, 183.33) * mm, "mid": v(467.76, 183.52) * mm, "end": v(467.83, 183.77) * mm});
            skArc(sketch, "E2591", {"start": v(467.58, 183.33) * mm, "mid": v(467.47, 182.55) * mm, "end": v(468.26, 182.65) * mm});
            skArc(sketch, "E2592", {"start": v(468.7, 182.9) * mm, "mid": v(468.44, 182.83) * mm, "end": v(468.26, 182.65) * mm});
            skLineSegment(sketch, "E2593", {"start": v(468.7, 182.9) * mm, "end": v(470.33, 182.9) * mm});
            skArc(sketch, "E2594", {"start": v(470.83, 182.4) * mm, "mid": v(470.68, 182.76) * mm, "end": v(470.33, 182.9) * mm});
            skLineSegment(sketch, "E2595", {"start": v(470.83, 182.4) * mm, "end": v(470.83, 177.4) * mm});
            skArc(sketch, "E2596", {"start": v(470.33, 176.9) * mm, "mid": v(470.68, 177.05) * mm, "end": v(470.83, 177.4) * mm});
            skLineSegment(sketch, "E2597", {"start": v(470.33, 176.9) * mm, "end": v(468.7, 176.9) * mm});
            skArc(sketch, "E2598", {"start": v(468.26, 177.15) * mm, "mid": v(468.44, 176.97) * mm, "end": v(468.7, 176.9) * mm});
            skArc(sketch, "E2599", {"start": v(468.26, 177.15) * mm, "mid": v(467.47, 177.26) * mm, "end": v(467.58, 176.47) * mm});
            skArc(sketch, "E2600", {"start": v(467.83, 176.04) * mm, "mid": v(467.76, 176.29) * mm, "end": v(467.58, 176.47) * mm});
            skLineSegment(sketch, "E2601", {"start": v(467.83, 176.04) * mm, "end": v(467.83, 167.5) * mm});
            skLineSegment(sketch, "E2602", {"start": v(467.83, 167.5) * mm, "end": v(467.14, 167.5) * mm});
            skArc(sketch, "E2603", {"start": v(461.48, 169.84) * mm, "mid": v(464.08, 168.11) * mm, "end": v(467.14, 167.5) * mm});
            skLineSegment(sketch, "E2604", {"start": v(461.48, 169.84) * mm, "end": v(422.17, 209.16) * mm});
            skLineSegment(sketch, "E2605", {"start": v(466.13, 113.77) * mm, "end": v(466.13, 103.23) * mm});
            skArc(sketch, "E2606", {"start": v(465.88, 102.8) * mm, "mid": v(466.06, 102.98) * mm, "end": v(466.13, 103.23) * mm});
            skArc(sketch, "E2607", {"start": v(418.13, 113.08) * mm, "mid": v(418.74, 110.02) * mm, "end": v(420.47, 107.42) * mm});
            skLineSegment(sketch, "E2608", {"start": v(418.13, 113.08) * mm, "end": v(418.13, 113.77) * mm});
            skLineSegment(sketch, "E2609", {"start": v(418.13, 113.77) * mm, "end": v(426.66, 113.77) * mm});
            skArc(sketch, "E2610", {"start": v(427.1, 113.52) * mm, "mid": v(426.91, 113.7) * mm, "end": v(426.66, 113.77) * mm});
            skArc(sketch, "E2611", {"start": v(427.1, 113.52) * mm, "mid": v(427.88, 113.41) * mm, "end": v(427.78, 114.2) * mm});
            skArc(sketch, "E2612", {"start": v(427.53, 114.63) * mm, "mid": v(427.6, 114.38) * mm, "end": v(427.78, 114.2) * mm});
            skLineSegment(sketch, "E2613", {"start": v(427.53, 114.63) * mm, "end": v(427.53, 116.27) * mm});
            skArc(sketch, "E2614", {"start": v(428.03, 116.77) * mm, "mid": v(427.68, 116.62) * mm, "end": v(427.53, 116.27) * mm});
            skLineSegment(sketch, "E2615", {"start": v(428.03, 116.77) * mm, "end": v(433.03, 116.77) * mm});
            skArc(sketch, "E2616", {"start": v(433.53, 116.27) * mm, "mid": v(433.38, 116.62) * mm, "end": v(433.03, 116.77) * mm});
            skLineSegment(sketch, "E2617", {"start": v(433.53, 116.27) * mm, "end": v(433.53, 114.63) * mm});
            skArc(sketch, "E2618", {"start": v(433.28, 114.2) * mm, "mid": v(433.46, 114.38) * mm, "end": v(433.53, 114.63) * mm});
            skArc(sketch, "E2619", {"start": v(433.28, 114.2) * mm, "mid": v(433.18, 113.41) * mm, "end": v(433.96, 113.52) * mm});
            skArc(sketch, "E2620", {"start": v(434.4, 113.77) * mm, "mid": v(434.15, 113.7) * mm, "end": v(433.96, 113.52) * mm});
            skLineSegment(sketch, "E2621", {"start": v(434.4, 113.77) * mm, "end": v(439.53, 113.77) * mm});
            skLineSegment(sketch, "E2622", {"start": v(439.53, 113.77) * mm, "end": v(439.53, 110.77) * mm});
            skLineSegment(sketch, "E2623", {"start": v(439.53, 110.77) * mm, "end": v(438.26, 110.77) * mm});
            skLineSegment(sketch, "E2624", {"start": v(438.26, 110.77) * mm, "end": v(438.26, 106.77) * mm});
            skLineSegment(sketch, "E2625", {"start": v(438.26, 106.77) * mm, "end": v(439.53, 106.77) * mm});
            skLineSegment(sketch, "E2626", {"start": v(439.53, 106.77) * mm, "end": v(439.53, 103.77) * mm});
            skLineSegment(sketch, "E2627", {"start": v(439.53, 103.77) * mm, "end": v(442.73, 103.77) * mm});
            skLineSegment(sketch, "E2628", {"start": v(442.73, 103.77) * mm, "end": v(442.73, 106.77) * mm});
            skLineSegment(sketch, "E2629", {"start": v(442.73, 106.77) * mm, "end": v(444, 106.77) * mm});
            skLineSegment(sketch, "E2630", {"start": v(444, 106.77) * mm, "end": v(444, 110.77) * mm});
            skLineSegment(sketch, "E2631", {"start": v(444, 110.77) * mm, "end": v(442.73, 110.77) * mm});
            skLineSegment(sketch, "E2632", {"start": v(442.73, 110.77) * mm, "end": v(442.73, 113.77) * mm});
            skLineSegment(sketch, "E2633", {"start": v(442.73, 113.77) * mm, "end": v(447.86, 113.77) * mm});
            skArc(sketch, "E2634", {"start": v(448.3, 113.52) * mm, "mid": v(448.11, 113.7) * mm, "end": v(447.86, 113.77) * mm});
            skArc(sketch, "E2635", {"start": v(448.3, 113.52) * mm, "mid": v(449.08, 113.41) * mm, "end": v(448.98, 114.2) * mm});
            skArc(sketch, "E2636", {"start": v(448.73, 114.63) * mm, "mid": v(448.8, 114.38) * mm, "end": v(448.98, 114.2) * mm});
            skLineSegment(sketch, "E2637", {"start": v(448.73, 114.63) * mm, "end": v(448.73, 116.27) * mm});
            skArc(sketch, "E2638", {"start": v(449.23, 116.77) * mm, "mid": v(448.88, 116.62) * mm, "end": v(448.73, 116.27) * mm});
            skLineSegment(sketch, "E2639", {"start": v(449.23, 116.77) * mm, "end": v(454.23, 116.77) * mm});
            skArc(sketch, "E2640", {"start": v(454.73, 116.27) * mm, "mid": v(454.58, 116.62) * mm, "end": v(454.23, 116.77) * mm});
            skLineSegment(sketch, "E2641", {"start": v(454.73, 116.27) * mm, "end": v(454.73, 114.63) * mm});
            skArc(sketch, "E2642", {"start": v(454.48, 114.2) * mm, "mid": v(454.66, 114.38) * mm, "end": v(454.73, 114.63) * mm});
            skArc(sketch, "E2643", {"start": v(454.48, 114.2) * mm, "mid": v(454.38, 113.41) * mm, "end": v(455.16, 113.52) * mm});
            skArc(sketch, "E2644", {"start": v(455.6, 113.77) * mm, "mid": v(455.35, 113.7) * mm, "end": v(455.16, 113.52) * mm});
            skLineSegment(sketch, "E2645", {"start": v(455.6, 113.77) * mm, "end": v(466.13, 113.77) * mm});
            skArc(sketch, "E2646", {"start": v(465.88, 102.8) * mm, "mid": v(465.78, 102.01) * mm, "end": v(466.56, 102.12) * mm});
            skArc(sketch, "E2647", {"start": v(467, 102.37) * mm, "mid": v(466.75, 102.3) * mm, "end": v(466.56, 102.12) * mm});
            skLineSegment(sketch, "E2648", {"start": v(467, 102.37) * mm, "end": v(468.63, 102.37) * mm});
            skArc(sketch, "E2649", {"start": v(469.13, 101.87) * mm, "mid": v(468.98, 102.22) * mm, "end": v(468.63, 102.37) * mm});
            skLineSegment(sketch, "E2650", {"start": v(469.13, 101.87) * mm, "end": v(469.13, 96.87) * mm});
            skArc(sketch, "E2651", {"start": v(468.63, 96.37) * mm, "mid": v(468.98, 96.51) * mm, "end": v(469.13, 96.87) * mm});
            skLineSegment(sketch, "E2652", {"start": v(468.63, 96.37) * mm, "end": v(467, 96.37) * mm});
            skArc(sketch, "E2653", {"start": v(466.56, 96.62) * mm, "mid": v(466.75, 96.43) * mm, "end": v(467, 96.37) * mm});
            skArc(sketch, "E2654", {"start": v(466.56, 96.62) * mm, "mid": v(465.78, 96.72) * mm, "end": v(465.88, 95.93) * mm});
            skArc(sketch, "E2655", {"start": v(466.13, 95.5) * mm, "mid": v(466.06, 95.75) * mm, "end": v(465.88, 95.93) * mm});
            skLineSegment(sketch, "E2656", {"start": v(466.13, 95.5) * mm, "end": v(466.13, 90.37) * mm});
            skLineSegment(sketch, "E2657", {"start": v(466.13, 90.37) * mm, "end": v(463.13, 90.37) * mm});
            skLineSegment(sketch, "E2658", {"start": v(463.13, 90.37) * mm, "end": v(463.13, 91.64) * mm});
            skLineSegment(sketch, "E2659", {"start": v(463.13, 91.64) * mm, "end": v(459.13, 91.64) * mm});
            skLineSegment(sketch, "E2660", {"start": v(459.13, 91.64) * mm, "end": v(459.13, 90.37) * mm});
            skLineSegment(sketch, "E2661", {"start": v(459.13, 90.37) * mm, "end": v(456.13, 90.37) * mm});
            skLineSegment(sketch, "E2662", {"start": v(456.13, 90.37) * mm, "end": v(456.13, 87.17) * mm});
            skLineSegment(sketch, "E2663", {"start": v(456.13, 87.17) * mm, "end": v(459.13, 87.17) * mm});
            skLineSegment(sketch, "E2664", {"start": v(459.13, 87.17) * mm, "end": v(459.13, 85.9) * mm});
            skLineSegment(sketch, "E2665", {"start": v(459.13, 85.9) * mm, "end": v(463.13, 85.9) * mm});
            skLineSegment(sketch, "E2666", {"start": v(463.13, 85.9) * mm, "end": v(463.13, 87.17) * mm});
            skLineSegment(sketch, "E2667", {"start": v(463.13, 87.17) * mm, "end": v(466.13, 87.17) * mm});
            skLineSegment(sketch, "E2668", {"start": v(466.13, 87.17) * mm, "end": v(466.13, 82.03) * mm});
            skArc(sketch, "E2669", {"start": v(465.88, 81.6) * mm, "mid": v(466.06, 81.78) * mm, "end": v(466.13, 82.03) * mm});
            skArc(sketch, "E2670", {"start": v(465.88, 81.6) * mm, "mid": v(465.78, 80.81) * mm, "end": v(466.56, 80.92) * mm});
            skArc(sketch, "E2671", {"start": v(467, 81.17) * mm, "mid": v(466.75, 81.1) * mm, "end": v(466.56, 80.92) * mm});
            skLineSegment(sketch, "E2672", {"start": v(467, 81.17) * mm, "end": v(468.63, 81.17) * mm});
            skArc(sketch, "E2673", {"start": v(469.13, 80.67) * mm, "mid": v(468.98, 81.02) * mm, "end": v(468.63, 81.17) * mm});
            skLineSegment(sketch, "E2674", {"start": v(469.13, 80.67) * mm, "end": v(469.13, 75.67) * mm});
            skArc(sketch, "E2675", {"start": v(468.63, 75.17) * mm, "mid": v(468.98, 75.31) * mm, "end": v(469.13, 75.67) * mm});
            skLineSegment(sketch, "E2676", {"start": v(468.63, 75.17) * mm, "end": v(467, 75.17) * mm});
            skArc(sketch, "E2677", {"start": v(466.56, 75.42) * mm, "mid": v(466.75, 75.23) * mm, "end": v(467, 75.17) * mm});
            skArc(sketch, "E2678", {"start": v(466.56, 75.42) * mm, "mid": v(465.78, 75.52) * mm, "end": v(465.88, 74.73) * mm});
            skArc(sketch, "E2679", {"start": v(466.13, 74.3) * mm, "mid": v(466.06, 74.55) * mm, "end": v(465.88, 74.73) * mm});
            skLineSegment(sketch, "E2680", {"start": v(466.13, 74.3) * mm, "end": v(466.13, 65.77) * mm});
            skLineSegment(sketch, "E2681", {"start": v(466.13, 65.77) * mm, "end": v(465.44, 65.77) * mm});
            skArc(sketch, "E2682", {"start": v(459.79, 68.11) * mm, "mid": v(462.38, 66.38) * mm, "end": v(465.44, 65.77) * mm});
            skLineSegment(sketch, "E2683", {"start": v(459.79, 68.11) * mm, "end": v(420.47, 107.42) * mm});
            skLineSegment(sketch, "E2684", {"start": v(416.04, 49.07) * mm, "end": v(416.04, 59.6) * mm});
            skArc(sketch, "E2685", {"start": v(416.3, 60.04) * mm, "mid": v(416.1, 59.85) * mm, "end": v(416.04, 59.6) * mm});
            skArc(sketch, "E2686", {"start": v(416.3, 60.04) * mm, "mid": v(416.4, 60.82) * mm, "end": v(415.6, 60.72) * mm});
            skArc(sketch, "E2687", {"start": v(415.17, 60.47) * mm, "mid": v(415.42, 60.54) * mm, "end": v(415.6, 60.72) * mm});
            skLineSegment(sketch, "E2688", {"start": v(415.17, 60.47) * mm, "end": v(413.54, 60.47) * mm});
            skLineSegment(sketch, "E2689", {"start": v(413.54, 66.47) * mm, "end": v(415.17, 66.47) * mm});
            skArc(sketch, "E2690", {"start": v(415.6, 66.22) * mm, "mid": v(415.42, 66.4) * mm, "end": v(415.17, 66.47) * mm});
            skArc(sketch, "E2691", {"start": v(415.6, 66.22) * mm, "mid": v(416.4, 66.12) * mm, "end": v(416.3, 66.9) * mm});
            skArc(sketch, "E2692", {"start": v(416.04, 67.34) * mm, "mid": v(416.1, 67.09) * mm, "end": v(416.3, 66.9) * mm});
            skLineSegment(sketch, "E2693", {"start": v(416.04, 67.34) * mm, "end": v(416.04, 72.47) * mm});
            skLineSegment(sketch, "E2694", {"start": v(416.04, 72.47) * mm, "end": v(419.04, 72.47) * mm});
            skLineSegment(sketch, "E2695", {"start": v(419.04, 72.47) * mm, "end": v(419.04, 71.2) * mm});
            skLineSegment(sketch, "E2696", {"start": v(419.04, 71.2) * mm, "end": v(423.04, 71.2) * mm});
            skLineSegment(sketch, "E2697", {"start": v(423.04, 71.2) * mm, "end": v(423.04, 72.47) * mm});
            skLineSegment(sketch, "E2698", {"start": v(423.04, 72.47) * mm, "end": v(426.04, 72.47) * mm});
            skLineSegment(sketch, "E2699", {"start": v(426.04, 72.47) * mm, "end": v(426.04, 75.67) * mm});
            skLineSegment(sketch, "E2700", {"start": v(426.04, 75.67) * mm, "end": v(423.04, 75.67) * mm});
            skLineSegment(sketch, "E2701", {"start": v(423.04, 75.67) * mm, "end": v(423.04, 76.95) * mm});
            skLineSegment(sketch, "E2702", {"start": v(423.04, 76.95) * mm, "end": v(419.04, 76.95) * mm});
            skLineSegment(sketch, "E2703", {"start": v(419.04, 76.95) * mm, "end": v(419.04, 75.67) * mm});
            skLineSegment(sketch, "E2704", {"start": v(419.04, 75.67) * mm, "end": v(416.04, 75.67) * mm});
            skLineSegment(sketch, "E2705", {"start": v(416.04, 75.67) * mm, "end": v(416.04, 80.8) * mm});
            skArc(sketch, "E2706", {"start": v(416.3, 81.24) * mm, "mid": v(416.1, 81.05) * mm, "end": v(416.04, 80.8) * mm});
            skArc(sketch, "E2707", {"start": v(416.3, 81.24) * mm, "mid": v(416.4, 82.02) * mm, "end": v(415.6, 81.92) * mm});
            skArc(sketch, "E2708", {"start": v(415.17, 81.67) * mm, "mid": v(415.42, 81.74) * mm, "end": v(415.6, 81.92) * mm});
            skLineSegment(sketch, "E2709", {"start": v(415.17, 81.67) * mm, "end": v(413.54, 81.67) * mm});
            skLineSegment(sketch, "E2710", {"start": v(413.54, 87.67) * mm, "end": v(415.17, 87.67) * mm});
            skArc(sketch, "E2711", {"start": v(415.6, 87.42) * mm, "mid": v(415.42, 87.6) * mm, "end": v(415.17, 87.67) * mm});
            skArc(sketch, "E2712", {"start": v(415.6, 87.42) * mm, "mid": v(416.4, 87.32) * mm, "end": v(416.3, 88.1) * mm});
            skArc(sketch, "E2713", {"start": v(416.04, 88.54) * mm, "mid": v(416.1, 88.29) * mm, "end": v(416.3, 88.1) * mm});
            skLineSegment(sketch, "E2714", {"start": v(416.04, 88.54) * mm, "end": v(416.04, 97.07) * mm});
            skLineSegment(sketch, "E2715", {"start": v(416.04, 97.07) * mm, "end": v(416.73, 97.07) * mm});
            skArc(sketch, "E2716", {"start": v(422.38, 94.73) * mm, "mid": v(419.79, 96.46) * mm, "end": v(416.73, 97.07) * mm});
            skArc(sketch, "E2717", {"start": v(433.87, 49.32) * mm, "mid": v(434.06, 49.14) * mm, "end": v(434.3, 49.07) * mm});
            skArc(sketch, "E2718", {"start": v(433.87, 49.32) * mm, "mid": v(433.09, 49.42) * mm, "end": v(433.2, 48.64) * mm});
            skArc(sketch, "E2719", {"start": v(433.44, 48.2) * mm, "mid": v(433.37, 48.45) * mm, "end": v(433.2, 48.64) * mm});
            skLineSegment(sketch, "E2720", {"start": v(433.44, 48.2) * mm, "end": v(433.44, 46.57) * mm});
            skArc(sketch, "E2721", {"start": v(432.94, 46.07) * mm, "mid": v(433.3, 46.22) * mm, "end": v(433.44, 46.57) * mm});
            skLineSegment(sketch, "E2722", {"start": v(432.94, 46.07) * mm, "end": v(427.94, 46.07) * mm});
            skArc(sketch, "E2723", {"start": v(427.44, 46.57) * mm, "mid": v(427.59, 46.22) * mm, "end": v(427.94, 46.07) * mm});
            skLineSegment(sketch, "E2724", {"start": v(427.44, 46.57) * mm, "end": v(427.44, 48.2) * mm});
            skArc(sketch, "E2725", {"start": v(427.7, 48.64) * mm, "mid": v(427.5, 48.45) * mm, "end": v(427.44, 48.2) * mm});
            skArc(sketch, "E2726", {"start": v(427.7, 48.64) * mm, "mid": v(427.8, 49.42) * mm, "end": v(427, 49.32) * mm});
            skArc(sketch, "E2727", {"start": v(426.57, 49.07) * mm, "mid": v(426.82, 49.14) * mm, "end": v(427, 49.32) * mm});
            skLineSegment(sketch, "E2728", {"start": v(426.57, 49.07) * mm, "end": v(416.04, 49.07) * mm});
            skArc(sketch, "E2729", {"start": v(413.04, 60.97) * mm, "mid": v(413.19, 60.62) * mm, "end": v(413.54, 60.47) * mm});
            skLineSegment(sketch, "E2730", {"start": v(413.04, 60.97) * mm, "end": v(413.04, 65.97) * mm});
            skArc(sketch, "E2731", {"start": v(413.54, 66.47) * mm, "mid": v(413.19, 66.32) * mm, "end": v(413.04, 65.97) * mm});
            skArc(sketch, "E2732", {"start": v(413.04, 82.17) * mm, "mid": v(413.19, 81.82) * mm, "end": v(413.54, 81.67) * mm});
            skLineSegment(sketch, "E2733", {"start": v(413.04, 82.17) * mm, "end": v(413.04, 87.17) * mm});
            skArc(sketch, "E2734", {"start": v(413.54, 87.67) * mm, "mid": v(413.19, 87.52) * mm, "end": v(413.04, 87.17) * mm});
            skArc(sketch, "E2735", {"start": v(464.04, 49.76) * mm, "mid": v(463.43, 52.82) * mm, "end": v(461.7, 55.41) * mm});
            skLineSegment(sketch, "E2736", {"start": v(464.04, 49.76) * mm, "end": v(464.04, 49.07) * mm});
            skLineSegment(sketch, "E2737", {"start": v(464.04, 49.07) * mm, "end": v(455.5, 49.07) * mm});
            skArc(sketch, "E2738", {"start": v(455.07, 49.32) * mm, "mid": v(455.26, 49.14) * mm, "end": v(455.5, 49.07) * mm});
            skArc(sketch, "E2739", {"start": v(455.07, 49.32) * mm, "mid": v(454.29, 49.42) * mm, "end": v(454.4, 48.64) * mm});
            skArc(sketch, "E2740", {"start": v(454.64, 48.2) * mm, "mid": v(454.57, 48.45) * mm, "end": v(454.4, 48.64) * mm});
            skLineSegment(sketch, "E2741", {"start": v(454.64, 48.2) * mm, "end": v(454.64, 46.57) * mm});
            skArc(sketch, "E2742", {"start": v(454.14, 46.07) * mm, "mid": v(454.5, 46.22) * mm, "end": v(454.64, 46.57) * mm});
            skLineSegment(sketch, "E2743", {"start": v(454.14, 46.07) * mm, "end": v(449.14, 46.07) * mm});
            skArc(sketch, "E2744", {"start": v(448.64, 46.57) * mm, "mid": v(448.79, 46.22) * mm, "end": v(449.14, 46.07) * mm});
            skLineSegment(sketch, "E2745", {"start": v(448.64, 46.57) * mm, "end": v(448.64, 48.2) * mm});
            skArc(sketch, "E2746", {"start": v(448.9, 48.64) * mm, "mid": v(448.7, 48.45) * mm, "end": v(448.64, 48.2) * mm});
            skArc(sketch, "E2747", {"start": v(448.9, 48.64) * mm, "mid": v(449, 49.42) * mm, "end": v(448.2, 49.32) * mm});
            skArc(sketch, "E2748", {"start": v(447.77, 49.07) * mm, "mid": v(448.02, 49.14) * mm, "end": v(448.2, 49.32) * mm});
            skLineSegment(sketch, "E2749", {"start": v(447.77, 49.07) * mm, "end": v(442.64, 49.07) * mm});
            skLineSegment(sketch, "E2750", {"start": v(442.64, 49.07) * mm, "end": v(442.64, 52.07) * mm});
            skLineSegment(sketch, "E2751", {"start": v(442.64, 52.07) * mm, "end": v(443.92, 52.07) * mm});
            skLineSegment(sketch, "E2752", {"start": v(443.92, 52.07) * mm, "end": v(443.92, 56.07) * mm});
            skLineSegment(sketch, "E2753", {"start": v(443.92, 56.07) * mm, "end": v(442.64, 56.07) * mm});
            skLineSegment(sketch, "E2754", {"start": v(442.64, 56.07) * mm, "end": v(442.64, 59.07) * mm});
            skLineSegment(sketch, "E2755", {"start": v(442.64, 59.07) * mm, "end": v(439.44, 59.07) * mm});
            skLineSegment(sketch, "E2756", {"start": v(439.44, 59.07) * mm, "end": v(439.44, 56.07) * mm});
            skLineSegment(sketch, "E2757", {"start": v(439.44, 56.07) * mm, "end": v(438.17, 56.07) * mm});
            skLineSegment(sketch, "E2758", {"start": v(438.17, 56.07) * mm, "end": v(438.17, 52.07) * mm});
            skLineSegment(sketch, "E2759", {"start": v(438.17, 52.07) * mm, "end": v(439.44, 52.07) * mm});
            skLineSegment(sketch, "E2760", {"start": v(439.44, 52.07) * mm, "end": v(439.44, 49.07) * mm});
            skLineSegment(sketch, "E2761", {"start": v(439.44, 49.07) * mm, "end": v(434.3, 49.07) * mm});
            skLineSegment(sketch, "E2762", {"start": v(422.38, 94.73) * mm, "end": v(461.7, 55.41) * mm});
            skLineSegment(sketch, "E2763", {"start": v(414.68, 152.16) * mm, "end": v(414.68, 162.7) * mm});
            skArc(sketch, "E2764", {"start": v(414.93, 163.13) * mm, "mid": v(414.75, 162.94) * mm, "end": v(414.68, 162.7) * mm});
            skArc(sketch, "E2765", {"start": v(414.93, 163.13) * mm, "mid": v(415.04, 163.91) * mm, "end": v(414.25, 163.81) * mm});
            skArc(sketch, "E2766", {"start": v(413.82, 163.56) * mm, "mid": v(414.07, 163.63) * mm, "end": v(414.25, 163.81) * mm});
            skLineSegment(sketch, "E2767", {"start": v(413.82, 163.56) * mm, "end": v(412.18, 163.56) * mm});
            skLineSegment(sketch, "E2768", {"start": v(412.18, 169.56) * mm, "end": v(413.82, 169.56) * mm});
            skArc(sketch, "E2769", {"start": v(414.25, 169.31) * mm, "mid": v(414.07, 169.5) * mm, "end": v(413.82, 169.56) * mm});
            skArc(sketch, "E2770", {"start": v(414.25, 169.31) * mm, "mid": v(415.04, 169.2) * mm, "end": v(414.93, 170) * mm});
            skArc(sketch, "E2771", {"start": v(414.68, 170.43) * mm, "mid": v(414.75, 170.18) * mm, "end": v(414.93, 170) * mm});
            skLineSegment(sketch, "E2772", {"start": v(414.68, 170.43) * mm, "end": v(414.68, 175.56) * mm});
            skLineSegment(sketch, "E2773", {"start": v(414.68, 175.56) * mm, "end": v(417.68, 175.56) * mm});
            skLineSegment(sketch, "E2774", {"start": v(417.68, 175.56) * mm, "end": v(417.68, 174.29) * mm});
            skLineSegment(sketch, "E2775", {"start": v(417.68, 174.29) * mm, "end": v(421.68, 174.29) * mm});
            skLineSegment(sketch, "E2776", {"start": v(421.68, 174.29) * mm, "end": v(421.68, 175.56) * mm});
            skLineSegment(sketch, "E2777", {"start": v(421.68, 175.56) * mm, "end": v(424.68, 175.56) * mm});
            skLineSegment(sketch, "E2778", {"start": v(424.68, 175.56) * mm, "end": v(424.68, 178.76) * mm});
            skLineSegment(sketch, "E2779", {"start": v(424.68, 178.76) * mm, "end": v(421.68, 178.76) * mm});
            skLineSegment(sketch, "E2780", {"start": v(421.68, 178.76) * mm, "end": v(421.68, 180.04) * mm});
            skLineSegment(sketch, "E2781", {"start": v(421.68, 180.04) * mm, "end": v(417.68, 180.04) * mm});
            skLineSegment(sketch, "E2782", {"start": v(417.68, 180.04) * mm, "end": v(417.68, 178.76) * mm});
            skLineSegment(sketch, "E2783", {"start": v(417.68, 178.76) * mm, "end": v(414.68, 178.76) * mm});
            skLineSegment(sketch, "E2784", {"start": v(414.68, 178.76) * mm, "end": v(414.68, 183.9) * mm});
            skArc(sketch, "E2785", {"start": v(414.93, 184.33) * mm, "mid": v(414.75, 184.14) * mm, "end": v(414.68, 183.9) * mm});
            skArc(sketch, "E2786", {"start": v(414.93, 184.33) * mm, "mid": v(415.04, 185.11) * mm, "end": v(414.25, 185.01) * mm});
            skArc(sketch, "E2787", {"start": v(413.82, 184.76) * mm, "mid": v(414.07, 184.83) * mm, "end": v(414.25, 185.01) * mm});
            skLineSegment(sketch, "E2788", {"start": v(413.82, 184.76) * mm, "end": v(412.18, 184.76) * mm});
            skLineSegment(sketch, "E2789", {"start": v(412.18, 190.76) * mm, "end": v(413.82, 190.76) * mm});
            skArc(sketch, "E2790", {"start": v(414.25, 190.51) * mm, "mid": v(414.07, 190.7) * mm, "end": v(413.82, 190.76) * mm});
            skArc(sketch, "E2791", {"start": v(414.25, 190.51) * mm, "mid": v(415.04, 190.4) * mm, "end": v(414.93, 191.2) * mm});
            skArc(sketch, "E2792", {"start": v(414.68, 191.63) * mm, "mid": v(414.75, 191.38) * mm, "end": v(414.93, 191.2) * mm});
            skLineSegment(sketch, "E2793", {"start": v(414.68, 191.63) * mm, "end": v(414.68, 200.16) * mm});
            skLineSegment(sketch, "E2794", {"start": v(414.68, 200.16) * mm, "end": v(415.37, 200.16) * mm});
            skArc(sketch, "E2795", {"start": v(421.03, 197.82) * mm, "mid": v(418.43, 199.55) * mm, "end": v(415.37, 200.16) * mm});
            skArc(sketch, "E2796", {"start": v(432.52, 152.41) * mm, "mid": v(432.7, 152.23) * mm, "end": v(432.95, 152.16) * mm});
            skArc(sketch, "E2797", {"start": v(432.52, 152.41) * mm, "mid": v(431.73, 152.51) * mm, "end": v(431.83, 151.73) * mm});
            skArc(sketch, "E2798", {"start": v(432.08, 151.3) * mm, "mid": v(432.02, 151.54) * mm, "end": v(431.83, 151.73) * mm});
            skLineSegment(sketch, "E2799", {"start": v(432.08, 151.3) * mm, "end": v(432.08, 149.66) * mm});
            skArc(sketch, "E2800", {"start": v(431.58, 149.16) * mm, "mid": v(431.94, 149.3) * mm, "end": v(432.08, 149.66) * mm});
            skLineSegment(sketch, "E2801", {"start": v(431.58, 149.16) * mm, "end": v(426.58, 149.16) * mm});
            skArc(sketch, "E2802", {"start": v(426.08, 149.66) * mm, "mid": v(426.23, 149.3) * mm, "end": v(426.58, 149.16) * mm});
            skLineSegment(sketch, "E2803", {"start": v(426.08, 149.66) * mm, "end": v(426.08, 151.3) * mm});
            skArc(sketch, "E2804", {"start": v(426.33, 151.73) * mm, "mid": v(426.15, 151.54) * mm, "end": v(426.08, 151.3) * mm});
            skArc(sketch, "E2805", {"start": v(426.33, 151.73) * mm, "mid": v(426.44, 152.51) * mm, "end": v(425.65, 152.41) * mm});
            skArc(sketch, "E2806", {"start": v(425.22, 152.16) * mm, "mid": v(425.47, 152.23) * mm, "end": v(425.65, 152.41) * mm});
            skLineSegment(sketch, "E2807", {"start": v(425.22, 152.16) * mm, "end": v(414.68, 152.16) * mm});
            skArc(sketch, "E2808", {"start": v(411.68, 164.06) * mm, "mid": v(411.83, 163.7) * mm, "end": v(412.18, 163.56) * mm});
            skLineSegment(sketch, "E2809", {"start": v(411.68, 164.06) * mm, "end": v(411.68, 169.06) * mm});
            skArc(sketch, "E2810", {"start": v(412.18, 169.56) * mm, "mid": v(411.83, 169.41) * mm, "end": v(411.68, 169.06) * mm});
            skArc(sketch, "E2811", {"start": v(411.68, 185.26) * mm, "mid": v(411.83, 184.9) * mm, "end": v(412.18, 184.76) * mm});
            skLineSegment(sketch, "E2812", {"start": v(411.68, 185.26) * mm, "end": v(411.68, 190.26) * mm});
            skArc(sketch, "E2813", {"start": v(412.18, 190.76) * mm, "mid": v(411.83, 190.61) * mm, "end": v(411.68, 190.26) * mm});
            skArc(sketch, "E2814", {"start": v(462.68, 152.85) * mm, "mid": v(462.08, 155.9) * mm, "end": v(460.34, 158.5) * mm});
            skLineSegment(sketch, "E2815", {"start": v(462.68, 152.85) * mm, "end": v(462.68, 152.16) * mm});
            skLineSegment(sketch, "E2816", {"start": v(462.68, 152.16) * mm, "end": v(454.15, 152.16) * mm});
            skArc(sketch, "E2817", {"start": v(453.72, 152.41) * mm, "mid": v(453.9, 152.23) * mm, "end": v(454.15, 152.16) * mm});
            skArc(sketch, "E2818", {"start": v(453.72, 152.41) * mm, "mid": v(452.93, 152.51) * mm, "end": v(453.03, 151.73) * mm});
            skArc(sketch, "E2819", {"start": v(453.28, 151.3) * mm, "mid": v(453.22, 151.54) * mm, "end": v(453.03, 151.73) * mm});
            skLineSegment(sketch, "E2820", {"start": v(453.28, 151.3) * mm, "end": v(453.28, 149.66) * mm});
            skArc(sketch, "E2821", {"start": v(452.78, 149.16) * mm, "mid": v(453.14, 149.3) * mm, "end": v(453.28, 149.66) * mm});
            skLineSegment(sketch, "E2822", {"start": v(452.78, 149.16) * mm, "end": v(447.78, 149.16) * mm});
            skArc(sketch, "E2823", {"start": v(447.28, 149.66) * mm, "mid": v(447.43, 149.3) * mm, "end": v(447.78, 149.16) * mm});
            skLineSegment(sketch, "E2824", {"start": v(447.28, 149.66) * mm, "end": v(447.28, 151.3) * mm});
            skArc(sketch, "E2825", {"start": v(447.53, 151.73) * mm, "mid": v(447.35, 151.54) * mm, "end": v(447.28, 151.3) * mm});
            skArc(sketch, "E2826", {"start": v(447.53, 151.73) * mm, "mid": v(447.64, 152.51) * mm, "end": v(446.85, 152.41) * mm});
            skArc(sketch, "E2827", {"start": v(446.42, 152.16) * mm, "mid": v(446.67, 152.23) * mm, "end": v(446.85, 152.41) * mm});
            skLineSegment(sketch, "E2828", {"start": v(446.42, 152.16) * mm, "end": v(441.28, 152.16) * mm});
            skLineSegment(sketch, "E2829", {"start": v(441.28, 152.16) * mm, "end": v(441.28, 155.16) * mm});
            skLineSegment(sketch, "E2830", {"start": v(441.28, 155.16) * mm, "end": v(442.56, 155.16) * mm});
            skLineSegment(sketch, "E2831", {"start": v(442.56, 155.16) * mm, "end": v(442.56, 159.16) * mm});
            skLineSegment(sketch, "E2832", {"start": v(442.56, 159.16) * mm, "end": v(441.28, 159.16) * mm});
            skLineSegment(sketch, "E2833", {"start": v(441.28, 159.16) * mm, "end": v(441.28, 162.16) * mm});
            skLineSegment(sketch, "E2834", {"start": v(441.28, 162.16) * mm, "end": v(438.08, 162.16) * mm});
            skLineSegment(sketch, "E2835", {"start": v(438.08, 162.16) * mm, "end": v(438.08, 159.16) * mm});
            skLineSegment(sketch, "E2836", {"start": v(438.08, 159.16) * mm, "end": v(436.8, 159.16) * mm});
            skLineSegment(sketch, "E2837", {"start": v(436.8, 159.16) * mm, "end": v(436.8, 155.16) * mm});
            skLineSegment(sketch, "E2838", {"start": v(436.8, 155.16) * mm, "end": v(438.08, 155.16) * mm});
            skLineSegment(sketch, "E2839", {"start": v(438.08, 155.16) * mm, "end": v(438.08, 152.16) * mm});
            skLineSegment(sketch, "E2840", {"start": v(438.08, 152.16) * mm, "end": v(432.95, 152.16) * mm});
            skLineSegment(sketch, "E2841", {"start": v(421.03, 197.82) * mm, "end": v(460.34, 158.5) * mm});
            skLineSegment(sketch, "E2842", {"start": v(221.3, 66.98) * mm, "end": v(217.3, 66.98) * mm});
            skLineSegment(sketch, "E2843", {"start": v(217.3, 66.98) * mm, "end": v(217.3, 68.26) * mm});
            skLineSegment(sketch, "E2844", {"start": v(217.3, 68.26) * mm, "end": v(214.3, 68.26) * mm});
            skLineSegment(sketch, "E2845", {"start": v(214.3, 68.26) * mm, "end": v(214.3, 71.46) * mm});
            skLineSegment(sketch, "E2846", {"start": v(214.3, 71.46) * mm, "end": v(217.3, 71.46) * mm});
            skLineSegment(sketch, "E2847", {"start": v(217.3, 71.46) * mm, "end": v(217.3, 72.73) * mm});
            skLineSegment(sketch, "E2848", {"start": v(217.3, 72.73) * mm, "end": v(221.3, 72.73) * mm});
            skLineSegment(sketch, "E2849", {"start": v(221.3, 72.73) * mm, "end": v(221.3, 71.46) * mm});
            skLineSegment(sketch, "E2850", {"start": v(221.3, 71.46) * mm, "end": v(224.3, 71.46) * mm});
            skLineSegment(sketch, "E2851", {"start": v(224.3, 71.46) * mm, "end": v(224.3, 77.36) * mm});
            skLineSegment(sketch, "E2852", {"start": v(224.3, 77.36) * mm, "end": v(219.2, 77.36) * mm});
            skArc(sketch, "E2853", {"start": v(219.2, 92.36) * mm, "mid": v(211.7, 84.86) * mm, "end": v(219.2, 77.36) * mm});
            skLineSegment(sketch, "E2854", {"start": v(219.2, 92.36) * mm, "end": v(224.3, 92.36) * mm});
            skLineSegment(sketch, "E2855", {"start": v(224.3, 92.36) * mm, "end": v(224.3, 98.26) * mm});
            skLineSegment(sketch, "E2856", {"start": v(224.3, 98.26) * mm, "end": v(221.3, 98.26) * mm});
            skLineSegment(sketch, "E2857", {"start": v(221.3, 98.26) * mm, "end": v(221.3, 96.98) * mm});
            skLineSegment(sketch, "E2858", {"start": v(221.3, 96.98) * mm, "end": v(217.3, 96.98) * mm});
            skLineSegment(sketch, "E2859", {"start": v(217.3, 96.98) * mm, "end": v(217.3, 98.26) * mm});
            skLineSegment(sketch, "E2860", {"start": v(217.3, 98.26) * mm, "end": v(214.3, 98.26) * mm});
            skLineSegment(sketch, "E2861", {"start": v(214.3, 98.26) * mm, "end": v(214.3, 101.46) * mm});
            skLineSegment(sketch, "E2862", {"start": v(214.3, 101.46) * mm, "end": v(217.3, 101.46) * mm});
            skLineSegment(sketch, "E2863", {"start": v(217.3, 101.46) * mm, "end": v(217.3, 102.73) * mm});
            skLineSegment(sketch, "E2864", {"start": v(217.3, 102.73) * mm, "end": v(221.3, 102.73) * mm});
            skLineSegment(sketch, "E2865", {"start": v(221.3, 102.73) * mm, "end": v(221.3, 101.46) * mm});
            skLineSegment(sketch, "E2866", {"start": v(221.3, 101.46) * mm, "end": v(224.3, 101.46) * mm});
            skLineSegment(sketch, "E2867", {"start": v(224.3, 101.46) * mm, "end": v(224.3, 104.46) * mm});
            skLineSegment(sketch, "E2868", {"start": v(224.3, 104.46) * mm, "end": v(212.29, 104.46) * mm});
            skArc(sketch, "E2869", {"start": v(212.29, 104.46) * mm, "mid": v(210.16, 103.58) * mm, "end": v(209.29, 101.46) * mm});
            skLineSegment(sketch, "E2870", {"start": v(209.29, 101.46) * mm, "end": v(209.29, 68.26) * mm});
            skArc(sketch, "E2871", {"start": v(209.29, 68.26) * mm, "mid": v(210.16, 66.14) * mm, "end": v(212.29, 65.26) * mm});
            skLineSegment(sketch, "E2872", {"start": v(212.29, 65.26) * mm, "end": v(224.3, 65.26) * mm});
            skLineSegment(sketch, "E2873", {"start": v(224.3, 65.26) * mm, "end": v(224.3, 68.26) * mm});
            skLineSegment(sketch, "E2874", {"start": v(224.3, 68.26) * mm, "end": v(221.3, 68.26) * mm});
            skLineSegment(sketch, "E2875", {"start": v(221.3, 68.26) * mm, "end": v(221.3, 66.98) * mm});
            skLineSegment(sketch, "E2876", {"start": v(-101.79, 311.48) * mm, "end": v(-99.78, 311.48) * mm});
            skLineSegment(sketch, "E2877", {"start": v(-96.25, 273.48) * mm, "end": v(-94.4, 273.48) * mm});
            skLineSegment(sketch, "E2878", {"start": v(-94.4, 273.48) * mm, "end": v(-94.26, 273.48) * mm});
            skLineSegment(sketch, "E2879", {"start": v(-94.26, 273.48) * mm, "end": v(-94.25, 273.48) * mm});
            skLineSegment(sketch, "E2880", {"start": v(-32.67, -32.79) * mm, "end": v(-32.67, -29.59) * mm});
            skLineSegment(sketch, "E2881", {"start": v(-32.67, -29.59) * mm, "end": v(-29.67, -29.59) * mm});
            skLineSegment(sketch, "E2882", {"start": v(-29.67, -29.59) * mm, "end": v(-29.67, -28.31) * mm});
            skLineSegment(sketch, "E2883", {"start": v(-29.67, -28.31) * mm, "end": v(-25.67, -28.31) * mm});
            skLineSegment(sketch, "E2884", {"start": v(-25.67, -28.31) * mm, "end": v(-25.67, -29.59) * mm});
            skLineSegment(sketch, "E2885", {"start": v(-25.67, -29.59) * mm, "end": v(-22.67, -29.59) * mm});
            skLineSegment(sketch, "E2886", {"start": v(-22.67, -29.59) * mm, "end": v(-22.67, -24.45) * mm});
            skArc(sketch, "E2887", {"start": v(-22.67, -24.45) * mm, "mid": v(-22.73, -24.2) * mm, "end": v(-22.92, -24.02) * mm});
            skArc(sketch, "E2888", {"start": v(-22.23, -23.34) * mm, "mid": v(-23.02, -23.23) * mm, "end": v(-22.92, -24.02) * mm});
            skArc(sketch, "E2889", {"start": v(-22.23, -23.34) * mm, "mid": v(-22.05, -23.52) * mm, "end": v(-21.8, -23.59) * mm});
            skLineSegment(sketch, "E2890", {"start": v(-21.8, -23.59) * mm, "end": v(-20.17, -23.59) * mm});
            skArc(sketch, "E2891", {"start": v(-20.17, -23.59) * mm, "mid": v(-19.81, -23.44) * mm, "end": v(-19.67, -23.09) * mm});
            skLineSegment(sketch, "E2892", {"start": v(-19.67, -23.09) * mm, "end": v(-19.67, -18.09) * mm});
            skArc(sketch, "E2893", {"start": v(-19.67, -18.09) * mm, "mid": v(-19.81, -17.73) * mm, "end": v(-20.17, -17.59) * mm});
            skLineSegment(sketch, "E2894", {"start": v(-20.17, -17.59) * mm, "end": v(-21.8, -17.59) * mm});
            skArc(sketch, "E2895", {"start": v(-21.8, -17.59) * mm, "mid": v(-22.05, -17.65) * mm, "end": v(-22.23, -17.84) * mm});
            skArc(sketch, "E2896", {"start": v(-22.92, -17.15) * mm, "mid": v(-23.02, -17.94) * mm, "end": v(-22.23, -17.84) * mm});
            skArc(sketch, "E2897", {"start": v(-22.92, -17.15) * mm, "mid": v(-22.73, -16.97) * mm, "end": v(-22.67, -16.72) * mm});
            skLineSegment(sketch, "E2898", {"start": v(-22.67, -16.72) * mm, "end": v(-22.67, -12.19) * mm});
            skLineSegment(sketch, "E2899", {"start": v(-22.67, -12.19) * mm, "end": v(-27.87, -12.19) * mm});
            skLineSegment(sketch, "E2900", {"start": v(-37.18, -17.19) * mm, "end": v(-68.67, -17.19) * mm});
            skArc(sketch, "E2901", {"start": v(-68.67, -17.19) * mm, "mid": v(-70.08, -17.77) * mm, "end": v(-70.67, -19.19) * mm});
            skLineSegment(sketch, "E2902", {"start": v(-70.67, -19.19) * mm, "end": v(-70.67, -53.19) * mm});
            skArc(sketch, "E2903", {"start": v(-70.67, -53.19) * mm, "mid": v(-70.08, -54.6) * mm, "end": v(-68.67, -55.19) * mm});
            skLineSegment(sketch, "E2904", {"start": v(-68.67, -55.19) * mm, "end": v(-31.64, -55.19) * mm});
            skArc(sketch, "E2905", {"start": v(-22.67, -45.65) * mm, "mid": v(-22.73, -45.4) * mm, "end": v(-22.92, -45.22) * mm});
            skArc(sketch, "E2906", {"start": v(-22.23, -44.54) * mm, "mid": v(-23.02, -44.43) * mm, "end": v(-22.92, -45.22) * mm});
            skArc(sketch, "E2907", {"start": v(-22.23, -44.54) * mm, "mid": v(-22.05, -44.72) * mm, "end": v(-21.8, -44.79) * mm});
            skLineSegment(sketch, "E2908", {"start": v(-21.8, -44.79) * mm, "end": v(-20.17, -44.79) * mm});
            skArc(sketch, "E2909", {"start": v(-20.17, -44.79) * mm, "mid": v(-19.81, -44.64) * mm, "end": v(-19.67, -44.29) * mm});
            skLineSegment(sketch, "E2910", {"start": v(-19.67, -44.29) * mm, "end": v(-19.67, -39.29) * mm});
            skArc(sketch, "E2911", {"start": v(-19.67, -39.29) * mm, "mid": v(-19.81, -38.93) * mm, "end": v(-20.17, -38.79) * mm});
            skLineSegment(sketch, "E2912", {"start": v(-20.17, -38.79) * mm, "end": v(-21.8, -38.79) * mm});
            skArc(sketch, "E2913", {"start": v(-21.8, -38.79) * mm, "mid": v(-22.05, -38.85) * mm, "end": v(-22.23, -39.04) * mm});
            skArc(sketch, "E2914", {"start": v(-22.92, -38.35) * mm, "mid": v(-23.02, -39.14) * mm, "end": v(-22.23, -39.04) * mm});
            skArc(sketch, "E2915", {"start": v(-22.92, -38.35) * mm, "mid": v(-22.73, -38.17) * mm, "end": v(-22.67, -37.92) * mm});
            skLineSegment(sketch, "E2916", {"start": v(-22.67, -37.92) * mm, "end": v(-22.67, -32.79) * mm});
            skLineSegment(sketch, "E2917", {"start": v(-22.67, -32.79) * mm, "end": v(-25.67, -32.79) * mm});
            skLineSegment(sketch, "E2918", {"start": v(-25.67, -32.79) * mm, "end": v(-25.67, -34.06) * mm});
            skLineSegment(sketch, "E2919", {"start": v(-25.67, -34.06) * mm, "end": v(-29.67, -34.06) * mm});
            skLineSegment(sketch, "E2920", {"start": v(-29.67, -34.06) * mm, "end": v(-29.67, -32.79) * mm});
            skLineSegment(sketch, "E2921", {"start": v(-29.67, -32.79) * mm, "end": v(-32.67, -32.79) * mm});
            skCircle(sketch, "E2922", {"center": v(-50.45, -36.19) * mm, "radius": 11.1 * mm});
            skCircle(sketch, "E2923", {"center": v(-34.95, -51.69) * mm, "radius": 1.6 * mm});
            skCircle(sketch, "E2924", {"center": v(-65.95, -51.69) * mm, "radius": 1.6 * mm});
            skCircle(sketch, "E2925", {"center": v(-34.95, -20.69) * mm, "radius": 1.6 * mm});
            skCircle(sketch, "E2926", {"center": v(-65.95, -20.69) * mm, "radius": 1.6 * mm});
            skLineSegment(sketch, "E2927", {"start": v(-29.04, -54.99) * mm, "end": v(-22.67, -50.19) * mm});
            skLineSegment(sketch, "E2928", {"start": v(-34.58, -16.99) * mm, "end": v(-28.47, -12.39) * mm});
            skArc(sketch, "E2929", {"start": v(-29.64, -55.19) * mm, "mid": v(-29.33, -55.14) * mm, "end": v(-29.04, -54.99) * mm});
            skArc(sketch, "E2930", {"start": v(-35.18, -17.19) * mm, "mid": v(-34.86, -17.14) * mm, "end": v(-34.58, -16.99) * mm});
            skArc(sketch, "E2931", {"start": v(-27.87, -12.19) * mm, "mid": v(-28.19, -12.24) * mm, "end": v(-28.47, -12.39) * mm});
            skLineSegment(sketch, "E2932", {"start": v(-22.67, -50.19) * mm, "end": v(-22.67, -45.65) * mm});
            skLineSegment(sketch, "E2933", {"start": v(-37.18, -17.19) * mm, "end": v(-35.17, -17.19) * mm});
            skLineSegment(sketch, "E2934", {"start": v(-31.64, -55.19) * mm, "end": v(-29.8, -55.19) * mm});
            skLineSegment(sketch, "E2935", {"start": v(-29.8, -55.19) * mm, "end": v(-29.65, -55.19) * mm});
            skLineSegment(sketch, "E2936", {"start": v(-29.65, -55.19) * mm, "end": v(-29.64, -55.19) * mm});
            skLineSegment(sketch, "E2937", {"start": v(92.55, -22.06) * mm, "end": v(92.55, -18.07) * mm});
            skLineSegment(sketch, "E2938", {"start": v(92.55, -18.06) * mm, "end": v(92.55, -18.08) * mm});
            skLineSegment(sketch, "E2939", {"start": v(119.75, -18.06) * mm, "end": v(119.75, -22.06) * mm});
            skLineSegment(sketch, "E2940", {"start": v(-273.9, 282.86) * mm, "end": v(-273.9, 278.85) * mm});
            skLineSegment(sketch, "E2941", {"start": v(-246.7, 282.81) * mm, "end": v(-246.7, 278.85) * mm});
            skLineSegment(sketch, "E2942", {"start": v(-246.7, 282.85) * mm, "end": v(-246.7, 282.81) * mm});
            skLineSegment(sketch, "E2943", {"start": v(-285.3, -58.65) * mm, "end": v(-285.3, -63.65) * mm});
            skLineSegment(sketch, "E2944", {"start": v(-240.86, -59.03) * mm, "end": v(-240.86, -63.65) * mm});
            skArc(sketch, "E2945", {"start": v(-240.5, -58.55) * mm, "mid": v(-240.76, -58.73) * mm, "end": v(-240.86, -59.03) * mm});
            skLineSegment(sketch, "E2946", {"start": v(131.15, 324.44) * mm, "end": v(131.15, 319.43) * mm});
            skLineSegment(sketch, "E2947", {"start": v(86.7, 324.44) * mm, "end": v(86.7, 319.81) * mm});
            skArc(sketch, "E2948", {"start": v(86.34, 319.33) * mm, "mid": v(86.6, 319.51) * mm, "end": v(86.7, 319.81) * mm});
            skCircle(sketch, "E2949", {"center": v(-506.73, -325.84) * mm, "radius": 1.6 * mm});
            skCircle(sketch, "E2950", {"center": v(-260.3, 229.35) * mm, "radius": 1.6 * mm});
            skCircle(sketch, "E2951", {"center": v(106.08, 31.44) * mm, "radius": 1.6 * mm});
            skSolve(sketch);
        }
        {
            var Q0;
            Q0=makeQuery(id+"F1.imprint","IMPRINT",FACE,{"disambiguationData":[TD([[makeQuery(id+"F1.imprint","IMPRINT",EDGE,{"derivedFrom":sQuery(id+"F1.wireOp",EDGE,"E1334")}),1.0]])]});
            extrude(context, id + "F2", {"entities" : qUnion([Q0]), "depth" : (getVariable(context, 'thikness')) * mm, "offsetDistance" : 25 * mm});
        }
        {
            var Q0;
            Q0=makeQuery(id+"F1.imprint","IMPRINT",FACE,{"disambiguationData":[TD([[makeQuery(id+"F1.imprint","IMPRINT",EDGE,{"derivedFrom":sQuery(id+"F1.wireOp",EDGE,"E1975")}),1.0]])]});
            extrude(context, id + "F3", {"entities" : qUnion([Q0]), "depth" : (getVariable(context, 'thikness')) * mm, "offsetDistance" : 25 * mm});
        }
        {
            var Q0;
            Q0=makeQuery(id+"F1.imprint","IMPRINT",FACE,{"disambiguationData":[TD([[makeQuery(id+"F1.imprint","IMPRINT",EDGE,{"derivedFrom":sQuery(id+"F1.wireOp",EDGE,"E0")}),1.0]])]});
            extrude(context, id + "F4", {"entities" : qUnion([Q0]), "depth" : (getVariable(context, 'thikness')) * mm, "offsetDistance" : 25 * mm});
        }
        {
            var Q0;
            Q0=makeQuery(id+"F1.imprint","IMPRINT",FACE,{"disambiguationData":[TD([[makeQuery(id+"F1.imprint","IMPRINT",EDGE,{"derivedFrom":sQuery(id+"F1.wireOp",EDGE,"E2055")}),-1.0]])]});
            extrude(context, id + "F5", {"entities" : qUnion([Q0]), "depth" : (getVariable(context, 'thikness')) * mm, "offsetDistance" : 25 * mm});
        }
        {
            var Q0;
            Q0=makeQuery(id+"F1.imprint","IMPRINT",FACE,{"disambiguationData":[TD([[makeQuery(id+"F1.imprint","IMPRINT",EDGE,{"derivedFrom":sQuery(id+"F1.wireOp",EDGE,"E899")}),1.0]])]});
            extrude(context, id + "F6", {"entities" : qUnion([Q0]), "depth" : (getVariable(context, 'thikness')) * mm, "offsetDistance" : 25 * mm});
        }
        {
            var Q0;
            Q0=makeQuery(id+"F1.imprint","IMPRINT",FACE,{"disambiguationData":[TD([[makeQuery(id+"F1.imprint","IMPRINT",EDGE,{"derivedFrom":sQuery(id+"F1.wireOp",EDGE,"E1057")}),1.0]])]});
            extrude(context, id + "F7", {"entities" : qUnion([Q0]), "depth" : (getVariable(context, 'thikness')) * mm, "offsetDistance" : 25 * mm});
        }
        {
            var Q0;
            Q0=makeQuery(id+"F1.imprint","IMPRINT",FACE,{"disambiguationData":[TD([[makeQuery(id+"F1.imprint","IMPRINT",EDGE,{"derivedFrom":sQuery(id+"F1.wireOp",EDGE,"E1567")}),1.0]])]});
            extrude(context, id + "F8", {"entities" : qUnion([Q0]), "depth" : (getVariable(context, 'thikness')) * mm, "offsetDistance" : 25 * mm});
        }
        {
            var Q0;
            Q0=makeQuery(id+"F1.imprint","IMPRINT",FACE,{"disambiguationData":[TD([[makeQuery(id+"F1.imprint","IMPRINT",EDGE,{"derivedFrom":sQuery(id+"F1.wireOp",EDGE,"E1747")}),-1.0]])]});
            extrude(context, id + "F9", {"entities" : qUnion([Q0]), "depth" : (getVariable(context, 'thikness')) * mm, "offsetDistance" : 25 * mm});
        }
        {
            var Q0;
            Q0=makeQuery(id+"F1.imprint","IMPRINT",FACE,{"disambiguationData":[TD([[makeQuery(id+"F1.imprint","IMPRINT",EDGE,{"derivedFrom":sQuery(id+"F1.wireOp",EDGE,"E2411")}),1.0]])]});
            extrude(context, id + "F10", {"entities" : qUnion([Q0]), "depth" : (getVariable(context, 'thikness')) * mm, "offsetDistance" : 25 * mm});
        }
        {
            var Q0;
            Q0=makeQuery(id+"F1.imprint","IMPRINT",FACE,{"disambiguationData":[TD([[makeQuery(id+"F1.imprint","IMPRINT",EDGE,{"derivedFrom":sQuery(id+"F1.wireOp",EDGE,"E2763")}),-1.0]])]});
            extrude(context, id + "F11", {"entities" : qUnion([Q0]), "depth" : (getVariable(context, 'thikness')) * mm, "offsetDistance" : 25 * mm});
        }
        {
            var Q0;
            Q0=makeQuery(id+"F1.imprint","IMPRINT",FACE,{"disambiguationData":[TD([[makeQuery(id+"F1.imprint","IMPRINT",EDGE,{"derivedFrom":sQuery(id+"F1.wireOp",EDGE,"E2258")}),-1.0]])]});
            extrude(context, id + "F12", {"entities" : qUnion([Q0]), "depth" : (getVariable(context, 'thikness')) * mm, "offsetDistance" : 25 * mm});
        }
        {
            var Q0;
            Q0=makeQuery(id+"F1.imprint","IMPRINT",FACE,{"disambiguationData":[TD([[makeQuery(id+"F1.imprint","IMPRINT",EDGE,{"derivedFrom":sQuery(id+"F1.wireOp",EDGE,"E2492")}),1.0]])]});
            extrude(context, id + "F13", {"entities" : qUnion([Q0]), "depth" : (getVariable(context, 'thikness')) * mm, "offsetDistance" : 25 * mm});
        }
    });
